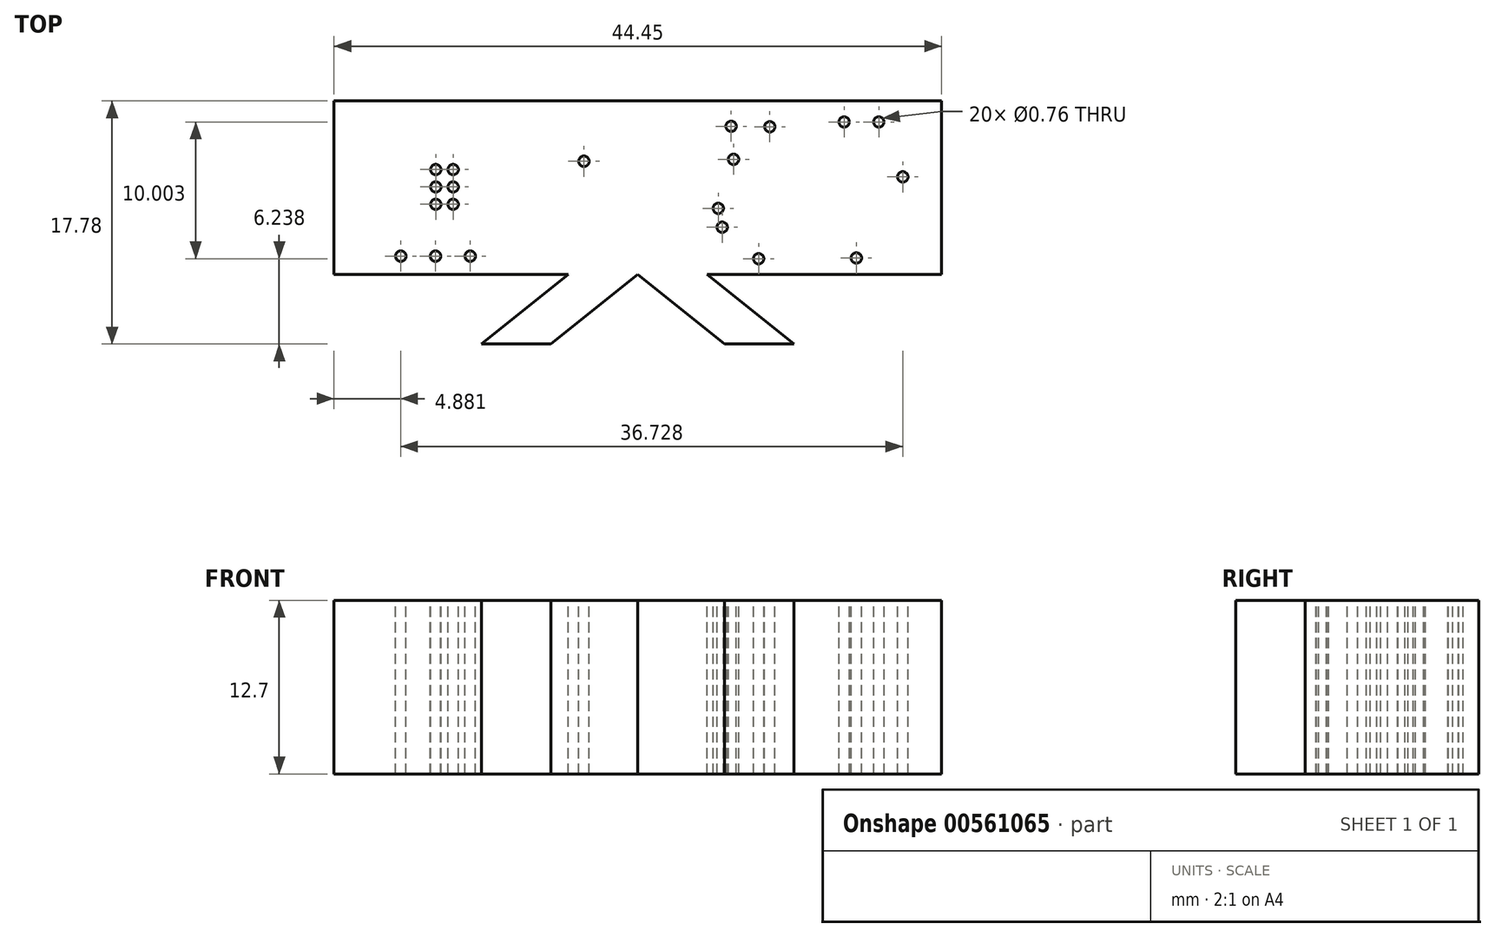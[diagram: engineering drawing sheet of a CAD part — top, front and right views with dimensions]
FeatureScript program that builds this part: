
annotation { "Feature Type Name" : "Feature", "Feature Type Description" : "" }
export const myFeature = defineFeature(function(context is Context, id is Id, definition is map)
    precondition{}
    {
        {
            var Q0;
            Q0=qCreatedBy(makeId("Top.planeOp"),FACE);
            var sketch = newSketch(context, id + "F0", { "sketchPlane" : qUnion([Q0])});
            skArc(sketch, "E0", {"start": v(-12.89, -6) * mm, "mid": v(-13.13, -5.75) * mm, "end": v(-13.37, -6) * mm});
            skArc(sketch, "E1", {"start": v(-13.37, -6) * mm, "mid": v(-13.13, -6.24) * mm, "end": v(-12.89, -6) * mm});
            skArc(sketch, "E2", {"start": v(-15.43, -6) * mm, "mid": v(-15.67, -5.75) * mm, "end": v(-15.91, -6) * mm});
            skArc(sketch, "E3", {"start": v(-15.91, -6) * mm, "mid": v(-15.67, -6.24) * mm, "end": v(-15.43, -6) * mm});
            skArc(sketch, "E4", {"start": v(-17.97, -6) * mm, "mid": v(-18.2, -5.75) * mm, "end": v(-18.45, -6) * mm});
            skArc(sketch, "E5", {"start": v(-18.45, -6) * mm, "mid": v(-18.2, -6.24) * mm, "end": v(-17.97, -6) * mm});
            skArc(sketch, "E6", {"start": v(18.76, -0.2) * mm, "mid": v(18.52, 0.05) * mm, "end": v(18.28, -0.2) * mm});
            skArc(sketch, "E7", {"start": v(18.28, -0.2) * mm, "mid": v(18.52, -0.43) * mm, "end": v(18.76, -0.2) * mm});
            skArc(sketch, "E8", {"start": v(5.26, -2.5) * mm, "mid": v(5.02, -2.26) * mm, "end": v(4.78, -2.5) * mm});
            skArc(sketch, "E9", {"start": v(4.78, -2.5) * mm, "mid": v(5.02, -2.74) * mm, "end": v(5.26, -2.5) * mm});
            skArc(sketch, "E10", {"start": v(5.54, -3.88) * mm, "mid": v(5.3, -3.63) * mm, "end": v(5.06, -3.88) * mm});
            skArc(sketch, "E11", {"start": v(5.06, -3.88) * mm, "mid": v(5.3, -4.12) * mm, "end": v(5.54, -3.88) * mm});
            skArc(sketch, "E12", {"start": v(-4.57, 0.95) * mm, "mid": v(-4.81, 1.19) * mm, "end": v(-5.05, 0.95) * mm});
            skArc(sketch, "E13", {"start": v(-5.05, 0.95) * mm, "mid": v(-4.81, 0.7) * mm, "end": v(-4.57, 0.95) * mm});
            skArc(sketch, "E14", {"start": v(6.2, 3.5) * mm, "mid": v(5.96, 3.75) * mm, "end": v(5.72, 3.5) * mm});
            skArc(sketch, "E15", {"start": v(5.72, 3.5) * mm, "mid": v(5.96, 3.27) * mm, "end": v(6.2, 3.5) * mm});
            skArc(sketch, "E16", {"start": v(9.03, 3.47) * mm, "mid": v(8.79, 3.71) * mm, "end": v(8.54, 3.47) * mm});
            skArc(sketch, "E17", {"start": v(8.54, 3.47) * mm, "mid": v(8.79, 3.23) * mm, "end": v(9.03, 3.47) * mm});
            skArc(sketch, "E18", {"start": v(6.38, 1.09) * mm, "mid": v(6.14, 1.33) * mm, "end": v(5.9, 1.09) * mm});
            skArc(sketch, "E19", {"start": v(5.9, 1.09) * mm, "mid": v(6.14, 0.85) * mm, "end": v(6.38, 1.09) * mm});
            skArc(sketch, "E20", {"start": v(28.86, -23.7) * mm, "mid": v(28.39, -23.22) * mm, "end": v(27.91, -23.7) * mm});
            skArc(sketch, "E21", {"start": v(27.91, -23.7) * mm, "mid": v(28.39, -24.17) * mm, "end": v(28.86, -23.7) * mm});
            skArc(sketch, "E22", {"start": v(26.32, -23.7) * mm, "mid": v(25.85, -23.22) * mm, "end": v(25.37, -23.7) * mm});
            skArc(sketch, "E23", {"start": v(25.37, -23.7) * mm, "mid": v(25.85, -24.17) * mm, "end": v(26.32, -23.7) * mm});
            skArc(sketch, "E24", {"start": v(23.78, -23.7) * mm, "mid": v(23.3, -23.22) * mm, "end": v(22.83, -23.7) * mm});
            skArc(sketch, "E25", {"start": v(22.83, -23.7) * mm, "mid": v(23.3, -24.17) * mm, "end": v(23.78, -23.7) * mm});
            skArc(sketch, "E26", {"start": v(21.24, -23.7) * mm, "mid": v(20.77, -23.22) * mm, "end": v(20.3, -23.7) * mm});
            skArc(sketch, "E27", {"start": v(20.3, -23.7) * mm, "mid": v(20.77, -24.17) * mm, "end": v(21.24, -23.7) * mm});
            skArc(sketch, "E28", {"start": v(18.7, -23.7) * mm, "mid": v(18.23, -23.22) * mm, "end": v(17.75, -23.7) * mm});
            skArc(sketch, "E29", {"start": v(17.75, -23.7) * mm, "mid": v(18.23, -24.17) * mm, "end": v(18.7, -23.7) * mm});
            skArc(sketch, "E30", {"start": v(16.16, -23.7) * mm, "mid": v(15.69, -23.22) * mm, "end": v(15.21, -23.7) * mm});
            skArc(sketch, "E31", {"start": v(15.21, -23.7) * mm, "mid": v(15.69, -24.17) * mm, "end": v(16.16, -23.7) * mm});
            skArc(sketch, "E32", {"start": v(13.62, -23.7) * mm, "mid": v(13.15, -23.22) * mm, "end": v(12.67, -23.7) * mm});
            skArc(sketch, "E33", {"start": v(12.67, -23.7) * mm, "mid": v(13.15, -24.17) * mm, "end": v(13.62, -23.7) * mm});
            skArc(sketch, "E34", {"start": v(11.08, -23.7) * mm, "mid": v(10.6, -23.22) * mm, "end": v(10.13, -23.7) * mm});
            skArc(sketch, "E35", {"start": v(10.13, -23.7) * mm, "mid": v(10.6, -24.17) * mm, "end": v(11.08, -23.7) * mm});
            skArc(sketch, "E36", {"start": v(8.54, -23.7) * mm, "mid": v(8.07, -23.22) * mm, "end": v(7.6, -23.7) * mm});
            skArc(sketch, "E37", {"start": v(7.6, -23.7) * mm, "mid": v(8.07, -24.17) * mm, "end": v(8.54, -23.7) * mm});
            skArc(sketch, "E38", {"start": v(6, -23.7) * mm, "mid": v(5.53, -23.22) * mm, "end": v(5.05, -23.7) * mm});
            skArc(sketch, "E39", {"start": v(5.05, -23.7) * mm, "mid": v(5.53, -24.17) * mm, "end": v(6, -23.7) * mm});
            skArc(sketch, "E40", {"start": v(3.46, -23.7) * mm, "mid": v(2.99, -23.22) * mm, "end": v(2.51, -23.7) * mm});
            skArc(sketch, "E41", {"start": v(2.51, -23.7) * mm, "mid": v(2.99, -24.17) * mm, "end": v(3.46, -23.7) * mm});
            skArc(sketch, "E42", {"start": v(0.92, -23.7) * mm, "mid": v(0.45, -23.22) * mm, "end": v(-0.03, -23.7) * mm});
            skArc(sketch, "E43", {"start": v(-0.03, -23.7) * mm, "mid": v(0.45, -24.17) * mm, "end": v(0.92, -23.7) * mm});
            skArc(sketch, "E44", {"start": v(-1.62, -23.7) * mm, "mid": v(-2.1, -23.22) * mm, "end": v(-2.57, -23.7) * mm});
            skArc(sketch, "E45", {"start": v(-2.57, -23.7) * mm, "mid": v(-2.1, -24.17) * mm, "end": v(-1.62, -23.7) * mm});
            skArc(sketch, "E46", {"start": v(-4.16, -23.7) * mm, "mid": v(-4.63, -23.22) * mm, "end": v(-5.1, -23.7) * mm});
            skArc(sketch, "E47", {"start": v(-5.1, -23.7) * mm, "mid": v(-4.63, -24.17) * mm, "end": v(-4.16, -23.7) * mm});
            skArc(sketch, "E48", {"start": v(-6.7, -23.7) * mm, "mid": v(-7.17, -23.22) * mm, "end": v(-7.65, -23.7) * mm});
            skArc(sketch, "E49", {"start": v(-7.65, -23.7) * mm, "mid": v(-7.17, -24.17) * mm, "end": v(-6.7, -23.7) * mm});
            skArc(sketch, "E50", {"start": v(-9.24, -23.7) * mm, "mid": v(-9.71, -23.22) * mm, "end": v(-10.19, -23.7) * mm});
            skArc(sketch, "E51", {"start": v(-10.19, -23.7) * mm, "mid": v(-9.71, -24.17) * mm, "end": v(-9.24, -23.7) * mm});
            skArc(sketch, "E52", {"start": v(-11.78, -23.7) * mm, "mid": v(-12.25, -23.22) * mm, "end": v(-12.73, -23.7) * mm});
            skArc(sketch, "E53", {"start": v(-12.73, -23.7) * mm, "mid": v(-12.25, -24.17) * mm, "end": v(-11.78, -23.7) * mm});
            skArc(sketch, "E54", {"start": v(-15.4, 0.34) * mm, "mid": v(-15.65, 0.58) * mm, "end": v(-15.89, 0.34) * mm});
            skArc(sketch, "E55", {"start": v(-15.89, 0.34) * mm, "mid": v(-15.65, 0.1) * mm, "end": v(-15.4, 0.34) * mm});
            skArc(sketch, "E56", {"start": v(-14.14, 0.34) * mm, "mid": v(-14.38, 0.58) * mm, "end": v(-14.62, 0.34) * mm});
            skArc(sketch, "E57", {"start": v(-14.62, 0.34) * mm, "mid": v(-14.38, 0.1) * mm, "end": v(-14.14, 0.34) * mm});
            skArc(sketch, "E58", {"start": v(-14.14, -0.93) * mm, "mid": v(-14.38, -0.69) * mm, "end": v(-14.62, -0.93) * mm});
            skArc(sketch, "E59", {"start": v(-14.62, -0.93) * mm, "mid": v(-14.38, -1.17) * mm, "end": v(-14.14, -0.93) * mm});
            skArc(sketch, "E60", {"start": v(-14.14, -2.2) * mm, "mid": v(-14.38, -1.96) * mm, "end": v(-14.62, -2.2) * mm});
            skArc(sketch, "E61", {"start": v(-14.62, -2.2) * mm, "mid": v(-14.38, -2.44) * mm, "end": v(-14.14, -2.2) * mm});
            skArc(sketch, "E62", {"start": v(-15.4, -0.93) * mm, "mid": v(-15.65, -0.69) * mm, "end": v(-15.89, -0.93) * mm});
            skArc(sketch, "E63", {"start": v(-15.89, -0.93) * mm, "mid": v(-15.65, -1.17) * mm, "end": v(-15.4, -0.93) * mm});
            skArc(sketch, "E64", {"start": v(-15.4, -2.2) * mm, "mid": v(-15.65, -1.96) * mm, "end": v(-15.89, -2.2) * mm});
            skArc(sketch, "E65", {"start": v(-15.89, -2.2) * mm, "mid": v(-15.65, -2.44) * mm, "end": v(-15.4, -2.2) * mm});
            skArc(sketch, "E66", {"start": v(37.09, 19.86) * mm, "mid": v(36.61, 20.34) * mm, "end": v(36.13, 19.86) * mm});
            skArc(sketch, "E67", {"start": v(36.13, 19.86) * mm, "mid": v(36.61, 19.38) * mm, "end": v(37.09, 19.86) * mm});
            skArc(sketch, "E68", {"start": v(37.09, 17.32) * mm, "mid": v(36.61, 17.8) * mm, "end": v(36.13, 17.32) * mm});
            skArc(sketch, "E69", {"start": v(36.13, 17.32) * mm, "mid": v(36.61, 16.84) * mm, "end": v(37.09, 17.32) * mm});
            skArc(sketch, "E70", {"start": v(37.09, 14.78) * mm, "mid": v(36.61, 15.26) * mm, "end": v(36.13, 14.78) * mm});
            skArc(sketch, "E71", {"start": v(36.13, 14.78) * mm, "mid": v(36.61, 14.3) * mm, "end": v(37.09, 14.78) * mm});
            skArc(sketch, "E72", {"start": v(37.09, 12.24) * mm, "mid": v(36.61, 12.72) * mm, "end": v(36.13, 12.24) * mm});
            skArc(sketch, "E73", {"start": v(36.13, 12.24) * mm, "mid": v(36.61, 11.76) * mm, "end": v(37.09, 12.24) * mm});
            skArc(sketch, "E74", {"start": v(37.09, 9.7) * mm, "mid": v(36.61, 10.18) * mm, "end": v(36.13, 9.7) * mm});
            skArc(sketch, "E75", {"start": v(36.13, 9.7) * mm, "mid": v(36.61, 9.22) * mm, "end": v(37.09, 9.7) * mm});
            skArc(sketch, "E76", {"start": v(37, -12.53) * mm, "mid": v(36.53, -12.06) * mm, "end": v(36.06, -12.53) * mm});
            skArc(sketch, "E77", {"start": v(36.06, -12.53) * mm, "mid": v(36.53, -13) * mm, "end": v(37, -12.53) * mm});
            skArc(sketch, "E78", {"start": v(17.24, 3.82) * mm, "mid": v(16.76, 4.3) * mm, "end": v(16.29, 3.82) * mm});
            skArc(sketch, "E79", {"start": v(16.29, 3.82) * mm, "mid": v(16.76, 3.34) * mm, "end": v(17.24, 3.82) * mm});
            skArc(sketch, "E80", {"start": v(16.8, 23.69) * mm, "mid": v(16.33, 24.16) * mm, "end": v(15.85, 23.69) * mm});
            skArc(sketch, "E81", {"start": v(15.85, 23.69) * mm, "mid": v(16.33, 23.21) * mm, "end": v(16.8, 23.69) * mm});
            skArc(sketch, "E82", {"start": v(-12.94, -6) * mm, "mid": v(-13.13, -5.8) * mm, "end": v(-13.32, -6) * mm});
            skArc(sketch, "E83", {"start": v(-13.32, -6) * mm, "mid": v(-13.13, -6.18) * mm, "end": v(-12.94, -6) * mm});
            skArc(sketch, "E84", {"start": v(-15.48, -6) * mm, "mid": v(-15.67, -5.8) * mm, "end": v(-15.86, -6) * mm});
            skArc(sketch, "E85", {"start": v(-15.86, -6) * mm, "mid": v(-15.67, -6.18) * mm, "end": v(-15.48, -6) * mm});
            skArc(sketch, "E86", {"start": v(-18.02, -6) * mm, "mid": v(-18.2, -5.8) * mm, "end": v(-18.4, -6) * mm});
            skArc(sketch, "E87", {"start": v(-18.4, -6) * mm, "mid": v(-18.2, -6.18) * mm, "end": v(-18.02, -6) * mm});
            skArc(sketch, "E88", {"start": v(18.7, -0.2) * mm, "mid": v(18.52, 0) * mm, "end": v(18.33, -0.2) * mm});
            skArc(sketch, "E89", {"start": v(18.33, -0.2) * mm, "mid": v(18.52, -0.38) * mm, "end": v(18.7, -0.2) * mm});
            skArc(sketch, "E90", {"start": v(5.2, -2.5) * mm, "mid": v(5.02, -2.3) * mm, "end": v(4.83, -2.5) * mm});
            skArc(sketch, "E91", {"start": v(4.83, -2.5) * mm, "mid": v(5.02, -2.69) * mm, "end": v(5.2, -2.5) * mm});
            skArc(sketch, "E92", {"start": v(5.5, -3.88) * mm, "mid": v(5.3, -3.69) * mm, "end": v(5.11, -3.88) * mm});
            skArc(sketch, "E93", {"start": v(5.11, -3.88) * mm, "mid": v(5.3, -4.07) * mm, "end": v(5.5, -3.88) * mm});
            skArc(sketch, "E94", {"start": v(-4.62, 0.95) * mm, "mid": v(-4.81, 1.14) * mm, "end": v(-5, 0.95) * mm});
            skArc(sketch, "E95", {"start": v(-5, 0.95) * mm, "mid": v(-4.81, 0.76) * mm, "end": v(-4.62, 0.95) * mm});
            skArc(sketch, "E96", {"start": v(6.15, 3.5) * mm, "mid": v(5.96, 3.7) * mm, "end": v(5.77, 3.5) * mm});
            skArc(sketch, "E97", {"start": v(5.77, 3.5) * mm, "mid": v(5.96, 3.32) * mm, "end": v(6.15, 3.5) * mm});
            skArc(sketch, "E98", {"start": v(8.98, 3.47) * mm, "mid": v(8.79, 3.66) * mm, "end": v(8.6, 3.47) * mm});
            skArc(sketch, "E99", {"start": v(8.6, 3.47) * mm, "mid": v(8.79, 3.28) * mm, "end": v(8.98, 3.47) * mm});
            skArc(sketch, "E100", {"start": v(6.33, 1.09) * mm, "mid": v(6.14, 1.28) * mm, "end": v(5.95, 1.09) * mm});
            skArc(sketch, "E101", {"start": v(5.95, 1.09) * mm, "mid": v(6.14, 0.9) * mm, "end": v(6.33, 1.09) * mm});
            skArc(sketch, "E102", {"start": v(28.81, -23.7) * mm, "mid": v(28.39, -23.27) * mm, "end": v(27.97, -23.7) * mm});
            skArc(sketch, "E103", {"start": v(27.97, -23.7) * mm, "mid": v(28.39, -24.11) * mm, "end": v(28.81, -23.7) * mm});
            skArc(sketch, "E104", {"start": v(26.27, -23.7) * mm, "mid": v(25.85, -23.27) * mm, "end": v(25.43, -23.7) * mm});
            skArc(sketch, "E105", {"start": v(25.43, -23.7) * mm, "mid": v(25.85, -24.11) * mm, "end": v(26.27, -23.7) * mm});
            skArc(sketch, "E106", {"start": v(23.73, -23.7) * mm, "mid": v(23.3, -23.27) * mm, "end": v(22.89, -23.7) * mm});
            skArc(sketch, "E107", {"start": v(22.89, -23.7) * mm, "mid": v(23.3, -24.11) * mm, "end": v(23.73, -23.7) * mm});
            skArc(sketch, "E108", {"start": v(21.2, -23.7) * mm, "mid": v(20.77, -23.27) * mm, "end": v(20.35, -23.7) * mm});
            skArc(sketch, "E109", {"start": v(20.35, -23.7) * mm, "mid": v(20.77, -24.11) * mm, "end": v(21.2, -23.7) * mm});
            skArc(sketch, "E110", {"start": v(18.65, -23.7) * mm, "mid": v(18.23, -23.27) * mm, "end": v(17.8, -23.7) * mm});
            skArc(sketch, "E111", {"start": v(17.8, -23.7) * mm, "mid": v(18.23, -24.11) * mm, "end": v(18.65, -23.7) * mm});
            skArc(sketch, "E112", {"start": v(16.11, -23.7) * mm, "mid": v(15.69, -23.27) * mm, "end": v(15.27, -23.7) * mm});
            skArc(sketch, "E113", {"start": v(15.27, -23.7) * mm, "mid": v(15.69, -24.11) * mm, "end": v(16.11, -23.7) * mm});
            skArc(sketch, "E114", {"start": v(13.57, -23.7) * mm, "mid": v(13.15, -23.27) * mm, "end": v(12.73, -23.7) * mm});
            skArc(sketch, "E115", {"start": v(12.73, -23.7) * mm, "mid": v(13.15, -24.11) * mm, "end": v(13.57, -23.7) * mm});
            skArc(sketch, "E116", {"start": v(11.03, -23.7) * mm, "mid": v(10.6, -23.27) * mm, "end": v(10.19, -23.7) * mm});
            skArc(sketch, "E117", {"start": v(10.19, -23.7) * mm, "mid": v(10.6, -24.11) * mm, "end": v(11.03, -23.7) * mm});
            skArc(sketch, "E118", {"start": v(8.5, -23.7) * mm, "mid": v(8.07, -23.27) * mm, "end": v(7.65, -23.7) * mm});
            skArc(sketch, "E119", {"start": v(7.65, -23.7) * mm, "mid": v(8.07, -24.11) * mm, "end": v(8.5, -23.7) * mm});
            skArc(sketch, "E120", {"start": v(5.95, -23.7) * mm, "mid": v(5.53, -23.27) * mm, "end": v(5.1, -23.7) * mm});
            skArc(sketch, "E121", {"start": v(5.1, -23.7) * mm, "mid": v(5.53, -24.11) * mm, "end": v(5.95, -23.7) * mm});
            skArc(sketch, "E122", {"start": v(3.41, -23.7) * mm, "mid": v(2.99, -23.27) * mm, "end": v(2.57, -23.7) * mm});
            skArc(sketch, "E123", {"start": v(2.57, -23.7) * mm, "mid": v(2.99, -24.11) * mm, "end": v(3.41, -23.7) * mm});
            skArc(sketch, "E124", {"start": v(0.87, -23.7) * mm, "mid": v(0.45, -23.27) * mm, "end": v(0.03, -23.7) * mm});
            skArc(sketch, "E125", {"start": v(0.03, -23.7) * mm, "mid": v(0.45, -24.11) * mm, "end": v(0.87, -23.7) * mm});
            skArc(sketch, "E126", {"start": v(-1.67, -23.7) * mm, "mid": v(-2.1, -23.27) * mm, "end": v(-2.51, -23.7) * mm});
            skArc(sketch, "E127", {"start": v(-2.51, -23.7) * mm, "mid": v(-2.1, -24.11) * mm, "end": v(-1.67, -23.7) * mm});
            skArc(sketch, "E128", {"start": v(-4.2, -23.7) * mm, "mid": v(-4.63, -23.27) * mm, "end": v(-5.05, -23.7) * mm});
            skArc(sketch, "E129", {"start": v(-5.05, -23.7) * mm, "mid": v(-4.63, -24.11) * mm, "end": v(-4.2, -23.7) * mm});
            skArc(sketch, "E130", {"start": v(-6.75, -23.7) * mm, "mid": v(-7.17, -23.27) * mm, "end": v(-7.6, -23.7) * mm});
            skArc(sketch, "E131", {"start": v(-7.6, -23.7) * mm, "mid": v(-7.17, -24.11) * mm, "end": v(-6.75, -23.7) * mm});
            skArc(sketch, "E132", {"start": v(-9.29, -23.7) * mm, "mid": v(-9.71, -23.27) * mm, "end": v(-10.13, -23.7) * mm});
            skArc(sketch, "E133", {"start": v(-10.13, -23.7) * mm, "mid": v(-9.71, -24.11) * mm, "end": v(-9.29, -23.7) * mm});
            skArc(sketch, "E134", {"start": v(-11.83, -23.7) * mm, "mid": v(-12.25, -23.27) * mm, "end": v(-12.67, -23.7) * mm});
            skArc(sketch, "E135", {"start": v(-12.67, -23.7) * mm, "mid": v(-12.25, -24.11) * mm, "end": v(-11.83, -23.7) * mm});
            skArc(sketch, "E136", {"start": v(-15.46, 0.34) * mm, "mid": v(-15.65, 0.53) * mm, "end": v(-15.84, 0.34) * mm});
            skArc(sketch, "E137", {"start": v(-15.84, 0.34) * mm, "mid": v(-15.65, 0.15) * mm, "end": v(-15.46, 0.34) * mm});
            skArc(sketch, "E138", {"start": v(-14.19, 0.34) * mm, "mid": v(-14.38, 0.53) * mm, "end": v(-14.57, 0.34) * mm});
            skArc(sketch, "E139", {"start": v(-14.57, 0.34) * mm, "mid": v(-14.38, 0.15) * mm, "end": v(-14.19, 0.34) * mm});
            skArc(sketch, "E140", {"start": v(-14.19, -0.93) * mm, "mid": v(-14.38, -0.74) * mm, "end": v(-14.57, -0.93) * mm});
            skArc(sketch, "E141", {"start": v(-14.57, -0.93) * mm, "mid": v(-14.38, -1.12) * mm, "end": v(-14.19, -0.93) * mm});
            skArc(sketch, "E142", {"start": v(-14.19, -2.2) * mm, "mid": v(-14.38, -2) * mm, "end": v(-14.57, -2.2) * mm});
            skArc(sketch, "E143", {"start": v(-14.57, -2.2) * mm, "mid": v(-14.38, -2.39) * mm, "end": v(-14.19, -2.2) * mm});
            skArc(sketch, "E144", {"start": v(-15.46, -0.93) * mm, "mid": v(-15.65, -0.74) * mm, "end": v(-15.84, -0.93) * mm});
            skArc(sketch, "E145", {"start": v(-15.84, -0.93) * mm, "mid": v(-15.65, -1.12) * mm, "end": v(-15.46, -0.93) * mm});
            skArc(sketch, "E146", {"start": v(-15.46, -2.2) * mm, "mid": v(-15.65, -2) * mm, "end": v(-15.84, -2.2) * mm});
            skArc(sketch, "E147", {"start": v(-15.84, -2.2) * mm, "mid": v(-15.65, -2.39) * mm, "end": v(-15.46, -2.2) * mm});
            skArc(sketch, "E148", {"start": v(37.04, 19.86) * mm, "mid": v(36.61, 20.29) * mm, "end": v(36.18, 19.86) * mm});
            skArc(sketch, "E149", {"start": v(36.18, 19.86) * mm, "mid": v(36.61, 19.43) * mm, "end": v(37.04, 19.86) * mm});
            skArc(sketch, "E150", {"start": v(37.04, 17.32) * mm, "mid": v(36.61, 17.75) * mm, "end": v(36.18, 17.32) * mm});
            skArc(sketch, "E151", {"start": v(36.18, 17.32) * mm, "mid": v(36.61, 16.9) * mm, "end": v(37.04, 17.32) * mm});
            skArc(sketch, "E152", {"start": v(37.04, 14.78) * mm, "mid": v(36.61, 15.2) * mm, "end": v(36.18, 14.78) * mm});
            skArc(sketch, "E153", {"start": v(36.18, 14.78) * mm, "mid": v(36.61, 14.35) * mm, "end": v(37.04, 14.78) * mm});
            skArc(sketch, "E154", {"start": v(37.04, 12.24) * mm, "mid": v(36.61, 12.67) * mm, "end": v(36.18, 12.24) * mm});
            skArc(sketch, "E155", {"start": v(36.18, 12.24) * mm, "mid": v(36.61, 11.81) * mm, "end": v(37.04, 12.24) * mm});
            skArc(sketch, "E156", {"start": v(37.04, 9.7) * mm, "mid": v(36.61, 10.13) * mm, "end": v(36.18, 9.7) * mm});
            skArc(sketch, "E157", {"start": v(36.18, 9.7) * mm, "mid": v(36.61, 9.27) * mm, "end": v(37.04, 9.7) * mm});
            skArc(sketch, "E158", {"start": v(36.95, -12.53) * mm, "mid": v(36.53, -12.1) * mm, "end": v(36.1, -12.53) * mm});
            skArc(sketch, "E159", {"start": v(36.1, -12.53) * mm, "mid": v(36.53, -12.96) * mm, "end": v(36.95, -12.53) * mm});
            skArc(sketch, "E160", {"start": v(17.19, 3.82) * mm, "mid": v(16.76, 4.25) * mm, "end": v(16.34, 3.82) * mm});
            skArc(sketch, "E161", {"start": v(16.34, 3.82) * mm, "mid": v(16.76, 3.4) * mm, "end": v(17.19, 3.82) * mm});
            skArc(sketch, "E162", {"start": v(16.75, 23.69) * mm, "mid": v(16.33, 24.1) * mm, "end": v(15.9, 23.69) * mm});
            skArc(sketch, "E163", {"start": v(15.9, 23.69) * mm, "mid": v(16.33, 23.26) * mm, "end": v(16.75, 23.69) * mm});
            skLineSegment(sketch, "E164", {"start": v(15.12, -6.13) * mm, "end": v(15.12, -7.88) * mm});
            skArc(sketch, "E165", {"start": v(15.08, -6.13) * mm, "mid": v(15.12, -6.16) * mm, "end": v(15.16, -6.13) * mm});
            skArc(sketch, "E166", {"start": v(15.16, -6.13) * mm, "mid": v(15.12, -6.09) * mm, "end": v(15.08, -6.13) * mm});
            skArc(sketch, "E167", {"start": v(15.08, -7.88) * mm, "mid": v(15.12, -7.92) * mm, "end": v(15.16, -7.88) * mm});
            skArc(sketch, "E168", {"start": v(15.16, -7.88) * mm, "mid": v(15.12, -7.84) * mm, "end": v(15.08, -7.88) * mm});
            skLineSegment(sketch, "E169", {"start": v(15.12, -7.88) * mm, "end": v(30.93, -23.7) * mm});
            skArc(sketch, "E170", {"start": v(30.9, -23.7) * mm, "mid": v(30.93, -23.73) * mm, "end": v(30.97, -23.7) * mm});
            skArc(sketch, "E171", {"start": v(30.97, -23.7) * mm, "mid": v(30.93, -23.65) * mm, "end": v(30.9, -23.7) * mm});
            skLineSegment(sketch, "E172", {"start": v(15.12, -6.13) * mm, "end": v(30.12, -6.13) * mm});
            skArc(sketch, "E173", {"start": v(30.09, -6.13) * mm, "mid": v(30.12, -6.16) * mm, "end": v(30.16, -6.13) * mm});
            skArc(sketch, "E174", {"start": v(30.16, -6.13) * mm, "mid": v(30.12, -6.09) * mm, "end": v(30.09, -6.13) * mm});
            skLineSegment(sketch, "E175", {"start": v(30.12, -6.13) * mm, "end": v(36.53, -12.53) * mm});
            skArc(sketch, "E176", {"start": v(36.5, -12.53) * mm, "mid": v(36.53, -12.57) * mm, "end": v(36.57, -12.53) * mm});
            skArc(sketch, "E177", {"start": v(36.57, -12.53) * mm, "mid": v(36.53, -12.5) * mm, "end": v(36.5, -12.53) * mm});
            skLineSegment(sketch, "E178", {"start": v(-14.38, -0.93) * mm, "end": v(-14.24, -0.93) * mm});
            skArc(sketch, "E179", {"start": v(-14.41, -0.93) * mm, "mid": v(-14.38, -0.97) * mm, "end": v(-14.34, -0.93) * mm});
            skArc(sketch, "E180", {"start": v(-14.34, -0.93) * mm, "mid": v(-14.38, -0.89) * mm, "end": v(-14.41, -0.93) * mm});
            skArc(sketch, "E181", {"start": v(-14.28, -0.93) * mm, "mid": v(-14.24, -0.97) * mm, "end": v(-14.2, -0.93) * mm});
            skArc(sketch, "E182", {"start": v(-14.2, -0.93) * mm, "mid": v(-14.24, -0.89) * mm, "end": v(-14.28, -0.93) * mm});
            skLineSegment(sketch, "E183", {"start": v(-14.24, -0.93) * mm, "end": v(-14.01, -0.7) * mm});
            skArc(sketch, "E184", {"start": v(-14.05, -0.7) * mm, "mid": v(-14.01, -0.73) * mm, "end": v(-13.97, -0.7) * mm});
            skArc(sketch, "E185", {"start": v(-13.97, -0.7) * mm, "mid": v(-14.01, -0.66) * mm, "end": v(-14.05, -0.7) * mm});
            skLineSegment(sketch, "E186", {"start": v(-14.01, -0.7) * mm, "end": v(-12.24, -0.7) * mm});
            skArc(sketch, "E187", {"start": v(-12.28, -0.7) * mm, "mid": v(-12.24, -0.73) * mm, "end": v(-12.2, -0.7) * mm});
            skArc(sketch, "E188", {"start": v(-12.2, -0.7) * mm, "mid": v(-12.24, -0.66) * mm, "end": v(-12.28, -0.7) * mm});
            skLineSegment(sketch, "E189", {"start": v(-12.24, -0.7) * mm, "end": v(-8.8, -4.14) * mm});
            skArc(sketch, "E190", {"start": v(-8.83, -4.14) * mm, "mid": v(-8.8, -4.18) * mm, "end": v(-8.76, -4.14) * mm});
            skArc(sketch, "E191", {"start": v(-8.76, -4.14) * mm, "mid": v(-8.8, -4.1) * mm, "end": v(-8.83, -4.14) * mm});
            skLineSegment(sketch, "E192", {"start": v(-8.8, -4.14) * mm, "end": v(-8.8, -9.37) * mm});
            skArc(sketch, "E193", {"start": v(-8.83, -9.37) * mm, "mid": v(-8.8, -9.4) * mm, "end": v(-8.76, -9.37) * mm});
            skArc(sketch, "E194", {"start": v(-8.76, -9.37) * mm, "mid": v(-8.8, -9.33) * mm, "end": v(-8.83, -9.37) * mm});
            skLineSegment(sketch, "E195", {"start": v(-8.8, -9.37) * mm, "end": v(5.53, -23.7) * mm});
            skArc(sketch, "E196", {"start": v(5.5, -23.7) * mm, "mid": v(5.53, -23.73) * mm, "end": v(5.57, -23.7) * mm});
            skArc(sketch, "E197", {"start": v(5.57, -23.7) * mm, "mid": v(5.53, -23.65) * mm, "end": v(5.5, -23.7) * mm});
            skLineSegment(sketch, "E198", {"start": v(7.97, -6.18) * mm, "end": v(10.72, -6.18) * mm});
            skArc(sketch, "E199", {"start": v(7.93, -6.18) * mm, "mid": v(7.97, -6.22) * mm, "end": v(8.01, -6.18) * mm});
            skArc(sketch, "E200", {"start": v(8.01, -6.18) * mm, "mid": v(7.97, -6.14) * mm, "end": v(7.93, -6.18) * mm});
            skArc(sketch, "E201", {"start": v(10.68, -6.18) * mm, "mid": v(10.72, -6.22) * mm, "end": v(10.75, -6.18) * mm});
            skArc(sketch, "E202", {"start": v(10.75, -6.18) * mm, "mid": v(10.72, -6.14) * mm, "end": v(10.68, -6.18) * mm});
            skLineSegment(sketch, "E203", {"start": v(10.72, -6.18) * mm, "end": v(13.39, -8.85) * mm});
            skArc(sketch, "E204", {"start": v(13.35, -8.85) * mm, "mid": v(13.39, -8.9) * mm, "end": v(13.42, -8.85) * mm});
            skArc(sketch, "E205", {"start": v(13.42, -8.85) * mm, "mid": v(13.39, -8.82) * mm, "end": v(13.35, -8.85) * mm});
            skLineSegment(sketch, "E206", {"start": v(13.39, -8.85) * mm, "end": v(13.55, -8.85) * mm});
            skArc(sketch, "E207", {"start": v(13.52, -8.85) * mm, "mid": v(13.55, -8.9) * mm, "end": v(13.6, -8.85) * mm});
            skArc(sketch, "E208", {"start": v(13.6, -8.85) * mm, "mid": v(13.55, -8.82) * mm, "end": v(13.52, -8.85) * mm});
            skLineSegment(sketch, "E209", {"start": v(13.55, -8.85) * mm, "end": v(28.39, -23.7) * mm});
            skArc(sketch, "E210", {"start": v(28.35, -23.7) * mm, "mid": v(28.39, -23.73) * mm, "end": v(28.43, -23.7) * mm});
            skArc(sketch, "E211", {"start": v(28.43, -23.7) * mm, "mid": v(28.39, -23.65) * mm, "end": v(28.35, -23.7) * mm});
            skLineSegment(sketch, "E212", {"start": v(7.97, -6.18) * mm, "end": v(12.31, -6.18) * mm});
            skArc(sketch, "E213", {"start": v(12.28, -6.18) * mm, "mid": v(12.31, -6.22) * mm, "end": v(12.35, -6.18) * mm});
            skArc(sketch, "E214", {"start": v(12.35, -6.18) * mm, "mid": v(12.31, -6.14) * mm, "end": v(12.28, -6.18) * mm});
            skLineSegment(sketch, "E215", {"start": v(12.31, -6.18) * mm, "end": v(14.23, -4.26) * mm});
            skArc(sketch, "E216", {"start": v(14.2, -4.26) * mm, "mid": v(14.23, -4.3) * mm, "end": v(14.27, -4.26) * mm});
            skArc(sketch, "E217", {"start": v(14.27, -4.26) * mm, "mid": v(14.23, -4.22) * mm, "end": v(14.2, -4.26) * mm});
            skLineSegment(sketch, "E218", {"start": v(14.23, -4.26) * mm, "end": v(30.8, -4.26) * mm});
            skArc(sketch, "E219", {"start": v(30.76, -4.26) * mm, "mid": v(30.8, -4.3) * mm, "end": v(30.84, -4.26) * mm});
            skArc(sketch, "E220", {"start": v(30.84, -4.26) * mm, "mid": v(30.8, -4.22) * mm, "end": v(30.76, -4.26) * mm});
            skLineSegment(sketch, "E221", {"start": v(30.8, -4.26) * mm, "end": v(36.53, -10) * mm});
            skArc(sketch, "E222", {"start": v(36.5, -10) * mm, "mid": v(36.53, -10.03) * mm, "end": v(36.57, -10) * mm});
            skArc(sketch, "E223", {"start": v(36.57, -10) * mm, "mid": v(36.53, -9.95) * mm, "end": v(36.5, -10) * mm});
            skLineSegment(sketch, "E224", {"start": v(18.52, -0.2) * mm, "end": v(12, -0.2) * mm});
            skArc(sketch, "E225", {"start": v(18.48, -0.2) * mm, "mid": v(18.52, -0.23) * mm, "end": v(18.56, -0.2) * mm});
            skArc(sketch, "E226", {"start": v(18.56, -0.2) * mm, "mid": v(18.52, -0.15) * mm, "end": v(18.48, -0.2) * mm});
            skArc(sketch, "E227", {"start": v(11.97, -0.2) * mm, "mid": v(12, -0.23) * mm, "end": v(12.04, -0.2) * mm});
            skArc(sketch, "E228", {"start": v(12.04, -0.2) * mm, "mid": v(12, -0.15) * mm, "end": v(11.97, -0.2) * mm});
            skLineSegment(sketch, "E229", {"start": v(12, -0.2) * mm, "end": v(6.55, -5.65) * mm});
            skArc(sketch, "E230", {"start": v(6.5, -5.65) * mm, "mid": v(6.55, -5.69) * mm, "end": v(6.58, -5.65) * mm});
            skArc(sketch, "E231", {"start": v(6.58, -5.65) * mm, "mid": v(6.55, -5.61) * mm, "end": v(6.5, -5.65) * mm});
            skLineSegment(sketch, "E232", {"start": v(6.55, -5.65) * mm, "end": v(6.55, -6.96) * mm});
            skArc(sketch, "E233", {"start": v(6.5, -6.96) * mm, "mid": v(6.55, -7) * mm, "end": v(6.58, -6.96) * mm});
            skArc(sketch, "E234", {"start": v(6.58, -6.96) * mm, "mid": v(6.55, -6.92) * mm, "end": v(6.5, -6.96) * mm});
            skLineSegment(sketch, "E235", {"start": v(6.55, -6.96) * mm, "end": v(7.84, -8.25) * mm});
            skArc(sketch, "E236", {"start": v(7.8, -8.25) * mm, "mid": v(7.84, -8.3) * mm, "end": v(7.87, -8.25) * mm});
            skArc(sketch, "E237", {"start": v(7.87, -8.25) * mm, "mid": v(7.84, -8.21) * mm, "end": v(7.8, -8.25) * mm});
            skLineSegment(sketch, "E238", {"start": v(7.84, -8.25) * mm, "end": v(10.34, -8.25) * mm});
            skArc(sketch, "E239", {"start": v(10.3, -8.25) * mm, "mid": v(10.34, -8.3) * mm, "end": v(10.38, -8.25) * mm});
            skArc(sketch, "E240", {"start": v(10.38, -8.25) * mm, "mid": v(10.34, -8.21) * mm, "end": v(10.3, -8.25) * mm});
            skLineSegment(sketch, "E241", {"start": v(10.34, -8.25) * mm, "end": v(23.07, -20.98) * mm});
            skArc(sketch, "E242", {"start": v(23.04, -20.98) * mm, "mid": v(23.07, -21.02) * mm, "end": v(23.11, -20.98) * mm});
            skArc(sketch, "E243", {"start": v(23.11, -20.98) * mm, "mid": v(23.07, -20.94) * mm, "end": v(23.04, -20.98) * mm});
            skLineSegment(sketch, "E244", {"start": v(23.07, -20.98) * mm, "end": v(23.14, -20.98) * mm});
            skArc(sketch, "E245", {"start": v(23.1, -20.98) * mm, "mid": v(23.14, -21.02) * mm, "end": v(23.18, -20.98) * mm});
            skArc(sketch, "E246", {"start": v(23.18, -20.98) * mm, "mid": v(23.14, -20.94) * mm, "end": v(23.1, -20.98) * mm});
            skLineSegment(sketch, "E247", {"start": v(23.14, -20.98) * mm, "end": v(25.85, -23.7) * mm});
            skArc(sketch, "E248", {"start": v(25.81, -23.7) * mm, "mid": v(25.85, -23.73) * mm, "end": v(25.89, -23.7) * mm});
            skArc(sketch, "E249", {"start": v(25.89, -23.7) * mm, "mid": v(25.85, -23.65) * mm, "end": v(25.81, -23.7) * mm});
            skLineSegment(sketch, "E250", {"start": v(8.79, 3.47) * mm, "end": v(8.79, -2.32) * mm});
            skArc(sketch, "E251", {"start": v(8.75, 3.47) * mm, "mid": v(8.79, 3.43) * mm, "end": v(8.82, 3.47) * mm});
            skArc(sketch, "E252", {"start": v(8.82, 3.47) * mm, "mid": v(8.79, 3.5) * mm, "end": v(8.75, 3.47) * mm});
            skArc(sketch, "E253", {"start": v(8.75, -2.32) * mm, "mid": v(8.79, -2.36) * mm, "end": v(8.82, -2.32) * mm});
            skArc(sketch, "E254", {"start": v(8.82, -2.32) * mm, "mid": v(8.79, -2.28) * mm, "end": v(8.75, -2.32) * mm});
            skLineSegment(sketch, "E255", {"start": v(8.79, -2.32) * mm, "end": v(4.84, -6.27) * mm});
            skArc(sketch, "E256", {"start": v(4.8, -6.27) * mm, "mid": v(4.84, -6.3) * mm, "end": v(4.88, -6.27) * mm});
            skArc(sketch, "E257", {"start": v(4.88, -6.27) * mm, "mid": v(4.84, -6.23) * mm, "end": v(4.8, -6.27) * mm});
            skLineSegment(sketch, "E258", {"start": v(4.84, -6.27) * mm, "end": v(4.84, -6.38) * mm});
            skArc(sketch, "E259", {"start": v(4.8, -6.38) * mm, "mid": v(4.84, -6.41) * mm, "end": v(4.88, -6.38) * mm});
            skArc(sketch, "E260", {"start": v(4.88, -6.38) * mm, "mid": v(4.84, -6.34) * mm, "end": v(4.8, -6.38) * mm});
            skLineSegment(sketch, "E261", {"start": v(4.84, -6.38) * mm, "end": v(7.43, -8.97) * mm});
            skArc(sketch, "E262", {"start": v(7.4, -8.97) * mm, "mid": v(7.43, -9) * mm, "end": v(7.47, -8.97) * mm});
            skArc(sketch, "E263", {"start": v(7.47, -8.97) * mm, "mid": v(7.43, -8.93) * mm, "end": v(7.4, -8.97) * mm});
            skLineSegment(sketch, "E264", {"start": v(7.43, -8.97) * mm, "end": v(8.57, -8.97) * mm});
            skArc(sketch, "E265", {"start": v(8.53, -8.97) * mm, "mid": v(8.57, -9) * mm, "end": v(8.61, -8.97) * mm});
            skArc(sketch, "E266", {"start": v(8.61, -8.97) * mm, "mid": v(8.57, -8.93) * mm, "end": v(8.53, -8.97) * mm});
            skLineSegment(sketch, "E267", {"start": v(8.57, -8.97) * mm, "end": v(9.38, -9.77) * mm});
            skArc(sketch, "E268", {"start": v(9.34, -9.77) * mm, "mid": v(9.38, -9.81) * mm, "end": v(9.42, -9.77) * mm});
            skArc(sketch, "E269", {"start": v(9.42, -9.77) * mm, "mid": v(9.38, -9.74) * mm, "end": v(9.34, -9.77) * mm});
            skLineSegment(sketch, "E270", {"start": v(9.38, -9.77) * mm, "end": v(9.4, -9.77) * mm});
            skArc(sketch, "E271", {"start": v(9.35, -9.77) * mm, "mid": v(9.4, -9.81) * mm, "end": v(9.43, -9.77) * mm});
            skArc(sketch, "E272", {"start": v(9.43, -9.77) * mm, "mid": v(9.4, -9.74) * mm, "end": v(9.35, -9.77) * mm});
            skLineSegment(sketch, "E273", {"start": v(9.4, -9.77) * mm, "end": v(23.3, -23.7) * mm});
            skArc(sketch, "E274", {"start": v(23.27, -23.7) * mm, "mid": v(23.3, -23.73) * mm, "end": v(23.35, -23.7) * mm});
            skArc(sketch, "E275", {"start": v(23.35, -23.7) * mm, "mid": v(23.3, -23.65) * mm, "end": v(23.27, -23.7) * mm});
            skLineSegment(sketch, "E276", {"start": v(5.3, -3.88) * mm, "end": v(5.08, -3.88) * mm});
            skArc(sketch, "E277", {"start": v(5.27, -3.88) * mm, "mid": v(5.3, -3.91) * mm, "end": v(5.34, -3.88) * mm});
            skArc(sketch, "E278", {"start": v(5.34, -3.88) * mm, "mid": v(5.3, -3.84) * mm, "end": v(5.27, -3.88) * mm});
            skArc(sketch, "E279", {"start": v(5.04, -3.88) * mm, "mid": v(5.08, -3.91) * mm, "end": v(5.12, -3.88) * mm});
            skArc(sketch, "E280", {"start": v(5.12, -3.88) * mm, "mid": v(5.08, -3.84) * mm, "end": v(5.04, -3.88) * mm});
            skLineSegment(sketch, "E281", {"start": v(5.08, -3.88) * mm, "end": v(3.66, -5.3) * mm});
            skArc(sketch, "E282", {"start": v(3.62, -5.3) * mm, "mid": v(3.66, -5.34) * mm, "end": v(3.7, -5.3) * mm});
            skArc(sketch, "E283", {"start": v(3.7, -5.3) * mm, "mid": v(3.66, -5.26) * mm, "end": v(3.62, -5.3) * mm});
            skLineSegment(sketch, "E284", {"start": v(3.66, -5.3) * mm, "end": v(3.66, -6.6) * mm});
            skArc(sketch, "E285", {"start": v(3.62, -6.6) * mm, "mid": v(3.66, -6.63) * mm, "end": v(3.7, -6.6) * mm});
            skArc(sketch, "E286", {"start": v(3.7, -6.6) * mm, "mid": v(3.66, -6.56) * mm, "end": v(3.62, -6.6) * mm});
            skLineSegment(sketch, "E287", {"start": v(3.66, -6.6) * mm, "end": v(16.5, -19.44) * mm});
            skArc(sketch, "E288", {"start": v(16.47, -19.44) * mm, "mid": v(16.5, -19.48) * mm, "end": v(16.55, -19.44) * mm});
            skArc(sketch, "E289", {"start": v(16.55, -19.44) * mm, "mid": v(16.5, -19.4) * mm, "end": v(16.47, -19.44) * mm});
            skLineSegment(sketch, "E290", {"start": v(16.5, -19.44) * mm, "end": v(16.52, -19.44) * mm});
            skArc(sketch, "E291", {"start": v(16.48, -19.44) * mm, "mid": v(16.52, -19.48) * mm, "end": v(16.56, -19.44) * mm});
            skArc(sketch, "E292", {"start": v(16.56, -19.44) * mm, "mid": v(16.52, -19.4) * mm, "end": v(16.48, -19.44) * mm});
            skLineSegment(sketch, "E293", {"start": v(16.52, -19.44) * mm, "end": v(20.77, -23.7) * mm});
            skArc(sketch, "E294", {"start": v(20.73, -23.7) * mm, "mid": v(20.77, -23.73) * mm, "end": v(20.8, -23.7) * mm});
            skArc(sketch, "E295", {"start": v(20.8, -23.7) * mm, "mid": v(20.77, -23.65) * mm, "end": v(20.73, -23.7) * mm});
            skLineSegment(sketch, "E296", {"start": v(5.02, -2.5) * mm, "end": v(5.02, -2.76) * mm});
            skArc(sketch, "E297", {"start": v(4.98, -2.5) * mm, "mid": v(5.02, -2.54) * mm, "end": v(5.06, -2.5) * mm});
            skArc(sketch, "E298", {"start": v(5.06, -2.5) * mm, "mid": v(5.02, -2.46) * mm, "end": v(4.98, -2.5) * mm});
            skArc(sketch, "E299", {"start": v(4.98, -2.76) * mm, "mid": v(5.02, -2.8) * mm, "end": v(5.06, -2.76) * mm});
            skArc(sketch, "E300", {"start": v(5.06, -2.76) * mm, "mid": v(5.02, -2.73) * mm, "end": v(4.98, -2.76) * mm});
            skLineSegment(sketch, "E301", {"start": v(5.02, -2.76) * mm, "end": v(1.15, -6.63) * mm});
            skArc(sketch, "E302", {"start": v(1.11, -6.63) * mm, "mid": v(1.15, -6.67) * mm, "end": v(1.19, -6.63) * mm});
            skArc(sketch, "E303", {"start": v(1.19, -6.63) * mm, "mid": v(1.15, -6.6) * mm, "end": v(1.11, -6.63) * mm});
            skLineSegment(sketch, "E304", {"start": v(1.15, -6.63) * mm, "end": v(6.99, -12.47) * mm});
            skArc(sketch, "E305", {"start": v(6.95, -12.47) * mm, "mid": v(6.99, -12.5) * mm, "end": v(7.03, -12.47) * mm});
            skArc(sketch, "E306", {"start": v(7.03, -12.47) * mm, "mid": v(6.99, -12.43) * mm, "end": v(6.95, -12.47) * mm});
            skLineSegment(sketch, "E307", {"start": v(6.99, -12.47) * mm, "end": v(7.01, -12.47) * mm});
            skArc(sketch, "E308", {"start": v(6.97, -12.47) * mm, "mid": v(7.01, -12.5) * mm, "end": v(7.05, -12.47) * mm});
            skArc(sketch, "E309", {"start": v(7.05, -12.47) * mm, "mid": v(7.01, -12.43) * mm, "end": v(6.97, -12.47) * mm});
            skLineSegment(sketch, "E310", {"start": v(7.01, -12.47) * mm, "end": v(18.23, -23.7) * mm});
            skArc(sketch, "E311", {"start": v(18.2, -23.7) * mm, "mid": v(18.23, -23.73) * mm, "end": v(18.27, -23.7) * mm});
            skArc(sketch, "E312", {"start": v(18.27, -23.7) * mm, "mid": v(18.23, -23.65) * mm, "end": v(18.2, -23.7) * mm});
            skLineSegment(sketch, "E313", {"start": v(6.14, 1.09) * mm, "end": v(5.96, 1.09) * mm});
            skArc(sketch, "E314", {"start": v(6.1, 1.09) * mm, "mid": v(6.14, 1.05) * mm, "end": v(6.18, 1.09) * mm});
            skArc(sketch, "E315", {"start": v(6.18, 1.09) * mm, "mid": v(6.14, 1.13) * mm, "end": v(6.1, 1.09) * mm});
            skArc(sketch, "E316", {"start": v(5.92, 1.09) * mm, "mid": v(5.96, 1.05) * mm, "end": v(6, 1.09) * mm});
            skArc(sketch, "E317", {"start": v(6, 1.09) * mm, "mid": v(5.96, 1.13) * mm, "end": v(5.92, 1.09) * mm});
            skLineSegment(sketch, "E318", {"start": v(5.96, 1.09) * mm, "end": v(-1.29, -6.16) * mm});
            skArc(sketch, "E319", {"start": v(-1.33, -6.16) * mm, "mid": v(-1.29, -6.2) * mm, "end": v(-1.25, -6.16) * mm});
            skArc(sketch, "E320", {"start": v(-1.25, -6.16) * mm, "mid": v(-1.29, -6.12) * mm, "end": v(-1.33, -6.16) * mm});
            skLineSegment(sketch, "E321", {"start": v(-1.29, -6.16) * mm, "end": v(-1.29, -6.7) * mm});
            skArc(sketch, "E322", {"start": v(-1.33, -6.7) * mm, "mid": v(-1.29, -6.73) * mm, "end": v(-1.25, -6.7) * mm});
            skArc(sketch, "E323", {"start": v(-1.25, -6.7) * mm, "mid": v(-1.29, -6.65) * mm, "end": v(-1.33, -6.7) * mm});
            skLineSegment(sketch, "E324", {"start": v(-1.29, -6.7) * mm, "end": v(6.29, -14.27) * mm});
            skArc(sketch, "E325", {"start": v(6.25, -14.27) * mm, "mid": v(6.29, -14.3) * mm, "end": v(6.33, -14.27) * mm});
            skArc(sketch, "E326", {"start": v(6.33, -14.27) * mm, "mid": v(6.29, -14.23) * mm, "end": v(6.25, -14.27) * mm});
            skLineSegment(sketch, "E327", {"start": v(6.29, -14.27) * mm, "end": v(6.29, -14.3) * mm});
            skArc(sketch, "E328", {"start": v(6.25, -14.3) * mm, "mid": v(6.29, -14.33) * mm, "end": v(6.33, -14.3) * mm});
            skArc(sketch, "E329", {"start": v(6.33, -14.3) * mm, "mid": v(6.29, -14.25) * mm, "end": v(6.25, -14.3) * mm});
            skLineSegment(sketch, "E330", {"start": v(6.29, -14.3) * mm, "end": v(15.69, -23.7) * mm});
            skArc(sketch, "E331", {"start": v(15.65, -23.7) * mm, "mid": v(15.69, -23.73) * mm, "end": v(15.73, -23.7) * mm});
            skArc(sketch, "E332", {"start": v(15.73, -23.7) * mm, "mid": v(15.69, -23.65) * mm, "end": v(15.65, -23.7) * mm});
            skLineSegment(sketch, "E333", {"start": v(5.96, 3.5) * mm, "end": v(5.96, 3.27) * mm});
            skArc(sketch, "E334", {"start": v(5.92, 3.5) * mm, "mid": v(5.96, 3.47) * mm, "end": v(6, 3.5) * mm});
            skArc(sketch, "E335", {"start": v(6, 3.5) * mm, "mid": v(5.96, 3.55) * mm, "end": v(5.92, 3.5) * mm});
            skArc(sketch, "E336", {"start": v(5.92, 3.27) * mm, "mid": v(5.96, 3.23) * mm, "end": v(6, 3.27) * mm});
            skArc(sketch, "E337", {"start": v(6, 3.27) * mm, "mid": v(5.96, 3.3) * mm, "end": v(5.92, 3.27) * mm});
            skLineSegment(sketch, "E338", {"start": v(5.96, 3.27) * mm, "end": v(-4.03, -6.72) * mm});
            skArc(sketch, "E339", {"start": v(-4.07, -6.72) * mm, "mid": v(-4.03, -6.76) * mm, "end": v(-4, -6.72) * mm});
            skArc(sketch, "E340", {"start": v(-4, -6.72) * mm, "mid": v(-4.03, -6.69) * mm, "end": v(-4.07, -6.72) * mm});
            skLineSegment(sketch, "E341", {"start": v(-4.03, -6.72) * mm, "end": v(4.64, -15.4) * mm});
            skArc(sketch, "E342", {"start": v(4.6, -15.4) * mm, "mid": v(4.64, -15.43) * mm, "end": v(4.67, -15.4) * mm});
            skArc(sketch, "E343", {"start": v(4.67, -15.4) * mm, "mid": v(4.64, -15.35) * mm, "end": v(4.6, -15.4) * mm});
            skLineSegment(sketch, "E344", {"start": v(4.64, -15.4) * mm, "end": v(4.66, -15.4) * mm});
            skArc(sketch, "E345", {"start": v(4.62, -15.4) * mm, "mid": v(4.66, -15.43) * mm, "end": v(4.7, -15.4) * mm});
            skArc(sketch, "E346", {"start": v(4.7, -15.4) * mm, "mid": v(4.66, -15.35) * mm, "end": v(4.62, -15.4) * mm});
            skLineSegment(sketch, "E347", {"start": v(4.66, -15.4) * mm, "end": v(8.5, -19.24) * mm});
            skArc(sketch, "E348", {"start": v(8.47, -19.24) * mm, "mid": v(8.5, -19.28) * mm, "end": v(8.55, -19.24) * mm});
            skArc(sketch, "E349", {"start": v(8.55, -19.24) * mm, "mid": v(8.5, -19.2) * mm, "end": v(8.47, -19.24) * mm});
            skLineSegment(sketch, "E350", {"start": v(8.5, -19.24) * mm, "end": v(8.5, -19.2) * mm});
            skArc(sketch, "E351", {"start": v(8.47, -19.2) * mm, "mid": v(8.5, -19.24) * mm, "end": v(8.55, -19.2) * mm});
            skArc(sketch, "E352", {"start": v(8.55, -19.2) * mm, "mid": v(8.5, -19.16) * mm, "end": v(8.47, -19.2) * mm});
            skLineSegment(sketch, "E353", {"start": v(8.5, -19.2) * mm, "end": v(13, -23.7) * mm});
            skArc(sketch, "E354", {"start": v(12.96, -23.7) * mm, "mid": v(13, -23.73) * mm, "end": v(13.04, -23.7) * mm});
            skArc(sketch, "E355", {"start": v(13.04, -23.7) * mm, "mid": v(13, -23.65) * mm, "end": v(12.96, -23.7) * mm});
            skLineSegment(sketch, "E356", {"start": v(13, -23.7) * mm, "end": v(13.15, -23.7) * mm});
            skArc(sketch, "E357", {"start": v(13.11, -23.7) * mm, "mid": v(13.15, -23.73) * mm, "end": v(13.19, -23.7) * mm});
            skArc(sketch, "E358", {"start": v(13.19, -23.7) * mm, "mid": v(13.15, -23.65) * mm, "end": v(13.11, -23.7) * mm});
            skLineSegment(sketch, "E359", {"start": v(10.6, -23.7) * mm, "end": v(-5.75, -7.33) * mm});
            skArc(sketch, "E360", {"start": v(10.57, -23.7) * mm, "mid": v(10.6, -23.73) * mm, "end": v(10.65, -23.7) * mm});
            skArc(sketch, "E361", {"start": v(10.65, -23.7) * mm, "mid": v(10.6, -23.65) * mm, "end": v(10.57, -23.7) * mm});
            skArc(sketch, "E362", {"start": v(-5.78, -7.33) * mm, "mid": v(-5.75, -7.37) * mm, "end": v(-5.7, -7.33) * mm});
            skArc(sketch, "E363", {"start": v(-5.7, -7.33) * mm, "mid": v(-5.75, -7.3) * mm, "end": v(-5.78, -7.33) * mm});
            skLineSegment(sketch, "E364", {"start": v(-5.75, -7.33) * mm, "end": v(-5.75, -6.68) * mm});
            skArc(sketch, "E365", {"start": v(-5.78, -6.68) * mm, "mid": v(-5.75, -6.72) * mm, "end": v(-5.7, -6.68) * mm});
            skArc(sketch, "E366", {"start": v(-5.7, -6.68) * mm, "mid": v(-5.75, -6.64) * mm, "end": v(-5.78, -6.68) * mm});
            skLineSegment(sketch, "E367", {"start": v(-5.75, -6.68) * mm, "end": v(-4.4, -5.33) * mm});
            skArc(sketch, "E368", {"start": v(-4.43, -5.33) * mm, "mid": v(-4.4, -5.37) * mm, "end": v(-4.36, -5.33) * mm});
            skArc(sketch, "E369", {"start": v(-4.36, -5.33) * mm, "mid": v(-4.4, -5.3) * mm, "end": v(-4.43, -5.33) * mm});
            skLineSegment(sketch, "E370", {"start": v(-4.4, -5.33) * mm, "end": v(-4.4, 0.79) * mm});
            skArc(sketch, "E371", {"start": v(-4.43, 0.79) * mm, "mid": v(-4.4, 0.75) * mm, "end": v(-4.36, 0.79) * mm});
            skArc(sketch, "E372", {"start": v(-4.36, 0.79) * mm, "mid": v(-4.4, 0.83) * mm, "end": v(-4.43, 0.79) * mm});
            skLineSegment(sketch, "E373", {"start": v(-4.4, 0.79) * mm, "end": v(-4.65, 0.79) * mm});
            skArc(sketch, "E374", {"start": v(-4.69, 0.79) * mm, "mid": v(-4.65, 0.75) * mm, "end": v(-4.61, 0.79) * mm});
            skArc(sketch, "E375", {"start": v(-4.61, 0.79) * mm, "mid": v(-4.65, 0.83) * mm, "end": v(-4.69, 0.79) * mm});
            skLineSegment(sketch, "E376", {"start": v(-4.65, 0.79) * mm, "end": v(-4.81, 0.95) * mm});
            skArc(sketch, "E377", {"start": v(-4.85, 0.95) * mm, "mid": v(-4.81, 0.9) * mm, "end": v(-4.77, 0.95) * mm});
            skArc(sketch, "E378", {"start": v(-4.77, 0.95) * mm, "mid": v(-4.81, 0.99) * mm, "end": v(-4.85, 0.95) * mm});
            skLineSegment(sketch, "E379", {"start": v(-14.38, 0.34) * mm, "end": v(-11.81, 0.34) * mm});
            skArc(sketch, "E380", {"start": v(-14.41, 0.34) * mm, "mid": v(-14.38, 0.3) * mm, "end": v(-14.34, 0.34) * mm});
            skArc(sketch, "E381", {"start": v(-14.34, 0.34) * mm, "mid": v(-14.38, 0.38) * mm, "end": v(-14.41, 0.34) * mm});
            skArc(sketch, "E382", {"start": v(-11.85, 0.34) * mm, "mid": v(-11.81, 0.3) * mm, "end": v(-11.78, 0.34) * mm});
            skArc(sketch, "E383", {"start": v(-11.78, 0.34) * mm, "mid": v(-11.81, 0.38) * mm, "end": v(-11.85, 0.34) * mm});
            skLineSegment(sketch, "E384", {"start": v(-11.81, 0.34) * mm, "end": v(-7.74, -3.73) * mm});
            skArc(sketch, "E385", {"start": v(-7.78, -3.73) * mm, "mid": v(-7.74, -3.76) * mm, "end": v(-7.7, -3.73) * mm});
            skArc(sketch, "E386", {"start": v(-7.7, -3.73) * mm, "mid": v(-7.74, -3.69) * mm, "end": v(-7.78, -3.73) * mm});
            skLineSegment(sketch, "E387", {"start": v(-7.74, -3.73) * mm, "end": v(-7.74, -7.88) * mm});
            skArc(sketch, "E388", {"start": v(-7.78, -7.88) * mm, "mid": v(-7.74, -7.91) * mm, "end": v(-7.7, -7.88) * mm});
            skArc(sketch, "E389", {"start": v(-7.7, -7.88) * mm, "mid": v(-7.74, -7.84) * mm, "end": v(-7.78, -7.88) * mm});
            skLineSegment(sketch, "E390", {"start": v(-7.74, -7.88) * mm, "end": v(8.07, -23.7) * mm});
            skArc(sketch, "E391", {"start": v(8.03, -23.7) * mm, "mid": v(8.07, -23.73) * mm, "end": v(8.1, -23.7) * mm});
            skArc(sketch, "E392", {"start": v(8.1, -23.7) * mm, "mid": v(8.07, -23.65) * mm, "end": v(8.03, -23.7) * mm});
            skLineSegment(sketch, "E393", {"start": v(-14.38, -2.2) * mm, "end": v(-12.18, -2.2) * mm});
            skArc(sketch, "E394", {"start": v(-14.41, -2.2) * mm, "mid": v(-14.38, -2.24) * mm, "end": v(-14.34, -2.2) * mm});
            skArc(sketch, "E395", {"start": v(-14.34, -2.2) * mm, "mid": v(-14.38, -2.16) * mm, "end": v(-14.41, -2.2) * mm});
            skArc(sketch, "E396", {"start": v(-12.22, -2.2) * mm, "mid": v(-12.18, -2.24) * mm, "end": v(-12.14, -2.2) * mm});
            skArc(sketch, "E397", {"start": v(-12.14, -2.2) * mm, "mid": v(-12.18, -2.16) * mm, "end": v(-12.22, -2.2) * mm});
            skLineSegment(sketch, "E398", {"start": v(-12.18, -2.2) * mm, "end": v(-10.41, -3.96) * mm});
            skArc(sketch, "E399", {"start": v(-10.45, -3.96) * mm, "mid": v(-10.41, -4) * mm, "end": v(-10.38, -3.96) * mm});
            skArc(sketch, "E400", {"start": v(-10.38, -3.96) * mm, "mid": v(-10.41, -3.92) * mm, "end": v(-10.45, -3.96) * mm});
            skLineSegment(sketch, "E401", {"start": v(-10.41, -3.96) * mm, "end": v(-10.41, -10.29) * mm});
            skArc(sketch, "E402", {"start": v(-10.45, -10.29) * mm, "mid": v(-10.41, -10.33) * mm, "end": v(-10.38, -10.29) * mm});
            skArc(sketch, "E403", {"start": v(-10.38, -10.29) * mm, "mid": v(-10.41, -10.25) * mm, "end": v(-10.45, -10.29) * mm});
            skLineSegment(sketch, "E404", {"start": v(-10.41, -10.29) * mm, "end": v(2.99, -23.7) * mm});
            skArc(sketch, "E405", {"start": v(2.95, -23.7) * mm, "mid": v(2.99, -23.73) * mm, "end": v(3.03, -23.7) * mm});
            skArc(sketch, "E406", {"start": v(3.03, -23.7) * mm, "mid": v(2.99, -23.65) * mm, "end": v(2.95, -23.7) * mm});
            skLineSegment(sketch, "E407", {"start": v(-13.13, -6) * mm, "end": v(-13.13, -10.1) * mm});
            skArc(sketch, "E408", {"start": v(-13.17, -6) * mm, "mid": v(-13.13, -6.03) * mm, "end": v(-13.1, -6) * mm});
            skArc(sketch, "E409", {"start": v(-13.1, -6) * mm, "mid": v(-13.13, -5.96) * mm, "end": v(-13.17, -6) * mm});
            skArc(sketch, "E410", {"start": v(-13.17, -10.1) * mm, "mid": v(-13.13, -10.15) * mm, "end": v(-13.1, -10.1) * mm});
            skArc(sketch, "E411", {"start": v(-13.1, -10.1) * mm, "mid": v(-13.13, -10.07) * mm, "end": v(-13.17, -10.1) * mm});
            skLineSegment(sketch, "E412", {"start": v(-13.13, -10.1) * mm, "end": v(0.45, -23.7) * mm});
            skArc(sketch, "E413", {"start": v(0.41, -23.7) * mm, "mid": v(0.45, -23.73) * mm, "end": v(0.49, -23.7) * mm});
            skArc(sketch, "E414", {"start": v(0.49, -23.7) * mm, "mid": v(0.45, -23.65) * mm, "end": v(0.41, -23.7) * mm});
            skLineSegment(sketch, "E415", {"start": v(-15.67, -6) * mm, "end": v(-15.67, -10.1) * mm});
            skArc(sketch, "E416", {"start": v(-15.7, -6) * mm, "mid": v(-15.67, -6.03) * mm, "end": v(-15.63, -6) * mm});
            skArc(sketch, "E417", {"start": v(-15.63, -6) * mm, "mid": v(-15.67, -5.96) * mm, "end": v(-15.7, -6) * mm});
            skArc(sketch, "E418", {"start": v(-15.7, -10.1) * mm, "mid": v(-15.67, -10.15) * mm, "end": v(-15.63, -10.1) * mm});
            skArc(sketch, "E419", {"start": v(-15.63, -10.1) * mm, "mid": v(-15.67, -10.07) * mm, "end": v(-15.7, -10.1) * mm});
            skLineSegment(sketch, "E420", {"start": v(-15.67, -10.1) * mm, "end": v(-2.1, -23.7) * mm});
            skArc(sketch, "E421", {"start": v(-2.13, -23.7) * mm, "mid": v(-2.1, -23.73) * mm, "end": v(-2.05, -23.7) * mm});
            skArc(sketch, "E422", {"start": v(-2.05, -23.7) * mm, "mid": v(-2.1, -23.65) * mm, "end": v(-2.13, -23.7) * mm});
            skLineSegment(sketch, "E423", {"start": v(-15.65, -0.93) * mm, "end": v(-17.84, -0.93) * mm});
            skArc(sketch, "E424", {"start": v(-15.68, -0.93) * mm, "mid": v(-15.65, -0.97) * mm, "end": v(-15.6, -0.93) * mm});
            skArc(sketch, "E425", {"start": v(-15.6, -0.93) * mm, "mid": v(-15.65, -0.89) * mm, "end": v(-15.68, -0.93) * mm});
            skArc(sketch, "E426", {"start": v(-17.88, -0.93) * mm, "mid": v(-17.84, -0.97) * mm, "end": v(-17.8, -0.93) * mm});
            skArc(sketch, "E427", {"start": v(-17.8, -0.93) * mm, "mid": v(-17.84, -0.89) * mm, "end": v(-17.88, -0.93) * mm});
            skLineSegment(sketch, "E428", {"start": v(-17.84, -0.93) * mm, "end": v(-20.72, -3.8) * mm});
            skArc(sketch, "E429", {"start": v(-20.75, -3.8) * mm, "mid": v(-20.72, -3.84) * mm, "end": v(-20.68, -3.8) * mm});
            skArc(sketch, "E430", {"start": v(-20.68, -3.8) * mm, "mid": v(-20.72, -3.76) * mm, "end": v(-20.75, -3.8) * mm});
            skLineSegment(sketch, "E431", {"start": v(-20.72, -3.8) * mm, "end": v(-20.72, -12.68) * mm});
            skArc(sketch, "E432", {"start": v(-20.75, -12.68) * mm, "mid": v(-20.72, -12.72) * mm, "end": v(-20.68, -12.68) * mm});
            skArc(sketch, "E433", {"start": v(-20.68, -12.68) * mm, "mid": v(-20.72, -12.64) * mm, "end": v(-20.75, -12.68) * mm});
            skLineSegment(sketch, "E434", {"start": v(-20.72, -12.68) * mm, "end": v(-9.71, -23.7) * mm});
            skArc(sketch, "E435", {"start": v(-9.75, -23.7) * mm, "mid": v(-9.71, -23.73) * mm, "end": v(-9.67, -23.7) * mm});
            skArc(sketch, "E436", {"start": v(-9.67, -23.7) * mm, "mid": v(-9.71, -23.65) * mm, "end": v(-9.75, -23.7) * mm});
            skLineSegment(sketch, "E437", {"start": v(-15.65, 0.34) * mm, "end": v(-20.12, 0.34) * mm});
            skArc(sketch, "E438", {"start": v(-15.68, 0.34) * mm, "mid": v(-15.65, 0.3) * mm, "end": v(-15.6, 0.34) * mm});
            skArc(sketch, "E439", {"start": v(-15.6, 0.34) * mm, "mid": v(-15.65, 0.38) * mm, "end": v(-15.68, 0.34) * mm});
            skArc(sketch, "E440", {"start": v(-20.15, 0.34) * mm, "mid": v(-20.12, 0.3) * mm, "end": v(-20.08, 0.34) * mm});
            skArc(sketch, "E441", {"start": v(-20.08, 0.34) * mm, "mid": v(-20.12, 0.38) * mm, "end": v(-20.15, 0.34) * mm});
            skLineSegment(sketch, "E442", {"start": v(-20.12, 0.34) * mm, "end": v(-22.16, -1.7) * mm});
            skArc(sketch, "E443", {"start": v(-22.2, -1.7) * mm, "mid": v(-22.16, -1.74) * mm, "end": v(-22.13, -1.7) * mm});
            skArc(sketch, "E444", {"start": v(-22.13, -1.7) * mm, "mid": v(-22.16, -1.67) * mm, "end": v(-22.2, -1.7) * mm});
            skLineSegment(sketch, "E445", {"start": v(-22.16, -1.7) * mm, "end": v(-22.16, -13.78) * mm});
            skArc(sketch, "E446", {"start": v(-22.2, -13.78) * mm, "mid": v(-22.16, -13.82) * mm, "end": v(-22.13, -13.78) * mm});
            skArc(sketch, "E447", {"start": v(-22.13, -13.78) * mm, "mid": v(-22.16, -13.74) * mm, "end": v(-22.2, -13.78) * mm});
            skLineSegment(sketch, "E448", {"start": v(-22.16, -13.78) * mm, "end": v(-12.25, -23.7) * mm});
            skArc(sketch, "E449", {"start": v(-12.29, -23.7) * mm, "mid": v(-12.25, -23.73) * mm, "end": v(-12.21, -23.7) * mm});
            skArc(sketch, "E450", {"start": v(-12.21, -23.7) * mm, "mid": v(-12.25, -23.65) * mm, "end": v(-12.29, -23.7) * mm});
            skLineSegment(sketch, "E451", {"start": v(16.76, 3.82) * mm, "end": v(16.76, 23.25) * mm});
            skArc(sketch, "E452", {"start": v(16.45, 3.82) * mm, "mid": v(16.76, 3.5) * mm, "end": v(17.08, 3.82) * mm});
            skArc(sketch, "E453", {"start": v(17.08, 3.82) * mm, "mid": v(16.76, 4.14) * mm, "end": v(16.45, 3.82) * mm});
            skArc(sketch, "E454", {"start": v(16.45, 23.25) * mm, "mid": v(16.76, 22.94) * mm, "end": v(17.08, 23.25) * mm});
            skArc(sketch, "E455", {"start": v(17.08, 23.25) * mm, "mid": v(16.76, 23.57) * mm, "end": v(16.45, 23.25) * mm});
            skLineSegment(sketch, "E456", {"start": v(16.76, 23.25) * mm, "end": v(16.33, 23.69) * mm});
            skArc(sketch, "E457", {"start": v(16.73, 23.25) * mm, "mid": v(16.76, 23.22) * mm, "end": v(16.8, 23.25) * mm});
            skArc(sketch, "E458", {"start": v(16.8, 23.25) * mm, "mid": v(16.76, 23.3) * mm, "end": v(16.73, 23.25) * mm});
            skArc(sketch, "E459", {"start": v(16.3, 23.69) * mm, "mid": v(16.33, 23.65) * mm, "end": v(16.37, 23.69) * mm});
            skArc(sketch, "E460", {"start": v(16.37, 23.69) * mm, "mid": v(16.33, 23.72) * mm, "end": v(16.3, 23.69) * mm});
            skLineSegment(sketch, "E461", {"start": v(14.22, 3.82) * mm, "end": v(14.22, 23.25) * mm});
            skArc(sketch, "E462", {"start": v(13.9, 3.82) * mm, "mid": v(14.22, 3.5) * mm, "end": v(14.54, 3.82) * mm});
            skArc(sketch, "E463", {"start": v(14.54, 3.82) * mm, "mid": v(14.22, 4.14) * mm, "end": v(13.9, 3.82) * mm});
            skArc(sketch, "E464", {"start": v(13.9, 23.25) * mm, "mid": v(14.22, 22.94) * mm, "end": v(14.54, 23.25) * mm});
            skArc(sketch, "E465", {"start": v(14.54, 23.25) * mm, "mid": v(14.22, 23.57) * mm, "end": v(13.9, 23.25) * mm});
            skLineSegment(sketch, "E466", {"start": v(14.22, 23.25) * mm, "end": v(13.79, 23.69) * mm});
            skArc(sketch, "E467", {"start": v(14.19, 23.25) * mm, "mid": v(14.22, 23.22) * mm, "end": v(14.26, 23.25) * mm});
            skArc(sketch, "E468", {"start": v(14.26, 23.25) * mm, "mid": v(14.22, 23.3) * mm, "end": v(14.19, 23.25) * mm});
            skArc(sketch, "E469", {"start": v(13.75, 23.69) * mm, "mid": v(13.79, 23.65) * mm, "end": v(13.83, 23.69) * mm});
            skArc(sketch, "E470", {"start": v(13.83, 23.69) * mm, "mid": v(13.79, 23.72) * mm, "end": v(13.75, 23.69) * mm});
            skLineSegment(sketch, "E471", {"start": v(36.6, 14.78) * mm, "end": v(-20.06, 14.78) * mm});
            skArc(sketch, "E472", {"start": v(36.57, 14.78) * mm, "mid": v(36.6, 14.74) * mm, "end": v(36.65, 14.78) * mm});
            skArc(sketch, "E473", {"start": v(36.65, 14.78) * mm, "mid": v(36.6, 14.82) * mm, "end": v(36.57, 14.78) * mm});
            skArc(sketch, "E474", {"start": v(-20.1, 14.78) * mm, "mid": v(-20.06, 14.74) * mm, "end": v(-20.02, 14.78) * mm});
            skArc(sketch, "E475", {"start": v(-20.02, 14.78) * mm, "mid": v(-20.06, 14.82) * mm, "end": v(-20.1, 14.78) * mm});
            skLineSegment(sketch, "E476", {"start": v(-20.06, 14.78) * mm, "end": v(-24.33, 10.5) * mm});
            skArc(sketch, "E477", {"start": v(-24.37, 10.5) * mm, "mid": v(-24.33, 10.46) * mm, "end": v(-24.3, 10.5) * mm});
            skArc(sketch, "E478", {"start": v(-24.3, 10.5) * mm, "mid": v(-24.33, 10.54) * mm, "end": v(-24.37, 10.5) * mm});
            skLineSegment(sketch, "E479", {"start": v(-24.33, 10.5) * mm, "end": v(-24.33, 3.76) * mm});
            skArc(sketch, "E480", {"start": v(-24.37, 3.76) * mm, "mid": v(-24.33, 3.73) * mm, "end": v(-24.3, 3.76) * mm});
            skArc(sketch, "E481", {"start": v(-24.3, 3.76) * mm, "mid": v(-24.33, 3.8) * mm, "end": v(-24.37, 3.76) * mm});
            skLineSegment(sketch, "E482", {"start": v(-24.33, 3.76) * mm, "end": v(-20.28, -0.29) * mm});
            skArc(sketch, "E483", {"start": v(-20.32, -0.29) * mm, "mid": v(-20.28, -0.33) * mm, "end": v(-20.24, -0.29) * mm});
            skArc(sketch, "E484", {"start": v(-20.24, -0.29) * mm, "mid": v(-20.28, -0.25) * mm, "end": v(-20.32, -0.29) * mm});
            skLineSegment(sketch, "E485", {"start": v(-20.28, -0.29) * mm, "end": v(-15.01, -0.29) * mm});
            skArc(sketch, "E486", {"start": v(-15.05, -0.29) * mm, "mid": v(-15.01, -0.33) * mm, "end": v(-14.98, -0.29) * mm});
            skArc(sketch, "E487", {"start": v(-14.98, -0.29) * mm, "mid": v(-15.01, -0.25) * mm, "end": v(-15.05, -0.29) * mm});
            skLineSegment(sketch, "E488", {"start": v(-15.01, -0.29) * mm, "end": v(-14.38, -0.93) * mm});
            skLineSegment(sketch, "E489", {"start": v(36.6, 9.7) * mm, "end": v(-19.47, 9.7) * mm});
            skArc(sketch, "E490", {"start": v(36.57, 9.7) * mm, "mid": v(36.6, 9.66) * mm, "end": v(36.65, 9.7) * mm});
            skArc(sketch, "E491", {"start": v(36.65, 9.7) * mm, "mid": v(36.6, 9.74) * mm, "end": v(36.57, 9.7) * mm});
            skArc(sketch, "E492", {"start": v(-19.51, 9.7) * mm, "mid": v(-19.47, 9.66) * mm, "end": v(-19.44, 9.7) * mm});
            skArc(sketch, "E493", {"start": v(-19.44, 9.7) * mm, "mid": v(-19.47, 9.74) * mm, "end": v(-19.51, 9.7) * mm});
            skLineSegment(sketch, "E494", {"start": v(-19.47, 9.7) * mm, "end": v(-21.1, 8.06) * mm});
            skArc(sketch, "E495", {"start": v(-21.15, 8.06) * mm, "mid": v(-21.1, 8.03) * mm, "end": v(-21.07, 8.06) * mm});
            skArc(sketch, "E496", {"start": v(-21.07, 8.06) * mm, "mid": v(-21.1, 8.1) * mm, "end": v(-21.15, 8.06) * mm});
            skLineSegment(sketch, "E497", {"start": v(-21.1, 8.06) * mm, "end": v(-21.1, 3.76) * mm});
            skArc(sketch, "E498", {"start": v(-21.15, 3.76) * mm, "mid": v(-21.1, 3.72) * mm, "end": v(-21.07, 3.76) * mm});
            skArc(sketch, "E499", {"start": v(-21.07, 3.76) * mm, "mid": v(-21.1, 3.8) * mm, "end": v(-21.15, 3.76) * mm});
            skLineSegment(sketch, "E500", {"start": v(-21.1, 3.76) * mm, "end": v(-18.99, 1.64) * mm});
            skArc(sketch, "E501", {"start": v(-19.03, 1.64) * mm, "mid": v(-18.99, 1.6) * mm, "end": v(-18.95, 1.64) * mm});
            skArc(sketch, "E502", {"start": v(-18.95, 1.64) * mm, "mid": v(-18.99, 1.67) * mm, "end": v(-19.03, 1.64) * mm});
            skLineSegment(sketch, "E503", {"start": v(-18.99, 1.64) * mm, "end": v(-15.67, 1.64) * mm});
            skArc(sketch, "E504", {"start": v(-15.7, 1.64) * mm, "mid": v(-15.67, 1.6) * mm, "end": v(-15.63, 1.64) * mm});
            skArc(sketch, "E505", {"start": v(-15.63, 1.64) * mm, "mid": v(-15.67, 1.67) * mm, "end": v(-15.7, 1.64) * mm});
            skLineSegment(sketch, "E506", {"start": v(-15.67, 1.64) * mm, "end": v(-14.38, 0.34) * mm});
            skLineSegment(sketch, "E507", {"start": v(36.6, 19.86) * mm, "end": v(-17.28, 19.86) * mm});
            skArc(sketch, "E508", {"start": v(36.57, 19.86) * mm, "mid": v(36.6, 19.82) * mm, "end": v(36.65, 19.86) * mm});
            skArc(sketch, "E509", {"start": v(36.65, 19.86) * mm, "mid": v(36.6, 19.9) * mm, "end": v(36.57, 19.86) * mm});
            skArc(sketch, "E510", {"start": v(-17.32, 19.86) * mm, "mid": v(-17.28, 19.82) * mm, "end": v(-17.24, 19.86) * mm});
            skArc(sketch, "E511", {"start": v(-17.24, 19.86) * mm, "mid": v(-17.28, 19.9) * mm, "end": v(-17.32, 19.86) * mm});
            skLineSegment(sketch, "E512", {"start": v(-17.28, 19.86) * mm, "end": v(-26.38, 10.76) * mm});
            skArc(sketch, "E513", {"start": v(-26.42, 10.76) * mm, "mid": v(-26.38, 10.73) * mm, "end": v(-26.34, 10.76) * mm});
            skArc(sketch, "E514", {"start": v(-26.34, 10.76) * mm, "mid": v(-26.38, 10.8) * mm, "end": v(-26.42, 10.76) * mm});
            skLineSegment(sketch, "E515", {"start": v(-26.38, 10.76) * mm, "end": v(-26.38, 2.47) * mm});
            skArc(sketch, "E516", {"start": v(-26.42, 2.47) * mm, "mid": v(-26.38, 2.43) * mm, "end": v(-26.34, 2.47) * mm});
            skArc(sketch, "E517", {"start": v(-26.34, 2.47) * mm, "mid": v(-26.38, 2.5) * mm, "end": v(-26.42, 2.47) * mm});
            skLineSegment(sketch, "E518", {"start": v(-26.38, 2.47) * mm, "end": v(-18.7, -5.21) * mm});
            skArc(sketch, "E519", {"start": v(-18.74, -5.21) * mm, "mid": v(-18.7, -5.25) * mm, "end": v(-18.66, -5.21) * mm});
            skArc(sketch, "E520", {"start": v(-18.66, -5.21) * mm, "mid": v(-18.7, -5.17) * mm, "end": v(-18.74, -5.21) * mm});
            skLineSegment(sketch, "E521", {"start": v(-18.7, -5.21) * mm, "end": v(-17.4, -5.21) * mm});
            skArc(sketch, "E522", {"start": v(-17.43, -5.21) * mm, "mid": v(-17.4, -5.25) * mm, "end": v(-17.36, -5.21) * mm});
            skArc(sketch, "E523", {"start": v(-17.36, -5.21) * mm, "mid": v(-17.4, -5.17) * mm, "end": v(-17.43, -5.21) * mm});
            skLineSegment(sketch, "E524", {"start": v(-17.4, -5.21) * mm, "end": v(-14.38, -2.2) * mm});
            skLineSegment(sketch, "E525", {"start": v(36.6, 17.32) * mm, "end": v(-18.74, 17.32) * mm});
            skArc(sketch, "E526", {"start": v(36.57, 17.32) * mm, "mid": v(36.6, 17.28) * mm, "end": v(36.65, 17.32) * mm});
            skArc(sketch, "E527", {"start": v(36.65, 17.32) * mm, "mid": v(36.6, 17.36) * mm, "end": v(36.57, 17.32) * mm});
            skArc(sketch, "E528", {"start": v(-18.78, 17.32) * mm, "mid": v(-18.74, 17.28) * mm, "end": v(-18.7, 17.32) * mm});
            skArc(sketch, "E529", {"start": v(-18.7, 17.32) * mm, "mid": v(-18.74, 17.36) * mm, "end": v(-18.78, 17.32) * mm});
            skLineSegment(sketch, "E530", {"start": v(-18.74, 17.32) * mm, "end": v(-25.12, 10.94) * mm});
            skArc(sketch, "E531", {"start": v(-25.16, 10.94) * mm, "mid": v(-25.12, 10.9) * mm, "end": v(-25.08, 10.94) * mm});
            skArc(sketch, "E532", {"start": v(-25.08, 10.94) * mm, "mid": v(-25.12, 10.98) * mm, "end": v(-25.16, 10.94) * mm});
            skLineSegment(sketch, "E533", {"start": v(-25.12, 10.94) * mm, "end": v(-25.12, 3.35) * mm});
            skArc(sketch, "E534", {"start": v(-25.16, 3.35) * mm, "mid": v(-25.12, 3.31) * mm, "end": v(-25.08, 3.35) * mm});
            skArc(sketch, "E535", {"start": v(-25.08, 3.35) * mm, "mid": v(-25.12, 3.39) * mm, "end": v(-25.16, 3.35) * mm});
            skLineSegment(sketch, "E536", {"start": v(-25.12, 3.35) * mm, "end": v(-20.9, -0.87) * mm});
            skArc(sketch, "E537", {"start": v(-20.94, -0.87) * mm, "mid": v(-20.9, -0.9) * mm, "end": v(-20.86, -0.87) * mm});
            skArc(sketch, "E538", {"start": v(-20.86, -0.87) * mm, "mid": v(-20.9, -0.83) * mm, "end": v(-20.94, -0.87) * mm});
            skLineSegment(sketch, "E539", {"start": v(-20.9, -0.87) * mm, "end": v(-15.7, -0.87) * mm});
            skArc(sketch, "E540", {"start": v(-15.74, -0.87) * mm, "mid": v(-15.7, -0.9) * mm, "end": v(-15.66, -0.87) * mm});
            skArc(sketch, "E541", {"start": v(-15.66, -0.87) * mm, "mid": v(-15.7, -0.83) * mm, "end": v(-15.74, -0.87) * mm});
            skLineSegment(sketch, "E542", {"start": v(-15.7, -0.87) * mm, "end": v(-15.65, -0.93) * mm});
            skLineSegment(sketch, "E543", {"start": v(36.6, 12.24) * mm, "end": v(-20.34, 12.24) * mm});
            skArc(sketch, "E544", {"start": v(36.57, 12.24) * mm, "mid": v(36.6, 12.2) * mm, "end": v(36.65, 12.24) * mm});
            skArc(sketch, "E545", {"start": v(36.65, 12.24) * mm, "mid": v(36.6, 12.28) * mm, "end": v(36.57, 12.24) * mm});
            skArc(sketch, "E546", {"start": v(-20.38, 12.24) * mm, "mid": v(-20.34, 12.2) * mm, "end": v(-20.3, 12.24) * mm});
            skArc(sketch, "E547", {"start": v(-20.3, 12.24) * mm, "mid": v(-20.34, 12.28) * mm, "end": v(-20.38, 12.24) * mm});
            skLineSegment(sketch, "E548", {"start": v(-20.34, 12.24) * mm, "end": v(-22.97, 9.6) * mm});
            skArc(sketch, "E549", {"start": v(-23.01, 9.6) * mm, "mid": v(-22.97, 9.57) * mm, "end": v(-22.94, 9.6) * mm});
            skArc(sketch, "E550", {"start": v(-22.94, 9.6) * mm, "mid": v(-22.97, 9.64) * mm, "end": v(-23.01, 9.6) * mm});
            skLineSegment(sketch, "E551", {"start": v(-22.97, 9.6) * mm, "end": v(-22.97, 3.7) * mm});
            skArc(sketch, "E552", {"start": v(-23.01, 3.7) * mm, "mid": v(-22.97, 3.66) * mm, "end": v(-22.94, 3.7) * mm});
            skArc(sketch, "E553", {"start": v(-22.94, 3.7) * mm, "mid": v(-22.97, 3.73) * mm, "end": v(-23.01, 3.7) * mm});
            skLineSegment(sketch, "E554", {"start": v(-22.97, 3.7) * mm, "end": v(-19.82, 0.54) * mm});
            skArc(sketch, "E555", {"start": v(-19.86, 0.54) * mm, "mid": v(-19.82, 0.5) * mm, "end": v(-19.78, 0.54) * mm});
            skArc(sketch, "E556", {"start": v(-19.78, 0.54) * mm, "mid": v(-19.82, 0.58) * mm, "end": v(-19.86, 0.54) * mm});
            skLineSegment(sketch, "E557", {"start": v(-19.82, 0.54) * mm, "end": v(-15.85, 0.54) * mm});
            skArc(sketch, "E558", {"start": v(-15.89, 0.54) * mm, "mid": v(-15.85, 0.5) * mm, "end": v(-15.8, 0.54) * mm});
            skArc(sketch, "E559", {"start": v(-15.8, 0.54) * mm, "mid": v(-15.85, 0.58) * mm, "end": v(-15.89, 0.54) * mm});
            skLineSegment(sketch, "E560", {"start": v(-15.85, 0.54) * mm, "end": v(-15.65, 0.34) * mm});
            skCircle(sketch, "E561", {"center": v(-13.13, -6) * mm, "radius": 0.32 * mm});
            skCircle(sketch, "E562", {"center": v(-15.67, -6) * mm, "radius": 0.32 * mm});
            skCircle(sketch, "E563", {"center": v(-18.2, -6) * mm, "radius": 0.32 * mm});
            skCircle(sketch, "E564", {"center": v(18.52, -0.2) * mm, "radius": 0.32 * mm});
            skCircle(sketch, "E565", {"center": v(5.02, -2.5) * mm, "radius": 0.32 * mm});
            skCircle(sketch, "E566", {"center": v(5.3, -3.88) * mm, "radius": 0.32 * mm});
            skCircle(sketch, "E567", {"center": v(-4.81, 0.95) * mm, "radius": 0.32 * mm});
            skCircle(sketch, "E568", {"center": v(5.96, 3.5) * mm, "radius": 0.32 * mm});
            skCircle(sketch, "E569", {"center": v(8.79, 3.47) * mm, "radius": 0.32 * mm});
            skCircle(sketch, "E570", {"center": v(6.14, 1.09) * mm, "radius": 0.32 * mm});
            skCircle(sketch, "E571", {"center": v(15.12, -6.13) * mm, "radius": 0.32 * mm});
            skCircle(sketch, "E572", {"center": v(7.97, -6.18) * mm, "radius": 0.32 * mm});
            skCircle(sketch, "E573", {"center": v(30.93, -23.7) * mm, "radius": 0.55 * mm});
            skCircle(sketch, "E574", {"center": v(28.39, -23.7) * mm, "radius": 0.55 * mm});
            skCircle(sketch, "E575", {"center": v(25.85, -23.7) * mm, "radius": 0.55 * mm});
            skCircle(sketch, "E576", {"center": v(23.3, -23.7) * mm, "radius": 0.55 * mm});
            skCircle(sketch, "E577", {"center": v(20.77, -23.7) * mm, "radius": 0.55 * mm});
            skCircle(sketch, "E578", {"center": v(18.23, -23.7) * mm, "radius": 0.55 * mm});
            skCircle(sketch, "E579", {"center": v(15.69, -23.7) * mm, "radius": 0.55 * mm});
            skCircle(sketch, "E580", {"center": v(13.15, -23.7) * mm, "radius": 0.55 * mm});
            skCircle(sketch, "E581", {"center": v(10.6, -23.7) * mm, "radius": 0.55 * mm});
            skCircle(sketch, "E582", {"center": v(8.07, -23.7) * mm, "radius": 0.55 * mm});
            skCircle(sketch, "E583", {"center": v(5.53, -23.7) * mm, "radius": 0.55 * mm});
            skCircle(sketch, "E584", {"center": v(2.99, -23.7) * mm, "radius": 0.55 * mm});
            skCircle(sketch, "E585", {"center": v(0.45, -23.7) * mm, "radius": 0.55 * mm});
            skCircle(sketch, "E586", {"center": v(-2.1, -23.7) * mm, "radius": 0.55 * mm});
            skCircle(sketch, "E587", {"center": v(-4.63, -23.7) * mm, "radius": 0.55 * mm});
            skCircle(sketch, "E588", {"center": v(-7.17, -23.7) * mm, "radius": 0.55 * mm});
            skCircle(sketch, "E589", {"center": v(-9.71, -23.7) * mm, "radius": 0.55 * mm});
            skCircle(sketch, "E590", {"center": v(-12.25, -23.7) * mm, "radius": 0.55 * mm});
            skCircle(sketch, "E591", {"center": v(-15.65, 0.34) * mm, "radius": 0.32 * mm});
            skCircle(sketch, "E592", {"center": v(-14.38, 0.34) * mm, "radius": 0.32 * mm});
            skCircle(sketch, "E593", {"center": v(-14.38, -0.93) * mm, "radius": 0.32 * mm});
            skCircle(sketch, "E594", {"center": v(-14.38, -2.2) * mm, "radius": 0.32 * mm});
            skCircle(sketch, "E595", {"center": v(-15.65, -0.93) * mm, "radius": 0.32 * mm});
            skCircle(sketch, "E596", {"center": v(-15.65, -2.2) * mm, "radius": 0.32 * mm});
            skCircle(sketch, "E597", {"center": v(36.6, 22.4) * mm, "radius": 0.55 * mm});
            skCircle(sketch, "E598", {"center": v(36.6, 19.86) * mm, "radius": 0.55 * mm});
            skCircle(sketch, "E599", {"center": v(36.6, 17.32) * mm, "radius": 0.55 * mm});
            skCircle(sketch, "E600", {"center": v(36.6, 14.78) * mm, "radius": 0.55 * mm});
            skCircle(sketch, "E601", {"center": v(36.6, 12.24) * mm, "radius": 0.55 * mm});
            skCircle(sketch, "E602", {"center": v(36.6, 9.7) * mm, "radius": 0.55 * mm});
            skCircle(sketch, "E603", {"center": v(36.53, -10) * mm, "radius": 0.55 * mm});
            skCircle(sketch, "E604", {"center": v(36.53, -12.53) * mm, "radius": 0.55 * mm});
            skCircle(sketch, "E605", {"center": v(14.22, 3.82) * mm, "radius": 0.55 * mm});
            skCircle(sketch, "E606", {"center": v(16.76, 3.82) * mm, "radius": 0.55 * mm});
            skCircle(sketch, "E607", {"center": v(13.79, 23.69) * mm, "radius": 0.55 * mm});
            skCircle(sketch, "E608", {"center": v(16.33, 23.69) * mm, "radius": 0.55 * mm});
            skCircle(sketch, "E609", {"center": v(-25.5, -12.84) * mm, "radius": 2.54 * mm});
            skCircle(sketch, "E610", {"center": v(25.48, -12.74) * mm, "radius": 2.54 * mm});
            skCircle(sketch, "E611", {"center": v(25.5, -12.74) * mm, "radius": 0.5 * mm});
            skLineSegment(sketch, "E612", {"start": v(-38.1, -25.4) * mm, "end": v(38.1, -25.4) * mm});
            skLineSegment(sketch, "E613", {"start": v(38.1, -25.4) * mm, "end": v(38.1, 25.4) * mm});
            skLineSegment(sketch, "E614", {"start": v(38.1, 25.4) * mm, "end": v(-38.1, 25.4) * mm});
            skLineSegment(sketch, "E615", {"start": v(-38.1, 25.4) * mm, "end": v(-38.1, -25.4) * mm});
            skLineSegment(sketch, "E616", {"start": v(-12.65, -6.03) * mm, "end": v(-12.67, -6.14) * mm});
            skLineSegment(sketch, "E617", {"start": v(-12.67, -6.14) * mm, "end": v(-12.72, -6.25) * mm});
            skLineSegment(sketch, "E618", {"start": v(-12.72, -6.25) * mm, "end": v(-12.79, -6.33) * mm});
            skLineSegment(sketch, "E619", {"start": v(-12.79, -6.33) * mm, "end": v(-12.88, -6.4) * mm});
            skLineSegment(sketch, "E620", {"start": v(-12.88, -6.4) * mm, "end": v(-12.95, -6.44) * mm});
            skLineSegment(sketch, "E621", {"start": v(-12.95, -6.44) * mm, "end": v(-12.95, -10.04) * mm});
            skLineSegment(sketch, "E622", {"start": v(-12.95, -10.04) * mm, "end": v(-0.09, -22.9) * mm});
            skLineSegment(sketch, "E623", {"start": v(-0.09, -22.9) * mm, "end": v(0.09, -22.81) * mm});
            skLineSegment(sketch, "E624", {"start": v(0.09, -22.81) * mm, "end": v(0.23, -22.76) * mm});
            skLineSegment(sketch, "E625", {"start": v(0.23, -22.76) * mm, "end": v(0.38, -22.74) * mm});
            skLineSegment(sketch, "E626", {"start": v(0.38, -22.74) * mm, "end": v(0.53, -22.74) * mm});
            skLineSegment(sketch, "E627", {"start": v(0.53, -22.74) * mm, "end": v(0.67, -22.76) * mm});
            skLineSegment(sketch, "E628", {"start": v(0.67, -22.76) * mm, "end": v(0.82, -22.81) * mm});
            skLineSegment(sketch, "E629", {"start": v(0.82, -22.81) * mm, "end": v(0.95, -22.88) * mm});
            skLineSegment(sketch, "E630", {"start": v(0.95, -22.88) * mm, "end": v(1.07, -22.97) * mm});
            skLineSegment(sketch, "E631", {"start": v(1.07, -22.97) * mm, "end": v(1.17, -23.07) * mm});
            skLineSegment(sketch, "E632", {"start": v(1.17, -23.07) * mm, "end": v(1.26, -23.2) * mm});
            skLineSegment(sketch, "E633", {"start": v(1.26, -23.2) * mm, "end": v(1.33, -23.32) * mm});
            skLineSegment(sketch, "E634", {"start": v(1.33, -23.32) * mm, "end": v(1.37, -23.47) * mm});
            skLineSegment(sketch, "E635", {"start": v(1.37, -23.47) * mm, "end": v(1.4, -23.61) * mm});
            skLineSegment(sketch, "E636", {"start": v(1.4, -23.61) * mm, "end": v(1.4, -23.76) * mm});
            skLineSegment(sketch, "E637", {"start": v(1.4, -23.76) * mm, "end": v(1.37, -23.91) * mm});
            skLineSegment(sketch, "E638", {"start": v(1.37, -23.91) * mm, "end": v(1.33, -24.05) * mm});
            skLineSegment(sketch, "E639", {"start": v(1.33, -24.05) * mm, "end": v(1.26, -24.19) * mm});
            skLineSegment(sketch, "E640", {"start": v(1.26, -24.19) * mm, "end": v(1.17, -24.3) * mm});
            skLineSegment(sketch, "E641", {"start": v(1.17, -24.3) * mm, "end": v(1.07, -24.41) * mm});
            skLineSegment(sketch, "E642", {"start": v(1.07, -24.41) * mm, "end": v(0.95, -24.5) * mm});
            skLineSegment(sketch, "E643", {"start": v(0.95, -24.5) * mm, "end": v(0.82, -24.57) * mm});
            skLineSegment(sketch, "E644", {"start": v(0.82, -24.57) * mm, "end": v(0.67, -24.62) * mm});
            skLineSegment(sketch, "E645", {"start": v(0.67, -24.62) * mm, "end": v(0.53, -24.64) * mm});
            skLineSegment(sketch, "E646", {"start": v(0.53, -24.64) * mm, "end": v(0.38, -24.64) * mm});
            skLineSegment(sketch, "E647", {"start": v(0.38, -24.64) * mm, "end": v(0.23, -24.62) * mm});
            skLineSegment(sketch, "E648", {"start": v(0.23, -24.62) * mm, "end": v(0.09, -24.57) * mm});
            skLineSegment(sketch, "E649", {"start": v(0.09, -24.57) * mm, "end": v(-0.05, -24.5) * mm});
            skLineSegment(sketch, "E650", {"start": v(-0.05, -24.5) * mm, "end": v(-0.17, -24.41) * mm});
            skLineSegment(sketch, "E651", {"start": v(-0.17, -24.41) * mm, "end": v(-0.27, -24.3) * mm});
            skLineSegment(sketch, "E652", {"start": v(-0.27, -24.3) * mm, "end": v(-0.36, -24.19) * mm});
            skLineSegment(sketch, "E653", {"start": v(-0.36, -24.19) * mm, "end": v(-0.43, -24.05) * mm});
            skLineSegment(sketch, "E654", {"start": v(-0.43, -24.05) * mm, "end": v(-0.47, -23.91) * mm});
            skLineSegment(sketch, "E655", {"start": v(-0.47, -23.91) * mm, "end": v(-0.5, -23.76) * mm});
            skLineSegment(sketch, "E656", {"start": v(-0.5, -23.76) * mm, "end": v(-0.5, -23.61) * mm});
            skLineSegment(sketch, "E657", {"start": v(-0.5, -23.61) * mm, "end": v(-0.47, -23.47) * mm});
            skLineSegment(sketch, "E658", {"start": v(-0.47, -23.47) * mm, "end": v(-0.43, -23.32) * mm});
            skLineSegment(sketch, "E659", {"start": v(-0.43, -23.32) * mm, "end": v(-0.36, -23.2) * mm});
            skLineSegment(sketch, "E660", {"start": v(-0.36, -23.2) * mm, "end": v(-0.34, -23.15) * mm});
            skLineSegment(sketch, "E661", {"start": v(-0.34, -23.15) * mm, "end": v(-13.27, -10.21) * mm});
            skLineSegment(sketch, "E662", {"start": v(-13.27, -10.21) * mm, "end": v(-13.3, -10.15) * mm});
            skLineSegment(sketch, "E663", {"start": v(-13.3, -10.15) * mm, "end": v(-13.3, -10.1) * mm});
            skLineSegment(sketch, "E664", {"start": v(-13.3, -10.1) * mm, "end": v(-13.3, -6.44) * mm});
            skLineSegment(sketch, "E665", {"start": v(-13.3, -6.44) * mm, "end": v(-13.38, -6.4) * mm});
            skLineSegment(sketch, "E666", {"start": v(-13.38, -6.4) * mm, "end": v(-13.47, -6.33) * mm});
            skLineSegment(sketch, "E667", {"start": v(-13.47, -6.33) * mm, "end": v(-13.54, -6.25) * mm});
            skLineSegment(sketch, "E668", {"start": v(-13.54, -6.25) * mm, "end": v(-13.59, -6.14) * mm});
            skLineSegment(sketch, "E669", {"start": v(-13.59, -6.14) * mm, "end": v(-13.61, -6.03) * mm});
            skLineSegment(sketch, "E670", {"start": v(-13.61, -6.03) * mm, "end": v(-13.6, -5.92) * mm});
            skLineSegment(sketch, "E671", {"start": v(-13.6, -5.92) * mm, "end": v(-13.58, -5.8) * mm});
            skLineSegment(sketch, "E672", {"start": v(-13.58, -5.8) * mm, "end": v(-13.52, -5.7) * mm});
            skLineSegment(sketch, "E673", {"start": v(-13.52, -5.7) * mm, "end": v(-13.44, -5.63) * mm});
            skLineSegment(sketch, "E674", {"start": v(-13.44, -5.63) * mm, "end": v(-13.35, -5.56) * mm});
            skLineSegment(sketch, "E675", {"start": v(-13.35, -5.56) * mm, "end": v(-13.24, -5.52) * mm});
            skLineSegment(sketch, "E676", {"start": v(-13.24, -5.52) * mm, "end": v(-13.13, -5.51) * mm});
            skLineSegment(sketch, "E677", {"start": v(-13.13, -5.51) * mm, "end": v(-13.02, -5.52) * mm});
            skLineSegment(sketch, "E678", {"start": v(-13.02, -5.52) * mm, "end": v(-12.91, -5.56) * mm});
            skLineSegment(sketch, "E679", {"start": v(-12.91, -5.56) * mm, "end": v(-12.82, -5.63) * mm});
            skLineSegment(sketch, "E680", {"start": v(-12.82, -5.63) * mm, "end": v(-12.74, -5.7) * mm});
            skLineSegment(sketch, "E681", {"start": v(-12.74, -5.7) * mm, "end": v(-12.68, -5.8) * mm});
            skLineSegment(sketch, "E682", {"start": v(-12.68, -5.8) * mm, "end": v(-12.65, -5.92) * mm});
            skLineSegment(sketch, "E683", {"start": v(-12.65, -5.92) * mm, "end": v(-12.65, -6.03) * mm});
            skLineSegment(sketch, "E684", {"start": v(-15.19, -6.03) * mm, "end": v(-15.21, -6.14) * mm});
            skLineSegment(sketch, "E685", {"start": v(-15.21, -6.14) * mm, "end": v(-15.26, -6.25) * mm});
            skLineSegment(sketch, "E686", {"start": v(-15.26, -6.25) * mm, "end": v(-15.33, -6.33) * mm});
            skLineSegment(sketch, "E687", {"start": v(-15.33, -6.33) * mm, "end": v(-15.42, -6.4) * mm});
            skLineSegment(sketch, "E688", {"start": v(-15.42, -6.4) * mm, "end": v(-15.5, -6.44) * mm});
            skLineSegment(sketch, "E689", {"start": v(-15.5, -6.44) * mm, "end": v(-15.5, -10.04) * mm});
            skLineSegment(sketch, "E690", {"start": v(-15.5, -10.04) * mm, "end": v(-2.63, -22.9) * mm});
            skLineSegment(sketch, "E691", {"start": v(-2.63, -22.9) * mm, "end": v(-2.45, -22.81) * mm});
            skLineSegment(sketch, "E692", {"start": v(-2.45, -22.81) * mm, "end": v(-2.31, -22.76) * mm});
            skLineSegment(sketch, "E693", {"start": v(-2.31, -22.76) * mm, "end": v(-2.16, -22.74) * mm});
            skLineSegment(sketch, "E694", {"start": v(-2.16, -22.74) * mm, "end": v(-2.01, -22.74) * mm});
            skLineSegment(sketch, "E695", {"start": v(-2.01, -22.74) * mm, "end": v(-1.87, -22.76) * mm});
            skLineSegment(sketch, "E696", {"start": v(-1.87, -22.76) * mm, "end": v(-1.72, -22.81) * mm});
            skLineSegment(sketch, "E697", {"start": v(-1.72, -22.81) * mm, "end": v(-1.6, -22.88) * mm});
            skLineSegment(sketch, "E698", {"start": v(-1.6, -22.88) * mm, "end": v(-1.47, -22.97) * mm});
            skLineSegment(sketch, "E699", {"start": v(-1.47, -22.97) * mm, "end": v(-1.37, -23.07) * mm});
            skLineSegment(sketch, "E700", {"start": v(-1.37, -23.07) * mm, "end": v(-1.28, -23.2) * mm});
            skLineSegment(sketch, "E701", {"start": v(-1.28, -23.2) * mm, "end": v(-1.21, -23.32) * mm});
            skLineSegment(sketch, "E702", {"start": v(-1.21, -23.32) * mm, "end": v(-1.17, -23.47) * mm});
            skLineSegment(sketch, "E703", {"start": v(-1.17, -23.47) * mm, "end": v(-1.14, -23.61) * mm});
            skLineSegment(sketch, "E704", {"start": v(-1.14, -23.61) * mm, "end": v(-1.14, -23.76) * mm});
            skLineSegment(sketch, "E705", {"start": v(-1.14, -23.76) * mm, "end": v(-1.17, -23.91) * mm});
            skLineSegment(sketch, "E706", {"start": v(-1.17, -23.91) * mm, "end": v(-1.21, -24.05) * mm});
            skLineSegment(sketch, "E707", {"start": v(-1.21, -24.05) * mm, "end": v(-1.28, -24.19) * mm});
            skLineSegment(sketch, "E708", {"start": v(-1.28, -24.19) * mm, "end": v(-1.37, -24.3) * mm});
            skLineSegment(sketch, "E709", {"start": v(-1.37, -24.3) * mm, "end": v(-1.47, -24.41) * mm});
            skLineSegment(sketch, "E710", {"start": v(-1.47, -24.41) * mm, "end": v(-1.6, -24.5) * mm});
            skLineSegment(sketch, "E711", {"start": v(-1.6, -24.5) * mm, "end": v(-1.72, -24.57) * mm});
            skLineSegment(sketch, "E712", {"start": v(-1.72, -24.57) * mm, "end": v(-1.87, -24.62) * mm});
            skLineSegment(sketch, "E713", {"start": v(-1.87, -24.62) * mm, "end": v(-2.01, -24.64) * mm});
            skLineSegment(sketch, "E714", {"start": v(-2.01, -24.64) * mm, "end": v(-2.16, -24.64) * mm});
            skLineSegment(sketch, "E715", {"start": v(-2.16, -24.64) * mm, "end": v(-2.31, -24.62) * mm});
            skLineSegment(sketch, "E716", {"start": v(-2.31, -24.62) * mm, "end": v(-2.45, -24.57) * mm});
            skLineSegment(sketch, "E717", {"start": v(-2.45, -24.57) * mm, "end": v(-2.59, -24.5) * mm});
            skLineSegment(sketch, "E718", {"start": v(-2.59, -24.5) * mm, "end": v(-2.7, -24.41) * mm});
            skLineSegment(sketch, "E719", {"start": v(-2.7, -24.41) * mm, "end": v(-2.81, -24.3) * mm});
            skLineSegment(sketch, "E720", {"start": v(-2.81, -24.3) * mm, "end": v(-2.9, -24.19) * mm});
            skLineSegment(sketch, "E721", {"start": v(-2.9, -24.19) * mm, "end": v(-2.97, -24.05) * mm});
            skLineSegment(sketch, "E722", {"start": v(-2.97, -24.05) * mm, "end": v(-3.01, -23.91) * mm});
            skLineSegment(sketch, "E723", {"start": v(-3.01, -23.91) * mm, "end": v(-3.04, -23.76) * mm});
            skLineSegment(sketch, "E724", {"start": v(-3.04, -23.76) * mm, "end": v(-3.04, -23.61) * mm});
            skLineSegment(sketch, "E725", {"start": v(-3.04, -23.61) * mm, "end": v(-3.01, -23.47) * mm});
            skLineSegment(sketch, "E726", {"start": v(-3.01, -23.47) * mm, "end": v(-2.97, -23.32) * mm});
            skLineSegment(sketch, "E727", {"start": v(-2.97, -23.32) * mm, "end": v(-2.9, -23.2) * mm});
            skLineSegment(sketch, "E728", {"start": v(-2.9, -23.2) * mm, "end": v(-2.88, -23.15) * mm});
            skLineSegment(sketch, "E729", {"start": v(-2.88, -23.15) * mm, "end": v(-15.81, -10.21) * mm});
            skLineSegment(sketch, "E730", {"start": v(-15.81, -10.21) * mm, "end": v(-15.84, -10.15) * mm});
            skLineSegment(sketch, "E731", {"start": v(-15.84, -10.15) * mm, "end": v(-15.85, -10.1) * mm});
            skLineSegment(sketch, "E732", {"start": v(-15.85, -10.1) * mm, "end": v(-15.85, -6.44) * mm});
            skLineSegment(sketch, "E733", {"start": v(-15.85, -6.44) * mm, "end": v(-15.92, -6.4) * mm});
            skLineSegment(sketch, "E734", {"start": v(-15.92, -6.4) * mm, "end": v(-16.01, -6.33) * mm});
            skLineSegment(sketch, "E735", {"start": v(-16.01, -6.33) * mm, "end": v(-16.08, -6.25) * mm});
            skLineSegment(sketch, "E736", {"start": v(-16.08, -6.25) * mm, "end": v(-16.13, -6.14) * mm});
            skLineSegment(sketch, "E737", {"start": v(-16.13, -6.14) * mm, "end": v(-16.15, -6.03) * mm});
            skLineSegment(sketch, "E738", {"start": v(-16.15, -6.03) * mm, "end": v(-16.15, -5.92) * mm});
            skLineSegment(sketch, "E739", {"start": v(-16.15, -5.92) * mm, "end": v(-16.12, -5.8) * mm});
            skLineSegment(sketch, "E740", {"start": v(-16.12, -5.8) * mm, "end": v(-16.06, -5.7) * mm});
            skLineSegment(sketch, "E741", {"start": v(-16.06, -5.7) * mm, "end": v(-15.98, -5.63) * mm});
            skLineSegment(sketch, "E742", {"start": v(-15.98, -5.63) * mm, "end": v(-15.9, -5.56) * mm});
            skLineSegment(sketch, "E743", {"start": v(-15.9, -5.56) * mm, "end": v(-15.78, -5.52) * mm});
            skLineSegment(sketch, "E744", {"start": v(-15.78, -5.52) * mm, "end": v(-15.67, -5.51) * mm});
            skLineSegment(sketch, "E745", {"start": v(-15.67, -5.51) * mm, "end": v(-15.56, -5.52) * mm});
            skLineSegment(sketch, "E746", {"start": v(-15.56, -5.52) * mm, "end": v(-15.45, -5.56) * mm});
            skLineSegment(sketch, "E747", {"start": v(-15.45, -5.56) * mm, "end": v(-15.36, -5.63) * mm});
            skLineSegment(sketch, "E748", {"start": v(-15.36, -5.63) * mm, "end": v(-15.28, -5.7) * mm});
            skLineSegment(sketch, "E749", {"start": v(-15.28, -5.7) * mm, "end": v(-15.22, -5.8) * mm});
            skLineSegment(sketch, "E750", {"start": v(-15.22, -5.8) * mm, "end": v(-15.2, -5.92) * mm});
            skLineSegment(sketch, "E751", {"start": v(-15.2, -5.92) * mm, "end": v(-15.19, -6.03) * mm});
            skLineSegment(sketch, "E752", {"start": v(-17.73, -6.03) * mm, "end": v(-17.75, -6.14) * mm});
            skLineSegment(sketch, "E753", {"start": v(-17.75, -6.14) * mm, "end": v(-17.8, -6.25) * mm});
            skLineSegment(sketch, "E754", {"start": v(-17.8, -6.25) * mm, "end": v(-17.87, -6.33) * mm});
            skLineSegment(sketch, "E755", {"start": v(-17.87, -6.33) * mm, "end": v(-17.96, -6.4) * mm});
            skLineSegment(sketch, "E756", {"start": v(-17.96, -6.4) * mm, "end": v(-18.06, -6.45) * mm});
            skLineSegment(sketch, "E757", {"start": v(-18.06, -6.45) * mm, "end": v(-18.17, -6.47) * mm});
            skLineSegment(sketch, "E758", {"start": v(-18.17, -6.47) * mm, "end": v(-18.29, -6.47) * mm});
            skLineSegment(sketch, "E759", {"start": v(-18.29, -6.47) * mm, "end": v(-18.4, -6.44) * mm});
            skLineSegment(sketch, "E760", {"start": v(-18.4, -6.44) * mm, "end": v(-18.5, -6.38) * mm});
            skLineSegment(sketch, "E761", {"start": v(-18.5, -6.38) * mm, "end": v(-18.58, -6.3) * mm});
            skLineSegment(sketch, "E762", {"start": v(-18.58, -6.3) * mm, "end": v(-18.64, -6.21) * mm});
            skLineSegment(sketch, "E763", {"start": v(-18.64, -6.21) * mm, "end": v(-18.68, -6.1) * mm});
            skLineSegment(sketch, "E764", {"start": v(-18.68, -6.1) * mm, "end": v(-18.7, -6) * mm});
            skLineSegment(sketch, "E765", {"start": v(-18.7, -6) * mm, "end": v(-18.68, -5.88) * mm});
            skLineSegment(sketch, "E766", {"start": v(-18.68, -5.88) * mm, "end": v(-18.64, -5.77) * mm});
            skLineSegment(sketch, "E767", {"start": v(-18.64, -5.77) * mm, "end": v(-18.58, -5.68) * mm});
            skLineSegment(sketch, "E768", {"start": v(-18.58, -5.68) * mm, "end": v(-18.5, -5.6) * mm});
            skLineSegment(sketch, "E769", {"start": v(-18.5, -5.6) * mm, "end": v(-18.4, -5.55) * mm});
            skLineSegment(sketch, "E770", {"start": v(-18.4, -5.55) * mm, "end": v(-18.29, -5.52) * mm});
            skLineSegment(sketch, "E771", {"start": v(-18.29, -5.52) * mm, "end": v(-18.17, -5.51) * mm});
            skLineSegment(sketch, "E772", {"start": v(-18.17, -5.51) * mm, "end": v(-18.06, -5.53) * mm});
            skLineSegment(sketch, "E773", {"start": v(-18.06, -5.53) * mm, "end": v(-17.96, -5.58) * mm});
            skLineSegment(sketch, "E774", {"start": v(-17.96, -5.58) * mm, "end": v(-17.87, -5.65) * mm});
            skLineSegment(sketch, "E775", {"start": v(-17.87, -5.65) * mm, "end": v(-17.8, -5.74) * mm});
            skLineSegment(sketch, "E776", {"start": v(-17.8, -5.74) * mm, "end": v(-17.75, -5.84) * mm});
            skLineSegment(sketch, "E777", {"start": v(-17.75, -5.84) * mm, "end": v(-17.73, -5.96) * mm});
            skLineSegment(sketch, "E778", {"start": v(-17.73, -5.96) * mm, "end": v(-17.73, -6.03) * mm});
            skLineSegment(sketch, "E779", {"start": v(19, -0.23) * mm, "end": v(18.98, -0.34) * mm});
            skLineSegment(sketch, "E780", {"start": v(18.98, -0.34) * mm, "end": v(18.93, -0.44) * mm});
            skLineSegment(sketch, "E781", {"start": v(18.93, -0.44) * mm, "end": v(18.86, -0.53) * mm});
            skLineSegment(sketch, "E782", {"start": v(18.86, -0.53) * mm, "end": v(18.77, -0.6) * mm});
            skLineSegment(sketch, "E783", {"start": v(18.77, -0.6) * mm, "end": v(18.67, -0.65) * mm});
            skLineSegment(sketch, "E784", {"start": v(18.67, -0.65) * mm, "end": v(18.56, -0.68) * mm});
            skLineSegment(sketch, "E785", {"start": v(18.56, -0.68) * mm, "end": v(18.45, -0.67) * mm});
            skLineSegment(sketch, "E786", {"start": v(18.45, -0.67) * mm, "end": v(18.34, -0.64) * mm});
            skLineSegment(sketch, "E787", {"start": v(18.34, -0.64) * mm, "end": v(18.24, -0.58) * mm});
            skLineSegment(sketch, "E788", {"start": v(18.24, -0.58) * mm, "end": v(18.15, -0.5) * mm});
            skLineSegment(sketch, "E789", {"start": v(18.15, -0.5) * mm, "end": v(18.09, -0.41) * mm});
            skLineSegment(sketch, "E790", {"start": v(18.09, -0.41) * mm, "end": v(18.07, -0.37) * mm});
            skLineSegment(sketch, "E791", {"start": v(18.07, -0.37) * mm, "end": v(12.07, -0.37) * mm});
            skLineSegment(sketch, "E792", {"start": v(12.07, -0.37) * mm, "end": v(11.36, -1.08) * mm});
            skLineSegment(sketch, "E793", {"start": v(11.36, -1.08) * mm, "end": v(6.72, -5.73) * mm});
            skLineSegment(sketch, "E794", {"start": v(6.72, -5.73) * mm, "end": v(6.72, -6.9) * mm});
            skLineSegment(sketch, "E795", {"start": v(6.72, -6.9) * mm, "end": v(7.9, -8.07) * mm});
            skLineSegment(sketch, "E796", {"start": v(7.9, -8.07) * mm, "end": v(10.36, -8.08) * mm});
            skLineSegment(sketch, "E797", {"start": v(10.36, -8.08) * mm, "end": v(10.42, -8.1) * mm});
            skLineSegment(sketch, "E798", {"start": v(10.42, -8.1) * mm, "end": v(10.47, -8.13) * mm});
            skLineSegment(sketch, "E799", {"start": v(10.47, -8.13) * mm, "end": v(23.15, -20.8) * mm});
            skLineSegment(sketch, "E800", {"start": v(23.15, -20.8) * mm, "end": v(23.21, -20.82) * mm});
            skLineSegment(sketch, "E801", {"start": v(23.21, -20.82) * mm, "end": v(23.27, -20.86) * mm});
            skLineSegment(sketch, "E802", {"start": v(23.27, -20.86) * mm, "end": v(25.31, -22.9) * mm});
            skLineSegment(sketch, "E803", {"start": v(25.31, -22.9) * mm, "end": v(25.49, -22.81) * mm});
            skLineSegment(sketch, "E804", {"start": v(25.49, -22.81) * mm, "end": v(25.63, -22.76) * mm});
            skLineSegment(sketch, "E805", {"start": v(25.63, -22.76) * mm, "end": v(25.78, -22.74) * mm});
            skLineSegment(sketch, "E806", {"start": v(25.78, -22.74) * mm, "end": v(25.93, -22.74) * mm});
            skLineSegment(sketch, "E807", {"start": v(25.93, -22.74) * mm, "end": v(26.07, -22.76) * mm});
            skLineSegment(sketch, "E808", {"start": v(26.07, -22.76) * mm, "end": v(26.22, -22.81) * mm});
            skLineSegment(sketch, "E809", {"start": v(26.22, -22.81) * mm, "end": v(26.35, -22.88) * mm});
            skLineSegment(sketch, "E810", {"start": v(26.35, -22.88) * mm, "end": v(26.47, -22.97) * mm});
            skLineSegment(sketch, "E811", {"start": v(26.47, -22.97) * mm, "end": v(26.57, -23.07) * mm});
            skLineSegment(sketch, "E812", {"start": v(26.57, -23.07) * mm, "end": v(26.66, -23.2) * mm});
            skLineSegment(sketch, "E813", {"start": v(26.66, -23.2) * mm, "end": v(26.73, -23.32) * mm});
            skLineSegment(sketch, "E814", {"start": v(26.73, -23.32) * mm, "end": v(26.77, -23.47) * mm});
            skLineSegment(sketch, "E815", {"start": v(26.77, -23.47) * mm, "end": v(26.8, -23.61) * mm});
            skLineSegment(sketch, "E816", {"start": v(26.8, -23.61) * mm, "end": v(26.8, -23.76) * mm});
            skLineSegment(sketch, "E817", {"start": v(26.8, -23.76) * mm, "end": v(26.77, -23.91) * mm});
            skLineSegment(sketch, "E818", {"start": v(26.77, -23.91) * mm, "end": v(26.73, -24.05) * mm});
            skLineSegment(sketch, "E819", {"start": v(26.73, -24.05) * mm, "end": v(26.66, -24.19) * mm});
            skLineSegment(sketch, "E820", {"start": v(26.66, -24.19) * mm, "end": v(26.57, -24.3) * mm});
            skLineSegment(sketch, "E821", {"start": v(26.57, -24.3) * mm, "end": v(26.47, -24.41) * mm});
            skLineSegment(sketch, "E822", {"start": v(26.47, -24.41) * mm, "end": v(26.35, -24.5) * mm});
            skLineSegment(sketch, "E823", {"start": v(26.35, -24.5) * mm, "end": v(26.22, -24.57) * mm});
            skLineSegment(sketch, "E824", {"start": v(26.22, -24.57) * mm, "end": v(26.07, -24.62) * mm});
            skLineSegment(sketch, "E825", {"start": v(26.07, -24.62) * mm, "end": v(25.93, -24.64) * mm});
            skLineSegment(sketch, "E826", {"start": v(25.93, -24.64) * mm, "end": v(25.78, -24.64) * mm});
            skLineSegment(sketch, "E827", {"start": v(25.78, -24.64) * mm, "end": v(25.63, -24.62) * mm});
            skLineSegment(sketch, "E828", {"start": v(25.63, -24.62) * mm, "end": v(25.49, -24.57) * mm});
            skLineSegment(sketch, "E829", {"start": v(25.49, -24.57) * mm, "end": v(25.35, -24.5) * mm});
            skLineSegment(sketch, "E830", {"start": v(25.35, -24.5) * mm, "end": v(25.23, -24.41) * mm});
            skLineSegment(sketch, "E831", {"start": v(25.23, -24.41) * mm, "end": v(25.13, -24.3) * mm});
            skLineSegment(sketch, "E832", {"start": v(25.13, -24.3) * mm, "end": v(25.04, -24.19) * mm});
            skLineSegment(sketch, "E833", {"start": v(25.04, -24.19) * mm, "end": v(24.97, -24.05) * mm});
            skLineSegment(sketch, "E834", {"start": v(24.97, -24.05) * mm, "end": v(24.93, -23.91) * mm});
            skLineSegment(sketch, "E835", {"start": v(24.93, -23.91) * mm, "end": v(24.9, -23.76) * mm});
            skLineSegment(sketch, "E836", {"start": v(24.9, -23.76) * mm, "end": v(24.9, -23.61) * mm});
            skLineSegment(sketch, "E837", {"start": v(24.9, -23.61) * mm, "end": v(24.93, -23.47) * mm});
            skLineSegment(sketch, "E838", {"start": v(24.93, -23.47) * mm, "end": v(24.97, -23.32) * mm});
            skLineSegment(sketch, "E839", {"start": v(24.97, -23.32) * mm, "end": v(25.04, -23.2) * mm});
            skLineSegment(sketch, "E840", {"start": v(25.04, -23.2) * mm, "end": v(25.06, -23.15) * mm});
            skLineSegment(sketch, "E841", {"start": v(25.06, -23.15) * mm, "end": v(23.07, -21.16) * mm});
            skLineSegment(sketch, "E842", {"start": v(23.07, -21.16) * mm, "end": v(23, -21.15) * mm});
            skLineSegment(sketch, "E843", {"start": v(23, -21.15) * mm, "end": v(22.95, -21.1) * mm});
            skLineSegment(sketch, "E844", {"start": v(22.95, -21.1) * mm, "end": v(10.27, -8.43) * mm});
            skLineSegment(sketch, "E845", {"start": v(10.27, -8.43) * mm, "end": v(7.8, -8.43) * mm});
            skLineSegment(sketch, "E846", {"start": v(7.8, -8.43) * mm, "end": v(7.74, -8.4) * mm});
            skLineSegment(sketch, "E847", {"start": v(7.74, -8.4) * mm, "end": v(7.71, -8.38) * mm});
            skLineSegment(sketch, "E848", {"start": v(7.71, -8.38) * mm, "end": v(6.4, -7.06) * mm});
            skLineSegment(sketch, "E849", {"start": v(6.4, -7.06) * mm, "end": v(6.37, -7) * mm});
            skLineSegment(sketch, "E850", {"start": v(6.37, -7) * mm, "end": v(6.37, -6.29) * mm});
            skLineSegment(sketch, "E851", {"start": v(6.37, -6.29) * mm, "end": v(6.37, -5.6) * mm});
            skLineSegment(sketch, "E852", {"start": v(6.37, -5.6) * mm, "end": v(6.4, -5.54) * mm});
            skLineSegment(sketch, "E853", {"start": v(6.4, -5.54) * mm, "end": v(6.9, -5.04) * mm});
            skLineSegment(sketch, "E854", {"start": v(6.9, -5.04) * mm, "end": v(11.91, -0.04) * mm});
            skLineSegment(sketch, "E855", {"start": v(11.91, -0.04) * mm, "end": v(11.98, -0.02) * mm});
            skLineSegment(sketch, "E856", {"start": v(11.98, -0.02) * mm, "end": v(12.68, -0.02) * mm});
            skLineSegment(sketch, "E857", {"start": v(12.68, -0.02) * mm, "end": v(18.07, -0.02) * mm});
            skLineSegment(sketch, "E858", {"start": v(18.07, -0.02) * mm, "end": v(18.13, 0.1) * mm});
            skLineSegment(sketch, "E859", {"start": v(18.13, 0.1) * mm, "end": v(18.2, 0.17) * mm});
            skLineSegment(sketch, "E860", {"start": v(18.2, 0.17) * mm, "end": v(18.3, 0.24) * mm});
            skLineSegment(sketch, "E861", {"start": v(18.3, 0.24) * mm, "end": v(18.4, 0.28) * mm});
            skLineSegment(sketch, "E862", {"start": v(18.4, 0.28) * mm, "end": v(18.52, 0.29) * mm});
            skLineSegment(sketch, "E863", {"start": v(18.52, 0.29) * mm, "end": v(18.63, 0.28) * mm});
            skLineSegment(sketch, "E864", {"start": v(18.63, 0.28) * mm, "end": v(18.74, 0.24) * mm});
            skLineSegment(sketch, "E865", {"start": v(18.74, 0.24) * mm, "end": v(18.83, 0.17) * mm});
            skLineSegment(sketch, "E866", {"start": v(18.83, 0.17) * mm, "end": v(18.91, 0.1) * mm});
            skLineSegment(sketch, "E867", {"start": v(18.91, 0.1) * mm, "end": v(18.97, 0) * mm});
            skLineSegment(sketch, "E868", {"start": v(18.97, 0) * mm, "end": v(19, -0.12) * mm});
            skLineSegment(sketch, "E869", {"start": v(19, -0.12) * mm, "end": v(19, -0.23) * mm});
            skLineSegment(sketch, "E870", {"start": v(5.5, -2.54) * mm, "end": v(5.48, -2.65) * mm});
            skLineSegment(sketch, "E871", {"start": v(5.48, -2.65) * mm, "end": v(5.43, -2.75) * mm});
            skLineSegment(sketch, "E872", {"start": v(5.43, -2.75) * mm, "end": v(5.36, -2.84) * mm});
            skLineSegment(sketch, "E873", {"start": v(5.36, -2.84) * mm, "end": v(5.27, -2.91) * mm});
            skLineSegment(sketch, "E874", {"start": v(5.27, -2.91) * mm, "end": v(5.17, -2.96) * mm});
            skLineSegment(sketch, "E875", {"start": v(5.17, -2.96) * mm, "end": v(5.05, -2.98) * mm});
            skLineSegment(sketch, "E876", {"start": v(5.05, -2.98) * mm, "end": v(1.4, -6.63) * mm});
            skLineSegment(sketch, "E877", {"start": v(1.4, -6.63) * mm, "end": v(7.08, -12.3) * mm});
            skLineSegment(sketch, "E878", {"start": v(7.08, -12.3) * mm, "end": v(7.13, -12.34) * mm});
            skLineSegment(sketch, "E879", {"start": v(7.13, -12.34) * mm, "end": v(17.7, -22.9) * mm});
            skLineSegment(sketch, "E880", {"start": v(17.7, -22.9) * mm, "end": v(17.87, -22.81) * mm});
            skLineSegment(sketch, "E881", {"start": v(17.87, -22.81) * mm, "end": v(18, -22.76) * mm});
            skLineSegment(sketch, "E882", {"start": v(18, -22.76) * mm, "end": v(18.16, -22.74) * mm});
            skLineSegment(sketch, "E883", {"start": v(18.16, -22.74) * mm, "end": v(18.3, -22.74) * mm});
            skLineSegment(sketch, "E884", {"start": v(18.3, -22.74) * mm, "end": v(18.45, -22.76) * mm});
            skLineSegment(sketch, "E885", {"start": v(18.45, -22.76) * mm, "end": v(18.6, -22.81) * mm});
            skLineSegment(sketch, "E886", {"start": v(18.6, -22.81) * mm, "end": v(18.73, -22.88) * mm});
            skLineSegment(sketch, "E887", {"start": v(18.73, -22.88) * mm, "end": v(18.85, -22.97) * mm});
            skLineSegment(sketch, "E888", {"start": v(18.85, -22.97) * mm, "end": v(18.95, -23.07) * mm});
            skLineSegment(sketch, "E889", {"start": v(18.95, -23.07) * mm, "end": v(19.04, -23.2) * mm});
            skLineSegment(sketch, "E890", {"start": v(19.04, -23.2) * mm, "end": v(19.1, -23.32) * mm});
            skLineSegment(sketch, "E891", {"start": v(19.1, -23.32) * mm, "end": v(19.15, -23.47) * mm});
            skLineSegment(sketch, "E892", {"start": v(19.15, -23.47) * mm, "end": v(19.18, -23.61) * mm});
            skLineSegment(sketch, "E893", {"start": v(19.18, -23.61) * mm, "end": v(19.18, -23.76) * mm});
            skLineSegment(sketch, "E894", {"start": v(19.18, -23.76) * mm, "end": v(19.15, -23.91) * mm});
            skLineSegment(sketch, "E895", {"start": v(19.15, -23.91) * mm, "end": v(19.1, -24.05) * mm});
            skLineSegment(sketch, "E896", {"start": v(19.1, -24.05) * mm, "end": v(19.04, -24.19) * mm});
            skLineSegment(sketch, "E897", {"start": v(19.04, -24.19) * mm, "end": v(18.95, -24.3) * mm});
            skLineSegment(sketch, "E898", {"start": v(18.95, -24.3) * mm, "end": v(18.85, -24.41) * mm});
            skLineSegment(sketch, "E899", {"start": v(18.85, -24.41) * mm, "end": v(18.73, -24.5) * mm});
            skLineSegment(sketch, "E900", {"start": v(18.73, -24.5) * mm, "end": v(18.6, -24.57) * mm});
            skLineSegment(sketch, "E901", {"start": v(18.6, -24.57) * mm, "end": v(18.45, -24.62) * mm});
            skLineSegment(sketch, "E902", {"start": v(18.45, -24.62) * mm, "end": v(18.3, -24.64) * mm});
            skLineSegment(sketch, "E903", {"start": v(18.3, -24.64) * mm, "end": v(18.16, -24.64) * mm});
            skLineSegment(sketch, "E904", {"start": v(18.16, -24.64) * mm, "end": v(18, -24.62) * mm});
            skLineSegment(sketch, "E905", {"start": v(18, -24.62) * mm, "end": v(17.87, -24.57) * mm});
            skLineSegment(sketch, "E906", {"start": v(17.87, -24.57) * mm, "end": v(17.73, -24.5) * mm});
            skLineSegment(sketch, "E907", {"start": v(17.73, -24.5) * mm, "end": v(17.61, -24.41) * mm});
            skLineSegment(sketch, "E908", {"start": v(17.61, -24.41) * mm, "end": v(17.5, -24.3) * mm});
            skLineSegment(sketch, "E909", {"start": v(17.5, -24.3) * mm, "end": v(17.42, -24.19) * mm});
            skLineSegment(sketch, "E910", {"start": v(17.42, -24.19) * mm, "end": v(17.35, -24.05) * mm});
            skLineSegment(sketch, "E911", {"start": v(17.35, -24.05) * mm, "end": v(17.3, -23.91) * mm});
            skLineSegment(sketch, "E912", {"start": v(17.3, -23.91) * mm, "end": v(17.28, -23.76) * mm});
            skLineSegment(sketch, "E913", {"start": v(17.28, -23.76) * mm, "end": v(17.28, -23.61) * mm});
            skLineSegment(sketch, "E914", {"start": v(17.28, -23.61) * mm, "end": v(17.3, -23.47) * mm});
            skLineSegment(sketch, "E915", {"start": v(17.3, -23.47) * mm, "end": v(17.35, -23.32) * mm});
            skLineSegment(sketch, "E916", {"start": v(17.35, -23.32) * mm, "end": v(17.42, -23.2) * mm});
            skLineSegment(sketch, "E917", {"start": v(17.42, -23.2) * mm, "end": v(17.44, -23.15) * mm});
            skLineSegment(sketch, "E918", {"start": v(17.44, -23.15) * mm, "end": v(6.92, -12.64) * mm});
            skLineSegment(sketch, "E919", {"start": v(6.92, -12.64) * mm, "end": v(6.87, -12.6) * mm});
            skLineSegment(sketch, "E920", {"start": v(6.87, -12.6) * mm, "end": v(1, -6.74) * mm});
            skLineSegment(sketch, "E921", {"start": v(1, -6.74) * mm, "end": v(0.98, -6.68) * mm});
            skLineSegment(sketch, "E922", {"start": v(0.98, -6.68) * mm, "end": v(0.98, -6.6) * mm});
            skLineSegment(sketch, "E923", {"start": v(0.98, -6.6) * mm, "end": v(1, -6.54) * mm});
            skLineSegment(sketch, "E924", {"start": v(1, -6.54) * mm, "end": v(1.02, -6.5) * mm});
            skLineSegment(sketch, "E925", {"start": v(1.02, -6.5) * mm, "end": v(4.69, -2.85) * mm});
            skLineSegment(sketch, "E926", {"start": v(4.69, -2.85) * mm, "end": v(4.6, -2.75) * mm});
            skLineSegment(sketch, "E927", {"start": v(4.6, -2.75) * mm, "end": v(4.56, -2.65) * mm});
            skLineSegment(sketch, "E928", {"start": v(4.56, -2.65) * mm, "end": v(4.54, -2.54) * mm});
            skLineSegment(sketch, "E929", {"start": v(4.54, -2.54) * mm, "end": v(4.54, -2.43) * mm});
            skLineSegment(sketch, "E930", {"start": v(4.54, -2.43) * mm, "end": v(4.57, -2.32) * mm});
            skLineSegment(sketch, "E931", {"start": v(4.57, -2.32) * mm, "end": v(4.63, -2.22) * mm});
            skLineSegment(sketch, "E932", {"start": v(4.63, -2.22) * mm, "end": v(4.7, -2.13) * mm});
            skLineSegment(sketch, "E933", {"start": v(4.7, -2.13) * mm, "end": v(4.8, -2.07) * mm});
            skLineSegment(sketch, "E934", {"start": v(4.8, -2.07) * mm, "end": v(4.9, -2.03) * mm});
            skLineSegment(sketch, "E935", {"start": v(4.9, -2.03) * mm, "end": v(5.02, -2.02) * mm});
            skLineSegment(sketch, "E936", {"start": v(5.02, -2.02) * mm, "end": v(5.13, -2.03) * mm});
            skLineSegment(sketch, "E937", {"start": v(5.13, -2.03) * mm, "end": v(5.24, -2.07) * mm});
            skLineSegment(sketch, "E938", {"start": v(5.24, -2.07) * mm, "end": v(5.33, -2.13) * mm});
            skLineSegment(sketch, "E939", {"start": v(5.33, -2.13) * mm, "end": v(5.41, -2.22) * mm});
            skLineSegment(sketch, "E940", {"start": v(5.41, -2.22) * mm, "end": v(5.47, -2.32) * mm});
            skLineSegment(sketch, "E941", {"start": v(5.47, -2.32) * mm, "end": v(5.5, -2.43) * mm});
            skLineSegment(sketch, "E942", {"start": v(5.5, -2.43) * mm, "end": v(5.5, -2.54) * mm});
            skLineSegment(sketch, "E943", {"start": v(5.78, -3.91) * mm, "end": v(5.76, -4.03) * mm});
            skLineSegment(sketch, "E944", {"start": v(5.76, -4.03) * mm, "end": v(5.72, -4.13) * mm});
            skLineSegment(sketch, "E945", {"start": v(5.72, -4.13) * mm, "end": v(5.64, -4.22) * mm});
            skLineSegment(sketch, "E946", {"start": v(5.64, -4.22) * mm, "end": v(5.55, -4.29) * mm});
            skLineSegment(sketch, "E947", {"start": v(5.55, -4.29) * mm, "end": v(5.45, -4.34) * mm});
            skLineSegment(sketch, "E948", {"start": v(5.45, -4.34) * mm, "end": v(5.34, -4.36) * mm});
            skLineSegment(sketch, "E949", {"start": v(5.34, -4.36) * mm, "end": v(5.23, -4.35) * mm});
            skLineSegment(sketch, "E950", {"start": v(5.23, -4.35) * mm, "end": v(5.12, -4.32) * mm});
            skLineSegment(sketch, "E951", {"start": v(5.12, -4.32) * mm, "end": v(5.02, -4.27) * mm});
            skLineSegment(sketch, "E952", {"start": v(5.02, -4.27) * mm, "end": v(4.98, -4.23) * mm});
            skLineSegment(sketch, "E953", {"start": v(4.98, -4.23) * mm, "end": v(3.84, -5.37) * mm});
            skLineSegment(sketch, "E954", {"start": v(3.84, -5.37) * mm, "end": v(3.84, -6.52) * mm});
            skLineSegment(sketch, "E955", {"start": v(3.84, -6.52) * mm, "end": v(16.6, -19.28) * mm});
            skLineSegment(sketch, "E956", {"start": v(16.6, -19.28) * mm, "end": v(16.65, -19.32) * mm});
            skLineSegment(sketch, "E957", {"start": v(16.65, -19.32) * mm, "end": v(20.23, -22.9) * mm});
            skLineSegment(sketch, "E958", {"start": v(20.23, -22.9) * mm, "end": v(20.4, -22.81) * mm});
            skLineSegment(sketch, "E959", {"start": v(20.4, -22.81) * mm, "end": v(20.55, -22.76) * mm});
            skLineSegment(sketch, "E960", {"start": v(20.55, -22.76) * mm, "end": v(20.7, -22.74) * mm});
            skLineSegment(sketch, "E961", {"start": v(20.7, -22.74) * mm, "end": v(20.85, -22.74) * mm});
            skLineSegment(sketch, "E962", {"start": v(20.85, -22.74) * mm, "end": v(21, -22.76) * mm});
            skLineSegment(sketch, "E963", {"start": v(21, -22.76) * mm, "end": v(21.14, -22.81) * mm});
            skLineSegment(sketch, "E964", {"start": v(21.14, -22.81) * mm, "end": v(21.27, -22.88) * mm});
            skLineSegment(sketch, "E965", {"start": v(21.27, -22.88) * mm, "end": v(21.39, -22.97) * mm});
            skLineSegment(sketch, "E966", {"start": v(21.39, -22.97) * mm, "end": v(21.5, -23.07) * mm});
            skLineSegment(sketch, "E967", {"start": v(21.5, -23.07) * mm, "end": v(21.58, -23.2) * mm});
            skLineSegment(sketch, "E968", {"start": v(21.58, -23.2) * mm, "end": v(21.65, -23.32) * mm});
            skLineSegment(sketch, "E969", {"start": v(21.65, -23.32) * mm, "end": v(21.7, -23.47) * mm});
            skLineSegment(sketch, "E970", {"start": v(21.7, -23.47) * mm, "end": v(21.72, -23.61) * mm});
            skLineSegment(sketch, "E971", {"start": v(21.72, -23.61) * mm, "end": v(21.72, -23.76) * mm});
            skLineSegment(sketch, "E972", {"start": v(21.72, -23.76) * mm, "end": v(21.7, -23.91) * mm});
            skLineSegment(sketch, "E973", {"start": v(21.7, -23.91) * mm, "end": v(21.65, -24.05) * mm});
            skLineSegment(sketch, "E974", {"start": v(21.65, -24.05) * mm, "end": v(21.58, -24.19) * mm});
            skLineSegment(sketch, "E975", {"start": v(21.58, -24.19) * mm, "end": v(21.5, -24.3) * mm});
            skLineSegment(sketch, "E976", {"start": v(21.5, -24.3) * mm, "end": v(21.39, -24.41) * mm});
            skLineSegment(sketch, "E977", {"start": v(21.39, -24.41) * mm, "end": v(21.27, -24.5) * mm});
            skLineSegment(sketch, "E978", {"start": v(21.27, -24.5) * mm, "end": v(21.14, -24.57) * mm});
            skLineSegment(sketch, "E979", {"start": v(21.14, -24.57) * mm, "end": v(21, -24.62) * mm});
            skLineSegment(sketch, "E980", {"start": v(21, -24.62) * mm, "end": v(20.85, -24.64) * mm});
            skLineSegment(sketch, "E981", {"start": v(20.85, -24.64) * mm, "end": v(20.7, -24.64) * mm});
            skLineSegment(sketch, "E982", {"start": v(20.7, -24.64) * mm, "end": v(20.55, -24.62) * mm});
            skLineSegment(sketch, "E983", {"start": v(20.55, -24.62) * mm, "end": v(20.4, -24.57) * mm});
            skLineSegment(sketch, "E984", {"start": v(20.4, -24.57) * mm, "end": v(20.27, -24.5) * mm});
            skLineSegment(sketch, "E985", {"start": v(20.27, -24.5) * mm, "end": v(20.15, -24.41) * mm});
            skLineSegment(sketch, "E986", {"start": v(20.15, -24.41) * mm, "end": v(20.05, -24.3) * mm});
            skLineSegment(sketch, "E987", {"start": v(20.05, -24.3) * mm, "end": v(19.96, -24.19) * mm});
            skLineSegment(sketch, "E988", {"start": v(19.96, -24.19) * mm, "end": v(19.9, -24.05) * mm});
            skLineSegment(sketch, "E989", {"start": v(19.9, -24.05) * mm, "end": v(19.85, -23.91) * mm});
            skLineSegment(sketch, "E990", {"start": v(19.85, -23.91) * mm, "end": v(19.82, -23.76) * mm});
            skLineSegment(sketch, "E991", {"start": v(19.82, -23.76) * mm, "end": v(19.82, -23.61) * mm});
            skLineSegment(sketch, "E992", {"start": v(19.82, -23.61) * mm, "end": v(19.85, -23.47) * mm});
            skLineSegment(sketch, "E993", {"start": v(19.85, -23.47) * mm, "end": v(19.9, -23.32) * mm});
            skLineSegment(sketch, "E994", {"start": v(19.9, -23.32) * mm, "end": v(19.96, -23.2) * mm});
            skLineSegment(sketch, "E995", {"start": v(19.96, -23.2) * mm, "end": v(19.98, -23.15) * mm});
            skLineSegment(sketch, "E996", {"start": v(19.98, -23.15) * mm, "end": v(16.43, -19.6) * mm});
            skLineSegment(sketch, "E997", {"start": v(16.43, -19.6) * mm, "end": v(16.38, -19.57) * mm});
            skLineSegment(sketch, "E998", {"start": v(16.38, -19.57) * mm, "end": v(3.5, -6.69) * mm});
            skLineSegment(sketch, "E999", {"start": v(3.5, -6.69) * mm, "end": v(3.48, -6.62) * mm});
            skLineSegment(sketch, "E1000", {"start": v(3.48, -6.62) * mm, "end": v(3.48, -5.92) * mm});
            skLineSegment(sketch, "E1001", {"start": v(3.48, -5.92) * mm, "end": v(3.48, -5.26) * mm});
            skLineSegment(sketch, "E1002", {"start": v(3.48, -5.26) * mm, "end": v(3.51, -5.2) * mm});
            skLineSegment(sketch, "E1003", {"start": v(3.51, -5.2) * mm, "end": v(4.01, -4.7) * mm});
            skLineSegment(sketch, "E1004", {"start": v(4.01, -4.7) * mm, "end": v(4.82, -3.88) * mm});
            skLineSegment(sketch, "E1005", {"start": v(4.82, -3.88) * mm, "end": v(4.83, -3.76) * mm});
            skLineSegment(sketch, "E1006", {"start": v(4.83, -3.76) * mm, "end": v(4.87, -3.66) * mm});
            skLineSegment(sketch, "E1007", {"start": v(4.87, -3.66) * mm, "end": v(4.94, -3.56) * mm});
            skLineSegment(sketch, "E1008", {"start": v(4.94, -3.56) * mm, "end": v(5.02, -3.49) * mm});
            skLineSegment(sketch, "E1009", {"start": v(5.02, -3.49) * mm, "end": v(5.12, -3.43) * mm});
            skLineSegment(sketch, "E1010", {"start": v(5.12, -3.43) * mm, "end": v(5.23, -3.4) * mm});
            skLineSegment(sketch, "E1011", {"start": v(5.23, -3.4) * mm, "end": v(5.34, -3.4) * mm});
            skLineSegment(sketch, "E1012", {"start": v(5.34, -3.4) * mm, "end": v(5.45, -3.42) * mm});
            skLineSegment(sketch, "E1013", {"start": v(5.45, -3.42) * mm, "end": v(5.55, -3.46) * mm});
            skLineSegment(sketch, "E1014", {"start": v(5.55, -3.46) * mm, "end": v(5.64, -3.54) * mm});
            skLineSegment(sketch, "E1015", {"start": v(5.64, -3.54) * mm, "end": v(5.72, -3.62) * mm});
            skLineSegment(sketch, "E1016", {"start": v(5.72, -3.62) * mm, "end": v(5.76, -3.73) * mm});
            skLineSegment(sketch, "E1017", {"start": v(5.76, -3.73) * mm, "end": v(5.78, -3.84) * mm});
            skLineSegment(sketch, "E1018", {"start": v(5.78, -3.84) * mm, "end": v(5.78, -3.91) * mm});
            skLineSegment(sketch, "E1019", {"start": v(-4.57, 0.53) * mm, "end": v(-4.66, 0.49) * mm});
            skLineSegment(sketch, "E1020", {"start": v(-4.66, 0.49) * mm, "end": v(-4.77, 0.46) * mm});
            skLineSegment(sketch, "E1021", {"start": v(-4.77, 0.46) * mm, "end": v(-4.88, 0.47) * mm});
            skLineSegment(sketch, "E1022", {"start": v(-4.88, 0.47) * mm, "end": v(-5, 0.5) * mm});
            skLineSegment(sketch, "E1023", {"start": v(-5, 0.5) * mm, "end": v(-5.1, 0.56) * mm});
            skLineSegment(sketch, "E1024", {"start": v(-5.1, 0.56) * mm, "end": v(-5.18, 0.63) * mm});
            skLineSegment(sketch, "E1025", {"start": v(-5.18, 0.63) * mm, "end": v(-5.24, 0.73) * mm});
            skLineSegment(sketch, "E1026", {"start": v(-5.24, 0.73) * mm, "end": v(-5.28, 0.83) * mm});
            skLineSegment(sketch, "E1027", {"start": v(-5.28, 0.83) * mm, "end": v(-5.3, 0.95) * mm});
            skLineSegment(sketch, "E1028", {"start": v(-5.3, 0.95) * mm, "end": v(-5.28, 1.06) * mm});
            skLineSegment(sketch, "E1029", {"start": v(-5.28, 1.06) * mm, "end": v(-5.24, 1.17) * mm});
            skLineSegment(sketch, "E1030", {"start": v(-5.24, 1.17) * mm, "end": v(-5.18, 1.26) * mm});
            skLineSegment(sketch, "E1031", {"start": v(-5.18, 1.26) * mm, "end": v(-5.1, 1.34) * mm});
            skLineSegment(sketch, "E1032", {"start": v(-5.1, 1.34) * mm, "end": v(-5, 1.4) * mm});
            skLineSegment(sketch, "E1033", {"start": v(-5, 1.4) * mm, "end": v(-4.88, 1.42) * mm});
            skLineSegment(sketch, "E1034", {"start": v(-4.88, 1.42) * mm, "end": v(-4.77, 1.43) * mm});
            skLineSegment(sketch, "E1035", {"start": v(-4.77, 1.43) * mm, "end": v(-4.66, 1.4) * mm});
            skLineSegment(sketch, "E1036", {"start": v(-4.66, 1.4) * mm, "end": v(-4.56, 1.36) * mm});
            skLineSegment(sketch, "E1037", {"start": v(-4.56, 1.36) * mm, "end": v(-4.47, 1.29) * mm});
            skLineSegment(sketch, "E1038", {"start": v(-4.47, 1.29) * mm, "end": v(-4.4, 1.2) * mm});
            skLineSegment(sketch, "E1039", {"start": v(-4.4, 1.2) * mm, "end": v(-4.35, 1.1) * mm});
            skLineSegment(sketch, "E1040", {"start": v(-4.35, 1.1) * mm, "end": v(-4.33, 0.99) * mm});
            skLineSegment(sketch, "E1041", {"start": v(-4.33, 0.99) * mm, "end": v(-4.33, 0.95) * mm});
            skLineSegment(sketch, "E1042", {"start": v(-4.33, 0.95) * mm, "end": v(-4.27, 0.91) * mm});
            skLineSegment(sketch, "E1043", {"start": v(-4.27, 0.91) * mm, "end": v(-4.23, 0.86) * mm});
            skLineSegment(sketch, "E1044", {"start": v(-4.23, 0.86) * mm, "end": v(-4.22, 0.79) * mm});
            skLineSegment(sketch, "E1045", {"start": v(-4.22, 0.79) * mm, "end": v(-4.22, 0.78) * mm});
            skLineSegment(sketch, "E1046", {"start": v(-4.22, 0.78) * mm, "end": v(-4.22, -5.37) * mm});
            skLineSegment(sketch, "E1047", {"start": v(-4.22, -5.37) * mm, "end": v(-4.25, -5.44) * mm});
            skLineSegment(sketch, "E1048", {"start": v(-4.25, -5.44) * mm, "end": v(-4.75, -5.93) * mm});
            skLineSegment(sketch, "E1049", {"start": v(-4.75, -5.93) * mm, "end": v(-5.57, -6.75) * mm});
            skLineSegment(sketch, "E1050", {"start": v(-5.57, -6.75) * mm, "end": v(-5.57, -7.26) * mm});
            skLineSegment(sketch, "E1051", {"start": v(-5.57, -7.26) * mm, "end": v(10.07, -22.9) * mm});
            skLineSegment(sketch, "E1052", {"start": v(10.07, -22.9) * mm, "end": v(10.25, -22.81) * mm});
            skLineSegment(sketch, "E1053", {"start": v(10.25, -22.81) * mm, "end": v(10.39, -22.76) * mm});
            skLineSegment(sketch, "E1054", {"start": v(10.39, -22.76) * mm, "end": v(10.54, -22.74) * mm});
            skLineSegment(sketch, "E1055", {"start": v(10.54, -22.74) * mm, "end": v(10.69, -22.74) * mm});
            skLineSegment(sketch, "E1056", {"start": v(10.69, -22.74) * mm, "end": v(10.83, -22.76) * mm});
            skLineSegment(sketch, "E1057", {"start": v(10.83, -22.76) * mm, "end": v(10.98, -22.81) * mm});
            skLineSegment(sketch, "E1058", {"start": v(10.98, -22.81) * mm, "end": v(11.1, -22.88) * mm});
            skLineSegment(sketch, "E1059", {"start": v(11.1, -22.88) * mm, "end": v(11.23, -22.97) * mm});
            skLineSegment(sketch, "E1060", {"start": v(11.23, -22.97) * mm, "end": v(11.33, -23.07) * mm});
            skLineSegment(sketch, "E1061", {"start": v(11.33, -23.07) * mm, "end": v(11.42, -23.2) * mm});
            skLineSegment(sketch, "E1062", {"start": v(11.42, -23.2) * mm, "end": v(11.49, -23.32) * mm});
            skLineSegment(sketch, "E1063", {"start": v(11.49, -23.32) * mm, "end": v(11.53, -23.47) * mm});
            skLineSegment(sketch, "E1064", {"start": v(11.53, -23.47) * mm, "end": v(11.56, -23.61) * mm});
            skLineSegment(sketch, "E1065", {"start": v(11.56, -23.61) * mm, "end": v(11.56, -23.76) * mm});
            skLineSegment(sketch, "E1066", {"start": v(11.56, -23.76) * mm, "end": v(11.53, -23.91) * mm});
            skLineSegment(sketch, "E1067", {"start": v(11.53, -23.91) * mm, "end": v(11.49, -24.05) * mm});
            skLineSegment(sketch, "E1068", {"start": v(11.49, -24.05) * mm, "end": v(11.42, -24.19) * mm});
            skLineSegment(sketch, "E1069", {"start": v(11.42, -24.19) * mm, "end": v(11.33, -24.3) * mm});
            skLineSegment(sketch, "E1070", {"start": v(11.33, -24.3) * mm, "end": v(11.23, -24.41) * mm});
            skLineSegment(sketch, "E1071", {"start": v(11.23, -24.41) * mm, "end": v(11.1, -24.5) * mm});
            skLineSegment(sketch, "E1072", {"start": v(11.1, -24.5) * mm, "end": v(10.98, -24.57) * mm});
            skLineSegment(sketch, "E1073", {"start": v(10.98, -24.57) * mm, "end": v(10.83, -24.62) * mm});
            skLineSegment(sketch, "E1074", {"start": v(10.83, -24.62) * mm, "end": v(10.69, -24.64) * mm});
            skLineSegment(sketch, "E1075", {"start": v(10.69, -24.64) * mm, "end": v(10.54, -24.64) * mm});
            skLineSegment(sketch, "E1076", {"start": v(10.54, -24.64) * mm, "end": v(10.39, -24.62) * mm});
            skLineSegment(sketch, "E1077", {"start": v(10.39, -24.62) * mm, "end": v(10.25, -24.57) * mm});
            skLineSegment(sketch, "E1078", {"start": v(10.25, -24.57) * mm, "end": v(10.11, -24.5) * mm});
            skLineSegment(sketch, "E1079", {"start": v(10.11, -24.5) * mm, "end": v(10, -24.41) * mm});
            skLineSegment(sketch, "E1080", {"start": v(10, -24.41) * mm, "end": v(9.89, -24.3) * mm});
            skLineSegment(sketch, "E1081", {"start": v(9.89, -24.3) * mm, "end": v(9.8, -24.19) * mm});
            skLineSegment(sketch, "E1082", {"start": v(9.8, -24.19) * mm, "end": v(9.73, -24.05) * mm});
            skLineSegment(sketch, "E1083", {"start": v(9.73, -24.05) * mm, "end": v(9.69, -23.91) * mm});
            skLineSegment(sketch, "E1084", {"start": v(9.69, -23.91) * mm, "end": v(9.66, -23.76) * mm});
            skLineSegment(sketch, "E1085", {"start": v(9.66, -23.76) * mm, "end": v(9.66, -23.61) * mm});
            skLineSegment(sketch, "E1086", {"start": v(9.66, -23.61) * mm, "end": v(9.69, -23.47) * mm});
            skLineSegment(sketch, "E1087", {"start": v(9.69, -23.47) * mm, "end": v(9.73, -23.32) * mm});
            skLineSegment(sketch, "E1088", {"start": v(9.73, -23.32) * mm, "end": v(9.8, -23.2) * mm});
            skLineSegment(sketch, "E1089", {"start": v(9.8, -23.2) * mm, "end": v(9.82, -23.15) * mm});
            skLineSegment(sketch, "E1090", {"start": v(9.82, -23.15) * mm, "end": v(-5.88, -7.45) * mm});
            skLineSegment(sketch, "E1091", {"start": v(-5.88, -7.45) * mm, "end": v(-5.92, -7.39) * mm});
            skLineSegment(sketch, "E1092", {"start": v(-5.92, -7.39) * mm, "end": v(-5.92, -7.33) * mm});
            skLineSegment(sketch, "E1093", {"start": v(-5.92, -7.33) * mm, "end": v(-5.92, -6.64) * mm});
            skLineSegment(sketch, "E1094", {"start": v(-5.92, -6.64) * mm, "end": v(-5.9, -6.58) * mm});
            skLineSegment(sketch, "E1095", {"start": v(-5.9, -6.58) * mm, "end": v(-5.4, -6.08) * mm});
            skLineSegment(sketch, "E1096", {"start": v(-5.4, -6.08) * mm, "end": v(-4.58, -5.26) * mm});
            skLineSegment(sketch, "E1097", {"start": v(-4.58, -5.26) * mm, "end": v(-4.57, 0.53) * mm});
            skLineSegment(sketch, "E1098", {"start": v(6.44, 3.47) * mm, "end": v(6.42, 3.36) * mm});
            skLineSegment(sketch, "E1099", {"start": v(6.42, 3.36) * mm, "end": v(6.37, 3.25) * mm});
            skLineSegment(sketch, "E1100", {"start": v(6.37, 3.25) * mm, "end": v(6.3, 3.16) * mm});
            skLineSegment(sketch, "E1101", {"start": v(6.3, 3.16) * mm, "end": v(6.21, 3.1) * mm});
            skLineSegment(sketch, "E1102", {"start": v(6.21, 3.1) * mm, "end": v(6.1, 3.05) * mm});
            skLineSegment(sketch, "E1103", {"start": v(6.1, 3.05) * mm, "end": v(6, 3.03) * mm});
            skLineSegment(sketch, "E1104", {"start": v(6, 3.03) * mm, "end": v(5.97, 3.03) * mm});
            skLineSegment(sketch, "E1105", {"start": v(5.97, 3.03) * mm, "end": v(-3.78, -6.73) * mm});
            skLineSegment(sketch, "E1106", {"start": v(-3.78, -6.73) * mm, "end": v(-1.9, -8.6) * mm});
            skLineSegment(sketch, "E1107", {"start": v(-1.9, -8.6) * mm, "end": v(4.73, -15.23) * mm});
            skLineSegment(sketch, "E1108", {"start": v(4.73, -15.23) * mm, "end": v(4.79, -15.27) * mm});
            skLineSegment(sketch, "E1109", {"start": v(4.79, -15.27) * mm, "end": v(8.55, -19.03) * mm});
            skLineSegment(sketch, "E1110", {"start": v(8.55, -19.03) * mm, "end": v(8.62, -19.06) * mm});
            skLineSegment(sketch, "E1111", {"start": v(8.62, -19.06) * mm, "end": v(9.78, -20.23) * mm});
            skLineSegment(sketch, "E1112", {"start": v(9.78, -20.23) * mm, "end": v(12.53, -22.97) * mm});
            skLineSegment(sketch, "E1113", {"start": v(12.53, -22.97) * mm, "end": v(12.65, -22.88) * mm});
            skLineSegment(sketch, "E1114", {"start": v(12.65, -22.88) * mm, "end": v(12.79, -22.81) * mm});
            skLineSegment(sketch, "E1115", {"start": v(12.79, -22.81) * mm, "end": v(12.93, -22.76) * mm});
            skLineSegment(sketch, "E1116", {"start": v(12.93, -22.76) * mm, "end": v(13.08, -22.74) * mm});
            skLineSegment(sketch, "E1117", {"start": v(13.08, -22.74) * mm, "end": v(13.23, -22.74) * mm});
            skLineSegment(sketch, "E1118", {"start": v(13.23, -22.74) * mm, "end": v(13.37, -22.76) * mm});
            skLineSegment(sketch, "E1119", {"start": v(13.37, -22.76) * mm, "end": v(13.52, -22.81) * mm});
            skLineSegment(sketch, "E1120", {"start": v(13.52, -22.81) * mm, "end": v(13.65, -22.88) * mm});
            skLineSegment(sketch, "E1121", {"start": v(13.65, -22.88) * mm, "end": v(13.77, -22.97) * mm});
            skLineSegment(sketch, "E1122", {"start": v(13.77, -22.97) * mm, "end": v(13.87, -23.07) * mm});
            skLineSegment(sketch, "E1123", {"start": v(13.87, -23.07) * mm, "end": v(13.96, -23.2) * mm});
            skLineSegment(sketch, "E1124", {"start": v(13.96, -23.2) * mm, "end": v(14.03, -23.32) * mm});
            skLineSegment(sketch, "E1125", {"start": v(14.03, -23.32) * mm, "end": v(14.07, -23.47) * mm});
            skLineSegment(sketch, "E1126", {"start": v(14.07, -23.47) * mm, "end": v(14.1, -23.61) * mm});
            skLineSegment(sketch, "E1127", {"start": v(14.1, -23.61) * mm, "end": v(14.1, -23.76) * mm});
            skLineSegment(sketch, "E1128", {"start": v(14.1, -23.76) * mm, "end": v(14.07, -23.91) * mm});
            skLineSegment(sketch, "E1129", {"start": v(14.07, -23.91) * mm, "end": v(14.03, -24.05) * mm});
            skLineSegment(sketch, "E1130", {"start": v(14.03, -24.05) * mm, "end": v(13.96, -24.19) * mm});
            skLineSegment(sketch, "E1131", {"start": v(13.96, -24.19) * mm, "end": v(13.87, -24.3) * mm});
            skLineSegment(sketch, "E1132", {"start": v(13.87, -24.3) * mm, "end": v(13.77, -24.41) * mm});
            skLineSegment(sketch, "E1133", {"start": v(13.77, -24.41) * mm, "end": v(13.65, -24.5) * mm});
            skLineSegment(sketch, "E1134", {"start": v(13.65, -24.5) * mm, "end": v(13.52, -24.57) * mm});
            skLineSegment(sketch, "E1135", {"start": v(13.52, -24.57) * mm, "end": v(13.37, -24.62) * mm});
            skLineSegment(sketch, "E1136", {"start": v(13.37, -24.62) * mm, "end": v(13.23, -24.64) * mm});
            skLineSegment(sketch, "E1137", {"start": v(13.23, -24.64) * mm, "end": v(13.08, -24.64) * mm});
            skLineSegment(sketch, "E1138", {"start": v(13.08, -24.64) * mm, "end": v(12.93, -24.62) * mm});
            skLineSegment(sketch, "E1139", {"start": v(12.93, -24.62) * mm, "end": v(12.79, -24.57) * mm});
            skLineSegment(sketch, "E1140", {"start": v(12.79, -24.57) * mm, "end": v(12.65, -24.5) * mm});
            skLineSegment(sketch, "E1141", {"start": v(12.65, -24.5) * mm, "end": v(12.53, -24.41) * mm});
            skLineSegment(sketch, "E1142", {"start": v(12.53, -24.41) * mm, "end": v(12.43, -24.3) * mm});
            skLineSegment(sketch, "E1143", {"start": v(12.43, -24.3) * mm, "end": v(12.34, -24.19) * mm});
            skLineSegment(sketch, "E1144", {"start": v(12.34, -24.19) * mm, "end": v(12.27, -24.05) * mm});
            skLineSegment(sketch, "E1145", {"start": v(12.27, -24.05) * mm, "end": v(12.23, -23.91) * mm});
            skLineSegment(sketch, "E1146", {"start": v(12.23, -23.91) * mm, "end": v(12.2, -23.76) * mm});
            skLineSegment(sketch, "E1147", {"start": v(12.2, -23.76) * mm, "end": v(12.2, -23.61) * mm});
            skLineSegment(sketch, "E1148", {"start": v(12.2, -23.61) * mm, "end": v(12.23, -23.47) * mm});
            skLineSegment(sketch, "E1149", {"start": v(12.23, -23.47) * mm, "end": v(12.27, -23.32) * mm});
            skLineSegment(sketch, "E1150", {"start": v(12.27, -23.32) * mm, "end": v(12.3, -23.25) * mm});
            skLineSegment(sketch, "E1151", {"start": v(12.3, -23.25) * mm, "end": v(8.47, -19.42) * mm});
            skLineSegment(sketch, "E1152", {"start": v(8.47, -19.42) * mm, "end": v(8.4, -19.39) * mm});
            skLineSegment(sketch, "E1153", {"start": v(8.4, -19.39) * mm, "end": v(7.23, -18.22) * mm});
            skLineSegment(sketch, "E1154", {"start": v(7.23, -18.22) * mm, "end": v(4.57, -15.56) * mm});
            skLineSegment(sketch, "E1155", {"start": v(4.57, -15.56) * mm, "end": v(4.51, -15.52) * mm});
            skLineSegment(sketch, "E1156", {"start": v(4.51, -15.52) * mm, "end": v(-4.18, -6.83) * mm});
            skLineSegment(sketch, "E1157", {"start": v(-4.18, -6.83) * mm, "end": v(-4.2, -6.76) * mm});
            skLineSegment(sketch, "E1158", {"start": v(-4.2, -6.76) * mm, "end": v(-4.2, -6.7) * mm});
            skLineSegment(sketch, "E1159", {"start": v(-4.2, -6.7) * mm, "end": v(-4.19, -6.63) * mm});
            skLineSegment(sketch, "E1160", {"start": v(-4.19, -6.63) * mm, "end": v(-4.16, -6.6) * mm});
            skLineSegment(sketch, "E1161", {"start": v(-4.16, -6.6) * mm, "end": v(5.6, 3.17) * mm});
            skLineSegment(sketch, "E1162", {"start": v(5.6, 3.17) * mm, "end": v(5.53, 3.29) * mm});
            skLineSegment(sketch, "E1163", {"start": v(5.53, 3.29) * mm, "end": v(5.5, 3.4) * mm});
            skLineSegment(sketch, "E1164", {"start": v(5.5, 3.4) * mm, "end": v(5.48, 3.5) * mm});
            skLineSegment(sketch, "E1165", {"start": v(5.48, 3.5) * mm, "end": v(5.5, 3.62) * mm});
            skLineSegment(sketch, "E1166", {"start": v(5.5, 3.62) * mm, "end": v(5.53, 3.73) * mm});
            skLineSegment(sketch, "E1167", {"start": v(5.53, 3.73) * mm, "end": v(5.6, 3.82) * mm});
            skLineSegment(sketch, "E1168", {"start": v(5.6, 3.82) * mm, "end": v(5.68, 3.9) * mm});
            skLineSegment(sketch, "E1169", {"start": v(5.68, 3.9) * mm, "end": v(5.78, 3.95) * mm});
            skLineSegment(sketch, "E1170", {"start": v(5.78, 3.95) * mm, "end": v(5.89, 3.98) * mm});
            skLineSegment(sketch, "E1171", {"start": v(5.89, 3.98) * mm, "end": v(6, 3.99) * mm});
            skLineSegment(sketch, "E1172", {"start": v(6, 3.99) * mm, "end": v(6.1, 3.96) * mm});
            skLineSegment(sketch, "E1173", {"start": v(6.1, 3.96) * mm, "end": v(6.21, 3.92) * mm});
            skLineSegment(sketch, "E1174", {"start": v(6.21, 3.92) * mm, "end": v(6.3, 3.85) * mm});
            skLineSegment(sketch, "E1175", {"start": v(6.3, 3.85) * mm, "end": v(6.37, 3.76) * mm});
            skLineSegment(sketch, "E1176", {"start": v(6.37, 3.76) * mm, "end": v(6.42, 3.66) * mm});
            skLineSegment(sketch, "E1177", {"start": v(6.42, 3.66) * mm, "end": v(6.44, 3.54) * mm});
            skLineSegment(sketch, "E1178", {"start": v(6.44, 3.54) * mm, "end": v(6.44, 3.47) * mm});
            skLineSegment(sketch, "E1179", {"start": v(9.27, 3.43) * mm, "end": v(9.25, 3.32) * mm});
            skLineSegment(sketch, "E1180", {"start": v(9.25, 3.32) * mm, "end": v(9.2, 3.22) * mm});
            skLineSegment(sketch, "E1181", {"start": v(9.2, 3.22) * mm, "end": v(9.13, 3.13) * mm});
            skLineSegment(sketch, "E1182", {"start": v(9.13, 3.13) * mm, "end": v(9.04, 3.06) * mm});
            skLineSegment(sketch, "E1183", {"start": v(9.04, 3.06) * mm, "end": v(8.96, 3.02) * mm});
            skLineSegment(sketch, "E1184", {"start": v(8.96, 3.02) * mm, "end": v(8.96, -2.35) * mm});
            skLineSegment(sketch, "E1185", {"start": v(8.96, -2.35) * mm, "end": v(8.94, -2.41) * mm});
            skLineSegment(sketch, "E1186", {"start": v(8.94, -2.41) * mm, "end": v(8.91, -2.45) * mm});
            skLineSegment(sketch, "E1187", {"start": v(8.91, -2.45) * mm, "end": v(5.04, -6.32) * mm});
            skLineSegment(sketch, "E1188", {"start": v(5.04, -6.32) * mm, "end": v(7.5, -8.8) * mm});
            skLineSegment(sketch, "E1189", {"start": v(7.5, -8.8) * mm, "end": v(8.62, -8.8) * mm});
            skLineSegment(sketch, "E1190", {"start": v(8.62, -8.8) * mm, "end": v(8.68, -8.83) * mm});
            skLineSegment(sketch, "E1191", {"start": v(8.68, -8.83) * mm, "end": v(9.18, -9.32) * mm});
            skLineSegment(sketch, "E1192", {"start": v(9.18, -9.32) * mm, "end": v(9.49, -9.62) * mm});
            skLineSegment(sketch, "E1193", {"start": v(9.49, -9.62) * mm, "end": v(9.61, -9.74) * mm});
            skLineSegment(sketch, "E1194", {"start": v(9.61, -9.74) * mm, "end": v(22.78, -22.9) * mm});
            skLineSegment(sketch, "E1195", {"start": v(22.78, -22.9) * mm, "end": v(22.88, -22.84) * mm});
            skLineSegment(sketch, "E1196", {"start": v(22.88, -22.84) * mm, "end": v(23.01, -22.78) * mm});
            skLineSegment(sketch, "E1197", {"start": v(23.01, -22.78) * mm, "end": v(23.16, -22.75) * mm});
            skLineSegment(sketch, "E1198", {"start": v(23.16, -22.75) * mm, "end": v(23.3, -22.74) * mm});
            skLineSegment(sketch, "E1199", {"start": v(23.3, -22.74) * mm, "end": v(23.46, -22.75) * mm});
            skLineSegment(sketch, "E1200", {"start": v(23.46, -22.75) * mm, "end": v(23.6, -22.78) * mm});
            skLineSegment(sketch, "E1201", {"start": v(23.6, -22.78) * mm, "end": v(23.74, -22.84) * mm});
            skLineSegment(sketch, "E1202", {"start": v(23.74, -22.84) * mm, "end": v(23.87, -22.92) * mm});
            skLineSegment(sketch, "E1203", {"start": v(23.87, -22.92) * mm, "end": v(23.98, -23.02) * mm});
            skLineSegment(sketch, "E1204", {"start": v(23.98, -23.02) * mm, "end": v(24.08, -23.13) * mm});
            skLineSegment(sketch, "E1205", {"start": v(24.08, -23.13) * mm, "end": v(24.16, -23.26) * mm});
            skLineSegment(sketch, "E1206", {"start": v(24.16, -23.26) * mm, "end": v(24.21, -23.4) * mm});
            skLineSegment(sketch, "E1207", {"start": v(24.21, -23.4) * mm, "end": v(24.25, -23.54) * mm});
            skLineSegment(sketch, "E1208", {"start": v(24.25, -23.54) * mm, "end": v(24.26, -23.7) * mm});
            skLineSegment(sketch, "E1209", {"start": v(24.26, -23.7) * mm, "end": v(24.25, -23.84) * mm});
            skLineSegment(sketch, "E1210", {"start": v(24.25, -23.84) * mm, "end": v(24.21, -23.99) * mm});
            skLineSegment(sketch, "E1211", {"start": v(24.21, -23.99) * mm, "end": v(24.16, -24.12) * mm});
            skLineSegment(sketch, "E1212", {"start": v(24.16, -24.12) * mm, "end": v(24.08, -24.25) * mm});
            skLineSegment(sketch, "E1213", {"start": v(24.08, -24.25) * mm, "end": v(23.98, -24.36) * mm});
            skLineSegment(sketch, "E1214", {"start": v(23.98, -24.36) * mm, "end": v(23.87, -24.46) * mm});
            skLineSegment(sketch, "E1215", {"start": v(23.87, -24.46) * mm, "end": v(23.74, -24.54) * mm});
            skLineSegment(sketch, "E1216", {"start": v(23.74, -24.54) * mm, "end": v(23.6, -24.6) * mm});
            skLineSegment(sketch, "E1217", {"start": v(23.6, -24.6) * mm, "end": v(23.46, -24.63) * mm});
            skLineSegment(sketch, "E1218", {"start": v(23.46, -24.63) * mm, "end": v(23.3, -24.64) * mm});
            skLineSegment(sketch, "E1219", {"start": v(23.3, -24.64) * mm, "end": v(23.16, -24.63) * mm});
            skLineSegment(sketch, "E1220", {"start": v(23.16, -24.63) * mm, "end": v(23.01, -24.6) * mm});
            skLineSegment(sketch, "E1221", {"start": v(23.01, -24.6) * mm, "end": v(22.88, -24.54) * mm});
            skLineSegment(sketch, "E1222", {"start": v(22.88, -24.54) * mm, "end": v(22.75, -24.46) * mm});
            skLineSegment(sketch, "E1223", {"start": v(22.75, -24.46) * mm, "end": v(22.64, -24.36) * mm});
            skLineSegment(sketch, "E1224", {"start": v(22.64, -24.36) * mm, "end": v(22.54, -24.25) * mm});
            skLineSegment(sketch, "E1225", {"start": v(22.54, -24.25) * mm, "end": v(22.46, -24.12) * mm});
            skLineSegment(sketch, "E1226", {"start": v(22.46, -24.12) * mm, "end": v(22.4, -23.99) * mm});
            skLineSegment(sketch, "E1227", {"start": v(22.4, -23.99) * mm, "end": v(22.37, -23.84) * mm});
            skLineSegment(sketch, "E1228", {"start": v(22.37, -23.84) * mm, "end": v(22.36, -23.7) * mm});
            skLineSegment(sketch, "E1229", {"start": v(22.36, -23.7) * mm, "end": v(22.37, -23.54) * mm});
            skLineSegment(sketch, "E1230", {"start": v(22.37, -23.54) * mm, "end": v(22.4, -23.4) * mm});
            skLineSegment(sketch, "E1231", {"start": v(22.4, -23.4) * mm, "end": v(22.46, -23.26) * mm});
            skLineSegment(sketch, "E1232", {"start": v(22.46, -23.26) * mm, "end": v(22.52, -23.15) * mm});
            skLineSegment(sketch, "E1233", {"start": v(22.52, -23.15) * mm, "end": v(9.3, -9.94) * mm});
            skLineSegment(sketch, "E1234", {"start": v(9.3, -9.94) * mm, "end": v(9.25, -9.9) * mm});
            skLineSegment(sketch, "E1235", {"start": v(9.25, -9.9) * mm, "end": v(8.5, -9.15) * mm});
            skLineSegment(sketch, "E1236", {"start": v(8.5, -9.15) * mm, "end": v(7.4, -9.14) * mm});
            skLineSegment(sketch, "E1237", {"start": v(7.4, -9.14) * mm, "end": v(7.33, -9.11) * mm});
            skLineSegment(sketch, "E1238", {"start": v(7.33, -9.11) * mm, "end": v(6.83, -8.62) * mm});
            skLineSegment(sketch, "E1239", {"start": v(6.83, -8.62) * mm, "end": v(4.69, -6.47) * mm});
            skLineSegment(sketch, "E1240", {"start": v(4.69, -6.47) * mm, "end": v(4.66, -6.4) * mm});
            skLineSegment(sketch, "E1241", {"start": v(4.66, -6.4) * mm, "end": v(4.66, -6.24) * mm});
            skLineSegment(sketch, "E1242", {"start": v(4.66, -6.24) * mm, "end": v(4.69, -6.17) * mm});
            skLineSegment(sketch, "E1243", {"start": v(4.69, -6.17) * mm, "end": v(4.71, -6.14) * mm});
            skLineSegment(sketch, "E1244", {"start": v(4.71, -6.14) * mm, "end": v(8.6, -2.25) * mm});
            skLineSegment(sketch, "E1245", {"start": v(8.6, -2.25) * mm, "end": v(8.6, 3.02) * mm});
            skLineSegment(sketch, "E1246", {"start": v(8.6, 3.02) * mm, "end": v(8.5, 3.08) * mm});
            skLineSegment(sketch, "E1247", {"start": v(8.5, 3.08) * mm, "end": v(8.42, 3.16) * mm});
            skLineSegment(sketch, "E1248", {"start": v(8.42, 3.16) * mm, "end": v(8.36, 3.25) * mm});
            skLineSegment(sketch, "E1249", {"start": v(8.36, 3.25) * mm, "end": v(8.32, 3.36) * mm});
            skLineSegment(sketch, "E1250", {"start": v(8.32, 3.36) * mm, "end": v(8.3, 3.47) * mm});
            skLineSegment(sketch, "E1251", {"start": v(8.3, 3.47) * mm, "end": v(8.32, 3.58) * mm});
            skLineSegment(sketch, "E1252", {"start": v(8.32, 3.58) * mm, "end": v(8.36, 3.69) * mm});
            skLineSegment(sketch, "E1253", {"start": v(8.36, 3.69) * mm, "end": v(8.42, 3.78) * mm});
            skLineSegment(sketch, "E1254", {"start": v(8.42, 3.78) * mm, "end": v(8.5, 3.86) * mm});
            skLineSegment(sketch, "E1255", {"start": v(8.5, 3.86) * mm, "end": v(8.6, 3.92) * mm});
            skLineSegment(sketch, "E1256", {"start": v(8.6, 3.92) * mm, "end": v(8.71, 3.95) * mm});
            skLineSegment(sketch, "E1257", {"start": v(8.71, 3.95) * mm, "end": v(8.82, 3.95) * mm});
            skLineSegment(sketch, "E1258", {"start": v(8.82, 3.95) * mm, "end": v(8.94, 3.93) * mm});
            skLineSegment(sketch, "E1259", {"start": v(8.94, 3.93) * mm, "end": v(9.04, 3.88) * mm});
            skLineSegment(sketch, "E1260", {"start": v(9.04, 3.88) * mm, "end": v(9.13, 3.8) * mm});
            skLineSegment(sketch, "E1261", {"start": v(9.13, 3.8) * mm, "end": v(9.2, 3.72) * mm});
            skLineSegment(sketch, "E1262", {"start": v(9.2, 3.72) * mm, "end": v(9.25, 3.62) * mm});
            skLineSegment(sketch, "E1263", {"start": v(9.25, 3.62) * mm, "end": v(9.27, 3.5) * mm});
            skLineSegment(sketch, "E1264", {"start": v(9.27, 3.5) * mm, "end": v(9.27, 3.43) * mm});
            skLineSegment(sketch, "E1265", {"start": v(6.62, 1.05) * mm, "end": v(6.6, 0.94) * mm});
            skLineSegment(sketch, "E1266", {"start": v(6.6, 0.94) * mm, "end": v(6.55, 0.84) * mm});
            skLineSegment(sketch, "E1267", {"start": v(6.55, 0.84) * mm, "end": v(6.48, 0.74) * mm});
            skLineSegment(sketch, "E1268", {"start": v(6.48, 0.74) * mm, "end": v(6.4, 0.68) * mm});
            skLineSegment(sketch, "E1269", {"start": v(6.4, 0.68) * mm, "end": v(6.29, 0.63) * mm});
            skLineSegment(sketch, "E1270", {"start": v(6.29, 0.63) * mm, "end": v(6.18, 0.6) * mm});
            skLineSegment(sketch, "E1271", {"start": v(6.18, 0.6) * mm, "end": v(6.07, 0.6) * mm});
            skLineSegment(sketch, "E1272", {"start": v(6.07, 0.6) * mm, "end": v(5.96, 0.64) * mm});
            skLineSegment(sketch, "E1273", {"start": v(5.96, 0.64) * mm, "end": v(5.86, 0.7) * mm});
            skLineSegment(sketch, "E1274", {"start": v(5.86, 0.7) * mm, "end": v(5.84, 0.71) * mm});
            skLineSegment(sketch, "E1275", {"start": v(5.84, 0.71) * mm, "end": v(-1.1, -6.23) * mm});
            skLineSegment(sketch, "E1276", {"start": v(-1.1, -6.23) * mm, "end": v(-1.1, -6.62) * mm});
            skLineSegment(sketch, "E1277", {"start": v(-1.1, -6.62) * mm, "end": v(6.44, -14.17) * mm});
            skLineSegment(sketch, "E1278", {"start": v(6.44, -14.17) * mm, "end": v(6.46, -14.2) * mm});
            skLineSegment(sketch, "E1279", {"start": v(6.46, -14.2) * mm, "end": v(15.15, -22.9) * mm});
            skLineSegment(sketch, "E1280", {"start": v(15.15, -22.9) * mm, "end": v(15.33, -22.81) * mm});
            skLineSegment(sketch, "E1281", {"start": v(15.33, -22.81) * mm, "end": v(15.47, -22.76) * mm});
            skLineSegment(sketch, "E1282", {"start": v(15.47, -22.76) * mm, "end": v(15.62, -22.74) * mm});
            skLineSegment(sketch, "E1283", {"start": v(15.62, -22.74) * mm, "end": v(15.77, -22.74) * mm});
            skLineSegment(sketch, "E1284", {"start": v(15.77, -22.74) * mm, "end": v(15.91, -22.76) * mm});
            skLineSegment(sketch, "E1285", {"start": v(15.91, -22.76) * mm, "end": v(16.06, -22.81) * mm});
            skLineSegment(sketch, "E1286", {"start": v(16.06, -22.81) * mm, "end": v(16.19, -22.88) * mm});
            skLineSegment(sketch, "E1287", {"start": v(16.19, -22.88) * mm, "end": v(16.3, -22.97) * mm});
            skLineSegment(sketch, "E1288", {"start": v(16.3, -22.97) * mm, "end": v(16.41, -23.07) * mm});
            skLineSegment(sketch, "E1289", {"start": v(16.41, -23.07) * mm, "end": v(16.5, -23.2) * mm});
            skLineSegment(sketch, "E1290", {"start": v(16.5, -23.2) * mm, "end": v(16.57, -23.32) * mm});
            skLineSegment(sketch, "E1291", {"start": v(16.57, -23.32) * mm, "end": v(16.61, -23.47) * mm});
            skLineSegment(sketch, "E1292", {"start": v(16.61, -23.47) * mm, "end": v(16.64, -23.61) * mm});
            skLineSegment(sketch, "E1293", {"start": v(16.64, -23.61) * mm, "end": v(16.64, -23.76) * mm});
            skLineSegment(sketch, "E1294", {"start": v(16.64, -23.76) * mm, "end": v(16.61, -23.91) * mm});
            skLineSegment(sketch, "E1295", {"start": v(16.61, -23.91) * mm, "end": v(16.57, -24.05) * mm});
            skLineSegment(sketch, "E1296", {"start": v(16.57, -24.05) * mm, "end": v(16.5, -24.19) * mm});
            skLineSegment(sketch, "E1297", {"start": v(16.5, -24.19) * mm, "end": v(16.41, -24.3) * mm});
            skLineSegment(sketch, "E1298", {"start": v(16.41, -24.3) * mm, "end": v(16.3, -24.41) * mm});
            skLineSegment(sketch, "E1299", {"start": v(16.3, -24.41) * mm, "end": v(16.19, -24.5) * mm});
            skLineSegment(sketch, "E1300", {"start": v(16.19, -24.5) * mm, "end": v(16.06, -24.57) * mm});
            skLineSegment(sketch, "E1301", {"start": v(16.06, -24.57) * mm, "end": v(15.91, -24.62) * mm});
            skLineSegment(sketch, "E1302", {"start": v(15.91, -24.62) * mm, "end": v(15.77, -24.64) * mm});
            skLineSegment(sketch, "E1303", {"start": v(15.77, -24.64) * mm, "end": v(15.62, -24.64) * mm});
            skLineSegment(sketch, "E1304", {"start": v(15.62, -24.64) * mm, "end": v(15.47, -24.62) * mm});
            skLineSegment(sketch, "E1305", {"start": v(15.47, -24.62) * mm, "end": v(15.33, -24.57) * mm});
            skLineSegment(sketch, "E1306", {"start": v(15.33, -24.57) * mm, "end": v(15.2, -24.5) * mm});
            skLineSegment(sketch, "E1307", {"start": v(15.2, -24.5) * mm, "end": v(15.07, -24.41) * mm});
            skLineSegment(sketch, "E1308", {"start": v(15.07, -24.41) * mm, "end": v(14.97, -24.3) * mm});
            skLineSegment(sketch, "E1309", {"start": v(14.97, -24.3) * mm, "end": v(14.88, -24.19) * mm});
            skLineSegment(sketch, "E1310", {"start": v(14.88, -24.19) * mm, "end": v(14.81, -24.05) * mm});
            skLineSegment(sketch, "E1311", {"start": v(14.81, -24.05) * mm, "end": v(14.77, -23.91) * mm});
            skLineSegment(sketch, "E1312", {"start": v(14.77, -23.91) * mm, "end": v(14.74, -23.76) * mm});
            skLineSegment(sketch, "E1313", {"start": v(14.74, -23.76) * mm, "end": v(14.74, -23.61) * mm});
            skLineSegment(sketch, "E1314", {"start": v(14.74, -23.61) * mm, "end": v(14.77, -23.47) * mm});
            skLineSegment(sketch, "E1315", {"start": v(14.77, -23.47) * mm, "end": v(14.81, -23.32) * mm});
            skLineSegment(sketch, "E1316", {"start": v(14.81, -23.32) * mm, "end": v(14.88, -23.2) * mm});
            skLineSegment(sketch, "E1317", {"start": v(14.88, -23.2) * mm, "end": v(14.9, -23.15) * mm});
            skLineSegment(sketch, "E1318", {"start": v(14.9, -23.15) * mm, "end": v(6.15, -14.4) * mm});
            skLineSegment(sketch, "E1319", {"start": v(6.15, -14.4) * mm, "end": v(6.12, -14.35) * mm});
            skLineSegment(sketch, "E1320", {"start": v(6.12, -14.35) * mm, "end": v(-1.43, -6.8) * mm});
            skLineSegment(sketch, "E1321", {"start": v(-1.43, -6.8) * mm, "end": v(-1.46, -6.73) * mm});
            skLineSegment(sketch, "E1322", {"start": v(-1.46, -6.73) * mm, "end": v(-1.47, -6.7) * mm});
            skLineSegment(sketch, "E1323", {"start": v(-1.47, -6.7) * mm, "end": v(-1.46, -6.12) * mm});
            skLineSegment(sketch, "E1324", {"start": v(-1.46, -6.12) * mm, "end": v(-1.43, -6.06) * mm});
            skLineSegment(sketch, "E1325", {"start": v(-1.43, -6.06) * mm, "end": v(-0.93, -5.55) * mm});
            skLineSegment(sketch, "E1326", {"start": v(-0.93, -5.55) * mm, "end": v(5.66, 1.04) * mm});
            skLineSegment(sketch, "E1327", {"start": v(5.66, 1.04) * mm, "end": v(5.66, 1.13) * mm});
            skLineSegment(sketch, "E1328", {"start": v(5.66, 1.13) * mm, "end": v(5.68, 1.24) * mm});
            skLineSegment(sketch, "E1329", {"start": v(5.68, 1.24) * mm, "end": v(5.73, 1.34) * mm});
            skLineSegment(sketch, "E1330", {"start": v(5.73, 1.34) * mm, "end": v(5.8, 1.43) * mm});
            skLineSegment(sketch, "E1331", {"start": v(5.8, 1.43) * mm, "end": v(5.89, 1.5) * mm});
            skLineSegment(sketch, "E1332", {"start": v(5.89, 1.5) * mm, "end": v(6, 1.55) * mm});
            skLineSegment(sketch, "E1333", {"start": v(6, 1.55) * mm, "end": v(6.1, 1.57) * mm});
            skLineSegment(sketch, "E1334", {"start": v(6.1, 1.57) * mm, "end": v(6.22, 1.56) * mm});
            skLineSegment(sketch, "E1335", {"start": v(6.22, 1.56) * mm, "end": v(6.32, 1.53) * mm});
            skLineSegment(sketch, "E1336", {"start": v(6.32, 1.53) * mm, "end": v(6.42, 1.48) * mm});
            skLineSegment(sketch, "E1337", {"start": v(6.42, 1.48) * mm, "end": v(6.5, 1.4) * mm});
            skLineSegment(sketch, "E1338", {"start": v(6.5, 1.4) * mm, "end": v(6.57, 1.3) * mm});
            skLineSegment(sketch, "E1339", {"start": v(6.57, 1.3) * mm, "end": v(6.6, 1.2) * mm});
            skLineSegment(sketch, "E1340", {"start": v(6.6, 1.2) * mm, "end": v(6.62, 1.09) * mm});
            skLineSegment(sketch, "E1341", {"start": v(6.62, 1.09) * mm, "end": v(6.62, 1.05) * mm});
            skLineSegment(sketch, "E1342", {"start": v(14.77, -5.64) * mm, "end": v(15.6, -5.64) * mm});
            skLineSegment(sketch, "E1343", {"start": v(15.6, -5.64) * mm, "end": v(15.6, -5.95) * mm});
            skLineSegment(sketch, "E1344", {"start": v(15.6, -5.95) * mm, "end": v(16.07, -5.95) * mm});
            skLineSegment(sketch, "E1345", {"start": v(16.07, -5.95) * mm, "end": v(30.17, -5.95) * mm});
            skLineSegment(sketch, "E1346", {"start": v(30.17, -5.95) * mm, "end": v(30.23, -5.98) * mm});
            skLineSegment(sketch, "E1347", {"start": v(30.23, -5.98) * mm, "end": v(30.73, -6.48) * mm});
            skLineSegment(sketch, "E1348", {"start": v(30.73, -6.48) * mm, "end": v(36, -11.74) * mm});
            skLineSegment(sketch, "E1349", {"start": v(36, -11.74) * mm, "end": v(36.17, -11.65) * mm});
            skLineSegment(sketch, "E1350", {"start": v(36.17, -11.65) * mm, "end": v(36.3, -11.6) * mm});
            skLineSegment(sketch, "E1351", {"start": v(36.3, -11.6) * mm, "end": v(36.45, -11.58) * mm});
            skLineSegment(sketch, "E1352", {"start": v(36.45, -11.58) * mm, "end": v(36.6, -11.58) * mm});
            skLineSegment(sketch, "E1353", {"start": v(36.6, -11.58) * mm, "end": v(36.75, -11.6) * mm});
            skLineSegment(sketch, "E1354", {"start": v(36.75, -11.6) * mm, "end": v(36.9, -11.65) * mm});
            skLineSegment(sketch, "E1355", {"start": v(36.9, -11.65) * mm, "end": v(37.03, -11.72) * mm});
            skLineSegment(sketch, "E1356", {"start": v(37.03, -11.72) * mm, "end": v(37.15, -11.81) * mm});
            skLineSegment(sketch, "E1357", {"start": v(37.15, -11.81) * mm, "end": v(37.25, -11.92) * mm});
            skLineSegment(sketch, "E1358", {"start": v(37.25, -11.92) * mm, "end": v(37.34, -12.04) * mm});
            skLineSegment(sketch, "E1359", {"start": v(37.34, -12.04) * mm, "end": v(37.4, -12.17) * mm});
            skLineSegment(sketch, "E1360", {"start": v(37.4, -12.17) * mm, "end": v(37.45, -12.31) * mm});
            skLineSegment(sketch, "E1361", {"start": v(37.45, -12.31) * mm, "end": v(37.48, -12.46) * mm});
            skLineSegment(sketch, "E1362", {"start": v(37.48, -12.46) * mm, "end": v(37.48, -12.6) * mm});
            skLineSegment(sketch, "E1363", {"start": v(37.48, -12.6) * mm, "end": v(37.45, -12.76) * mm});
            skLineSegment(sketch, "E1364", {"start": v(37.45, -12.76) * mm, "end": v(37.4, -12.9) * mm});
            skLineSegment(sketch, "E1365", {"start": v(37.4, -12.9) * mm, "end": v(37.34, -13.03) * mm});
            skLineSegment(sketch, "E1366", {"start": v(37.34, -13.03) * mm, "end": v(37.25, -13.15) * mm});
            skLineSegment(sketch, "E1367", {"start": v(37.25, -13.15) * mm, "end": v(37.15, -13.26) * mm});
            skLineSegment(sketch, "E1368", {"start": v(37.15, -13.26) * mm, "end": v(37.03, -13.35) * mm});
            skLineSegment(sketch, "E1369", {"start": v(37.03, -13.35) * mm, "end": v(36.9, -13.41) * mm});
            skLineSegment(sketch, "E1370", {"start": v(36.9, -13.41) * mm, "end": v(36.75, -13.46) * mm});
            skLineSegment(sketch, "E1371", {"start": v(36.75, -13.46) * mm, "end": v(36.6, -13.48) * mm});
            skLineSegment(sketch, "E1372", {"start": v(36.6, -13.48) * mm, "end": v(36.45, -13.48) * mm});
            skLineSegment(sketch, "E1373", {"start": v(36.45, -13.48) * mm, "end": v(36.3, -13.46) * mm});
            skLineSegment(sketch, "E1374", {"start": v(36.3, -13.46) * mm, "end": v(36.17, -13.41) * mm});
            skLineSegment(sketch, "E1375", {"start": v(36.17, -13.41) * mm, "end": v(36.03, -13.35) * mm});
            skLineSegment(sketch, "E1376", {"start": v(36.03, -13.35) * mm, "end": v(35.91, -13.26) * mm});
            skLineSegment(sketch, "E1377", {"start": v(35.91, -13.26) * mm, "end": v(35.8, -13.15) * mm});
            skLineSegment(sketch, "E1378", {"start": v(35.8, -13.15) * mm, "end": v(35.72, -13.03) * mm});
            skLineSegment(sketch, "E1379", {"start": v(35.72, -13.03) * mm, "end": v(35.65, -12.9) * mm});
            skLineSegment(sketch, "E1380", {"start": v(35.65, -12.9) * mm, "end": v(35.6, -12.76) * mm});
            skLineSegment(sketch, "E1381", {"start": v(35.6, -12.76) * mm, "end": v(35.58, -12.6) * mm});
            skLineSegment(sketch, "E1382", {"start": v(35.58, -12.6) * mm, "end": v(35.58, -12.46) * mm});
            skLineSegment(sketch, "E1383", {"start": v(35.58, -12.46) * mm, "end": v(35.6, -12.31) * mm});
            skLineSegment(sketch, "E1384", {"start": v(35.6, -12.31) * mm, "end": v(35.65, -12.17) * mm});
            skLineSegment(sketch, "E1385", {"start": v(35.65, -12.17) * mm, "end": v(35.72, -12.04) * mm});
            skLineSegment(sketch, "E1386", {"start": v(35.72, -12.04) * mm, "end": v(35.74, -12) * mm});
            skLineSegment(sketch, "E1387", {"start": v(35.74, -12) * mm, "end": v(30.05, -6.3) * mm});
            skLineSegment(sketch, "E1388", {"start": v(30.05, -6.3) * mm, "end": v(25.11, -6.3) * mm});
            skLineSegment(sketch, "E1389", {"start": v(25.11, -6.3) * mm, "end": v(15.6, -6.3) * mm});
            skLineSegment(sketch, "E1390", {"start": v(15.6, -6.3) * mm, "end": v(15.6, -6.6) * mm});
            skLineSegment(sketch, "E1391", {"start": v(15.6, -6.6) * mm, "end": v(15.3, -6.6) * mm});
            skLineSegment(sketch, "E1392", {"start": v(15.3, -6.6) * mm, "end": v(15.3, -7.07) * mm});
            skLineSegment(sketch, "E1393", {"start": v(15.3, -7.07) * mm, "end": v(15.3, -7.8) * mm});
            skLineSegment(sketch, "E1394", {"start": v(15.3, -7.8) * mm, "end": v(22.81, -15.32) * mm});
            skLineSegment(sketch, "E1395", {"start": v(22.81, -15.32) * mm, "end": v(30.23, -22.74) * mm});
            skLineSegment(sketch, "E1396", {"start": v(30.23, -22.74) * mm, "end": v(31.88, -22.74) * mm});
            skLineSegment(sketch, "E1397", {"start": v(31.88, -22.74) * mm, "end": v(31.88, -24.64) * mm});
            skLineSegment(sketch, "E1398", {"start": v(31.88, -24.64) * mm, "end": v(29.98, -24.64) * mm});
            skLineSegment(sketch, "E1399", {"start": v(29.98, -24.64) * mm, "end": v(29.98, -22.99) * mm});
            skLineSegment(sketch, "E1400", {"start": v(29.98, -22.99) * mm, "end": v(28.7, -21.7) * mm});
            skLineSegment(sketch, "E1401", {"start": v(28.7, -21.7) * mm, "end": v(14.97, -7.97) * mm});
            skLineSegment(sketch, "E1402", {"start": v(14.97, -7.97) * mm, "end": v(14.95, -7.9) * mm});
            skLineSegment(sketch, "E1403", {"start": v(14.95, -7.9) * mm, "end": v(14.94, -7.2) * mm});
            skLineSegment(sketch, "E1404", {"start": v(14.94, -7.2) * mm, "end": v(14.94, -6.6) * mm});
            skLineSegment(sketch, "E1405", {"start": v(14.94, -6.6) * mm, "end": v(14.64, -6.6) * mm});
            skLineSegment(sketch, "E1406", {"start": v(14.64, -6.6) * mm, "end": v(14.64, -5.64) * mm});
            skLineSegment(sketch, "E1407", {"start": v(14.64, -5.64) * mm, "end": v(14.77, -5.64) * mm});
            skLineSegment(sketch, "E1408", {"start": v(7.63, -5.7) * mm, "end": v(8.46, -5.7) * mm});
            skLineSegment(sketch, "E1409", {"start": v(8.46, -5.7) * mm, "end": v(8.46, -6) * mm});
            skLineSegment(sketch, "E1410", {"start": v(8.46, -6) * mm, "end": v(8.92, -6) * mm});
            skLineSegment(sketch, "E1411", {"start": v(8.92, -6) * mm, "end": v(12.24, -6) * mm});
            skLineSegment(sketch, "E1412", {"start": v(12.24, -6) * mm, "end": v(13.82, -4.43) * mm});
            skLineSegment(sketch, "E1413", {"start": v(13.82, -4.43) * mm, "end": v(14.14, -4.11) * mm});
            skLineSegment(sketch, "E1414", {"start": v(14.14, -4.11) * mm, "end": v(14.2, -4.09) * mm});
            skLineSegment(sketch, "E1415", {"start": v(14.2, -4.09) * mm, "end": v(14.9, -4.08) * mm});
            skLineSegment(sketch, "E1416", {"start": v(14.9, -4.08) * mm, "end": v(30.84, -4.09) * mm});
            skLineSegment(sketch, "E1417", {"start": v(30.84, -4.09) * mm, "end": v(30.9, -4.12) * mm});
            skLineSegment(sketch, "E1418", {"start": v(30.9, -4.12) * mm, "end": v(31.4, -4.62) * mm});
            skLineSegment(sketch, "E1419", {"start": v(31.4, -4.62) * mm, "end": v(35.83, -9.04) * mm});
            skLineSegment(sketch, "E1420", {"start": v(35.83, -9.04) * mm, "end": v(37.48, -9.04) * mm});
            skLineSegment(sketch, "E1421", {"start": v(37.48, -9.04) * mm, "end": v(37.48, -10.94) * mm});
            skLineSegment(sketch, "E1422", {"start": v(37.48, -10.94) * mm, "end": v(35.58, -10.94) * mm});
            skLineSegment(sketch, "E1423", {"start": v(35.58, -10.94) * mm, "end": v(35.58, -9.29) * mm});
            skLineSegment(sketch, "E1424", {"start": v(35.58, -9.29) * mm, "end": v(34.3, -8.01) * mm});
            skLineSegment(sketch, "E1425", {"start": v(34.3, -8.01) * mm, "end": v(30.73, -4.44) * mm});
            skLineSegment(sketch, "E1426", {"start": v(30.73, -4.44) * mm, "end": v(14.3, -4.44) * mm});
            skLineSegment(sketch, "E1427", {"start": v(14.3, -4.44) * mm, "end": v(13.5, -5.25) * mm});
            skLineSegment(sketch, "E1428", {"start": v(13.5, -5.25) * mm, "end": v(12.4, -6.33) * mm});
            skLineSegment(sketch, "E1429", {"start": v(12.4, -6.33) * mm, "end": v(12.34, -6.36) * mm});
            skLineSegment(sketch, "E1430", {"start": v(12.34, -6.36) * mm, "end": v(11.64, -6.36) * mm});
            skLineSegment(sketch, "E1431", {"start": v(11.64, -6.36) * mm, "end": v(11.15, -6.36) * mm});
            skLineSegment(sketch, "E1432", {"start": v(11.15, -6.36) * mm, "end": v(13.46, -8.68) * mm});
            skLineSegment(sketch, "E1433", {"start": v(13.46, -8.68) * mm, "end": v(13.6, -8.68) * mm});
            skLineSegment(sketch, "E1434", {"start": v(13.6, -8.68) * mm, "end": v(13.66, -8.7) * mm});
            skLineSegment(sketch, "E1435", {"start": v(13.66, -8.7) * mm, "end": v(14.16, -9.2) * mm});
            skLineSegment(sketch, "E1436", {"start": v(14.16, -9.2) * mm, "end": v(27.85, -22.9) * mm});
            skLineSegment(sketch, "E1437", {"start": v(27.85, -22.9) * mm, "end": v(28.03, -22.81) * mm});
            skLineSegment(sketch, "E1438", {"start": v(28.03, -22.81) * mm, "end": v(28.17, -22.76) * mm});
            skLineSegment(sketch, "E1439", {"start": v(28.17, -22.76) * mm, "end": v(28.32, -22.74) * mm});
            skLineSegment(sketch, "E1440", {"start": v(28.32, -22.74) * mm, "end": v(28.47, -22.74) * mm});
            skLineSegment(sketch, "E1441", {"start": v(28.47, -22.74) * mm, "end": v(28.61, -22.76) * mm});
            skLineSegment(sketch, "E1442", {"start": v(28.61, -22.76) * mm, "end": v(28.76, -22.81) * mm});
            skLineSegment(sketch, "E1443", {"start": v(28.76, -22.81) * mm, "end": v(28.89, -22.88) * mm});
            skLineSegment(sketch, "E1444", {"start": v(28.89, -22.88) * mm, "end": v(29, -22.97) * mm});
            skLineSegment(sketch, "E1445", {"start": v(29, -22.97) * mm, "end": v(29.11, -23.07) * mm});
            skLineSegment(sketch, "E1446", {"start": v(29.11, -23.07) * mm, "end": v(29.2, -23.2) * mm});
            skLineSegment(sketch, "E1447", {"start": v(29.2, -23.2) * mm, "end": v(29.27, -23.32) * mm});
            skLineSegment(sketch, "E1448", {"start": v(29.27, -23.32) * mm, "end": v(29.31, -23.47) * mm});
            skLineSegment(sketch, "E1449", {"start": v(29.31, -23.47) * mm, "end": v(29.34, -23.61) * mm});
            skLineSegment(sketch, "E1450", {"start": v(29.34, -23.61) * mm, "end": v(29.34, -23.76) * mm});
            skLineSegment(sketch, "E1451", {"start": v(29.34, -23.76) * mm, "end": v(29.31, -23.91) * mm});
            skLineSegment(sketch, "E1452", {"start": v(29.31, -23.91) * mm, "end": v(29.27, -24.05) * mm});
            skLineSegment(sketch, "E1453", {"start": v(29.27, -24.05) * mm, "end": v(29.2, -24.19) * mm});
            skLineSegment(sketch, "E1454", {"start": v(29.2, -24.19) * mm, "end": v(29.11, -24.3) * mm});
            skLineSegment(sketch, "E1455", {"start": v(29.11, -24.3) * mm, "end": v(29, -24.41) * mm});
            skLineSegment(sketch, "E1456", {"start": v(29, -24.41) * mm, "end": v(28.89, -24.5) * mm});
            skLineSegment(sketch, "E1457", {"start": v(28.89, -24.5) * mm, "end": v(28.76, -24.57) * mm});
            skLineSegment(sketch, "E1458", {"start": v(28.76, -24.57) * mm, "end": v(28.61, -24.62) * mm});
            skLineSegment(sketch, "E1459", {"start": v(28.61, -24.62) * mm, "end": v(28.47, -24.64) * mm});
            skLineSegment(sketch, "E1460", {"start": v(28.47, -24.64) * mm, "end": v(28.32, -24.64) * mm});
            skLineSegment(sketch, "E1461", {"start": v(28.32, -24.64) * mm, "end": v(28.17, -24.62) * mm});
            skLineSegment(sketch, "E1462", {"start": v(28.17, -24.62) * mm, "end": v(28.03, -24.57) * mm});
            skLineSegment(sketch, "E1463", {"start": v(28.03, -24.57) * mm, "end": v(27.9, -24.5) * mm});
            skLineSegment(sketch, "E1464", {"start": v(27.9, -24.5) * mm, "end": v(27.77, -24.41) * mm});
            skLineSegment(sketch, "E1465", {"start": v(27.77, -24.41) * mm, "end": v(27.67, -24.3) * mm});
            skLineSegment(sketch, "E1466", {"start": v(27.67, -24.3) * mm, "end": v(27.58, -24.19) * mm});
            skLineSegment(sketch, "E1467", {"start": v(27.58, -24.19) * mm, "end": v(27.51, -24.05) * mm});
            skLineSegment(sketch, "E1468", {"start": v(27.51, -24.05) * mm, "end": v(27.47, -23.91) * mm});
            skLineSegment(sketch, "E1469", {"start": v(27.47, -23.91) * mm, "end": v(27.44, -23.76) * mm});
            skLineSegment(sketch, "E1470", {"start": v(27.44, -23.76) * mm, "end": v(27.44, -23.61) * mm});
            skLineSegment(sketch, "E1471", {"start": v(27.44, -23.61) * mm, "end": v(27.47, -23.47) * mm});
            skLineSegment(sketch, "E1472", {"start": v(27.47, -23.47) * mm, "end": v(27.51, -23.32) * mm});
            skLineSegment(sketch, "E1473", {"start": v(27.51, -23.32) * mm, "end": v(27.58, -23.2) * mm});
            skLineSegment(sketch, "E1474", {"start": v(27.58, -23.2) * mm, "end": v(27.6, -23.15) * mm});
            skLineSegment(sketch, "E1475", {"start": v(27.6, -23.15) * mm, "end": v(13.48, -9.03) * mm});
            skLineSegment(sketch, "E1476", {"start": v(13.48, -9.03) * mm, "end": v(13.35, -9.03) * mm});
            skLineSegment(sketch, "E1477", {"start": v(13.35, -9.03) * mm, "end": v(13.28, -9) * mm});
            skLineSegment(sketch, "E1478", {"start": v(13.28, -9) * mm, "end": v(12.78, -8.5) * mm});
            skLineSegment(sketch, "E1479", {"start": v(12.78, -8.5) * mm, "end": v(10.64, -6.36) * mm});
            skLineSegment(sketch, "E1480", {"start": v(10.64, -6.36) * mm, "end": v(8.45, -6.36) * mm});
            skLineSegment(sketch, "E1481", {"start": v(8.45, -6.36) * mm, "end": v(8.46, -6.66) * mm});
            skLineSegment(sketch, "E1482", {"start": v(8.46, -6.66) * mm, "end": v(7.5, -6.66) * mm});
            skLineSegment(sketch, "E1483", {"start": v(7.5, -6.66) * mm, "end": v(7.5, -5.7) * mm});
            skLineSegment(sketch, "E1484", {"start": v(7.5, -5.7) * mm, "end": v(7.63, -5.7) * mm});
            skLineSegment(sketch, "E1485", {"start": v(9.02, -23.76) * mm, "end": v(9, -23.91) * mm});
            skLineSegment(sketch, "E1486", {"start": v(9, -23.91) * mm, "end": v(8.95, -24.05) * mm});
            skLineSegment(sketch, "E1487", {"start": v(8.95, -24.05) * mm, "end": v(8.88, -24.19) * mm});
            skLineSegment(sketch, "E1488", {"start": v(8.88, -24.19) * mm, "end": v(8.8, -24.3) * mm});
            skLineSegment(sketch, "E1489", {"start": v(8.8, -24.3) * mm, "end": v(8.69, -24.41) * mm});
            skLineSegment(sketch, "E1490", {"start": v(8.69, -24.41) * mm, "end": v(8.57, -24.5) * mm});
            skLineSegment(sketch, "E1491", {"start": v(8.57, -24.5) * mm, "end": v(8.44, -24.57) * mm});
            skLineSegment(sketch, "E1492", {"start": v(8.44, -24.57) * mm, "end": v(8.3, -24.62) * mm});
            skLineSegment(sketch, "E1493", {"start": v(8.3, -24.62) * mm, "end": v(8.15, -24.64) * mm});
            skLineSegment(sketch, "E1494", {"start": v(8.15, -24.64) * mm, "end": v(8, -24.64) * mm});
            skLineSegment(sketch, "E1495", {"start": v(8, -24.64) * mm, "end": v(7.85, -24.62) * mm});
            skLineSegment(sketch, "E1496", {"start": v(7.85, -24.62) * mm, "end": v(7.7, -24.57) * mm});
            skLineSegment(sketch, "E1497", {"start": v(7.7, -24.57) * mm, "end": v(7.57, -24.5) * mm});
            skLineSegment(sketch, "E1498", {"start": v(7.57, -24.5) * mm, "end": v(7.45, -24.41) * mm});
            skLineSegment(sketch, "E1499", {"start": v(7.45, -24.41) * mm, "end": v(7.35, -24.3) * mm});
            skLineSegment(sketch, "E1500", {"start": v(7.35, -24.3) * mm, "end": v(7.26, -24.19) * mm});
            skLineSegment(sketch, "E1501", {"start": v(7.26, -24.19) * mm, "end": v(7.2, -24.05) * mm});
            skLineSegment(sketch, "E1502", {"start": v(7.2, -24.05) * mm, "end": v(7.15, -23.91) * mm});
            skLineSegment(sketch, "E1503", {"start": v(7.15, -23.91) * mm, "end": v(7.12, -23.76) * mm});
            skLineSegment(sketch, "E1504", {"start": v(7.12, -23.76) * mm, "end": v(7.12, -23.61) * mm});
            skLineSegment(sketch, "E1505", {"start": v(7.12, -23.61) * mm, "end": v(7.15, -23.47) * mm});
            skLineSegment(sketch, "E1506", {"start": v(7.15, -23.47) * mm, "end": v(7.2, -23.32) * mm});
            skLineSegment(sketch, "E1507", {"start": v(7.2, -23.32) * mm, "end": v(7.26, -23.2) * mm});
            skLineSegment(sketch, "E1508", {"start": v(7.26, -23.2) * mm, "end": v(7.28, -23.15) * mm});
            skLineSegment(sketch, "E1509", {"start": v(7.28, -23.15) * mm, "end": v(-7.89, -7.98) * mm});
            skLineSegment(sketch, "E1510", {"start": v(-7.89, -7.98) * mm, "end": v(-7.92, -7.92) * mm});
            skLineSegment(sketch, "E1511", {"start": v(-7.92, -7.92) * mm, "end": v(-7.92, -7.88) * mm});
            skLineSegment(sketch, "E1512", {"start": v(-7.92, -7.88) * mm, "end": v(-7.92, -3.8) * mm});
            skLineSegment(sketch, "E1513", {"start": v(-7.92, -3.8) * mm, "end": v(-11.89, 0.17) * mm});
            skLineSegment(sketch, "E1514", {"start": v(-11.89, 0.17) * mm, "end": v(-13.93, 0.17) * mm});
            skLineSegment(sketch, "E1515", {"start": v(-13.93, 0.17) * mm, "end": v(-13.99, 0.06) * mm});
            skLineSegment(sketch, "E1516", {"start": v(-13.99, 0.06) * mm, "end": v(-14.06, -0.02) * mm});
            skLineSegment(sketch, "E1517", {"start": v(-14.06, -0.02) * mm, "end": v(-14.16, -0.09) * mm});
            skLineSegment(sketch, "E1518", {"start": v(-14.16, -0.09) * mm, "end": v(-14.26, -0.13) * mm});
            skLineSegment(sketch, "E1519", {"start": v(-14.26, -0.13) * mm, "end": v(-14.38, -0.14) * mm});
            skLineSegment(sketch, "E1520", {"start": v(-14.38, -0.14) * mm, "end": v(-14.49, -0.13) * mm});
            skLineSegment(sketch, "E1521", {"start": v(-14.49, -0.13) * mm, "end": v(-14.6, -0.09) * mm});
            skLineSegment(sketch, "E1522", {"start": v(-14.6, -0.09) * mm, "end": v(-14.7, -0.02) * mm});
            skLineSegment(sketch, "E1523", {"start": v(-14.7, -0.02) * mm, "end": v(-14.77, 0.06) * mm});
            skLineSegment(sketch, "E1524", {"start": v(-14.77, 0.06) * mm, "end": v(-14.82, 0.16) * mm});
            skLineSegment(sketch, "E1525", {"start": v(-14.82, 0.16) * mm, "end": v(-14.85, 0.27) * mm});
            skLineSegment(sketch, "E1526", {"start": v(-14.85, 0.27) * mm, "end": v(-14.86, 0.38) * mm});
            skLineSegment(sketch, "E1527", {"start": v(-14.86, 0.38) * mm, "end": v(-14.84, 0.5) * mm});
            skLineSegment(sketch, "E1528", {"start": v(-14.84, 0.5) * mm, "end": v(-14.79, 0.6) * mm});
            skLineSegment(sketch, "E1529", {"start": v(-14.79, 0.6) * mm, "end": v(-14.72, 0.69) * mm});
            skLineSegment(sketch, "E1530", {"start": v(-14.72, 0.69) * mm, "end": v(-14.63, 0.75) * mm});
            skLineSegment(sketch, "E1531", {"start": v(-14.63, 0.75) * mm, "end": v(-14.53, 0.8) * mm});
            skLineSegment(sketch, "E1532", {"start": v(-14.53, 0.8) * mm, "end": v(-14.41, 0.83) * mm});
            skLineSegment(sketch, "E1533", {"start": v(-14.41, 0.83) * mm, "end": v(-14.3, 0.82) * mm});
            skLineSegment(sketch, "E1534", {"start": v(-14.3, 0.82) * mm, "end": v(-14.2, 0.79) * mm});
            skLineSegment(sketch, "E1535", {"start": v(-14.2, 0.79) * mm, "end": v(-14.1, 0.73) * mm});
            skLineSegment(sketch, "E1536", {"start": v(-14.1, 0.73) * mm, "end": v(-14.01, 0.66) * mm});
            skLineSegment(sketch, "E1537", {"start": v(-14.01, 0.66) * mm, "end": v(-13.95, 0.56) * mm});
            skLineSegment(sketch, "E1538", {"start": v(-13.95, 0.56) * mm, "end": v(-13.93, 0.52) * mm});
            skLineSegment(sketch, "E1539", {"start": v(-13.93, 0.52) * mm, "end": v(-11.79, 0.52) * mm});
            skLineSegment(sketch, "E1540", {"start": v(-11.79, 0.52) * mm, "end": v(-11.72, 0.5) * mm});
            skLineSegment(sketch, "E1541", {"start": v(-11.72, 0.5) * mm, "end": v(-11.69, 0.47) * mm});
            skLineSegment(sketch, "E1542", {"start": v(-11.69, 0.47) * mm, "end": v(-7.6, -3.63) * mm});
            skLineSegment(sketch, "E1543", {"start": v(-7.6, -3.63) * mm, "end": v(-7.57, -3.7) * mm});
            skLineSegment(sketch, "E1544", {"start": v(-7.57, -3.7) * mm, "end": v(-7.57, -4.4) * mm});
            skLineSegment(sketch, "E1545", {"start": v(-7.57, -4.4) * mm, "end": v(-7.57, -7.8) * mm});
            skLineSegment(sketch, "E1546", {"start": v(-7.57, -7.8) * mm, "end": v(7.53, -22.9) * mm});
            skLineSegment(sketch, "E1547", {"start": v(7.53, -22.9) * mm, "end": v(7.7, -22.81) * mm});
            skLineSegment(sketch, "E1548", {"start": v(7.7, -22.81) * mm, "end": v(7.85, -22.76) * mm});
            skLineSegment(sketch, "E1549", {"start": v(7.85, -22.76) * mm, "end": v(8, -22.74) * mm});
            skLineSegment(sketch, "E1550", {"start": v(8, -22.74) * mm, "end": v(8.15, -22.74) * mm});
            skLineSegment(sketch, "E1551", {"start": v(8.15, -22.74) * mm, "end": v(8.3, -22.76) * mm});
            skLineSegment(sketch, "E1552", {"start": v(8.3, -22.76) * mm, "end": v(8.44, -22.81) * mm});
            skLineSegment(sketch, "E1553", {"start": v(8.44, -22.81) * mm, "end": v(8.57, -22.88) * mm});
            skLineSegment(sketch, "E1554", {"start": v(8.57, -22.88) * mm, "end": v(8.69, -22.97) * mm});
            skLineSegment(sketch, "E1555", {"start": v(8.69, -22.97) * mm, "end": v(8.8, -23.07) * mm});
            skLineSegment(sketch, "E1556", {"start": v(8.8, -23.07) * mm, "end": v(8.88, -23.2) * mm});
            skLineSegment(sketch, "E1557", {"start": v(8.88, -23.2) * mm, "end": v(8.95, -23.32) * mm});
            skLineSegment(sketch, "E1558", {"start": v(8.95, -23.32) * mm, "end": v(9, -23.47) * mm});
            skLineSegment(sketch, "E1559", {"start": v(9, -23.47) * mm, "end": v(9.02, -23.61) * mm});
            skLineSegment(sketch, "E1560", {"start": v(9.02, -23.61) * mm, "end": v(9.02, -23.76) * mm});
            skLineSegment(sketch, "E1561", {"start": v(6.48, -23.76) * mm, "end": v(6.45, -23.91) * mm});
            skLineSegment(sketch, "E1562", {"start": v(6.45, -23.91) * mm, "end": v(6.4, -24.05) * mm});
            skLineSegment(sketch, "E1563", {"start": v(6.4, -24.05) * mm, "end": v(6.34, -24.19) * mm});
            skLineSegment(sketch, "E1564", {"start": v(6.34, -24.19) * mm, "end": v(6.25, -24.3) * mm});
            skLineSegment(sketch, "E1565", {"start": v(6.25, -24.3) * mm, "end": v(6.15, -24.41) * mm});
            skLineSegment(sketch, "E1566", {"start": v(6.15, -24.41) * mm, "end": v(6.03, -24.5) * mm});
            skLineSegment(sketch, "E1567", {"start": v(6.03, -24.5) * mm, "end": v(5.9, -24.57) * mm});
            skLineSegment(sketch, "E1568", {"start": v(5.9, -24.57) * mm, "end": v(5.75, -24.62) * mm});
            skLineSegment(sketch, "E1569", {"start": v(5.75, -24.62) * mm, "end": v(5.6, -24.64) * mm});
            skLineSegment(sketch, "E1570", {"start": v(5.6, -24.64) * mm, "end": v(5.46, -24.64) * mm});
            skLineSegment(sketch, "E1571", {"start": v(5.46, -24.64) * mm, "end": v(5.3, -24.62) * mm});
            skLineSegment(sketch, "E1572", {"start": v(5.3, -24.62) * mm, "end": v(5.17, -24.57) * mm});
            skLineSegment(sketch, "E1573", {"start": v(5.17, -24.57) * mm, "end": v(5.03, -24.5) * mm});
            skLineSegment(sketch, "E1574", {"start": v(5.03, -24.5) * mm, "end": v(4.91, -24.41) * mm});
            skLineSegment(sketch, "E1575", {"start": v(4.91, -24.41) * mm, "end": v(4.8, -24.3) * mm});
            skLineSegment(sketch, "E1576", {"start": v(4.8, -24.3) * mm, "end": v(4.72, -24.19) * mm});
            skLineSegment(sketch, "E1577", {"start": v(4.72, -24.19) * mm, "end": v(4.65, -24.05) * mm});
            skLineSegment(sketch, "E1578", {"start": v(4.65, -24.05) * mm, "end": v(4.6, -23.91) * mm});
            skLineSegment(sketch, "E1579", {"start": v(4.6, -23.91) * mm, "end": v(4.58, -23.76) * mm});
            skLineSegment(sketch, "E1580", {"start": v(4.58, -23.76) * mm, "end": v(4.58, -23.61) * mm});
            skLineSegment(sketch, "E1581", {"start": v(4.58, -23.61) * mm, "end": v(4.6, -23.47) * mm});
            skLineSegment(sketch, "E1582", {"start": v(4.6, -23.47) * mm, "end": v(4.65, -23.32) * mm});
            skLineSegment(sketch, "E1583", {"start": v(4.65, -23.32) * mm, "end": v(4.72, -23.2) * mm});
            skLineSegment(sketch, "E1584", {"start": v(4.72, -23.2) * mm, "end": v(4.74, -23.15) * mm});
            skLineSegment(sketch, "E1585", {"start": v(4.74, -23.15) * mm, "end": v(-8.94, -9.47) * mm});
            skLineSegment(sketch, "E1586", {"start": v(-8.94, -9.47) * mm, "end": v(-8.97, -9.4) * mm});
            skLineSegment(sketch, "E1587", {"start": v(-8.97, -9.4) * mm, "end": v(-8.97, -9.37) * mm});
            skLineSegment(sketch, "E1588", {"start": v(-8.97, -9.37) * mm, "end": v(-8.97, -4.22) * mm});
            skLineSegment(sketch, "E1589", {"start": v(-8.97, -4.22) * mm, "end": v(-12.32, -0.87) * mm});
            skLineSegment(sketch, "E1590", {"start": v(-12.32, -0.87) * mm, "end": v(-13.9, -0.87) * mm});
            skLineSegment(sketch, "E1591", {"start": v(-13.9, -0.87) * mm, "end": v(-13.9, -1) * mm});
            skLineSegment(sketch, "E1592", {"start": v(-13.9, -1) * mm, "end": v(-13.93, -1.11) * mm});
            skLineSegment(sketch, "E1593", {"start": v(-13.93, -1.11) * mm, "end": v(-13.99, -1.21) * mm});
            skLineSegment(sketch, "E1594", {"start": v(-13.99, -1.21) * mm, "end": v(-14.06, -1.3) * mm});
            skLineSegment(sketch, "E1595", {"start": v(-14.06, -1.3) * mm, "end": v(-14.16, -1.36) * mm});
            skLineSegment(sketch, "E1596", {"start": v(-14.16, -1.36) * mm, "end": v(-14.26, -1.4) * mm});
            skLineSegment(sketch, "E1597", {"start": v(-14.26, -1.4) * mm, "end": v(-14.38, -1.4) * mm});
            skLineSegment(sketch, "E1598", {"start": v(-14.38, -1.4) * mm, "end": v(-14.49, -1.4) * mm});
            skLineSegment(sketch, "E1599", {"start": v(-14.49, -1.4) * mm, "end": v(-14.6, -1.36) * mm});
            skLineSegment(sketch, "E1600", {"start": v(-14.6, -1.36) * mm, "end": v(-14.7, -1.3) * mm});
            skLineSegment(sketch, "E1601", {"start": v(-14.7, -1.3) * mm, "end": v(-14.77, -1.21) * mm});
            skLineSegment(sketch, "E1602", {"start": v(-14.77, -1.21) * mm, "end": v(-14.82, -1.11) * mm});
            skLineSegment(sketch, "E1603", {"start": v(-14.82, -1.11) * mm, "end": v(-14.85, -1) * mm});
            skLineSegment(sketch, "E1604", {"start": v(-14.85, -1) * mm, "end": v(-14.86, -0.89) * mm});
            skLineSegment(sketch, "E1605", {"start": v(-14.86, -0.89) * mm, "end": v(-14.84, -0.78) * mm});
            skLineSegment(sketch, "E1606", {"start": v(-14.84, -0.78) * mm, "end": v(-14.79, -0.68) * mm});
            skLineSegment(sketch, "E1607", {"start": v(-14.79, -0.68) * mm, "end": v(-14.72, -0.58) * mm});
            skLineSegment(sketch, "E1608", {"start": v(-14.72, -0.58) * mm, "end": v(-14.63, -0.52) * mm});
            skLineSegment(sketch, "E1609", {"start": v(-14.63, -0.52) * mm, "end": v(-14.53, -0.47) * mm});
            skLineSegment(sketch, "E1610", {"start": v(-14.53, -0.47) * mm, "end": v(-14.41, -0.44) * mm});
            skLineSegment(sketch, "E1611", {"start": v(-14.41, -0.44) * mm, "end": v(-14.3, -0.45) * mm});
            skLineSegment(sketch, "E1612", {"start": v(-14.3, -0.45) * mm, "end": v(-14.2, -0.48) * mm});
            skLineSegment(sketch, "E1613", {"start": v(-14.2, -0.48) * mm, "end": v(-14.09, -0.54) * mm});
            skLineSegment(sketch, "E1614", {"start": v(-14.09, -0.54) * mm, "end": v(-14.02, -0.52) * mm});
            skLineSegment(sketch, "E1615", {"start": v(-14.02, -0.52) * mm, "end": v(-12.21, -0.52) * mm});
            skLineSegment(sketch, "E1616", {"start": v(-12.21, -0.52) * mm, "end": v(-12.15, -0.55) * mm});
            skLineSegment(sketch, "E1617", {"start": v(-12.15, -0.55) * mm, "end": v(-12.11, -0.57) * mm});
            skLineSegment(sketch, "E1618", {"start": v(-12.11, -0.57) * mm, "end": v(-8.64, -4.05) * mm});
            skLineSegment(sketch, "E1619", {"start": v(-8.64, -4.05) * mm, "end": v(-8.62, -4.11) * mm});
            skLineSegment(sketch, "E1620", {"start": v(-8.62, -4.11) * mm, "end": v(-8.62, -4.82) * mm});
            skLineSegment(sketch, "E1621", {"start": v(-8.62, -4.82) * mm, "end": v(-8.62, -9.3) * mm});
            skLineSegment(sketch, "E1622", {"start": v(-8.62, -9.3) * mm, "end": v(5, -22.9) * mm});
            skLineSegment(sketch, "E1623", {"start": v(5, -22.9) * mm, "end": v(5.1, -22.84) * mm});
            skLineSegment(sketch, "E1624", {"start": v(5.1, -22.84) * mm, "end": v(5.23, -22.78) * mm});
            skLineSegment(sketch, "E1625", {"start": v(5.23, -22.78) * mm, "end": v(5.38, -22.75) * mm});
            skLineSegment(sketch, "E1626", {"start": v(5.38, -22.75) * mm, "end": v(5.53, -22.74) * mm});
            skLineSegment(sketch, "E1627", {"start": v(5.53, -22.74) * mm, "end": v(5.68, -22.75) * mm});
            skLineSegment(sketch, "E1628", {"start": v(5.68, -22.75) * mm, "end": v(5.82, -22.78) * mm});
            skLineSegment(sketch, "E1629", {"start": v(5.82, -22.78) * mm, "end": v(5.96, -22.84) * mm});
            skLineSegment(sketch, "E1630", {"start": v(5.96, -22.84) * mm, "end": v(6.09, -22.92) * mm});
            skLineSegment(sketch, "E1631", {"start": v(6.09, -22.92) * mm, "end": v(6.2, -23.02) * mm});
            skLineSegment(sketch, "E1632", {"start": v(6.2, -23.02) * mm, "end": v(6.3, -23.13) * mm});
            skLineSegment(sketch, "E1633", {"start": v(6.3, -23.13) * mm, "end": v(6.38, -23.26) * mm});
            skLineSegment(sketch, "E1634", {"start": v(6.38, -23.26) * mm, "end": v(6.43, -23.4) * mm});
            skLineSegment(sketch, "E1635", {"start": v(6.43, -23.4) * mm, "end": v(6.47, -23.54) * mm});
            skLineSegment(sketch, "E1636", {"start": v(6.47, -23.54) * mm, "end": v(6.48, -23.7) * mm});
            skLineSegment(sketch, "E1637", {"start": v(6.48, -23.7) * mm, "end": v(6.48, -23.76) * mm});
            skLineSegment(sketch, "E1638", {"start": v(3.94, -23.76) * mm, "end": v(3.91, -23.91) * mm});
            skLineSegment(sketch, "E1639", {"start": v(3.91, -23.91) * mm, "end": v(3.87, -24.05) * mm});
            skLineSegment(sketch, "E1640", {"start": v(3.87, -24.05) * mm, "end": v(3.8, -24.19) * mm});
            skLineSegment(sketch, "E1641", {"start": v(3.8, -24.19) * mm, "end": v(3.71, -24.3) * mm});
            skLineSegment(sketch, "E1642", {"start": v(3.71, -24.3) * mm, "end": v(3.6, -24.41) * mm});
            skLineSegment(sketch, "E1643", {"start": v(3.6, -24.41) * mm, "end": v(3.49, -24.5) * mm});
            skLineSegment(sketch, "E1644", {"start": v(3.49, -24.5) * mm, "end": v(3.36, -24.57) * mm});
            skLineSegment(sketch, "E1645", {"start": v(3.36, -24.57) * mm, "end": v(3.21, -24.62) * mm});
            skLineSegment(sketch, "E1646", {"start": v(3.21, -24.62) * mm, "end": v(3.07, -24.64) * mm});
            skLineSegment(sketch, "E1647", {"start": v(3.07, -24.64) * mm, "end": v(2.92, -24.64) * mm});
            skLineSegment(sketch, "E1648", {"start": v(2.92, -24.64) * mm, "end": v(2.77, -24.62) * mm});
            skLineSegment(sketch, "E1649", {"start": v(2.77, -24.62) * mm, "end": v(2.63, -24.57) * mm});
            skLineSegment(sketch, "E1650", {"start": v(2.63, -24.57) * mm, "end": v(2.5, -24.5) * mm});
            skLineSegment(sketch, "E1651", {"start": v(2.5, -24.5) * mm, "end": v(2.37, -24.41) * mm});
            skLineSegment(sketch, "E1652", {"start": v(2.37, -24.41) * mm, "end": v(2.27, -24.3) * mm});
            skLineSegment(sketch, "E1653", {"start": v(2.27, -24.3) * mm, "end": v(2.18, -24.19) * mm});
            skLineSegment(sketch, "E1654", {"start": v(2.18, -24.19) * mm, "end": v(2.11, -24.05) * mm});
            skLineSegment(sketch, "E1655", {"start": v(2.11, -24.05) * mm, "end": v(2.07, -23.91) * mm});
            skLineSegment(sketch, "E1656", {"start": v(2.07, -23.91) * mm, "end": v(2.04, -23.76) * mm});
            skLineSegment(sketch, "E1657", {"start": v(2.04, -23.76) * mm, "end": v(2.04, -23.61) * mm});
            skLineSegment(sketch, "E1658", {"start": v(2.04, -23.61) * mm, "end": v(2.07, -23.47) * mm});
            skLineSegment(sketch, "E1659", {"start": v(2.07, -23.47) * mm, "end": v(2.11, -23.32) * mm});
            skLineSegment(sketch, "E1660", {"start": v(2.11, -23.32) * mm, "end": v(2.18, -23.2) * mm});
            skLineSegment(sketch, "E1661", {"start": v(2.18, -23.2) * mm, "end": v(2.2, -23.15) * mm});
            skLineSegment(sketch, "E1662", {"start": v(2.2, -23.15) * mm, "end": v(-10.56, -10.4) * mm});
            skLineSegment(sketch, "E1663", {"start": v(-10.56, -10.4) * mm, "end": v(-10.59, -10.33) * mm});
            skLineSegment(sketch, "E1664", {"start": v(-10.59, -10.33) * mm, "end": v(-10.6, -10.29) * mm});
            skLineSegment(sketch, "E1665", {"start": v(-10.6, -10.29) * mm, "end": v(-10.6, -4.04) * mm});
            skLineSegment(sketch, "E1666", {"start": v(-10.6, -4.04) * mm, "end": v(-12.26, -2.37) * mm});
            skLineSegment(sketch, "E1667", {"start": v(-12.26, -2.37) * mm, "end": v(-13.93, -2.37) * mm});
            skLineSegment(sketch, "E1668", {"start": v(-13.93, -2.37) * mm, "end": v(-13.99, -2.48) * mm});
            skLineSegment(sketch, "E1669", {"start": v(-13.99, -2.48) * mm, "end": v(-14.06, -2.56) * mm});
            skLineSegment(sketch, "E1670", {"start": v(-14.06, -2.56) * mm, "end": v(-14.16, -2.63) * mm});
            skLineSegment(sketch, "E1671", {"start": v(-14.16, -2.63) * mm, "end": v(-14.26, -2.67) * mm});
            skLineSegment(sketch, "E1672", {"start": v(-14.26, -2.67) * mm, "end": v(-14.38, -2.68) * mm});
            skLineSegment(sketch, "E1673", {"start": v(-14.38, -2.68) * mm, "end": v(-14.49, -2.67) * mm});
            skLineSegment(sketch, "E1674", {"start": v(-14.49, -2.67) * mm, "end": v(-14.6, -2.63) * mm});
            skLineSegment(sketch, "E1675", {"start": v(-14.6, -2.63) * mm, "end": v(-14.7, -2.56) * mm});
            skLineSegment(sketch, "E1676", {"start": v(-14.7, -2.56) * mm, "end": v(-14.77, -2.48) * mm});
            skLineSegment(sketch, "E1677", {"start": v(-14.77, -2.48) * mm, "end": v(-14.82, -2.38) * mm});
            skLineSegment(sketch, "E1678", {"start": v(-14.82, -2.38) * mm, "end": v(-14.85, -2.27) * mm});
            skLineSegment(sketch, "E1679", {"start": v(-14.85, -2.27) * mm, "end": v(-14.86, -2.16) * mm});
            skLineSegment(sketch, "E1680", {"start": v(-14.86, -2.16) * mm, "end": v(-14.84, -2.05) * mm});
            skLineSegment(sketch, "E1681", {"start": v(-14.84, -2.05) * mm, "end": v(-14.79, -1.95) * mm});
            skLineSegment(sketch, "E1682", {"start": v(-14.79, -1.95) * mm, "end": v(-14.72, -1.85) * mm});
            skLineSegment(sketch, "E1683", {"start": v(-14.72, -1.85) * mm, "end": v(-14.63, -1.79) * mm});
            skLineSegment(sketch, "E1684", {"start": v(-14.63, -1.79) * mm, "end": v(-14.53, -1.74) * mm});
            skLineSegment(sketch, "E1685", {"start": v(-14.53, -1.74) * mm, "end": v(-14.41, -1.71) * mm});
            skLineSegment(sketch, "E1686", {"start": v(-14.41, -1.71) * mm, "end": v(-14.3, -1.72) * mm});
            skLineSegment(sketch, "E1687", {"start": v(-14.3, -1.72) * mm, "end": v(-14.2, -1.75) * mm});
            skLineSegment(sketch, "E1688", {"start": v(-14.2, -1.75) * mm, "end": v(-14.1, -1.8) * mm});
            skLineSegment(sketch, "E1689", {"start": v(-14.1, -1.8) * mm, "end": v(-14.01, -1.88) * mm});
            skLineSegment(sketch, "E1690", {"start": v(-14.01, -1.88) * mm, "end": v(-13.95, -1.98) * mm});
            skLineSegment(sketch, "E1691", {"start": v(-13.95, -1.98) * mm, "end": v(-13.93, -2.02) * mm});
            skLineSegment(sketch, "E1692", {"start": v(-13.93, -2.02) * mm, "end": v(-12.15, -2.02) * mm});
            skLineSegment(sketch, "E1693", {"start": v(-12.15, -2.02) * mm, "end": v(-12.09, -2.04) * mm});
            skLineSegment(sketch, "E1694", {"start": v(-12.09, -2.04) * mm, "end": v(-12.05, -2.07) * mm});
            skLineSegment(sketch, "E1695", {"start": v(-12.05, -2.07) * mm, "end": v(-10.26, -3.87) * mm});
            skLineSegment(sketch, "E1696", {"start": v(-10.26, -3.87) * mm, "end": v(-10.24, -3.93) * mm});
            skLineSegment(sketch, "E1697", {"start": v(-10.24, -3.93) * mm, "end": v(-10.24, -4.64) * mm});
            skLineSegment(sketch, "E1698", {"start": v(-10.24, -4.64) * mm, "end": v(-10.24, -10.22) * mm});
            skLineSegment(sketch, "E1699", {"start": v(-10.24, -10.22) * mm, "end": v(2.46, -22.9) * mm});
            skLineSegment(sketch, "E1700", {"start": v(2.46, -22.9) * mm, "end": v(2.56, -22.84) * mm});
            skLineSegment(sketch, "E1701", {"start": v(2.56, -22.84) * mm, "end": v(2.7, -22.78) * mm});
            skLineSegment(sketch, "E1702", {"start": v(2.7, -22.78) * mm, "end": v(2.84, -22.75) * mm});
            skLineSegment(sketch, "E1703", {"start": v(2.84, -22.75) * mm, "end": v(2.99, -22.74) * mm});
            skLineSegment(sketch, "E1704", {"start": v(2.99, -22.74) * mm, "end": v(3.14, -22.75) * mm});
            skLineSegment(sketch, "E1705", {"start": v(3.14, -22.75) * mm, "end": v(3.28, -22.78) * mm});
            skLineSegment(sketch, "E1706", {"start": v(3.28, -22.78) * mm, "end": v(3.42, -22.84) * mm});
            skLineSegment(sketch, "E1707", {"start": v(3.42, -22.84) * mm, "end": v(3.55, -22.92) * mm});
            skLineSegment(sketch, "E1708", {"start": v(3.55, -22.92) * mm, "end": v(3.66, -23.02) * mm});
            skLineSegment(sketch, "E1709", {"start": v(3.66, -23.02) * mm, "end": v(3.76, -23.13) * mm});
            skLineSegment(sketch, "E1710", {"start": v(3.76, -23.13) * mm, "end": v(3.84, -23.26) * mm});
            skLineSegment(sketch, "E1711", {"start": v(3.84, -23.26) * mm, "end": v(3.9, -23.4) * mm});
            skLineSegment(sketch, "E1712", {"start": v(3.9, -23.4) * mm, "end": v(3.93, -23.54) * mm});
            skLineSegment(sketch, "E1713", {"start": v(3.93, -23.54) * mm, "end": v(3.94, -23.7) * mm});
            skLineSegment(sketch, "E1714", {"start": v(3.94, -23.7) * mm, "end": v(3.94, -23.76) * mm});
            skLineSegment(sketch, "E1715", {"start": v(-3.68, -23.76) * mm, "end": v(-3.7, -23.91) * mm});
            skLineSegment(sketch, "E1716", {"start": v(-3.7, -23.91) * mm, "end": v(-3.75, -24.05) * mm});
            skLineSegment(sketch, "E1717", {"start": v(-3.75, -24.05) * mm, "end": v(-3.82, -24.19) * mm});
            skLineSegment(sketch, "E1718", {"start": v(-3.82, -24.19) * mm, "end": v(-3.9, -24.3) * mm});
            skLineSegment(sketch, "E1719", {"start": v(-3.9, -24.3) * mm, "end": v(-4.01, -24.41) * mm});
            skLineSegment(sketch, "E1720", {"start": v(-4.01, -24.41) * mm, "end": v(-4.13, -24.5) * mm});
            skLineSegment(sketch, "E1721", {"start": v(-4.13, -24.5) * mm, "end": v(-4.26, -24.57) * mm});
            skLineSegment(sketch, "E1722", {"start": v(-4.26, -24.57) * mm, "end": v(-4.4, -24.62) * mm});
            skLineSegment(sketch, "E1723", {"start": v(-4.4, -24.62) * mm, "end": v(-4.55, -24.64) * mm});
            skLineSegment(sketch, "E1724", {"start": v(-4.55, -24.64) * mm, "end": v(-4.7, -24.64) * mm});
            skLineSegment(sketch, "E1725", {"start": v(-4.7, -24.64) * mm, "end": v(-4.85, -24.62) * mm});
            skLineSegment(sketch, "E1726", {"start": v(-4.85, -24.62) * mm, "end": v(-5, -24.57) * mm});
            skLineSegment(sketch, "E1727", {"start": v(-5, -24.57) * mm, "end": v(-5.13, -24.5) * mm});
            skLineSegment(sketch, "E1728", {"start": v(-5.13, -24.5) * mm, "end": v(-5.25, -24.41) * mm});
            skLineSegment(sketch, "E1729", {"start": v(-5.25, -24.41) * mm, "end": v(-5.35, -24.3) * mm});
            skLineSegment(sketch, "E1730", {"start": v(-5.35, -24.3) * mm, "end": v(-5.44, -24.19) * mm});
            skLineSegment(sketch, "E1731", {"start": v(-5.44, -24.19) * mm, "end": v(-5.5, -24.05) * mm});
            skLineSegment(sketch, "E1732", {"start": v(-5.5, -24.05) * mm, "end": v(-5.55, -23.91) * mm});
            skLineSegment(sketch, "E1733", {"start": v(-5.55, -23.91) * mm, "end": v(-5.58, -23.76) * mm});
            skLineSegment(sketch, "E1734", {"start": v(-5.58, -23.76) * mm, "end": v(-5.58, -23.61) * mm});
            skLineSegment(sketch, "E1735", {"start": v(-5.58, -23.61) * mm, "end": v(-5.55, -23.47) * mm});
            skLineSegment(sketch, "E1736", {"start": v(-5.55, -23.47) * mm, "end": v(-5.5, -23.32) * mm});
            skLineSegment(sketch, "E1737", {"start": v(-5.5, -23.32) * mm, "end": v(-5.44, -23.2) * mm});
            skLineSegment(sketch, "E1738", {"start": v(-5.44, -23.2) * mm, "end": v(-5.35, -23.07) * mm});
            skLineSegment(sketch, "E1739", {"start": v(-5.35, -23.07) * mm, "end": v(-5.25, -22.97) * mm});
            skLineSegment(sketch, "E1740", {"start": v(-5.25, -22.97) * mm, "end": v(-5.13, -22.88) * mm});
            skLineSegment(sketch, "E1741", {"start": v(-5.13, -22.88) * mm, "end": v(-5, -22.81) * mm});
            skLineSegment(sketch, "E1742", {"start": v(-5, -22.81) * mm, "end": v(-4.85, -22.76) * mm});
            skLineSegment(sketch, "E1743", {"start": v(-4.85, -22.76) * mm, "end": v(-4.7, -22.74) * mm});
            skLineSegment(sketch, "E1744", {"start": v(-4.7, -22.74) * mm, "end": v(-4.55, -22.74) * mm});
            skLineSegment(sketch, "E1745", {"start": v(-4.55, -22.74) * mm, "end": v(-4.4, -22.76) * mm});
            skLineSegment(sketch, "E1746", {"start": v(-4.4, -22.76) * mm, "end": v(-4.26, -22.81) * mm});
            skLineSegment(sketch, "E1747", {"start": v(-4.26, -22.81) * mm, "end": v(-4.13, -22.88) * mm});
            skLineSegment(sketch, "E1748", {"start": v(-4.13, -22.88) * mm, "end": v(-4.01, -22.97) * mm});
            skLineSegment(sketch, "E1749", {"start": v(-4.01, -22.97) * mm, "end": v(-3.9, -23.07) * mm});
            skLineSegment(sketch, "E1750", {"start": v(-3.9, -23.07) * mm, "end": v(-3.82, -23.2) * mm});
            skLineSegment(sketch, "E1751", {"start": v(-3.82, -23.2) * mm, "end": v(-3.75, -23.32) * mm});
            skLineSegment(sketch, "E1752", {"start": v(-3.75, -23.32) * mm, "end": v(-3.7, -23.47) * mm});
            skLineSegment(sketch, "E1753", {"start": v(-3.7, -23.47) * mm, "end": v(-3.68, -23.61) * mm});
            skLineSegment(sketch, "E1754", {"start": v(-3.68, -23.61) * mm, "end": v(-3.68, -23.76) * mm});
            skLineSegment(sketch, "E1755", {"start": v(-6.22, -23.76) * mm, "end": v(-6.25, -23.91) * mm});
            skLineSegment(sketch, "E1756", {"start": v(-6.25, -23.91) * mm, "end": v(-6.3, -24.05) * mm});
            skLineSegment(sketch, "E1757", {"start": v(-6.3, -24.05) * mm, "end": v(-6.36, -24.19) * mm});
            skLineSegment(sketch, "E1758", {"start": v(-6.36, -24.19) * mm, "end": v(-6.45, -24.3) * mm});
            skLineSegment(sketch, "E1759", {"start": v(-6.45, -24.3) * mm, "end": v(-6.55, -24.41) * mm});
            skLineSegment(sketch, "E1760", {"start": v(-6.55, -24.41) * mm, "end": v(-6.67, -24.5) * mm});
            skLineSegment(sketch, "E1761", {"start": v(-6.67, -24.5) * mm, "end": v(-6.8, -24.57) * mm});
            skLineSegment(sketch, "E1762", {"start": v(-6.8, -24.57) * mm, "end": v(-6.95, -24.62) * mm});
            skLineSegment(sketch, "E1763", {"start": v(-6.95, -24.62) * mm, "end": v(-7.1, -24.64) * mm});
            skLineSegment(sketch, "E1764", {"start": v(-7.1, -24.64) * mm, "end": v(-7.24, -24.64) * mm});
            skLineSegment(sketch, "E1765", {"start": v(-7.24, -24.64) * mm, "end": v(-7.4, -24.62) * mm});
            skLineSegment(sketch, "E1766", {"start": v(-7.4, -24.62) * mm, "end": v(-7.53, -24.57) * mm});
            skLineSegment(sketch, "E1767", {"start": v(-7.53, -24.57) * mm, "end": v(-7.67, -24.5) * mm});
            skLineSegment(sketch, "E1768", {"start": v(-7.67, -24.5) * mm, "end": v(-7.79, -24.41) * mm});
            skLineSegment(sketch, "E1769", {"start": v(-7.79, -24.41) * mm, "end": v(-7.9, -24.3) * mm});
            skLineSegment(sketch, "E1770", {"start": v(-7.9, -24.3) * mm, "end": v(-7.98, -24.19) * mm});
            skLineSegment(sketch, "E1771", {"start": v(-7.98, -24.19) * mm, "end": v(-8.05, -24.05) * mm});
            skLineSegment(sketch, "E1772", {"start": v(-8.05, -24.05) * mm, "end": v(-8.1, -23.91) * mm});
            skLineSegment(sketch, "E1773", {"start": v(-8.1, -23.91) * mm, "end": v(-8.12, -23.76) * mm});
            skLineSegment(sketch, "E1774", {"start": v(-8.12, -23.76) * mm, "end": v(-8.12, -23.61) * mm});
            skLineSegment(sketch, "E1775", {"start": v(-8.12, -23.61) * mm, "end": v(-8.1, -23.47) * mm});
            skLineSegment(sketch, "E1776", {"start": v(-8.1, -23.47) * mm, "end": v(-8.05, -23.32) * mm});
            skLineSegment(sketch, "E1777", {"start": v(-8.05, -23.32) * mm, "end": v(-7.98, -23.2) * mm});
            skLineSegment(sketch, "E1778", {"start": v(-7.98, -23.2) * mm, "end": v(-7.9, -23.07) * mm});
            skLineSegment(sketch, "E1779", {"start": v(-7.9, -23.07) * mm, "end": v(-7.79, -22.97) * mm});
            skLineSegment(sketch, "E1780", {"start": v(-7.79, -22.97) * mm, "end": v(-7.67, -22.88) * mm});
            skLineSegment(sketch, "E1781", {"start": v(-7.67, -22.88) * mm, "end": v(-7.53, -22.81) * mm});
            skLineSegment(sketch, "E1782", {"start": v(-7.53, -22.81) * mm, "end": v(-7.4, -22.76) * mm});
            skLineSegment(sketch, "E1783", {"start": v(-7.4, -22.76) * mm, "end": v(-7.24, -22.74) * mm});
            skLineSegment(sketch, "E1784", {"start": v(-7.24, -22.74) * mm, "end": v(-7.1, -22.74) * mm});
            skLineSegment(sketch, "E1785", {"start": v(-7.1, -22.74) * mm, "end": v(-6.95, -22.76) * mm});
            skLineSegment(sketch, "E1786", {"start": v(-6.95, -22.76) * mm, "end": v(-6.8, -22.81) * mm});
            skLineSegment(sketch, "E1787", {"start": v(-6.8, -22.81) * mm, "end": v(-6.67, -22.88) * mm});
            skLineSegment(sketch, "E1788", {"start": v(-6.67, -22.88) * mm, "end": v(-6.55, -22.97) * mm});
            skLineSegment(sketch, "E1789", {"start": v(-6.55, -22.97) * mm, "end": v(-6.45, -23.07) * mm});
            skLineSegment(sketch, "E1790", {"start": v(-6.45, -23.07) * mm, "end": v(-6.36, -23.2) * mm});
            skLineSegment(sketch, "E1791", {"start": v(-6.36, -23.2) * mm, "end": v(-6.3, -23.32) * mm});
            skLineSegment(sketch, "E1792", {"start": v(-6.3, -23.32) * mm, "end": v(-6.25, -23.47) * mm});
            skLineSegment(sketch, "E1793", {"start": v(-6.25, -23.47) * mm, "end": v(-6.22, -23.61) * mm});
            skLineSegment(sketch, "E1794", {"start": v(-6.22, -23.61) * mm, "end": v(-6.22, -23.76) * mm});
            skLineSegment(sketch, "E1795", {"start": v(-8.76, -23.76) * mm, "end": v(-8.79, -23.91) * mm});
            skLineSegment(sketch, "E1796", {"start": v(-8.79, -23.91) * mm, "end": v(-8.83, -24.05) * mm});
            skLineSegment(sketch, "E1797", {"start": v(-8.83, -24.05) * mm, "end": v(-8.9, -24.19) * mm});
            skLineSegment(sketch, "E1798", {"start": v(-8.9, -24.19) * mm, "end": v(-8.99, -24.3) * mm});
            skLineSegment(sketch, "E1799", {"start": v(-8.99, -24.3) * mm, "end": v(-9.1, -24.41) * mm});
            skLineSegment(sketch, "E1800", {"start": v(-9.1, -24.41) * mm, "end": v(-9.21, -24.5) * mm});
            skLineSegment(sketch, "E1801", {"start": v(-9.21, -24.5) * mm, "end": v(-9.34, -24.57) * mm});
            skLineSegment(sketch, "E1802", {"start": v(-9.34, -24.57) * mm, "end": v(-9.49, -24.62) * mm});
            skLineSegment(sketch, "E1803", {"start": v(-9.49, -24.62) * mm, "end": v(-9.63, -24.64) * mm});
            skLineSegment(sketch, "E1804", {"start": v(-9.63, -24.64) * mm, "end": v(-9.78, -24.64) * mm});
            skLineSegment(sketch, "E1805", {"start": v(-9.78, -24.64) * mm, "end": v(-9.93, -24.62) * mm});
            skLineSegment(sketch, "E1806", {"start": v(-9.93, -24.62) * mm, "end": v(-10.07, -24.57) * mm});
            skLineSegment(sketch, "E1807", {"start": v(-10.07, -24.57) * mm, "end": v(-10.2, -24.5) * mm});
            skLineSegment(sketch, "E1808", {"start": v(-10.2, -24.5) * mm, "end": v(-10.33, -24.41) * mm});
            skLineSegment(sketch, "E1809", {"start": v(-10.33, -24.41) * mm, "end": v(-10.43, -24.3) * mm});
            skLineSegment(sketch, "E1810", {"start": v(-10.43, -24.3) * mm, "end": v(-10.52, -24.19) * mm});
            skLineSegment(sketch, "E1811", {"start": v(-10.52, -24.19) * mm, "end": v(-10.59, -24.05) * mm});
            skLineSegment(sketch, "E1812", {"start": v(-10.59, -24.05) * mm, "end": v(-10.63, -23.91) * mm});
            skLineSegment(sketch, "E1813", {"start": v(-10.63, -23.91) * mm, "end": v(-10.66, -23.76) * mm});
            skLineSegment(sketch, "E1814", {"start": v(-10.66, -23.76) * mm, "end": v(-10.66, -23.61) * mm});
            skLineSegment(sketch, "E1815", {"start": v(-10.66, -23.61) * mm, "end": v(-10.63, -23.47) * mm});
            skLineSegment(sketch, "E1816", {"start": v(-10.63, -23.47) * mm, "end": v(-10.59, -23.32) * mm});
            skLineSegment(sketch, "E1817", {"start": v(-10.59, -23.32) * mm, "end": v(-10.52, -23.2) * mm});
            skLineSegment(sketch, "E1818", {"start": v(-10.52, -23.2) * mm, "end": v(-10.5, -23.15) * mm});
            skLineSegment(sketch, "E1819", {"start": v(-10.5, -23.15) * mm, "end": v(-20.86, -12.79) * mm});
            skLineSegment(sketch, "E1820", {"start": v(-20.86, -12.79) * mm, "end": v(-20.89, -12.73) * mm});
            skLineSegment(sketch, "E1821", {"start": v(-20.89, -12.73) * mm, "end": v(-20.9, -12.68) * mm});
            skLineSegment(sketch, "E1822", {"start": v(-20.9, -12.68) * mm, "end": v(-20.89, -3.76) * mm});
            skLineSegment(sketch, "E1823", {"start": v(-20.89, -3.76) * mm, "end": v(-20.86, -3.7) * mm});
            skLineSegment(sketch, "E1824", {"start": v(-20.86, -3.7) * mm, "end": v(-20.36, -3.2) * mm});
            skLineSegment(sketch, "E1825", {"start": v(-20.36, -3.2) * mm, "end": v(-17.93, -0.77) * mm});
            skLineSegment(sketch, "E1826", {"start": v(-17.93, -0.77) * mm, "end": v(-17.87, -0.75) * mm});
            skLineSegment(sketch, "E1827", {"start": v(-17.87, -0.75) * mm, "end": v(-17.16, -0.75) * mm});
            skLineSegment(sketch, "E1828", {"start": v(-17.16, -0.75) * mm, "end": v(-16.1, -0.75) * mm});
            skLineSegment(sketch, "E1829", {"start": v(-16.1, -0.75) * mm, "end": v(-16.06, -0.68) * mm});
            skLineSegment(sketch, "E1830", {"start": v(-16.06, -0.68) * mm, "end": v(-15.99, -0.58) * mm});
            skLineSegment(sketch, "E1831", {"start": v(-15.99, -0.58) * mm, "end": v(-15.9, -0.52) * mm});
            skLineSegment(sketch, "E1832", {"start": v(-15.9, -0.52) * mm, "end": v(-15.8, -0.47) * mm});
            skLineSegment(sketch, "E1833", {"start": v(-15.8, -0.47) * mm, "end": v(-15.68, -0.44) * mm});
            skLineSegment(sketch, "E1834", {"start": v(-15.68, -0.44) * mm, "end": v(-15.57, -0.45) * mm});
            skLineSegment(sketch, "E1835", {"start": v(-15.57, -0.45) * mm, "end": v(-15.46, -0.48) * mm});
            skLineSegment(sketch, "E1836", {"start": v(-15.46, -0.48) * mm, "end": v(-15.36, -0.54) * mm});
            skLineSegment(sketch, "E1837", {"start": v(-15.36, -0.54) * mm, "end": v(-15.28, -0.61) * mm});
            skLineSegment(sketch, "E1838", {"start": v(-15.28, -0.61) * mm, "end": v(-15.22, -0.7) * mm});
            skLineSegment(sketch, "E1839", {"start": v(-15.22, -0.7) * mm, "end": v(-15.18, -0.81) * mm});
            skLineSegment(sketch, "E1840", {"start": v(-15.18, -0.81) * mm, "end": v(-15.16, -0.93) * mm});
            skLineSegment(sketch, "E1841", {"start": v(-15.16, -0.93) * mm, "end": v(-15.18, -1.04) * mm});
            skLineSegment(sketch, "E1842", {"start": v(-15.18, -1.04) * mm, "end": v(-15.22, -1.15) * mm});
            skLineSegment(sketch, "E1843", {"start": v(-15.22, -1.15) * mm, "end": v(-15.28, -1.24) * mm});
            skLineSegment(sketch, "E1844", {"start": v(-15.28, -1.24) * mm, "end": v(-15.36, -1.32) * mm});
            skLineSegment(sketch, "E1845", {"start": v(-15.36, -1.32) * mm, "end": v(-15.46, -1.37) * mm});
            skLineSegment(sketch, "E1846", {"start": v(-15.46, -1.37) * mm, "end": v(-15.57, -1.4) * mm});
            skLineSegment(sketch, "E1847", {"start": v(-15.57, -1.4) * mm, "end": v(-15.68, -1.4) * mm});
            skLineSegment(sketch, "E1848", {"start": v(-15.68, -1.4) * mm, "end": v(-15.8, -1.39) * mm});
            skLineSegment(sketch, "E1849", {"start": v(-15.8, -1.39) * mm, "end": v(-15.9, -1.34) * mm});
            skLineSegment(sketch, "E1850", {"start": v(-15.9, -1.34) * mm, "end": v(-15.99, -1.27) * mm});
            skLineSegment(sketch, "E1851", {"start": v(-15.99, -1.27) * mm, "end": v(-16.06, -1.18) * mm});
            skLineSegment(sketch, "E1852", {"start": v(-16.06, -1.18) * mm, "end": v(-16.1, -1.1) * mm});
            skLineSegment(sketch, "E1853", {"start": v(-16.1, -1.1) * mm, "end": v(-17.77, -1.1) * mm});
            skLineSegment(sketch, "E1854", {"start": v(-17.77, -1.1) * mm, "end": v(-20.54, -3.88) * mm});
            skLineSegment(sketch, "E1855", {"start": v(-20.54, -3.88) * mm, "end": v(-20.54, -9.63) * mm});
            skLineSegment(sketch, "E1856", {"start": v(-20.54, -9.63) * mm, "end": v(-20.54, -12.61) * mm});
            skLineSegment(sketch, "E1857", {"start": v(-20.54, -12.61) * mm, "end": v(-10.24, -22.9) * mm});
            skLineSegment(sketch, "E1858", {"start": v(-10.24, -22.9) * mm, "end": v(-10.14, -22.84) * mm});
            skLineSegment(sketch, "E1859", {"start": v(-10.14, -22.84) * mm, "end": v(-10, -22.78) * mm});
            skLineSegment(sketch, "E1860", {"start": v(-10, -22.78) * mm, "end": v(-9.86, -22.75) * mm});
            skLineSegment(sketch, "E1861", {"start": v(-9.86, -22.75) * mm, "end": v(-9.71, -22.74) * mm});
            skLineSegment(sketch, "E1862", {"start": v(-9.71, -22.74) * mm, "end": v(-9.56, -22.75) * mm});
            skLineSegment(sketch, "E1863", {"start": v(-9.56, -22.75) * mm, "end": v(-9.42, -22.78) * mm});
            skLineSegment(sketch, "E1864", {"start": v(-9.42, -22.78) * mm, "end": v(-9.28, -22.84) * mm});
            skLineSegment(sketch, "E1865", {"start": v(-9.28, -22.84) * mm, "end": v(-9.15, -22.92) * mm});
            skLineSegment(sketch, "E1866", {"start": v(-9.15, -22.92) * mm, "end": v(-9.04, -23.02) * mm});
            skLineSegment(sketch, "E1867", {"start": v(-9.04, -23.02) * mm, "end": v(-8.94, -23.13) * mm});
            skLineSegment(sketch, "E1868", {"start": v(-8.94, -23.13) * mm, "end": v(-8.86, -23.26) * mm});
            skLineSegment(sketch, "E1869", {"start": v(-8.86, -23.26) * mm, "end": v(-8.8, -23.4) * mm});
            skLineSegment(sketch, "E1870", {"start": v(-8.8, -23.4) * mm, "end": v(-8.77, -23.54) * mm});
            skLineSegment(sketch, "E1871", {"start": v(-8.77, -23.54) * mm, "end": v(-8.76, -23.7) * mm});
            skLineSegment(sketch, "E1872", {"start": v(-8.76, -23.7) * mm, "end": v(-8.76, -23.76) * mm});
            skLineSegment(sketch, "E1873", {"start": v(-11.3, -23.76) * mm, "end": v(-11.33, -23.91) * mm});
            skLineSegment(sketch, "E1874", {"start": v(-11.33, -23.91) * mm, "end": v(-11.37, -24.05) * mm});
            skLineSegment(sketch, "E1875", {"start": v(-11.37, -24.05) * mm, "end": v(-11.44, -24.19) * mm});
            skLineSegment(sketch, "E1876", {"start": v(-11.44, -24.19) * mm, "end": v(-11.53, -24.3) * mm});
            skLineSegment(sketch, "E1877", {"start": v(-11.53, -24.3) * mm, "end": v(-11.63, -24.41) * mm});
            skLineSegment(sketch, "E1878", {"start": v(-11.63, -24.41) * mm, "end": v(-11.75, -24.5) * mm});
            skLineSegment(sketch, "E1879", {"start": v(-11.75, -24.5) * mm, "end": v(-11.88, -24.57) * mm});
            skLineSegment(sketch, "E1880", {"start": v(-11.88, -24.57) * mm, "end": v(-12.03, -24.62) * mm});
            skLineSegment(sketch, "E1881", {"start": v(-12.03, -24.62) * mm, "end": v(-12.17, -24.64) * mm});
            skLineSegment(sketch, "E1882", {"start": v(-12.17, -24.64) * mm, "end": v(-12.32, -24.64) * mm});
            skLineSegment(sketch, "E1883", {"start": v(-12.32, -24.64) * mm, "end": v(-12.47, -24.62) * mm});
            skLineSegment(sketch, "E1884", {"start": v(-12.47, -24.62) * mm, "end": v(-12.61, -24.57) * mm});
            skLineSegment(sketch, "E1885", {"start": v(-12.61, -24.57) * mm, "end": v(-12.75, -24.5) * mm});
            skLineSegment(sketch, "E1886", {"start": v(-12.75, -24.5) * mm, "end": v(-12.87, -24.41) * mm});
            skLineSegment(sketch, "E1887", {"start": v(-12.87, -24.41) * mm, "end": v(-12.97, -24.3) * mm});
            skLineSegment(sketch, "E1888", {"start": v(-12.97, -24.3) * mm, "end": v(-13.06, -24.19) * mm});
            skLineSegment(sketch, "E1889", {"start": v(-13.06, -24.19) * mm, "end": v(-13.13, -24.05) * mm});
            skLineSegment(sketch, "E1890", {"start": v(-13.13, -24.05) * mm, "end": v(-13.17, -23.91) * mm});
            skLineSegment(sketch, "E1891", {"start": v(-13.17, -23.91) * mm, "end": v(-13.2, -23.76) * mm});
            skLineSegment(sketch, "E1892", {"start": v(-13.2, -23.76) * mm, "end": v(-13.2, -23.61) * mm});
            skLineSegment(sketch, "E1893", {"start": v(-13.2, -23.61) * mm, "end": v(-13.17, -23.47) * mm});
            skLineSegment(sketch, "E1894", {"start": v(-13.17, -23.47) * mm, "end": v(-13.13, -23.32) * mm});
            skLineSegment(sketch, "E1895", {"start": v(-13.13, -23.32) * mm, "end": v(-13.06, -23.2) * mm});
            skLineSegment(sketch, "E1896", {"start": v(-13.06, -23.2) * mm, "end": v(-13.04, -23.15) * mm});
            skLineSegment(sketch, "E1897", {"start": v(-13.04, -23.15) * mm, "end": v(-22.3, -13.88) * mm});
            skLineSegment(sketch, "E1898", {"start": v(-22.3, -13.88) * mm, "end": v(-22.34, -13.82) * mm});
            skLineSegment(sketch, "E1899", {"start": v(-22.34, -13.82) * mm, "end": v(-22.34, -13.78) * mm});
            skLineSegment(sketch, "E1900", {"start": v(-22.34, -13.78) * mm, "end": v(-22.34, -1.66) * mm});
            skLineSegment(sketch, "E1901", {"start": v(-22.34, -1.66) * mm, "end": v(-22.3, -1.6) * mm});
            skLineSegment(sketch, "E1902", {"start": v(-22.3, -1.6) * mm, "end": v(-21.81, -1.1) * mm});
            skLineSegment(sketch, "E1903", {"start": v(-21.81, -1.1) * mm, "end": v(-20.21, 0.5) * mm});
            skLineSegment(sketch, "E1904", {"start": v(-20.21, 0.5) * mm, "end": v(-20.14, 0.52) * mm});
            skLineSegment(sketch, "E1905", {"start": v(-20.14, 0.52) * mm, "end": v(-19.44, 0.52) * mm});
            skLineSegment(sketch, "E1906", {"start": v(-19.44, 0.52) * mm, "end": v(-16.1, 0.52) * mm});
            skLineSegment(sketch, "E1907", {"start": v(-16.1, 0.52) * mm, "end": v(-16.04, 0.63) * mm});
            skLineSegment(sketch, "E1908", {"start": v(-16.04, 0.63) * mm, "end": v(-15.96, 0.71) * mm});
            skLineSegment(sketch, "E1909", {"start": v(-15.96, 0.71) * mm, "end": v(-15.86, 0.77) * mm});
            skLineSegment(sketch, "E1910", {"start": v(-15.86, 0.77) * mm, "end": v(-15.76, 0.81) * mm});
            skLineSegment(sketch, "E1911", {"start": v(-15.76, 0.81) * mm, "end": v(-15.65, 0.83) * mm});
            skLineSegment(sketch, "E1912", {"start": v(-15.65, 0.83) * mm, "end": v(-15.53, 0.81) * mm});
            skLineSegment(sketch, "E1913", {"start": v(-15.53, 0.81) * mm, "end": v(-15.43, 0.77) * mm});
            skLineSegment(sketch, "E1914", {"start": v(-15.43, 0.77) * mm, "end": v(-15.33, 0.71) * mm});
            skLineSegment(sketch, "E1915", {"start": v(-15.33, 0.71) * mm, "end": v(-15.26, 0.63) * mm});
            skLineSegment(sketch, "E1916", {"start": v(-15.26, 0.63) * mm, "end": v(-15.2, 0.53) * mm});
            skLineSegment(sketch, "E1917", {"start": v(-15.2, 0.53) * mm, "end": v(-15.17, 0.42) * mm});
            skLineSegment(sketch, "E1918", {"start": v(-15.17, 0.42) * mm, "end": v(-15.17, 0.3) * mm});
            skLineSegment(sketch, "E1919", {"start": v(-15.17, 0.3) * mm, "end": v(-15.19, 0.2) * mm});
            skLineSegment(sketch, "E1920", {"start": v(-15.19, 0.2) * mm, "end": v(-15.23, 0.1) * mm});
            skLineSegment(sketch, "E1921", {"start": v(-15.23, 0.1) * mm, "end": v(-15.3, 0) * mm});
            skLineSegment(sketch, "E1922", {"start": v(-15.3, 0) * mm, "end": v(-15.4, -0.07) * mm});
            skLineSegment(sketch, "E1923", {"start": v(-15.4, -0.07) * mm, "end": v(-15.5, -0.12) * mm});
            skLineSegment(sketch, "E1924", {"start": v(-15.5, -0.12) * mm, "end": v(-15.6, -0.14) * mm});
            skLineSegment(sketch, "E1925", {"start": v(-15.6, -0.14) * mm, "end": v(-15.72, -0.13) * mm});
            skLineSegment(sketch, "E1926", {"start": v(-15.72, -0.13) * mm, "end": v(-15.83, -0.1) * mm});
            skLineSegment(sketch, "E1927", {"start": v(-15.83, -0.1) * mm, "end": v(-15.93, -0.05) * mm});
            skLineSegment(sketch, "E1928", {"start": v(-15.93, -0.05) * mm, "end": v(-16.01, 0.03) * mm});
            skLineSegment(sketch, "E1929", {"start": v(-16.01, 0.03) * mm, "end": v(-16.08, 0.12) * mm});
            skLineSegment(sketch, "E1930", {"start": v(-16.08, 0.12) * mm, "end": v(-16.1, 0.17) * mm});
            skLineSegment(sketch, "E1931", {"start": v(-16.1, 0.17) * mm, "end": v(-20.05, 0.17) * mm});
            skLineSegment(sketch, "E1932", {"start": v(-20.05, 0.17) * mm, "end": v(-21.99, -1.78) * mm});
            skLineSegment(sketch, "E1933", {"start": v(-21.99, -1.78) * mm, "end": v(-21.99, -5.5) * mm});
            skLineSegment(sketch, "E1934", {"start": v(-21.99, -5.5) * mm, "end": v(-21.99, -13.7) * mm});
            skLineSegment(sketch, "E1935", {"start": v(-21.99, -13.7) * mm, "end": v(-12.78, -22.9) * mm});
            skLineSegment(sketch, "E1936", {"start": v(-12.78, -22.9) * mm, "end": v(-12.68, -22.84) * mm});
            skLineSegment(sketch, "E1937", {"start": v(-12.68, -22.84) * mm, "end": v(-12.55, -22.78) * mm});
            skLineSegment(sketch, "E1938", {"start": v(-12.55, -22.78) * mm, "end": v(-12.4, -22.75) * mm});
            skLineSegment(sketch, "E1939", {"start": v(-12.4, -22.75) * mm, "end": v(-12.25, -22.74) * mm});
            skLineSegment(sketch, "E1940", {"start": v(-12.25, -22.74) * mm, "end": v(-12.1, -22.75) * mm});
            skLineSegment(sketch, "E1941", {"start": v(-12.1, -22.75) * mm, "end": v(-11.96, -22.78) * mm});
            skLineSegment(sketch, "E1942", {"start": v(-11.96, -22.78) * mm, "end": v(-11.82, -22.84) * mm});
            skLineSegment(sketch, "E1943", {"start": v(-11.82, -22.84) * mm, "end": v(-11.7, -22.92) * mm});
            skLineSegment(sketch, "E1944", {"start": v(-11.7, -22.92) * mm, "end": v(-11.58, -23.02) * mm});
            skLineSegment(sketch, "E1945", {"start": v(-11.58, -23.02) * mm, "end": v(-11.48, -23.13) * mm});
            skLineSegment(sketch, "E1946", {"start": v(-11.48, -23.13) * mm, "end": v(-11.4, -23.26) * mm});
            skLineSegment(sketch, "E1947", {"start": v(-11.4, -23.26) * mm, "end": v(-11.35, -23.4) * mm});
            skLineSegment(sketch, "E1948", {"start": v(-11.35, -23.4) * mm, "end": v(-11.31, -23.54) * mm});
            skLineSegment(sketch, "E1949", {"start": v(-11.31, -23.54) * mm, "end": v(-11.3, -23.7) * mm});
            skLineSegment(sketch, "E1950", {"start": v(-11.3, -23.7) * mm, "end": v(-11.3, -23.76) * mm});
            skLineSegment(sketch, "E1951", {"start": v(-15.17, -2.24) * mm, "end": v(-15.19, -2.35) * mm});
            skLineSegment(sketch, "E1952", {"start": v(-15.19, -2.35) * mm, "end": v(-15.23, -2.45) * mm});
            skLineSegment(sketch, "E1953", {"start": v(-15.23, -2.45) * mm, "end": v(-15.3, -2.54) * mm});
            skLineSegment(sketch, "E1954", {"start": v(-15.3, -2.54) * mm, "end": v(-15.4, -2.6) * mm});
            skLineSegment(sketch, "E1955", {"start": v(-15.4, -2.6) * mm, "end": v(-15.5, -2.66) * mm});
            skLineSegment(sketch, "E1956", {"start": v(-15.5, -2.66) * mm, "end": v(-15.6, -2.68) * mm});
            skLineSegment(sketch, "E1957", {"start": v(-15.6, -2.68) * mm, "end": v(-15.72, -2.67) * mm});
            skLineSegment(sketch, "E1958", {"start": v(-15.72, -2.67) * mm, "end": v(-15.83, -2.64) * mm});
            skLineSegment(sketch, "E1959", {"start": v(-15.83, -2.64) * mm, "end": v(-15.93, -2.59) * mm});
            skLineSegment(sketch, "E1960", {"start": v(-15.93, -2.59) * mm, "end": v(-16.01, -2.5) * mm});
            skLineSegment(sketch, "E1961", {"start": v(-16.01, -2.5) * mm, "end": v(-16.08, -2.42) * mm});
            skLineSegment(sketch, "E1962", {"start": v(-16.08, -2.42) * mm, "end": v(-16.12, -2.3) * mm});
            skLineSegment(sketch, "E1963", {"start": v(-16.12, -2.3) * mm, "end": v(-16.13, -2.2) * mm});
            skLineSegment(sketch, "E1964", {"start": v(-16.13, -2.2) * mm, "end": v(-16.12, -2.08) * mm});
            skLineSegment(sketch, "E1965", {"start": v(-16.12, -2.08) * mm, "end": v(-16.08, -1.98) * mm});
            skLineSegment(sketch, "E1966", {"start": v(-16.08, -1.98) * mm, "end": v(-16.01, -1.88) * mm});
            skLineSegment(sketch, "E1967", {"start": v(-16.01, -1.88) * mm, "end": v(-15.93, -1.8) * mm});
            skLineSegment(sketch, "E1968", {"start": v(-15.93, -1.8) * mm, "end": v(-15.83, -1.75) * mm});
            skLineSegment(sketch, "E1969", {"start": v(-15.83, -1.75) * mm, "end": v(-15.72, -1.72) * mm});
            skLineSegment(sketch, "E1970", {"start": v(-15.72, -1.72) * mm, "end": v(-15.6, -1.71) * mm});
            skLineSegment(sketch, "E1971", {"start": v(-15.6, -1.71) * mm, "end": v(-15.5, -1.74) * mm});
            skLineSegment(sketch, "E1972", {"start": v(-15.5, -1.74) * mm, "end": v(-15.4, -1.79) * mm});
            skLineSegment(sketch, "E1973", {"start": v(-15.4, -1.79) * mm, "end": v(-15.3, -1.85) * mm});
            skLineSegment(sketch, "E1974", {"start": v(-15.3, -1.85) * mm, "end": v(-15.23, -1.95) * mm});
            skLineSegment(sketch, "E1975", {"start": v(-15.23, -1.95) * mm, "end": v(-15.19, -2.05) * mm});
            skLineSegment(sketch, "E1976", {"start": v(-15.19, -2.05) * mm, "end": v(-15.17, -2.16) * mm});
            skLineSegment(sketch, "E1977", {"start": v(-15.17, -2.16) * mm, "end": v(-15.17, -2.24) * mm});
            skLineSegment(sketch, "E1978", {"start": v(35.8, 23.35) * mm, "end": v(37.56, 23.35) * mm});
            skLineSegment(sketch, "E1979", {"start": v(37.56, 23.35) * mm, "end": v(37.56, 21.45) * mm});
            skLineSegment(sketch, "E1980", {"start": v(37.56, 21.45) * mm, "end": v(35.66, 21.45) * mm});
            skLineSegment(sketch, "E1981", {"start": v(35.66, 21.45) * mm, "end": v(35.66, 23.35) * mm});
            skLineSegment(sketch, "E1982", {"start": v(35.66, 23.35) * mm, "end": v(35.8, 23.35) * mm});
            skLineSegment(sketch, "E1983", {"start": v(37.56, 19.79) * mm, "end": v(37.54, 19.64) * mm});
            skLineSegment(sketch, "E1984", {"start": v(37.54, 19.64) * mm, "end": v(37.5, 19.5) * mm});
            skLineSegment(sketch, "E1985", {"start": v(37.5, 19.5) * mm, "end": v(37.42, 19.36) * mm});
            skLineSegment(sketch, "E1986", {"start": v(37.42, 19.36) * mm, "end": v(37.33, 19.24) * mm});
            skLineSegment(sketch, "E1987", {"start": v(37.33, 19.24) * mm, "end": v(37.23, 19.14) * mm});
            skLineSegment(sketch, "E1988", {"start": v(37.23, 19.14) * mm, "end": v(37.1, 19.05) * mm});
            skLineSegment(sketch, "E1989", {"start": v(37.1, 19.05) * mm, "end": v(36.97, 18.98) * mm});
            skLineSegment(sketch, "E1990", {"start": v(36.97, 18.98) * mm, "end": v(36.83, 18.94) * mm});
            skLineSegment(sketch, "E1991", {"start": v(36.83, 18.94) * mm, "end": v(36.69, 18.91) * mm});
            skLineSegment(sketch, "E1992", {"start": v(36.69, 18.91) * mm, "end": v(36.54, 18.91) * mm});
            skLineSegment(sketch, "E1993", {"start": v(36.54, 18.91) * mm, "end": v(36.39, 18.94) * mm});
            skLineSegment(sketch, "E1994", {"start": v(36.39, 18.94) * mm, "end": v(36.25, 18.98) * mm});
            skLineSegment(sketch, "E1995", {"start": v(36.25, 18.98) * mm, "end": v(36.11, 19.05) * mm});
            skLineSegment(sketch, "E1996", {"start": v(36.11, 19.05) * mm, "end": v(36, 19.14) * mm});
            skLineSegment(sketch, "E1997", {"start": v(36, 19.14) * mm, "end": v(35.89, 19.24) * mm});
            skLineSegment(sketch, "E1998", {"start": v(35.89, 19.24) * mm, "end": v(35.8, 19.36) * mm});
            skLineSegment(sketch, "E1999", {"start": v(35.8, 19.36) * mm, "end": v(35.73, 19.5) * mm});
            skLineSegment(sketch, "E2000", {"start": v(35.73, 19.5) * mm, "end": v(35.68, 19.64) * mm});
            skLineSegment(sketch, "E2001", {"start": v(35.68, 19.64) * mm, "end": v(35.66, 19.79) * mm});
            skLineSegment(sketch, "E2002", {"start": v(35.66, 19.79) * mm, "end": v(35.66, 19.93) * mm});
            skLineSegment(sketch, "E2003", {"start": v(35.66, 19.93) * mm, "end": v(35.68, 20.08) * mm});
            skLineSegment(sketch, "E2004", {"start": v(35.68, 20.08) * mm, "end": v(35.73, 20.22) * mm});
            skLineSegment(sketch, "E2005", {"start": v(35.73, 20.22) * mm, "end": v(35.8, 20.36) * mm});
            skLineSegment(sketch, "E2006", {"start": v(35.8, 20.36) * mm, "end": v(35.89, 20.48) * mm});
            skLineSegment(sketch, "E2007", {"start": v(35.89, 20.48) * mm, "end": v(36, 20.58) * mm});
            skLineSegment(sketch, "E2008", {"start": v(36, 20.58) * mm, "end": v(36.11, 20.67) * mm});
            skLineSegment(sketch, "E2009", {"start": v(36.11, 20.67) * mm, "end": v(36.25, 20.74) * mm});
            skLineSegment(sketch, "E2010", {"start": v(36.25, 20.74) * mm, "end": v(36.39, 20.78) * mm});
            skLineSegment(sketch, "E2011", {"start": v(36.39, 20.78) * mm, "end": v(36.54, 20.8) * mm});
            skLineSegment(sketch, "E2012", {"start": v(36.54, 20.8) * mm, "end": v(36.69, 20.8) * mm});
            skLineSegment(sketch, "E2013", {"start": v(36.69, 20.8) * mm, "end": v(36.83, 20.78) * mm});
            skLineSegment(sketch, "E2014", {"start": v(36.83, 20.78) * mm, "end": v(36.97, 20.74) * mm});
            skLineSegment(sketch, "E2015", {"start": v(36.97, 20.74) * mm, "end": v(37.1, 20.67) * mm});
            skLineSegment(sketch, "E2016", {"start": v(37.1, 20.67) * mm, "end": v(37.23, 20.58) * mm});
            skLineSegment(sketch, "E2017", {"start": v(37.23, 20.58) * mm, "end": v(37.33, 20.48) * mm});
            skLineSegment(sketch, "E2018", {"start": v(37.33, 20.48) * mm, "end": v(37.42, 20.36) * mm});
            skLineSegment(sketch, "E2019", {"start": v(37.42, 20.36) * mm, "end": v(37.5, 20.22) * mm});
            skLineSegment(sketch, "E2020", {"start": v(37.5, 20.22) * mm, "end": v(37.54, 20.08) * mm});
            skLineSegment(sketch, "E2021", {"start": v(37.54, 20.08) * mm, "end": v(37.56, 19.93) * mm});
            skLineSegment(sketch, "E2022", {"start": v(37.56, 19.93) * mm, "end": v(37.56, 19.79) * mm});
            skLineSegment(sketch, "E2023", {"start": v(37.56, 17.25) * mm, "end": v(37.54, 17.1) * mm});
            skLineSegment(sketch, "E2024", {"start": v(37.54, 17.1) * mm, "end": v(37.5, 16.96) * mm});
            skLineSegment(sketch, "E2025", {"start": v(37.5, 16.96) * mm, "end": v(37.42, 16.82) * mm});
            skLineSegment(sketch, "E2026", {"start": v(37.42, 16.82) * mm, "end": v(37.33, 16.7) * mm});
            skLineSegment(sketch, "E2027", {"start": v(37.33, 16.7) * mm, "end": v(37.23, 16.6) * mm});
            skLineSegment(sketch, "E2028", {"start": v(37.23, 16.6) * mm, "end": v(37.1, 16.5) * mm});
            skLineSegment(sketch, "E2029", {"start": v(37.1, 16.5) * mm, "end": v(36.97, 16.44) * mm});
            skLineSegment(sketch, "E2030", {"start": v(36.97, 16.44) * mm, "end": v(36.83, 16.4) * mm});
            skLineSegment(sketch, "E2031", {"start": v(36.83, 16.4) * mm, "end": v(36.69, 16.37) * mm});
            skLineSegment(sketch, "E2032", {"start": v(36.69, 16.37) * mm, "end": v(36.54, 16.37) * mm});
            skLineSegment(sketch, "E2033", {"start": v(36.54, 16.37) * mm, "end": v(36.39, 16.4) * mm});
            skLineSegment(sketch, "E2034", {"start": v(36.39, 16.4) * mm, "end": v(36.25, 16.44) * mm});
            skLineSegment(sketch, "E2035", {"start": v(36.25, 16.44) * mm, "end": v(36.11, 16.5) * mm});
            skLineSegment(sketch, "E2036", {"start": v(36.11, 16.5) * mm, "end": v(36, 16.6) * mm});
            skLineSegment(sketch, "E2037", {"start": v(36, 16.6) * mm, "end": v(35.89, 16.7) * mm});
            skLineSegment(sketch, "E2038", {"start": v(35.89, 16.7) * mm, "end": v(35.8, 16.82) * mm});
            skLineSegment(sketch, "E2039", {"start": v(35.8, 16.82) * mm, "end": v(35.73, 16.96) * mm});
            skLineSegment(sketch, "E2040", {"start": v(35.73, 16.96) * mm, "end": v(35.68, 17.1) * mm});
            skLineSegment(sketch, "E2041", {"start": v(35.68, 17.1) * mm, "end": v(35.66, 17.25) * mm});
            skLineSegment(sketch, "E2042", {"start": v(35.66, 17.25) * mm, "end": v(35.66, 17.4) * mm});
            skLineSegment(sketch, "E2043", {"start": v(35.66, 17.4) * mm, "end": v(35.68, 17.54) * mm});
            skLineSegment(sketch, "E2044", {"start": v(35.68, 17.54) * mm, "end": v(35.73, 17.68) * mm});
            skLineSegment(sketch, "E2045", {"start": v(35.73, 17.68) * mm, "end": v(35.8, 17.82) * mm});
            skLineSegment(sketch, "E2046", {"start": v(35.8, 17.82) * mm, "end": v(35.89, 17.94) * mm});
            skLineSegment(sketch, "E2047", {"start": v(35.89, 17.94) * mm, "end": v(36, 18.04) * mm});
            skLineSegment(sketch, "E2048", {"start": v(36, 18.04) * mm, "end": v(36.11, 18.13) * mm});
            skLineSegment(sketch, "E2049", {"start": v(36.11, 18.13) * mm, "end": v(36.25, 18.2) * mm});
            skLineSegment(sketch, "E2050", {"start": v(36.25, 18.2) * mm, "end": v(36.39, 18.24) * mm});
            skLineSegment(sketch, "E2051", {"start": v(36.39, 18.24) * mm, "end": v(36.54, 18.27) * mm});
            skLineSegment(sketch, "E2052", {"start": v(36.54, 18.27) * mm, "end": v(36.69, 18.27) * mm});
            skLineSegment(sketch, "E2053", {"start": v(36.69, 18.27) * mm, "end": v(36.83, 18.24) * mm});
            skLineSegment(sketch, "E2054", {"start": v(36.83, 18.24) * mm, "end": v(36.97, 18.2) * mm});
            skLineSegment(sketch, "E2055", {"start": v(36.97, 18.2) * mm, "end": v(37.1, 18.13) * mm});
            skLineSegment(sketch, "E2056", {"start": v(37.1, 18.13) * mm, "end": v(37.23, 18.04) * mm});
            skLineSegment(sketch, "E2057", {"start": v(37.23, 18.04) * mm, "end": v(37.33, 17.94) * mm});
            skLineSegment(sketch, "E2058", {"start": v(37.33, 17.94) * mm, "end": v(37.42, 17.82) * mm});
            skLineSegment(sketch, "E2059", {"start": v(37.42, 17.82) * mm, "end": v(37.5, 17.68) * mm});
            skLineSegment(sketch, "E2060", {"start": v(37.5, 17.68) * mm, "end": v(37.54, 17.54) * mm});
            skLineSegment(sketch, "E2061", {"start": v(37.54, 17.54) * mm, "end": v(37.56, 17.4) * mm});
            skLineSegment(sketch, "E2062", {"start": v(37.56, 17.4) * mm, "end": v(37.56, 17.25) * mm});
            skLineSegment(sketch, "E2063", {"start": v(37.56, 14.7) * mm, "end": v(37.54, 14.56) * mm});
            skLineSegment(sketch, "E2064", {"start": v(37.54, 14.56) * mm, "end": v(37.5, 14.42) * mm});
            skLineSegment(sketch, "E2065", {"start": v(37.5, 14.42) * mm, "end": v(37.42, 14.28) * mm});
            skLineSegment(sketch, "E2066", {"start": v(37.42, 14.28) * mm, "end": v(37.33, 14.16) * mm});
            skLineSegment(sketch, "E2067", {"start": v(37.33, 14.16) * mm, "end": v(37.23, 14.06) * mm});
            skLineSegment(sketch, "E2068", {"start": v(37.23, 14.06) * mm, "end": v(37.1, 13.97) * mm});
            skLineSegment(sketch, "E2069", {"start": v(37.1, 13.97) * mm, "end": v(36.97, 13.9) * mm});
            skLineSegment(sketch, "E2070", {"start": v(36.97, 13.9) * mm, "end": v(36.83, 13.86) * mm});
            skLineSegment(sketch, "E2071", {"start": v(36.83, 13.86) * mm, "end": v(36.69, 13.83) * mm});
            skLineSegment(sketch, "E2072", {"start": v(36.69, 13.83) * mm, "end": v(36.54, 13.83) * mm});
            skLineSegment(sketch, "E2073", {"start": v(36.54, 13.83) * mm, "end": v(36.39, 13.86) * mm});
            skLineSegment(sketch, "E2074", {"start": v(36.39, 13.86) * mm, "end": v(36.25, 13.9) * mm});
            skLineSegment(sketch, "E2075", {"start": v(36.25, 13.9) * mm, "end": v(36.11, 13.97) * mm});
            skLineSegment(sketch, "E2076", {"start": v(36.11, 13.97) * mm, "end": v(36, 14.06) * mm});
            skLineSegment(sketch, "E2077", {"start": v(36, 14.06) * mm, "end": v(35.89, 14.16) * mm});
            skLineSegment(sketch, "E2078", {"start": v(35.89, 14.16) * mm, "end": v(35.8, 14.28) * mm});
            skLineSegment(sketch, "E2079", {"start": v(35.8, 14.28) * mm, "end": v(35.73, 14.42) * mm});
            skLineSegment(sketch, "E2080", {"start": v(35.73, 14.42) * mm, "end": v(35.68, 14.56) * mm});
            skLineSegment(sketch, "E2081", {"start": v(35.68, 14.56) * mm, "end": v(35.66, 14.7) * mm});
            skLineSegment(sketch, "E2082", {"start": v(35.66, 14.7) * mm, "end": v(35.66, 14.85) * mm});
            skLineSegment(sketch, "E2083", {"start": v(35.66, 14.85) * mm, "end": v(35.68, 15) * mm});
            skLineSegment(sketch, "E2084", {"start": v(35.68, 15) * mm, "end": v(35.73, 15.14) * mm});
            skLineSegment(sketch, "E2085", {"start": v(35.73, 15.14) * mm, "end": v(35.8, 15.28) * mm});
            skLineSegment(sketch, "E2086", {"start": v(35.8, 15.28) * mm, "end": v(35.89, 15.4) * mm});
            skLineSegment(sketch, "E2087", {"start": v(35.89, 15.4) * mm, "end": v(36, 15.5) * mm});
            skLineSegment(sketch, "E2088", {"start": v(36, 15.5) * mm, "end": v(36.11, 15.6) * mm});
            skLineSegment(sketch, "E2089", {"start": v(36.11, 15.6) * mm, "end": v(36.25, 15.66) * mm});
            skLineSegment(sketch, "E2090", {"start": v(36.25, 15.66) * mm, "end": v(36.39, 15.7) * mm});
            skLineSegment(sketch, "E2091", {"start": v(36.39, 15.7) * mm, "end": v(36.54, 15.73) * mm});
            skLineSegment(sketch, "E2092", {"start": v(36.54, 15.73) * mm, "end": v(36.69, 15.73) * mm});
            skLineSegment(sketch, "E2093", {"start": v(36.69, 15.73) * mm, "end": v(36.83, 15.7) * mm});
            skLineSegment(sketch, "E2094", {"start": v(36.83, 15.7) * mm, "end": v(36.97, 15.66) * mm});
            skLineSegment(sketch, "E2095", {"start": v(36.97, 15.66) * mm, "end": v(37.1, 15.6) * mm});
            skLineSegment(sketch, "E2096", {"start": v(37.1, 15.6) * mm, "end": v(37.23, 15.5) * mm});
            skLineSegment(sketch, "E2097", {"start": v(37.23, 15.5) * mm, "end": v(37.33, 15.4) * mm});
            skLineSegment(sketch, "E2098", {"start": v(37.33, 15.4) * mm, "end": v(37.42, 15.28) * mm});
            skLineSegment(sketch, "E2099", {"start": v(37.42, 15.28) * mm, "end": v(37.5, 15.14) * mm});
            skLineSegment(sketch, "E2100", {"start": v(37.5, 15.14) * mm, "end": v(37.54, 15) * mm});
            skLineSegment(sketch, "E2101", {"start": v(37.54, 15) * mm, "end": v(37.56, 14.85) * mm});
            skLineSegment(sketch, "E2102", {"start": v(37.56, 14.85) * mm, "end": v(37.56, 14.7) * mm});
            skLineSegment(sketch, "E2103", {"start": v(37.56, 12.17) * mm, "end": v(37.54, 12.02) * mm});
            skLineSegment(sketch, "E2104", {"start": v(37.54, 12.02) * mm, "end": v(37.5, 11.88) * mm});
            skLineSegment(sketch, "E2105", {"start": v(37.5, 11.88) * mm, "end": v(37.42, 11.74) * mm});
            skLineSegment(sketch, "E2106", {"start": v(37.42, 11.74) * mm, "end": v(37.33, 11.62) * mm});
            skLineSegment(sketch, "E2107", {"start": v(37.33, 11.62) * mm, "end": v(37.23, 11.52) * mm});
            skLineSegment(sketch, "E2108", {"start": v(37.23, 11.52) * mm, "end": v(37.1, 11.43) * mm});
            skLineSegment(sketch, "E2109", {"start": v(37.1, 11.43) * mm, "end": v(36.97, 11.36) * mm});
            skLineSegment(sketch, "E2110", {"start": v(36.97, 11.36) * mm, "end": v(36.83, 11.32) * mm});
            skLineSegment(sketch, "E2111", {"start": v(36.83, 11.32) * mm, "end": v(36.69, 11.3) * mm});
            skLineSegment(sketch, "E2112", {"start": v(36.69, 11.3) * mm, "end": v(36.54, 11.3) * mm});
            skLineSegment(sketch, "E2113", {"start": v(36.54, 11.3) * mm, "end": v(36.39, 11.32) * mm});
            skLineSegment(sketch, "E2114", {"start": v(36.39, 11.32) * mm, "end": v(36.25, 11.36) * mm});
            skLineSegment(sketch, "E2115", {"start": v(36.25, 11.36) * mm, "end": v(36.11, 11.43) * mm});
            skLineSegment(sketch, "E2116", {"start": v(36.11, 11.43) * mm, "end": v(36, 11.52) * mm});
            skLineSegment(sketch, "E2117", {"start": v(36, 11.52) * mm, "end": v(35.89, 11.62) * mm});
            skLineSegment(sketch, "E2118", {"start": v(35.89, 11.62) * mm, "end": v(35.8, 11.74) * mm});
            skLineSegment(sketch, "E2119", {"start": v(35.8, 11.74) * mm, "end": v(35.73, 11.88) * mm});
            skLineSegment(sketch, "E2120", {"start": v(35.73, 11.88) * mm, "end": v(35.68, 12.02) * mm});
            skLineSegment(sketch, "E2121", {"start": v(35.68, 12.02) * mm, "end": v(35.66, 12.17) * mm});
            skLineSegment(sketch, "E2122", {"start": v(35.66, 12.17) * mm, "end": v(35.66, 12.31) * mm});
            skLineSegment(sketch, "E2123", {"start": v(35.66, 12.31) * mm, "end": v(35.68, 12.46) * mm});
            skLineSegment(sketch, "E2124", {"start": v(35.68, 12.46) * mm, "end": v(35.73, 12.6) * mm});
            skLineSegment(sketch, "E2125", {"start": v(35.73, 12.6) * mm, "end": v(35.8, 12.74) * mm});
            skLineSegment(sketch, "E2126", {"start": v(35.8, 12.74) * mm, "end": v(35.89, 12.86) * mm});
            skLineSegment(sketch, "E2127", {"start": v(35.89, 12.86) * mm, "end": v(36, 12.96) * mm});
            skLineSegment(sketch, "E2128", {"start": v(36, 12.96) * mm, "end": v(36.11, 13.05) * mm});
            skLineSegment(sketch, "E2129", {"start": v(36.11, 13.05) * mm, "end": v(36.25, 13.12) * mm});
            skLineSegment(sketch, "E2130", {"start": v(36.25, 13.12) * mm, "end": v(36.39, 13.16) * mm});
            skLineSegment(sketch, "E2131", {"start": v(36.39, 13.16) * mm, "end": v(36.54, 13.19) * mm});
            skLineSegment(sketch, "E2132", {"start": v(36.54, 13.19) * mm, "end": v(36.69, 13.19) * mm});
            skLineSegment(sketch, "E2133", {"start": v(36.69, 13.19) * mm, "end": v(36.83, 13.16) * mm});
            skLineSegment(sketch, "E2134", {"start": v(36.83, 13.16) * mm, "end": v(36.97, 13.12) * mm});
            skLineSegment(sketch, "E2135", {"start": v(36.97, 13.12) * mm, "end": v(37.1, 13.05) * mm});
            skLineSegment(sketch, "E2136", {"start": v(37.1, 13.05) * mm, "end": v(37.23, 12.96) * mm});
            skLineSegment(sketch, "E2137", {"start": v(37.23, 12.96) * mm, "end": v(37.33, 12.86) * mm});
            skLineSegment(sketch, "E2138", {"start": v(37.33, 12.86) * mm, "end": v(37.42, 12.74) * mm});
            skLineSegment(sketch, "E2139", {"start": v(37.42, 12.74) * mm, "end": v(37.5, 12.6) * mm});
            skLineSegment(sketch, "E2140", {"start": v(37.5, 12.6) * mm, "end": v(37.54, 12.46) * mm});
            skLineSegment(sketch, "E2141", {"start": v(37.54, 12.46) * mm, "end": v(37.56, 12.31) * mm});
            skLineSegment(sketch, "E2142", {"start": v(37.56, 12.31) * mm, "end": v(37.56, 12.17) * mm});
            skLineSegment(sketch, "E2143", {"start": v(37.56, 9.63) * mm, "end": v(37.54, 9.48) * mm});
            skLineSegment(sketch, "E2144", {"start": v(37.54, 9.48) * mm, "end": v(37.5, 9.34) * mm});
            skLineSegment(sketch, "E2145", {"start": v(37.5, 9.34) * mm, "end": v(37.42, 9.2) * mm});
            skLineSegment(sketch, "E2146", {"start": v(37.42, 9.2) * mm, "end": v(37.33, 9.08) * mm});
            skLineSegment(sketch, "E2147", {"start": v(37.33, 9.08) * mm, "end": v(37.23, 8.98) * mm});
            skLineSegment(sketch, "E2148", {"start": v(37.23, 8.98) * mm, "end": v(37.1, 8.89) * mm});
            skLineSegment(sketch, "E2149", {"start": v(37.1, 8.89) * mm, "end": v(36.97, 8.82) * mm});
            skLineSegment(sketch, "E2150", {"start": v(36.97, 8.82) * mm, "end": v(36.83, 8.78) * mm});
            skLineSegment(sketch, "E2151", {"start": v(36.83, 8.78) * mm, "end": v(36.69, 8.75) * mm});
            skLineSegment(sketch, "E2152", {"start": v(36.69, 8.75) * mm, "end": v(36.54, 8.75) * mm});
            skLineSegment(sketch, "E2153", {"start": v(36.54, 8.75) * mm, "end": v(36.39, 8.78) * mm});
            skLineSegment(sketch, "E2154", {"start": v(36.39, 8.78) * mm, "end": v(36.25, 8.82) * mm});
            skLineSegment(sketch, "E2155", {"start": v(36.25, 8.82) * mm, "end": v(36.11, 8.89) * mm});
            skLineSegment(sketch, "E2156", {"start": v(36.11, 8.89) * mm, "end": v(36, 8.98) * mm});
            skLineSegment(sketch, "E2157", {"start": v(36, 8.98) * mm, "end": v(35.89, 9.08) * mm});
            skLineSegment(sketch, "E2158", {"start": v(35.89, 9.08) * mm, "end": v(35.8, 9.2) * mm});
            skLineSegment(sketch, "E2159", {"start": v(35.8, 9.2) * mm, "end": v(35.73, 9.34) * mm});
            skLineSegment(sketch, "E2160", {"start": v(35.73, 9.34) * mm, "end": v(35.68, 9.48) * mm});
            skLineSegment(sketch, "E2161", {"start": v(35.68, 9.48) * mm, "end": v(35.66, 9.63) * mm});
            skLineSegment(sketch, "E2162", {"start": v(35.66, 9.63) * mm, "end": v(35.66, 9.77) * mm});
            skLineSegment(sketch, "E2163", {"start": v(35.66, 9.77) * mm, "end": v(35.68, 9.92) * mm});
            skLineSegment(sketch, "E2164", {"start": v(35.68, 9.92) * mm, "end": v(35.73, 10.06) * mm});
            skLineSegment(sketch, "E2165", {"start": v(35.73, 10.06) * mm, "end": v(35.8, 10.2) * mm});
            skLineSegment(sketch, "E2166", {"start": v(35.8, 10.2) * mm, "end": v(35.89, 10.32) * mm});
            skLineSegment(sketch, "E2167", {"start": v(35.89, 10.32) * mm, "end": v(36, 10.42) * mm});
            skLineSegment(sketch, "E2168", {"start": v(36, 10.42) * mm, "end": v(36.11, 10.51) * mm});
            skLineSegment(sketch, "E2169", {"start": v(36.11, 10.51) * mm, "end": v(36.25, 10.58) * mm});
            skLineSegment(sketch, "E2170", {"start": v(36.25, 10.58) * mm, "end": v(36.39, 10.62) * mm});
            skLineSegment(sketch, "E2171", {"start": v(36.39, 10.62) * mm, "end": v(36.54, 10.65) * mm});
            skLineSegment(sketch, "E2172", {"start": v(36.54, 10.65) * mm, "end": v(36.69, 10.65) * mm});
            skLineSegment(sketch, "E2173", {"start": v(36.69, 10.65) * mm, "end": v(36.83, 10.62) * mm});
            skLineSegment(sketch, "E2174", {"start": v(36.83, 10.62) * mm, "end": v(36.97, 10.58) * mm});
            skLineSegment(sketch, "E2175", {"start": v(36.97, 10.58) * mm, "end": v(37.1, 10.51) * mm});
            skLineSegment(sketch, "E2176", {"start": v(37.1, 10.51) * mm, "end": v(37.23, 10.42) * mm});
            skLineSegment(sketch, "E2177", {"start": v(37.23, 10.42) * mm, "end": v(37.33, 10.32) * mm});
            skLineSegment(sketch, "E2178", {"start": v(37.33, 10.32) * mm, "end": v(37.42, 10.2) * mm});
            skLineSegment(sketch, "E2179", {"start": v(37.42, 10.2) * mm, "end": v(37.5, 10.06) * mm});
            skLineSegment(sketch, "E2180", {"start": v(37.5, 10.06) * mm, "end": v(37.54, 9.92) * mm});
            skLineSegment(sketch, "E2181", {"start": v(37.54, 9.92) * mm, "end": v(37.56, 9.77) * mm});
            skLineSegment(sketch, "E2182", {"start": v(37.56, 9.77) * mm, "end": v(37.56, 9.63) * mm});
            skLineSegment(sketch, "E2183", {"start": v(13.4, 4.77) * mm, "end": v(13.49, 4.77) * mm});
            skLineSegment(sketch, "E2184", {"start": v(13.49, 4.77) * mm, "end": v(13.49, 22.74) * mm});
            skLineSegment(sketch, "E2185", {"start": v(13.49, 22.74) * mm, "end": v(12.84, 22.74) * mm});
            skLineSegment(sketch, "E2186", {"start": v(12.84, 22.74) * mm, "end": v(12.84, 24.64) * mm});
            skLineSegment(sketch, "E2187", {"start": v(12.84, 24.64) * mm, "end": v(14.74, 24.64) * mm});
            skLineSegment(sketch, "E2188", {"start": v(14.74, 24.64) * mm, "end": v(14.74, 23.77) * mm});
            skLineSegment(sketch, "E2189", {"start": v(14.74, 23.77) * mm, "end": v(14.82, 23.69) * mm});
            skLineSegment(sketch, "E2190", {"start": v(14.82, 23.69) * mm, "end": v(14.88, 23.59) * mm});
            skLineSegment(sketch, "E2191", {"start": v(14.88, 23.59) * mm, "end": v(14.93, 23.48) * mm});
            skLineSegment(sketch, "E2192", {"start": v(14.93, 23.48) * mm, "end": v(14.95, 23.37) * mm});
            skLineSegment(sketch, "E2193", {"start": v(14.95, 23.37) * mm, "end": v(14.96, 23.25) * mm});
            skLineSegment(sketch, "E2194", {"start": v(14.96, 23.25) * mm, "end": v(14.96, 4.78) * mm});
            skLineSegment(sketch, "E2195", {"start": v(14.96, 4.78) * mm, "end": v(15.17, 4.77) * mm});
            skLineSegment(sketch, "E2196", {"start": v(15.17, 4.77) * mm, "end": v(15.17, 2.87) * mm});
            skLineSegment(sketch, "E2197", {"start": v(15.17, 2.87) * mm, "end": v(13.27, 2.87) * mm});
            skLineSegment(sketch, "E2198", {"start": v(13.27, 2.87) * mm, "end": v(13.27, 4.77) * mm});
            skLineSegment(sketch, "E2199", {"start": v(13.27, 4.77) * mm, "end": v(13.4, 4.77) * mm});
            skLineSegment(sketch, "E2200", {"start": v(17.71, 3.75) * mm, "end": v(17.69, 3.6) * mm});
            skLineSegment(sketch, "E2201", {"start": v(17.69, 3.6) * mm, "end": v(17.64, 3.46) * mm});
            skLineSegment(sketch, "E2202", {"start": v(17.64, 3.46) * mm, "end": v(17.57, 3.32) * mm});
            skLineSegment(sketch, "E2203", {"start": v(17.57, 3.32) * mm, "end": v(17.49, 3.2) * mm});
            skLineSegment(sketch, "E2204", {"start": v(17.49, 3.2) * mm, "end": v(17.38, 3.1) * mm});
            skLineSegment(sketch, "E2205", {"start": v(17.38, 3.1) * mm, "end": v(17.26, 3) * mm});
            skLineSegment(sketch, "E2206", {"start": v(17.26, 3) * mm, "end": v(17.13, 2.94) * mm});
            skLineSegment(sketch, "E2207", {"start": v(17.13, 2.94) * mm, "end": v(16.98, 2.9) * mm});
            skLineSegment(sketch, "E2208", {"start": v(16.98, 2.9) * mm, "end": v(16.84, 2.87) * mm});
            skLineSegment(sketch, "E2209", {"start": v(16.84, 2.87) * mm, "end": v(16.69, 2.87) * mm});
            skLineSegment(sketch, "E2210", {"start": v(16.69, 2.87) * mm, "end": v(16.54, 2.9) * mm});
            skLineSegment(sketch, "E2211", {"start": v(16.54, 2.9) * mm, "end": v(16.4, 2.94) * mm});
            skLineSegment(sketch, "E2212", {"start": v(16.4, 2.94) * mm, "end": v(16.27, 3) * mm});
            skLineSegment(sketch, "E2213", {"start": v(16.27, 3) * mm, "end": v(16.14, 3.1) * mm});
            skLineSegment(sketch, "E2214", {"start": v(16.14, 3.1) * mm, "end": v(16.04, 3.2) * mm});
            skLineSegment(sketch, "E2215", {"start": v(16.04, 3.2) * mm, "end": v(15.95, 3.32) * mm});
            skLineSegment(sketch, "E2216", {"start": v(15.95, 3.32) * mm, "end": v(15.89, 3.46) * mm});
            skLineSegment(sketch, "E2217", {"start": v(15.89, 3.46) * mm, "end": v(15.84, 3.6) * mm});
            skLineSegment(sketch, "E2218", {"start": v(15.84, 3.6) * mm, "end": v(15.81, 3.75) * mm});
            skLineSegment(sketch, "E2219", {"start": v(15.81, 3.75) * mm, "end": v(15.81, 3.9) * mm});
            skLineSegment(sketch, "E2220", {"start": v(15.81, 3.9) * mm, "end": v(15.84, 4.04) * mm});
            skLineSegment(sketch, "E2221", {"start": v(15.84, 4.04) * mm, "end": v(15.89, 4.18) * mm});
            skLineSegment(sketch, "E2222", {"start": v(15.89, 4.18) * mm, "end": v(15.95, 4.32) * mm});
            skLineSegment(sketch, "E2223", {"start": v(15.95, 4.32) * mm, "end": v(16.03, 4.42) * mm});
            skLineSegment(sketch, "E2224", {"start": v(16.03, 4.42) * mm, "end": v(16.03, 22.78) * mm});
            skLineSegment(sketch, "E2225", {"start": v(16.03, 22.78) * mm, "end": v(15.83, 22.88) * mm});
            skLineSegment(sketch, "E2226", {"start": v(15.83, 22.88) * mm, "end": v(15.71, 22.96) * mm});
            skLineSegment(sketch, "E2227", {"start": v(15.71, 22.96) * mm, "end": v(15.6, 23.07) * mm});
            skLineSegment(sketch, "E2228", {"start": v(15.6, 23.07) * mm, "end": v(15.52, 23.2) * mm});
            skLineSegment(sketch, "E2229", {"start": v(15.52, 23.2) * mm, "end": v(15.45, 23.32) * mm});
            skLineSegment(sketch, "E2230", {"start": v(15.45, 23.32) * mm, "end": v(15.4, 23.46) * mm});
            skLineSegment(sketch, "E2231", {"start": v(15.4, 23.46) * mm, "end": v(15.38, 23.61) * mm});
            skLineSegment(sketch, "E2232", {"start": v(15.38, 23.61) * mm, "end": v(15.38, 23.76) * mm});
            skLineSegment(sketch, "E2233", {"start": v(15.38, 23.76) * mm, "end": v(15.4, 23.9) * mm});
            skLineSegment(sketch, "E2234", {"start": v(15.4, 23.9) * mm, "end": v(15.45, 24.05) * mm});
            skLineSegment(sketch, "E2235", {"start": v(15.45, 24.05) * mm, "end": v(15.52, 24.18) * mm});
            skLineSegment(sketch, "E2236", {"start": v(15.52, 24.18) * mm, "end": v(15.6, 24.3) * mm});
            skLineSegment(sketch, "E2237", {"start": v(15.6, 24.3) * mm, "end": v(15.71, 24.4) * mm});
            skLineSegment(sketch, "E2238", {"start": v(15.71, 24.4) * mm, "end": v(15.83, 24.5) * mm});
            skLineSegment(sketch, "E2239", {"start": v(15.83, 24.5) * mm, "end": v(15.97, 24.57) * mm});
            skLineSegment(sketch, "E2240", {"start": v(15.97, 24.57) * mm, "end": v(16.1, 24.61) * mm});
            skLineSegment(sketch, "E2241", {"start": v(16.1, 24.61) * mm, "end": v(16.26, 24.64) * mm});
            skLineSegment(sketch, "E2242", {"start": v(16.26, 24.64) * mm, "end": v(16.4, 24.64) * mm});
            skLineSegment(sketch, "E2243", {"start": v(16.4, 24.64) * mm, "end": v(16.55, 24.61) * mm});
            skLineSegment(sketch, "E2244", {"start": v(16.55, 24.61) * mm, "end": v(16.7, 24.57) * mm});
            skLineSegment(sketch, "E2245", {"start": v(16.7, 24.57) * mm, "end": v(16.83, 24.5) * mm});
            skLineSegment(sketch, "E2246", {"start": v(16.83, 24.5) * mm, "end": v(16.95, 24.4) * mm});
            skLineSegment(sketch, "E2247", {"start": v(16.95, 24.4) * mm, "end": v(17.05, 24.3) * mm});
            skLineSegment(sketch, "E2248", {"start": v(17.05, 24.3) * mm, "end": v(17.14, 24.18) * mm});
            skLineSegment(sketch, "E2249", {"start": v(17.14, 24.18) * mm, "end": v(17.2, 24.05) * mm});
            skLineSegment(sketch, "E2250", {"start": v(17.2, 24.05) * mm, "end": v(17.25, 23.9) * mm});
            skLineSegment(sketch, "E2251", {"start": v(17.25, 23.9) * mm, "end": v(17.28, 23.78) * mm});
            skLineSegment(sketch, "E2252", {"start": v(17.28, 23.78) * mm, "end": v(17.36, 23.69) * mm});
            skLineSegment(sketch, "E2253", {"start": v(17.36, 23.69) * mm, "end": v(17.42, 23.59) * mm});
            skLineSegment(sketch, "E2254", {"start": v(17.42, 23.59) * mm, "end": v(17.47, 23.48) * mm});
            skLineSegment(sketch, "E2255", {"start": v(17.47, 23.48) * mm, "end": v(17.5, 23.37) * mm});
            skLineSegment(sketch, "E2256", {"start": v(17.5, 23.37) * mm, "end": v(17.5, 23.25) * mm});
            skLineSegment(sketch, "E2257", {"start": v(17.5, 23.25) * mm, "end": v(17.5, 4.42) * mm});
            skLineSegment(sketch, "E2258", {"start": v(17.5, 4.42) * mm, "end": v(17.57, 4.32) * mm});
            skLineSegment(sketch, "E2259", {"start": v(17.57, 4.32) * mm, "end": v(17.64, 4.18) * mm});
            skLineSegment(sketch, "E2260", {"start": v(17.64, 4.18) * mm, "end": v(17.69, 4.04) * mm});
            skLineSegment(sketch, "E2261", {"start": v(17.69, 4.04) * mm, "end": v(17.71, 3.9) * mm});
            skLineSegment(sketch, "E2262", {"start": v(17.71, 3.9) * mm, "end": v(17.71, 3.75) * mm});
            skLineSegment(sketch, "E2263", {"start": v(-22.86, -12.97) * mm, "end": v(-22.9, -13.24) * mm});
            skLineSegment(sketch, "E2264", {"start": v(-22.9, -13.24) * mm, "end": v(-22.95, -13.5) * mm});
            skLineSegment(sketch, "E2265", {"start": v(-22.95, -13.5) * mm, "end": v(-23.03, -13.77) * mm});
            skLineSegment(sketch, "E2266", {"start": v(-23.03, -13.77) * mm, "end": v(-23.14, -14.02) * mm});
            skLineSegment(sketch, "E2267", {"start": v(-23.14, -14.02) * mm, "end": v(-23.27, -14.25) * mm});
            skLineSegment(sketch, "E2268", {"start": v(-23.27, -14.25) * mm, "end": v(-23.43, -14.47) * mm});
            skLineSegment(sketch, "E2269", {"start": v(-23.43, -14.47) * mm, "end": v(-23.6, -14.68) * mm});
            skLineSegment(sketch, "E2270", {"start": v(-23.6, -14.68) * mm, "end": v(-23.8, -14.86) * mm});
            skLineSegment(sketch, "E2271", {"start": v(-23.8, -14.86) * mm, "end": v(-24.02, -15.02) * mm});
            skLineSegment(sketch, "E2272", {"start": v(-24.02, -15.02) * mm, "end": v(-24.25, -15.16) * mm});
            skLineSegment(sketch, "E2273", {"start": v(-24.25, -15.16) * mm, "end": v(-24.5, -15.28) * mm});
            skLineSegment(sketch, "E2274", {"start": v(-24.5, -15.28) * mm, "end": v(-24.75, -15.37) * mm});
            skLineSegment(sketch, "E2275", {"start": v(-24.75, -15.37) * mm, "end": v(-25.01, -15.44) * mm});
            skLineSegment(sketch, "E2276", {"start": v(-25.01, -15.44) * mm, "end": v(-25.28, -15.47) * mm});
            skLineSegment(sketch, "E2277", {"start": v(-25.28, -15.47) * mm, "end": v(-25.55, -15.48) * mm});
            skLineSegment(sketch, "E2278", {"start": v(-25.55, -15.48) * mm, "end": v(-25.82, -15.46) * mm});
            skLineSegment(sketch, "E2279", {"start": v(-25.82, -15.46) * mm, "end": v(-26.09, -15.42) * mm});
            skLineSegment(sketch, "E2280", {"start": v(-26.09, -15.42) * mm, "end": v(-26.35, -15.34) * mm});
            skLineSegment(sketch, "E2281", {"start": v(-26.35, -15.34) * mm, "end": v(-26.6, -15.24) * mm});
            skLineSegment(sketch, "E2282", {"start": v(-26.6, -15.24) * mm, "end": v(-26.84, -15.12) * mm});
            skLineSegment(sketch, "E2283", {"start": v(-26.84, -15.12) * mm, "end": v(-27.07, -14.97) * mm});
            skLineSegment(sketch, "E2284", {"start": v(-27.07, -14.97) * mm, "end": v(-27.28, -14.8) * mm});
            skLineSegment(sketch, "E2285", {"start": v(-27.28, -14.8) * mm, "end": v(-27.47, -14.6) * mm});
            skLineSegment(sketch, "E2286", {"start": v(-27.47, -14.6) * mm, "end": v(-27.64, -14.4) * mm});
            skLineSegment(sketch, "E2287", {"start": v(-27.64, -14.4) * mm, "end": v(-27.79, -14.17) * mm});
            skLineSegment(sketch, "E2288", {"start": v(-27.79, -14.17) * mm, "end": v(-27.9, -13.92) * mm});
            skLineSegment(sketch, "E2289", {"start": v(-27.9, -13.92) * mm, "end": v(-28, -13.67) * mm});
            skLineSegment(sketch, "E2290", {"start": v(-28, -13.67) * mm, "end": v(-28.08, -13.41) * mm});
            skLineSegment(sketch, "E2291", {"start": v(-28.08, -13.41) * mm, "end": v(-28.13, -13.14) * mm});
            skLineSegment(sketch, "E2292", {"start": v(-28.13, -13.14) * mm, "end": v(-28.14, -12.88) * mm});
            skLineSegment(sketch, "E2293", {"start": v(-28.14, -12.88) * mm, "end": v(-28.13, -12.6) * mm});
            skLineSegment(sketch, "E2294", {"start": v(-28.13, -12.6) * mm, "end": v(-28.1, -12.34) * mm});
            skLineSegment(sketch, "E2295", {"start": v(-28.1, -12.34) * mm, "end": v(-28.03, -12.07) * mm});
            skLineSegment(sketch, "E2296", {"start": v(-28.03, -12.07) * mm, "end": v(-27.94, -11.82) * mm});
            skLineSegment(sketch, "E2297", {"start": v(-27.94, -11.82) * mm, "end": v(-27.82, -11.57) * mm});
            skLineSegment(sketch, "E2298", {"start": v(-27.82, -11.57) * mm, "end": v(-27.68, -11.34) * mm});
            skLineSegment(sketch, "E2299", {"start": v(-27.68, -11.34) * mm, "end": v(-27.51, -11.13) * mm});
            skLineSegment(sketch, "E2300", {"start": v(-27.51, -11.13) * mm, "end": v(-27.33, -10.93) * mm});
            skLineSegment(sketch, "E2301", {"start": v(-27.33, -10.93) * mm, "end": v(-27.12, -10.75) * mm});
            skLineSegment(sketch, "E2302", {"start": v(-27.12, -10.75) * mm, "end": v(-26.9, -10.6) * mm});
            skLineSegment(sketch, "E2303", {"start": v(-26.9, -10.6) * mm, "end": v(-26.66, -10.47) * mm});
            skLineSegment(sketch, "E2304", {"start": v(-26.66, -10.47) * mm, "end": v(-26.42, -10.36) * mm});
            skLineSegment(sketch, "E2305", {"start": v(-26.42, -10.36) * mm, "end": v(-26.16, -10.28) * mm});
            skLineSegment(sketch, "E2306", {"start": v(-26.16, -10.28) * mm, "end": v(-25.9, -10.23) * mm});
            skLineSegment(sketch, "E2307", {"start": v(-25.9, -10.23) * mm, "end": v(-25.62, -10.2) * mm});
            skLineSegment(sketch, "E2308", {"start": v(-25.62, -10.2) * mm, "end": v(-25.35, -10.2) * mm});
            skLineSegment(sketch, "E2309", {"start": v(-25.35, -10.2) * mm, "end": v(-25.08, -10.23) * mm});
            skLineSegment(sketch, "E2310", {"start": v(-25.08, -10.23) * mm, "end": v(-24.82, -10.29) * mm});
            skLineSegment(sketch, "E2311", {"start": v(-24.82, -10.29) * mm, "end": v(-24.56, -10.37) * mm});
            skLineSegment(sketch, "E2312", {"start": v(-24.56, -10.37) * mm, "end": v(-24.31, -10.48) * mm});
            skLineSegment(sketch, "E2313", {"start": v(-24.31, -10.48) * mm, "end": v(-24.08, -10.61) * mm});
            skLineSegment(sketch, "E2314", {"start": v(-24.08, -10.61) * mm, "end": v(-23.86, -10.77) * mm});
            skLineSegment(sketch, "E2315", {"start": v(-23.86, -10.77) * mm, "end": v(-23.65, -10.95) * mm});
            skLineSegment(sketch, "E2316", {"start": v(-23.65, -10.95) * mm, "end": v(-23.47, -11.15) * mm});
            skLineSegment(sketch, "E2317", {"start": v(-23.47, -11.15) * mm, "end": v(-23.3, -11.37) * mm});
            skLineSegment(sketch, "E2318", {"start": v(-23.3, -11.37) * mm, "end": v(-23.17, -11.6) * mm});
            skLineSegment(sketch, "E2319", {"start": v(-23.17, -11.6) * mm, "end": v(-23.05, -11.84) * mm});
            skLineSegment(sketch, "E2320", {"start": v(-23.05, -11.84) * mm, "end": v(-22.96, -12.1) * mm});
            skLineSegment(sketch, "E2321", {"start": v(-22.96, -12.1) * mm, "end": v(-22.9, -12.36) * mm});
            skLineSegment(sketch, "E2322", {"start": v(-22.9, -12.36) * mm, "end": v(-22.87, -12.63) * mm});
            skLineSegment(sketch, "E2323", {"start": v(-22.87, -12.63) * mm, "end": v(-22.86, -12.84) * mm});
            skLineSegment(sketch, "E2324", {"start": v(-22.86, -12.84) * mm, "end": v(-22.86, -12.97) * mm});
            skLineSegment(sketch, "E2325", {"start": v(28.12, -12.87) * mm, "end": v(28.09, -13.14) * mm});
            skLineSegment(sketch, "E2326", {"start": v(28.09, -13.14) * mm, "end": v(28.03, -13.4) * mm});
            skLineSegment(sketch, "E2327", {"start": v(28.03, -13.4) * mm, "end": v(27.95, -13.67) * mm});
            skLineSegment(sketch, "E2328", {"start": v(27.95, -13.67) * mm, "end": v(27.84, -13.91) * mm});
            skLineSegment(sketch, "E2329", {"start": v(27.84, -13.91) * mm, "end": v(27.7, -14.15) * mm});
            skLineSegment(sketch, "E2330", {"start": v(27.7, -14.15) * mm, "end": v(27.55, -14.37) * mm});
            skLineSegment(sketch, "E2331", {"start": v(27.55, -14.37) * mm, "end": v(27.37, -14.57) * mm});
            skLineSegment(sketch, "E2332", {"start": v(27.37, -14.57) * mm, "end": v(27.18, -14.76) * mm});
            skLineSegment(sketch, "E2333", {"start": v(27.18, -14.76) * mm, "end": v(26.96, -14.92) * mm});
            skLineSegment(sketch, "E2334", {"start": v(26.96, -14.92) * mm, "end": v(26.73, -15.06) * mm});
            skLineSegment(sketch, "E2335", {"start": v(26.73, -15.06) * mm, "end": v(26.48, -15.18) * mm});
            skLineSegment(sketch, "E2336", {"start": v(26.48, -15.18) * mm, "end": v(26.23, -15.27) * mm});
            skLineSegment(sketch, "E2337", {"start": v(26.23, -15.27) * mm, "end": v(25.97, -15.33) * mm});
            skLineSegment(sketch, "E2338", {"start": v(25.97, -15.33) * mm, "end": v(25.7, -15.37) * mm});
            skLineSegment(sketch, "E2339", {"start": v(25.7, -15.37) * mm, "end": v(25.43, -15.38) * mm});
            skLineSegment(sketch, "E2340", {"start": v(25.43, -15.38) * mm, "end": v(25.16, -15.36) * mm});
            skLineSegment(sketch, "E2341", {"start": v(25.16, -15.36) * mm, "end": v(24.89, -15.31) * mm});
            skLineSegment(sketch, "E2342", {"start": v(24.89, -15.31) * mm, "end": v(24.63, -15.24) * mm});
            skLineSegment(sketch, "E2343", {"start": v(24.63, -15.24) * mm, "end": v(24.38, -15.14) * mm});
            skLineSegment(sketch, "E2344", {"start": v(24.38, -15.14) * mm, "end": v(24.14, -15.01) * mm});
            skLineSegment(sketch, "E2345", {"start": v(24.14, -15.01) * mm, "end": v(23.91, -14.86) * mm});
            skLineSegment(sketch, "E2346", {"start": v(23.91, -14.86) * mm, "end": v(23.7, -14.7) * mm});
            skLineSegment(sketch, "E2347", {"start": v(23.7, -14.7) * mm, "end": v(23.51, -14.5) * mm});
            skLineSegment(sketch, "E2348", {"start": v(23.51, -14.5) * mm, "end": v(23.34, -14.3) * mm});
            skLineSegment(sketch, "E2349", {"start": v(23.34, -14.3) * mm, "end": v(23.2, -14.06) * mm});
            skLineSegment(sketch, "E2350", {"start": v(23.2, -14.06) * mm, "end": v(23.07, -13.82) * mm});
            skLineSegment(sketch, "E2351", {"start": v(23.07, -13.82) * mm, "end": v(22.97, -13.57) * mm});
            skLineSegment(sketch, "E2352", {"start": v(22.97, -13.57) * mm, "end": v(22.9, -13.3) * mm});
            skLineSegment(sketch, "E2353", {"start": v(22.9, -13.3) * mm, "end": v(22.85, -13.04) * mm});
            skLineSegment(sketch, "E2354", {"start": v(22.85, -13.04) * mm, "end": v(22.83, -12.77) * mm});
            skLineSegment(sketch, "E2355", {"start": v(22.83, -12.77) * mm, "end": v(22.84, -12.5) * mm});
            skLineSegment(sketch, "E2356", {"start": v(22.84, -12.5) * mm, "end": v(22.88, -12.24) * mm});
            skLineSegment(sketch, "E2357", {"start": v(22.88, -12.24) * mm, "end": v(22.95, -11.97) * mm});
            skLineSegment(sketch, "E2358", {"start": v(22.95, -11.97) * mm, "end": v(23.04, -11.72) * mm});
            skLineSegment(sketch, "E2359", {"start": v(23.04, -11.72) * mm, "end": v(23.16, -11.47) * mm});
            skLineSegment(sketch, "E2360", {"start": v(23.16, -11.47) * mm, "end": v(23.3, -11.24) * mm});
            skLineSegment(sketch, "E2361", {"start": v(23.3, -11.24) * mm, "end": v(23.46, -11.03) * mm});
            skLineSegment(sketch, "E2362", {"start": v(23.46, -11.03) * mm, "end": v(23.65, -10.83) * mm});
            skLineSegment(sketch, "E2363", {"start": v(23.65, -10.83) * mm, "end": v(23.86, -10.65) * mm});
            skLineSegment(sketch, "E2364", {"start": v(23.86, -10.65) * mm, "end": v(24.08, -10.5) * mm});
            skLineSegment(sketch, "E2365", {"start": v(24.08, -10.5) * mm, "end": v(24.31, -10.37) * mm});
            skLineSegment(sketch, "E2366", {"start": v(24.31, -10.37) * mm, "end": v(24.56, -10.26) * mm});
            skLineSegment(sketch, "E2367", {"start": v(24.56, -10.26) * mm, "end": v(24.82, -10.18) * mm});
            skLineSegment(sketch, "E2368", {"start": v(24.82, -10.18) * mm, "end": v(25.09, -10.12) * mm});
            skLineSegment(sketch, "E2369", {"start": v(25.09, -10.12) * mm, "end": v(25.36, -10.1) * mm});
            skLineSegment(sketch, "E2370", {"start": v(25.36, -10.1) * mm, "end": v(25.63, -10.1) * mm});
            skLineSegment(sketch, "E2371", {"start": v(25.63, -10.1) * mm, "end": v(25.9, -10.13) * mm});
            skLineSegment(sketch, "E2372", {"start": v(25.9, -10.13) * mm, "end": v(26.16, -10.19) * mm});
            skLineSegment(sketch, "E2373", {"start": v(26.16, -10.19) * mm, "end": v(26.42, -10.27) * mm});
            skLineSegment(sketch, "E2374", {"start": v(26.42, -10.27) * mm, "end": v(26.66, -10.38) * mm});
            skLineSegment(sketch, "E2375", {"start": v(26.66, -10.38) * mm, "end": v(26.9, -10.51) * mm});
            skLineSegment(sketch, "E2376", {"start": v(26.9, -10.51) * mm, "end": v(27.12, -10.67) * mm});
            skLineSegment(sketch, "E2377", {"start": v(27.12, -10.67) * mm, "end": v(27.33, -10.85) * mm});
            skLineSegment(sketch, "E2378", {"start": v(27.33, -10.85) * mm, "end": v(27.5, -11.05) * mm});
            skLineSegment(sketch, "E2379", {"start": v(27.5, -11.05) * mm, "end": v(27.67, -11.26) * mm});
            skLineSegment(sketch, "E2380", {"start": v(27.67, -11.26) * mm, "end": v(27.81, -11.5) * mm});
            skLineSegment(sketch, "E2381", {"start": v(27.81, -11.5) * mm, "end": v(27.92, -11.74) * mm});
            skLineSegment(sketch, "E2382", {"start": v(27.92, -11.74) * mm, "end": v(28.01, -12) * mm});
            skLineSegment(sketch, "E2383", {"start": v(28.01, -12) * mm, "end": v(28.07, -12.26) * mm});
            skLineSegment(sketch, "E2384", {"start": v(28.07, -12.26) * mm, "end": v(28.11, -12.53) * mm});
            skLineSegment(sketch, "E2385", {"start": v(28.11, -12.53) * mm, "end": v(28.12, -12.74) * mm});
            skLineSegment(sketch, "E2386", {"start": v(28.12, -12.74) * mm, "end": v(28.12, -12.87) * mm});
            skLineSegment(sketch, "E2387", {"start": v(-12.88, -6.4) * mm, "end": v(-12.98, -6.45) * mm});
            skLineSegment(sketch, "E2388", {"start": v(-12.98, -6.45) * mm, "end": v(-13.1, -6.47) * mm});
            skLineSegment(sketch, "E2389", {"start": v(-13.1, -6.47) * mm, "end": v(-13.2, -6.47) * mm});
            skLineSegment(sketch, "E2390", {"start": v(-13.2, -6.47) * mm, "end": v(-13.31, -6.44) * mm});
            skLineSegment(sketch, "E2391", {"start": v(-13.31, -6.44) * mm, "end": v(-13.41, -6.38) * mm});
            skLineSegment(sketch, "E2392", {"start": v(-13.41, -6.38) * mm, "end": v(-13.5, -6.3) * mm});
            skLineSegment(sketch, "E2393", {"start": v(-13.5, -6.3) * mm, "end": v(-13.56, -6.21) * mm});
            skLineSegment(sketch, "E2394", {"start": v(-13.56, -6.21) * mm, "end": v(-13.6, -6.1) * mm});
            skLineSegment(sketch, "E2395", {"start": v(-13.6, -6.1) * mm, "end": v(-13.61, -6) * mm});
            skLineSegment(sketch, "E2396", {"start": v(-13.61, -6) * mm, "end": v(-13.6, -5.88) * mm});
            skLineSegment(sketch, "E2397", {"start": v(-13.6, -5.88) * mm, "end": v(-13.56, -5.77) * mm});
            skLineSegment(sketch, "E2398", {"start": v(-13.56, -5.77) * mm, "end": v(-13.5, -5.68) * mm});
            skLineSegment(sketch, "E2399", {"start": v(-13.5, -5.68) * mm, "end": v(-13.41, -5.6) * mm});
            skLineSegment(sketch, "E2400", {"start": v(-13.41, -5.6) * mm, "end": v(-13.31, -5.55) * mm});
            skLineSegment(sketch, "E2401", {"start": v(-13.31, -5.55) * mm, "end": v(-13.2, -5.52) * mm});
            skLineSegment(sketch, "E2402", {"start": v(-13.2, -5.52) * mm, "end": v(-13.1, -5.51) * mm});
            skLineSegment(sketch, "E2403", {"start": v(-13.1, -5.51) * mm, "end": v(-12.98, -5.53) * mm});
            skLineSegment(sketch, "E2404", {"start": v(-12.98, -5.53) * mm, "end": v(-12.88, -5.58) * mm});
            skLineSegment(sketch, "E2405", {"start": v(-12.88, -5.58) * mm, "end": v(-12.79, -5.65) * mm});
            skLineSegment(sketch, "E2406", {"start": v(-12.79, -5.65) * mm, "end": v(-12.72, -5.74) * mm});
            skLineSegment(sketch, "E2407", {"start": v(-12.72, -5.74) * mm, "end": v(-12.67, -5.84) * mm});
            skLineSegment(sketch, "E2408", {"start": v(-12.67, -5.84) * mm, "end": v(-12.65, -5.96) * mm});
            skLineSegment(sketch, "E2409", {"start": v(-12.65, -5.96) * mm, "end": v(-12.65, -6.03) * mm});
            skLineSegment(sketch, "E2410", {"start": v(-15.42, -6.4) * mm, "end": v(-15.52, -6.45) * mm});
            skLineSegment(sketch, "E2411", {"start": v(-15.52, -6.45) * mm, "end": v(-15.63, -6.47) * mm});
            skLineSegment(sketch, "E2412", {"start": v(-15.63, -6.47) * mm, "end": v(-15.75, -6.47) * mm});
            skLineSegment(sketch, "E2413", {"start": v(-15.75, -6.47) * mm, "end": v(-15.85, -6.44) * mm});
            skLineSegment(sketch, "E2414", {"start": v(-15.85, -6.44) * mm, "end": v(-15.95, -6.38) * mm});
            skLineSegment(sketch, "E2415", {"start": v(-15.95, -6.38) * mm, "end": v(-16.04, -6.3) * mm});
            skLineSegment(sketch, "E2416", {"start": v(-16.04, -6.3) * mm, "end": v(-16.1, -6.21) * mm});
            skLineSegment(sketch, "E2417", {"start": v(-16.1, -6.21) * mm, "end": v(-16.14, -6.1) * mm});
            skLineSegment(sketch, "E2418", {"start": v(-16.14, -6.1) * mm, "end": v(-16.15, -6) * mm});
            skLineSegment(sketch, "E2419", {"start": v(-16.15, -6) * mm, "end": v(-16.14, -5.88) * mm});
            skLineSegment(sketch, "E2420", {"start": v(-16.14, -5.88) * mm, "end": v(-16.1, -5.77) * mm});
            skLineSegment(sketch, "E2421", {"start": v(-16.1, -5.77) * mm, "end": v(-16.04, -5.68) * mm});
            skLineSegment(sketch, "E2422", {"start": v(-16.04, -5.68) * mm, "end": v(-15.95, -5.6) * mm});
            skLineSegment(sketch, "E2423", {"start": v(-15.95, -5.6) * mm, "end": v(-15.85, -5.55) * mm});
            skLineSegment(sketch, "E2424", {"start": v(-15.85, -5.55) * mm, "end": v(-15.75, -5.52) * mm});
            skLineSegment(sketch, "E2425", {"start": v(-15.75, -5.52) * mm, "end": v(-15.63, -5.51) * mm});
            skLineSegment(sketch, "E2426", {"start": v(-15.63, -5.51) * mm, "end": v(-15.52, -5.53) * mm});
            skLineSegment(sketch, "E2427", {"start": v(-15.52, -5.53) * mm, "end": v(-15.42, -5.58) * mm});
            skLineSegment(sketch, "E2428", {"start": v(-15.42, -5.58) * mm, "end": v(-15.33, -5.65) * mm});
            skLineSegment(sketch, "E2429", {"start": v(-15.33, -5.65) * mm, "end": v(-15.26, -5.74) * mm});
            skLineSegment(sketch, "E2430", {"start": v(-15.26, -5.74) * mm, "end": v(-15.21, -5.84) * mm});
            skLineSegment(sketch, "E2431", {"start": v(-15.21, -5.84) * mm, "end": v(-15.19, -5.96) * mm});
            skLineSegment(sketch, "E2432", {"start": v(-15.19, -5.96) * mm, "end": v(-15.19, -6.03) * mm});
            skLineSegment(sketch, "E2433", {"start": v(18.09, -0.41) * mm, "end": v(18.05, -0.3) * mm});
            skLineSegment(sketch, "E2434", {"start": v(18.05, -0.3) * mm, "end": v(18.04, -0.2) * mm});
            skLineSegment(sketch, "E2435", {"start": v(18.04, -0.2) * mm, "end": v(18.05, -0.08) * mm});
            skLineSegment(sketch, "E2436", {"start": v(18.05, -0.08) * mm, "end": v(18.09, 0.03) * mm});
            skLineSegment(sketch, "E2437", {"start": v(18.09, 0.03) * mm, "end": v(18.15, 0.12) * mm});
            skLineSegment(sketch, "E2438", {"start": v(18.15, 0.12) * mm, "end": v(18.24, 0.2) * mm});
            skLineSegment(sketch, "E2439", {"start": v(18.24, 0.2) * mm, "end": v(18.34, 0.25) * mm});
            skLineSegment(sketch, "E2440", {"start": v(18.34, 0.25) * mm, "end": v(18.45, 0.28) * mm});
            skLineSegment(sketch, "E2441", {"start": v(18.45, 0.28) * mm, "end": v(18.56, 0.29) * mm});
            skLineSegment(sketch, "E2442", {"start": v(18.56, 0.29) * mm, "end": v(18.67, 0.27) * mm});
            skLineSegment(sketch, "E2443", {"start": v(18.67, 0.27) * mm, "end": v(18.77, 0.22) * mm});
            skLineSegment(sketch, "E2444", {"start": v(18.77, 0.22) * mm, "end": v(18.86, 0.15) * mm});
            skLineSegment(sketch, "E2445", {"start": v(18.86, 0.15) * mm, "end": v(18.93, 0.06) * mm});
            skLineSegment(sketch, "E2446", {"start": v(18.93, 0.06) * mm, "end": v(18.98, -0.04) * mm});
            skLineSegment(sketch, "E2447", {"start": v(18.98, -0.04) * mm, "end": v(19, -0.15) * mm});
            skLineSegment(sketch, "E2448", {"start": v(19, -0.15) * mm, "end": v(19, -0.23) * mm});
            skLineSegment(sketch, "E2449", {"start": v(5.17, -2.96) * mm, "end": v(5.06, -2.98) * mm});
            skLineSegment(sketch, "E2450", {"start": v(5.06, -2.98) * mm, "end": v(4.95, -2.98) * mm});
            skLineSegment(sketch, "E2451", {"start": v(4.95, -2.98) * mm, "end": v(4.84, -2.95) * mm});
            skLineSegment(sketch, "E2452", {"start": v(4.84, -2.95) * mm, "end": v(4.74, -2.9) * mm});
            skLineSegment(sketch, "E2453", {"start": v(4.74, -2.9) * mm, "end": v(4.65, -2.81) * mm});
            skLineSegment(sketch, "E2454", {"start": v(4.65, -2.81) * mm, "end": v(4.59, -2.72) * mm});
            skLineSegment(sketch, "E2455", {"start": v(4.59, -2.72) * mm, "end": v(4.55, -2.61) * mm});
            skLineSegment(sketch, "E2456", {"start": v(4.55, -2.61) * mm, "end": v(4.54, -2.5) * mm});
            skLineSegment(sketch, "E2457", {"start": v(4.54, -2.5) * mm, "end": v(4.55, -2.39) * mm});
            skLineSegment(sketch, "E2458", {"start": v(4.55, -2.39) * mm, "end": v(4.59, -2.28) * mm});
            skLineSegment(sketch, "E2459", {"start": v(4.59, -2.28) * mm, "end": v(4.65, -2.19) * mm});
            skLineSegment(sketch, "E2460", {"start": v(4.65, -2.19) * mm, "end": v(4.74, -2.11) * mm});
            skLineSegment(sketch, "E2461", {"start": v(4.74, -2.11) * mm, "end": v(4.84, -2.05) * mm});
            skLineSegment(sketch, "E2462", {"start": v(4.84, -2.05) * mm, "end": v(4.95, -2.02) * mm});
            skLineSegment(sketch, "E2463", {"start": v(4.95, -2.02) * mm, "end": v(5.06, -2.02) * mm});
            skLineSegment(sketch, "E2464", {"start": v(5.06, -2.02) * mm, "end": v(5.17, -2.04) * mm});
            skLineSegment(sketch, "E2465", {"start": v(5.17, -2.04) * mm, "end": v(5.27, -2.09) * mm});
            skLineSegment(sketch, "E2466", {"start": v(5.27, -2.09) * mm, "end": v(5.36, -2.16) * mm});
            skLineSegment(sketch, "E2467", {"start": v(5.36, -2.16) * mm, "end": v(5.43, -2.25) * mm});
            skLineSegment(sketch, "E2468", {"start": v(5.43, -2.25) * mm, "end": v(5.48, -2.35) * mm});
            skLineSegment(sketch, "E2469", {"start": v(5.48, -2.35) * mm, "end": v(5.5, -2.46) * mm});
            skLineSegment(sketch, "E2470", {"start": v(5.5, -2.46) * mm, "end": v(5.5, -2.54) * mm});
            skLineSegment(sketch, "E2471", {"start": v(5.02, -4.27) * mm, "end": v(4.94, -4.2) * mm});
            skLineSegment(sketch, "E2472", {"start": v(4.94, -4.2) * mm, "end": v(4.87, -4.1) * mm});
            skLineSegment(sketch, "E2473", {"start": v(4.87, -4.1) * mm, "end": v(4.83, -4) * mm});
            skLineSegment(sketch, "E2474", {"start": v(4.83, -4) * mm, "end": v(4.82, -3.88) * mm});
            skLineSegment(sketch, "E2475", {"start": v(-4.33, 0.9) * mm, "end": v(-4.35, 0.8) * mm});
            skLineSegment(sketch, "E2476", {"start": v(-4.35, 0.8) * mm, "end": v(-4.4, 0.7) * mm});
            skLineSegment(sketch, "E2477", {"start": v(-4.4, 0.7) * mm, "end": v(-4.47, 0.6) * mm});
            skLineSegment(sketch, "E2478", {"start": v(-4.47, 0.6) * mm, "end": v(-4.56, 0.54) * mm});
            skLineSegment(sketch, "E2479", {"start": v(-4.56, 0.54) * mm, "end": v(-4.66, 0.49) * mm});
            skLineSegment(sketch, "E2480", {"start": v(-4.33, 0.99) * mm, "end": v(-4.33, 0.9) * mm});
            skLineSegment(sketch, "E2481", {"start": v(6, 3.03) * mm, "end": v(5.89, 3.03) * mm});
            skLineSegment(sketch, "E2482", {"start": v(5.89, 3.03) * mm, "end": v(5.78, 3.06) * mm});
            skLineSegment(sketch, "E2483", {"start": v(5.78, 3.06) * mm, "end": v(5.68, 3.12) * mm});
            skLineSegment(sketch, "E2484", {"start": v(5.68, 3.12) * mm, "end": v(5.6, 3.2) * mm});
            skLineSegment(sketch, "E2485", {"start": v(5.6, 3.2) * mm, "end": v(5.53, 3.29) * mm});
            skLineSegment(sketch, "E2486", {"start": v(9.04, 3.06) * mm, "end": v(8.94, 3) * mm});
            skLineSegment(sketch, "E2487", {"start": v(8.94, 3) * mm, "end": v(8.82, 2.99) * mm});
            skLineSegment(sketch, "E2488", {"start": v(8.82, 2.99) * mm, "end": v(8.71, 3) * mm});
            skLineSegment(sketch, "E2489", {"start": v(8.71, 3) * mm, "end": v(8.6, 3.03) * mm});
            skLineSegment(sketch, "E2490", {"start": v(8.6, 3.03) * mm, "end": v(8.5, 3.08) * mm});
            skLineSegment(sketch, "E2491", {"start": v(5.86, 0.7) * mm, "end": v(5.77, 0.77) * mm});
            skLineSegment(sketch, "E2492", {"start": v(5.77, 0.77) * mm, "end": v(5.7, 0.87) * mm});
            skLineSegment(sketch, "E2493", {"start": v(5.7, 0.87) * mm, "end": v(5.67, 0.97) * mm});
            skLineSegment(sketch, "E2494", {"start": v(5.67, 0.97) * mm, "end": v(5.66, 1.09) * mm});
            skLineSegment(sketch, "E2495", {"start": v(5.66, 1.09) * mm, "end": v(5.67, 1.2) * mm});
            skLineSegment(sketch, "E2496", {"start": v(5.67, 1.2) * mm, "end": v(5.7, 1.3) * mm});
            skLineSegment(sketch, "E2497", {"start": v(5.7, 1.3) * mm, "end": v(5.77, 1.4) * mm});
            skLineSegment(sketch, "E2498", {"start": v(5.77, 1.4) * mm, "end": v(5.86, 1.48) * mm});
            skLineSegment(sketch, "E2499", {"start": v(5.86, 1.48) * mm, "end": v(5.96, 1.53) * mm});
            skLineSegment(sketch, "E2500", {"start": v(5.96, 1.53) * mm, "end": v(6.07, 1.56) * mm});
            skLineSegment(sketch, "E2501", {"start": v(6.07, 1.56) * mm, "end": v(6.18, 1.57) * mm});
            skLineSegment(sketch, "E2502", {"start": v(6.18, 1.57) * mm, "end": v(6.29, 1.55) * mm});
            skLineSegment(sketch, "E2503", {"start": v(6.29, 1.55) * mm, "end": v(6.4, 1.5) * mm});
            skLineSegment(sketch, "E2504", {"start": v(6.4, 1.5) * mm, "end": v(6.48, 1.43) * mm});
            skLineSegment(sketch, "E2505", {"start": v(6.48, 1.43) * mm, "end": v(6.55, 1.34) * mm});
            skLineSegment(sketch, "E2506", {"start": v(6.55, 1.34) * mm, "end": v(6.6, 1.24) * mm});
            skLineSegment(sketch, "E2507", {"start": v(6.6, 1.24) * mm, "end": v(6.62, 1.13) * mm});
            skLineSegment(sketch, "E2508", {"start": v(6.62, 1.13) * mm, "end": v(6.62, 1.05) * mm});
            skLineSegment(sketch, "E2509", {"start": v(15.6, -5.64) * mm, "end": v(15.6, -6.6) * mm});
            skLineSegment(sketch, "E2510", {"start": v(15.6, -6.6) * mm, "end": v(14.64, -6.6) * mm});
            skLineSegment(sketch, "E2511", {"start": v(8.46, -5.7) * mm, "end": v(8.46, -6.66) * mm});
            skLineSegment(sketch, "E2512", {"start": v(30.11, -22.74) * mm, "end": v(31.88, -22.74) * mm});
            skLineSegment(sketch, "E2513", {"start": v(29.98, -24.64) * mm, "end": v(29.98, -22.74) * mm});
            skLineSegment(sketch, "E2514", {"start": v(29.98, -22.74) * mm, "end": v(30.11, -22.74) * mm});
            skLineSegment(sketch, "E2515", {"start": v(27.58, -23.2) * mm, "end": v(27.67, -23.07) * mm});
            skLineSegment(sketch, "E2516", {"start": v(27.67, -23.07) * mm, "end": v(27.77, -22.97) * mm});
            skLineSegment(sketch, "E2517", {"start": v(27.77, -22.97) * mm, "end": v(27.9, -22.88) * mm});
            skLineSegment(sketch, "E2518", {"start": v(27.9, -22.88) * mm, "end": v(28.03, -22.81) * mm});
            skLineSegment(sketch, "E2519", {"start": v(25.04, -23.2) * mm, "end": v(25.13, -23.07) * mm});
            skLineSegment(sketch, "E2520", {"start": v(25.13, -23.07) * mm, "end": v(25.23, -22.97) * mm});
            skLineSegment(sketch, "E2521", {"start": v(25.23, -22.97) * mm, "end": v(25.35, -22.88) * mm});
            skLineSegment(sketch, "E2522", {"start": v(25.35, -22.88) * mm, "end": v(25.49, -22.81) * mm});
            skLineSegment(sketch, "E2523", {"start": v(24.26, -23.76) * mm, "end": v(24.23, -23.91) * mm});
            skLineSegment(sketch, "E2524", {"start": v(24.23, -23.91) * mm, "end": v(24.19, -24.05) * mm});
            skLineSegment(sketch, "E2525", {"start": v(24.19, -24.05) * mm, "end": v(24.12, -24.19) * mm});
            skLineSegment(sketch, "E2526", {"start": v(24.12, -24.19) * mm, "end": v(24.03, -24.3) * mm});
            skLineSegment(sketch, "E2527", {"start": v(24.03, -24.3) * mm, "end": v(23.93, -24.41) * mm});
            skLineSegment(sketch, "E2528", {"start": v(23.93, -24.41) * mm, "end": v(23.8, -24.5) * mm});
            skLineSegment(sketch, "E2529", {"start": v(23.8, -24.5) * mm, "end": v(23.68, -24.57) * mm});
            skLineSegment(sketch, "E2530", {"start": v(23.68, -24.57) * mm, "end": v(23.53, -24.62) * mm});
            skLineSegment(sketch, "E2531", {"start": v(23.53, -24.62) * mm, "end": v(23.39, -24.64) * mm});
            skLineSegment(sketch, "E2532", {"start": v(23.39, -24.64) * mm, "end": v(23.24, -24.64) * mm});
            skLineSegment(sketch, "E2533", {"start": v(23.24, -24.64) * mm, "end": v(23.09, -24.62) * mm});
            skLineSegment(sketch, "E2534", {"start": v(23.09, -24.62) * mm, "end": v(22.95, -24.57) * mm});
            skLineSegment(sketch, "E2535", {"start": v(22.95, -24.57) * mm, "end": v(22.81, -24.5) * mm});
            skLineSegment(sketch, "E2536", {"start": v(22.81, -24.5) * mm, "end": v(22.7, -24.41) * mm});
            skLineSegment(sketch, "E2537", {"start": v(22.7, -24.41) * mm, "end": v(22.59, -24.3) * mm});
            skLineSegment(sketch, "E2538", {"start": v(22.59, -24.3) * mm, "end": v(22.5, -24.19) * mm});
            skLineSegment(sketch, "E2539", {"start": v(22.5, -24.19) * mm, "end": v(22.43, -24.05) * mm});
            skLineSegment(sketch, "E2540", {"start": v(22.43, -24.05) * mm, "end": v(22.39, -23.91) * mm});
            skLineSegment(sketch, "E2541", {"start": v(22.39, -23.91) * mm, "end": v(22.36, -23.76) * mm});
            skLineSegment(sketch, "E2542", {"start": v(22.36, -23.76) * mm, "end": v(22.36, -23.61) * mm});
            skLineSegment(sketch, "E2543", {"start": v(22.36, -23.61) * mm, "end": v(22.39, -23.47) * mm});
            skLineSegment(sketch, "E2544", {"start": v(22.39, -23.47) * mm, "end": v(22.43, -23.32) * mm});
            skLineSegment(sketch, "E2545", {"start": v(22.43, -23.32) * mm, "end": v(22.5, -23.2) * mm});
            skLineSegment(sketch, "E2546", {"start": v(22.5, -23.2) * mm, "end": v(22.59, -23.07) * mm});
            skLineSegment(sketch, "E2547", {"start": v(22.59, -23.07) * mm, "end": v(22.7, -22.97) * mm});
            skLineSegment(sketch, "E2548", {"start": v(22.7, -22.97) * mm, "end": v(22.81, -22.88) * mm});
            skLineSegment(sketch, "E2549", {"start": v(22.81, -22.88) * mm, "end": v(22.95, -22.81) * mm});
            skLineSegment(sketch, "E2550", {"start": v(22.95, -22.81) * mm, "end": v(23.09, -22.76) * mm});
            skLineSegment(sketch, "E2551", {"start": v(23.09, -22.76) * mm, "end": v(23.24, -22.74) * mm});
            skLineSegment(sketch, "E2552", {"start": v(23.24, -22.74) * mm, "end": v(23.39, -22.74) * mm});
            skLineSegment(sketch, "E2553", {"start": v(23.39, -22.74) * mm, "end": v(23.53, -22.76) * mm});
            skLineSegment(sketch, "E2554", {"start": v(23.53, -22.76) * mm, "end": v(23.68, -22.81) * mm});
            skLineSegment(sketch, "E2555", {"start": v(23.68, -22.81) * mm, "end": v(23.8, -22.88) * mm});
            skLineSegment(sketch, "E2556", {"start": v(23.8, -22.88) * mm, "end": v(23.93, -22.97) * mm});
            skLineSegment(sketch, "E2557", {"start": v(23.93, -22.97) * mm, "end": v(24.03, -23.07) * mm});
            skLineSegment(sketch, "E2558", {"start": v(24.03, -23.07) * mm, "end": v(24.12, -23.2) * mm});
            skLineSegment(sketch, "E2559", {"start": v(24.12, -23.2) * mm, "end": v(24.19, -23.32) * mm});
            skLineSegment(sketch, "E2560", {"start": v(24.19, -23.32) * mm, "end": v(24.23, -23.47) * mm});
            skLineSegment(sketch, "E2561", {"start": v(24.23, -23.47) * mm, "end": v(24.26, -23.61) * mm});
            skLineSegment(sketch, "E2562", {"start": v(24.26, -23.61) * mm, "end": v(24.26, -23.76) * mm});
            skLineSegment(sketch, "E2563", {"start": v(19.96, -23.2) * mm, "end": v(20.05, -23.07) * mm});
            skLineSegment(sketch, "E2564", {"start": v(20.05, -23.07) * mm, "end": v(20.15, -22.97) * mm});
            skLineSegment(sketch, "E2565", {"start": v(20.15, -22.97) * mm, "end": v(20.27, -22.88) * mm});
            skLineSegment(sketch, "E2566", {"start": v(20.27, -22.88) * mm, "end": v(20.4, -22.81) * mm});
            skLineSegment(sketch, "E2567", {"start": v(17.42, -23.2) * mm, "end": v(17.5, -23.07) * mm});
            skLineSegment(sketch, "E2568", {"start": v(17.5, -23.07) * mm, "end": v(17.61, -22.97) * mm});
            skLineSegment(sketch, "E2569", {"start": v(17.61, -22.97) * mm, "end": v(17.73, -22.88) * mm});
            skLineSegment(sketch, "E2570", {"start": v(17.73, -22.88) * mm, "end": v(17.87, -22.81) * mm});
            skLineSegment(sketch, "E2571", {"start": v(14.88, -23.2) * mm, "end": v(14.97, -23.07) * mm});
            skLineSegment(sketch, "E2572", {"start": v(14.97, -23.07) * mm, "end": v(15.07, -22.97) * mm});
            skLineSegment(sketch, "E2573", {"start": v(15.07, -22.97) * mm, "end": v(15.2, -22.88) * mm});
            skLineSegment(sketch, "E2574", {"start": v(15.2, -22.88) * mm, "end": v(15.33, -22.81) * mm});
            skLineSegment(sketch, "E2575", {"start": v(12.27, -23.32) * mm, "end": v(12.34, -23.2) * mm});
            skLineSegment(sketch, "E2576", {"start": v(12.34, -23.2) * mm, "end": v(12.43, -23.07) * mm});
            skLineSegment(sketch, "E2577", {"start": v(12.43, -23.07) * mm, "end": v(12.53, -22.97) * mm});
            skLineSegment(sketch, "E2578", {"start": v(9.8, -23.2) * mm, "end": v(9.89, -23.07) * mm});
            skLineSegment(sketch, "E2579", {"start": v(9.89, -23.07) * mm, "end": v(10, -22.97) * mm});
            skLineSegment(sketch, "E2580", {"start": v(10, -22.97) * mm, "end": v(10.11, -22.88) * mm});
            skLineSegment(sketch, "E2581", {"start": v(10.11, -22.88) * mm, "end": v(10.25, -22.81) * mm});
            skLineSegment(sketch, "E2582", {"start": v(7.26, -23.2) * mm, "end": v(7.35, -23.07) * mm});
            skLineSegment(sketch, "E2583", {"start": v(7.35, -23.07) * mm, "end": v(7.45, -22.97) * mm});
            skLineSegment(sketch, "E2584", {"start": v(7.45, -22.97) * mm, "end": v(7.57, -22.88) * mm});
            skLineSegment(sketch, "E2585", {"start": v(7.57, -22.88) * mm, "end": v(7.7, -22.81) * mm});
            skLineSegment(sketch, "E2586", {"start": v(4.72, -23.2) * mm, "end": v(4.8, -23.07) * mm});
            skLineSegment(sketch, "E2587", {"start": v(4.8, -23.07) * mm, "end": v(4.91, -22.97) * mm});
            skLineSegment(sketch, "E2588", {"start": v(4.91, -22.97) * mm, "end": v(5.03, -22.88) * mm});
            skLineSegment(sketch, "E2589", {"start": v(5.03, -22.88) * mm, "end": v(5.17, -22.81) * mm});
            skLineSegment(sketch, "E2590", {"start": v(5.17, -22.81) * mm, "end": v(5.3, -22.76) * mm});
            skLineSegment(sketch, "E2591", {"start": v(5.3, -22.76) * mm, "end": v(5.46, -22.74) * mm});
            skLineSegment(sketch, "E2592", {"start": v(5.46, -22.74) * mm, "end": v(5.6, -22.74) * mm});
            skLineSegment(sketch, "E2593", {"start": v(5.6, -22.74) * mm, "end": v(5.75, -22.76) * mm});
            skLineSegment(sketch, "E2594", {"start": v(5.75, -22.76) * mm, "end": v(5.9, -22.81) * mm});
            skLineSegment(sketch, "E2595", {"start": v(5.9, -22.81) * mm, "end": v(6.03, -22.88) * mm});
            skLineSegment(sketch, "E2596", {"start": v(6.03, -22.88) * mm, "end": v(6.15, -22.97) * mm});
            skLineSegment(sketch, "E2597", {"start": v(6.15, -22.97) * mm, "end": v(6.25, -23.07) * mm});
            skLineSegment(sketch, "E2598", {"start": v(6.25, -23.07) * mm, "end": v(6.34, -23.2) * mm});
            skLineSegment(sketch, "E2599", {"start": v(6.34, -23.2) * mm, "end": v(6.4, -23.32) * mm});
            skLineSegment(sketch, "E2600", {"start": v(6.4, -23.32) * mm, "end": v(6.45, -23.47) * mm});
            skLineSegment(sketch, "E2601", {"start": v(6.45, -23.47) * mm, "end": v(6.48, -23.61) * mm});
            skLineSegment(sketch, "E2602", {"start": v(6.48, -23.61) * mm, "end": v(6.48, -23.76) * mm});
            skLineSegment(sketch, "E2603", {"start": v(2.18, -23.2) * mm, "end": v(2.27, -23.07) * mm});
            skLineSegment(sketch, "E2604", {"start": v(2.27, -23.07) * mm, "end": v(2.37, -22.97) * mm});
            skLineSegment(sketch, "E2605", {"start": v(2.37, -22.97) * mm, "end": v(2.5, -22.88) * mm});
            skLineSegment(sketch, "E2606", {"start": v(2.5, -22.88) * mm, "end": v(2.63, -22.81) * mm});
            skLineSegment(sketch, "E2607", {"start": v(2.63, -22.81) * mm, "end": v(2.77, -22.76) * mm});
            skLineSegment(sketch, "E2608", {"start": v(2.77, -22.76) * mm, "end": v(2.92, -22.74) * mm});
            skLineSegment(sketch, "E2609", {"start": v(2.92, -22.74) * mm, "end": v(3.07, -22.74) * mm});
            skLineSegment(sketch, "E2610", {"start": v(3.07, -22.74) * mm, "end": v(3.21, -22.76) * mm});
            skLineSegment(sketch, "E2611", {"start": v(3.21, -22.76) * mm, "end": v(3.36, -22.81) * mm});
            skLineSegment(sketch, "E2612", {"start": v(3.36, -22.81) * mm, "end": v(3.49, -22.88) * mm});
            skLineSegment(sketch, "E2613", {"start": v(3.49, -22.88) * mm, "end": v(3.6, -22.97) * mm});
            skLineSegment(sketch, "E2614", {"start": v(3.6, -22.97) * mm, "end": v(3.71, -23.07) * mm});
            skLineSegment(sketch, "E2615", {"start": v(3.71, -23.07) * mm, "end": v(3.8, -23.2) * mm});
            skLineSegment(sketch, "E2616", {"start": v(3.8, -23.2) * mm, "end": v(3.87, -23.32) * mm});
            skLineSegment(sketch, "E2617", {"start": v(3.87, -23.32) * mm, "end": v(3.91, -23.47) * mm});
            skLineSegment(sketch, "E2618", {"start": v(3.91, -23.47) * mm, "end": v(3.94, -23.61) * mm});
            skLineSegment(sketch, "E2619", {"start": v(3.94, -23.61) * mm, "end": v(3.94, -23.76) * mm});
            skLineSegment(sketch, "E2620", {"start": v(-0.36, -23.2) * mm, "end": v(-0.27, -23.07) * mm});
            skLineSegment(sketch, "E2621", {"start": v(-0.27, -23.07) * mm, "end": v(-0.17, -22.97) * mm});
            skLineSegment(sketch, "E2622", {"start": v(-0.17, -22.97) * mm, "end": v(-0.05, -22.88) * mm});
            skLineSegment(sketch, "E2623", {"start": v(-0.05, -22.88) * mm, "end": v(0.09, -22.81) * mm});
            skLineSegment(sketch, "E2624", {"start": v(-2.9, -23.2) * mm, "end": v(-2.81, -23.07) * mm});
            skLineSegment(sketch, "E2625", {"start": v(-2.81, -23.07) * mm, "end": v(-2.7, -22.97) * mm});
            skLineSegment(sketch, "E2626", {"start": v(-2.7, -22.97) * mm, "end": v(-2.59, -22.88) * mm});
            skLineSegment(sketch, "E2627", {"start": v(-2.59, -22.88) * mm, "end": v(-2.45, -22.81) * mm});
            skLineSegment(sketch, "E2628", {"start": v(-10.52, -23.2) * mm, "end": v(-10.43, -23.07) * mm});
            skLineSegment(sketch, "E2629", {"start": v(-10.43, -23.07) * mm, "end": v(-10.33, -22.97) * mm});
            skLineSegment(sketch, "E2630", {"start": v(-10.33, -22.97) * mm, "end": v(-10.2, -22.88) * mm});
            skLineSegment(sketch, "E2631", {"start": v(-10.2, -22.88) * mm, "end": v(-10.07, -22.81) * mm});
            skLineSegment(sketch, "E2632", {"start": v(-10.07, -22.81) * mm, "end": v(-9.93, -22.76) * mm});
            skLineSegment(sketch, "E2633", {"start": v(-9.93, -22.76) * mm, "end": v(-9.78, -22.74) * mm});
            skLineSegment(sketch, "E2634", {"start": v(-9.78, -22.74) * mm, "end": v(-9.63, -22.74) * mm});
            skLineSegment(sketch, "E2635", {"start": v(-9.63, -22.74) * mm, "end": v(-9.49, -22.76) * mm});
            skLineSegment(sketch, "E2636", {"start": v(-9.49, -22.76) * mm, "end": v(-9.34, -22.81) * mm});
            skLineSegment(sketch, "E2637", {"start": v(-9.34, -22.81) * mm, "end": v(-9.21, -22.88) * mm});
            skLineSegment(sketch, "E2638", {"start": v(-9.21, -22.88) * mm, "end": v(-9.1, -22.97) * mm});
            skLineSegment(sketch, "E2639", {"start": v(-9.1, -22.97) * mm, "end": v(-8.99, -23.07) * mm});
            skLineSegment(sketch, "E2640", {"start": v(-8.99, -23.07) * mm, "end": v(-8.9, -23.2) * mm});
            skLineSegment(sketch, "E2641", {"start": v(-8.9, -23.2) * mm, "end": v(-8.83, -23.32) * mm});
            skLineSegment(sketch, "E2642", {"start": v(-8.83, -23.32) * mm, "end": v(-8.79, -23.47) * mm});
            skLineSegment(sketch, "E2643", {"start": v(-8.79, -23.47) * mm, "end": v(-8.76, -23.61) * mm});
            skLineSegment(sketch, "E2644", {"start": v(-8.76, -23.61) * mm, "end": v(-8.76, -23.76) * mm});
            skLineSegment(sketch, "E2645", {"start": v(-13.06, -23.2) * mm, "end": v(-12.97, -23.07) * mm});
            skLineSegment(sketch, "E2646", {"start": v(-12.97, -23.07) * mm, "end": v(-12.87, -22.97) * mm});
            skLineSegment(sketch, "E2647", {"start": v(-12.87, -22.97) * mm, "end": v(-12.75, -22.88) * mm});
            skLineSegment(sketch, "E2648", {"start": v(-12.75, -22.88) * mm, "end": v(-12.61, -22.81) * mm});
            skLineSegment(sketch, "E2649", {"start": v(-12.61, -22.81) * mm, "end": v(-12.47, -22.76) * mm});
            skLineSegment(sketch, "E2650", {"start": v(-12.47, -22.76) * mm, "end": v(-12.32, -22.74) * mm});
            skLineSegment(sketch, "E2651", {"start": v(-12.32, -22.74) * mm, "end": v(-12.17, -22.74) * mm});
            skLineSegment(sketch, "E2652", {"start": v(-12.17, -22.74) * mm, "end": v(-12.03, -22.76) * mm});
            skLineSegment(sketch, "E2653", {"start": v(-12.03, -22.76) * mm, "end": v(-11.88, -22.81) * mm});
            skLineSegment(sketch, "E2654", {"start": v(-11.88, -22.81) * mm, "end": v(-11.75, -22.88) * mm});
            skLineSegment(sketch, "E2655", {"start": v(-11.75, -22.88) * mm, "end": v(-11.63, -22.97) * mm});
            skLineSegment(sketch, "E2656", {"start": v(-11.63, -22.97) * mm, "end": v(-11.53, -23.07) * mm});
            skLineSegment(sketch, "E2657", {"start": v(-11.53, -23.07) * mm, "end": v(-11.44, -23.2) * mm});
            skLineSegment(sketch, "E2658", {"start": v(-11.44, -23.2) * mm, "end": v(-11.37, -23.32) * mm});
            skLineSegment(sketch, "E2659", {"start": v(-11.37, -23.32) * mm, "end": v(-11.33, -23.47) * mm});
            skLineSegment(sketch, "E2660", {"start": v(-11.33, -23.47) * mm, "end": v(-11.3, -23.61) * mm});
            skLineSegment(sketch, "E2661", {"start": v(-11.3, -23.61) * mm, "end": v(-11.3, -23.76) * mm});
            skLineSegment(sketch, "E2662", {"start": v(-15.4, -0.07) * mm, "end": v(-15.49, -0.11) * mm});
            skLineSegment(sketch, "E2663", {"start": v(-15.49, -0.11) * mm, "end": v(-14.97, -0.12) * mm});
            skLineSegment(sketch, "E2664", {"start": v(-14.97, -0.12) * mm, "end": v(-14.9, -0.15) * mm});
            skLineSegment(sketch, "E2665", {"start": v(-14.9, -0.15) * mm, "end": v(-14.57, -0.49) * mm});
            skLineSegment(sketch, "E2666", {"start": v(-14.57, -0.49) * mm, "end": v(-14.49, -0.46) * mm});
            skLineSegment(sketch, "E2667", {"start": v(-14.49, -0.46) * mm, "end": v(-14.38, -0.44) * mm});
            skLineSegment(sketch, "E2668", {"start": v(-14.38, -0.44) * mm, "end": v(-14.26, -0.46) * mm});
            skLineSegment(sketch, "E2669", {"start": v(-14.26, -0.46) * mm, "end": v(-14.16, -0.5) * mm});
            skLineSegment(sketch, "E2670", {"start": v(-14.16, -0.5) * mm, "end": v(-14.06, -0.56) * mm});
            skLineSegment(sketch, "E2671", {"start": v(-14.06, -0.56) * mm, "end": v(-13.99, -0.64) * mm});
            skLineSegment(sketch, "E2672", {"start": v(-13.99, -0.64) * mm, "end": v(-13.93, -0.74) * mm});
            skLineSegment(sketch, "E2673", {"start": v(-13.93, -0.74) * mm, "end": v(-13.9, -0.85) * mm});
            skLineSegment(sketch, "E2674", {"start": v(-13.9, -0.85) * mm, "end": v(-13.9, -0.97) * mm});
            skLineSegment(sketch, "E2675", {"start": v(-13.9, -0.97) * mm, "end": v(-13.92, -1.08) * mm});
            skLineSegment(sketch, "E2676", {"start": v(-13.92, -1.08) * mm, "end": v(-13.96, -1.18) * mm});
            skLineSegment(sketch, "E2677", {"start": v(-13.96, -1.18) * mm, "end": v(-14.04, -1.27) * mm});
            skLineSegment(sketch, "E2678", {"start": v(-14.04, -1.27) * mm, "end": v(-14.12, -1.34) * mm});
            skLineSegment(sketch, "E2679", {"start": v(-14.12, -1.34) * mm, "end": v(-14.23, -1.39) * mm});
            skLineSegment(sketch, "E2680", {"start": v(-14.23, -1.39) * mm, "end": v(-14.34, -1.4) * mm});
            skLineSegment(sketch, "E2681", {"start": v(-14.34, -1.4) * mm, "end": v(-14.45, -1.4) * mm});
            skLineSegment(sketch, "E2682", {"start": v(-14.45, -1.4) * mm, "end": v(-14.56, -1.37) * mm});
            skLineSegment(sketch, "E2683", {"start": v(-14.56, -1.37) * mm, "end": v(-14.66, -1.32) * mm});
            skLineSegment(sketch, "E2684", {"start": v(-14.66, -1.32) * mm, "end": v(-14.74, -1.24) * mm});
            skLineSegment(sketch, "E2685", {"start": v(-14.74, -1.24) * mm, "end": v(-14.8, -1.15) * mm});
            skLineSegment(sketch, "E2686", {"start": v(-14.8, -1.15) * mm, "end": v(-14.85, -1.04) * mm});
            skLineSegment(sketch, "E2687", {"start": v(-14.85, -1.04) * mm, "end": v(-14.86, -0.93) * mm});
            skLineSegment(sketch, "E2688", {"start": v(-14.86, -0.93) * mm, "end": v(-14.85, -0.81) * mm});
            skLineSegment(sketch, "E2689", {"start": v(-14.85, -0.81) * mm, "end": v(-14.82, -0.73) * mm});
            skLineSegment(sketch, "E2690", {"start": v(-14.82, -0.73) * mm, "end": v(-15.09, -0.47) * mm});
            skLineSegment(sketch, "E2691", {"start": v(-15.09, -0.47) * mm, "end": v(-15.5, -0.47) * mm});
            skLineSegment(sketch, "E2692", {"start": v(-15.5, -0.47) * mm, "end": v(-15.4, -0.52) * mm});
            skLineSegment(sketch, "E2693", {"start": v(-15.4, -0.52) * mm, "end": v(-15.3, -0.58) * mm});
            skLineSegment(sketch, "E2694", {"start": v(-15.3, -0.58) * mm, "end": v(-15.23, -0.68) * mm});
            skLineSegment(sketch, "E2695", {"start": v(-15.23, -0.68) * mm, "end": v(-15.19, -0.78) * mm});
            skLineSegment(sketch, "E2696", {"start": v(-15.19, -0.78) * mm, "end": v(-15.17, -0.89) * mm});
            skLineSegment(sketch, "E2697", {"start": v(-15.17, -0.89) * mm, "end": v(-15.17, -1) * mm});
            skLineSegment(sketch, "E2698", {"start": v(-15.17, -1) * mm, "end": v(-15.2, -1.11) * mm});
            skLineSegment(sketch, "E2699", {"start": v(-15.2, -1.11) * mm, "end": v(-15.26, -1.21) * mm});
            skLineSegment(sketch, "E2700", {"start": v(-15.26, -1.21) * mm, "end": v(-15.33, -1.3) * mm});
            skLineSegment(sketch, "E2701", {"start": v(-15.33, -1.3) * mm, "end": v(-15.43, -1.36) * mm});
            skLineSegment(sketch, "E2702", {"start": v(-15.43, -1.36) * mm, "end": v(-15.53, -1.4) * mm});
            skLineSegment(sketch, "E2703", {"start": v(-15.53, -1.4) * mm, "end": v(-15.65, -1.4) * mm});
            skLineSegment(sketch, "E2704", {"start": v(-15.65, -1.4) * mm, "end": v(-15.76, -1.4) * mm});
            skLineSegment(sketch, "E2705", {"start": v(-15.76, -1.4) * mm, "end": v(-15.86, -1.36) * mm});
            skLineSegment(sketch, "E2706", {"start": v(-15.86, -1.36) * mm, "end": v(-15.96, -1.3) * mm});
            skLineSegment(sketch, "E2707", {"start": v(-15.96, -1.3) * mm, "end": v(-16.04, -1.21) * mm});
            skLineSegment(sketch, "E2708", {"start": v(-16.04, -1.21) * mm, "end": v(-16.1, -1.11) * mm});
            skLineSegment(sketch, "E2709", {"start": v(-16.1, -1.11) * mm, "end": v(-16.11, -1.05) * mm});
            skLineSegment(sketch, "E2710", {"start": v(-16.11, -1.05) * mm, "end": v(-20.94, -1.04) * mm});
            skLineSegment(sketch, "E2711", {"start": v(-20.94, -1.04) * mm, "end": v(-21, -1.01) * mm});
            skLineSegment(sketch, "E2712", {"start": v(-21, -1.01) * mm, "end": v(-21.5, -0.52) * mm});
            skLineSegment(sketch, "E2713", {"start": v(-21.5, -0.52) * mm, "end": v(-25.27, 3.26) * mm});
            skLineSegment(sketch, "E2714", {"start": v(-25.27, 3.26) * mm, "end": v(-25.3, 3.32) * mm});
            skLineSegment(sketch, "E2715", {"start": v(-25.3, 3.32) * mm, "end": v(-25.3, 4.03) * mm});
            skLineSegment(sketch, "E2716", {"start": v(-25.3, 4.03) * mm, "end": v(-25.3, 10.98) * mm});
            skLineSegment(sketch, "E2717", {"start": v(-25.3, 10.98) * mm, "end": v(-25.26, 11.04) * mm});
            skLineSegment(sketch, "E2718", {"start": v(-25.26, 11.04) * mm, "end": v(-24.77, 11.54) * mm});
            skLineSegment(sketch, "E2719", {"start": v(-24.77, 11.54) * mm, "end": v(-18.83, 17.47) * mm});
            skLineSegment(sketch, "E2720", {"start": v(-18.83, 17.47) * mm, "end": v(-18.77, 17.5) * mm});
            skLineSegment(sketch, "E2721", {"start": v(-18.77, 17.5) * mm, "end": v(-18.06, 17.5) * mm});
            skLineSegment(sketch, "E2722", {"start": v(-18.06, 17.5) * mm, "end": v(35.67, 17.5) * mm});
            skLineSegment(sketch, "E2723", {"start": v(35.67, 17.5) * mm, "end": v(35.73, 17.68) * mm});
            skLineSegment(sketch, "E2724", {"start": v(35.68, 17.1) * mm, "end": v(35.68, 17.14) * mm});
            skLineSegment(sketch, "E2725", {"start": v(35.68, 17.14) * mm, "end": v(-18.66, 17.14) * mm});
            skLineSegment(sketch, "E2726", {"start": v(-18.66, 17.14) * mm, "end": v(-24.94, 10.86) * mm});
            skLineSegment(sketch, "E2727", {"start": v(-24.94, 10.86) * mm, "end": v(-24.94, 3.42) * mm});
            skLineSegment(sketch, "E2728", {"start": v(-24.94, 3.42) * mm, "end": v(-20.83, -0.7) * mm});
            skLineSegment(sketch, "E2729", {"start": v(-20.83, -0.7) * mm, "end": v(-16.3, -0.7) * mm});
            skLineSegment(sketch, "E2730", {"start": v(-16.3, -0.7) * mm, "end": v(-16.07, -0.7) * mm});
            skLineSegment(sketch, "E2731", {"start": v(-16.07, -0.7) * mm, "end": v(-15.99, -0.58) * mm});
            skLineSegment(sketch, "E2732", {"start": v(-15.8, -0.47) * mm, "end": v(-20.32, -0.46) * mm});
            skLineSegment(sketch, "E2733", {"start": v(-20.32, -0.46) * mm, "end": v(-20.38, -0.43) * mm});
            skLineSegment(sketch, "E2734", {"start": v(-20.38, -0.43) * mm, "end": v(-20.88, 0.06) * mm});
            skLineSegment(sketch, "E2735", {"start": v(-20.88, 0.06) * mm, "end": v(-24.49, 3.67) * mm});
            skLineSegment(sketch, "E2736", {"start": v(-24.49, 3.67) * mm, "end": v(-24.5, 3.74) * mm});
            skLineSegment(sketch, "E2737", {"start": v(-24.5, 3.74) * mm, "end": v(-24.51, 4.44) * mm});
            skLineSegment(sketch, "E2738", {"start": v(-24.51, 4.44) * mm, "end": v(-24.5, 10.55) * mm});
            skLineSegment(sketch, "E2739", {"start": v(-24.5, 10.55) * mm, "end": v(-24.48, 10.6) * mm});
            skLineSegment(sketch, "E2740", {"start": v(-24.48, 10.6) * mm, "end": v(-23.98, 11.1) * mm});
            skLineSegment(sketch, "E2741", {"start": v(-23.98, 11.1) * mm, "end": v(-20.15, 14.93) * mm});
            skLineSegment(sketch, "E2742", {"start": v(-20.15, 14.93) * mm, "end": v(-20.08, 14.96) * mm});
            skLineSegment(sketch, "E2743", {"start": v(-20.08, 14.96) * mm, "end": v(-19.38, 14.96) * mm});
            skLineSegment(sketch, "E2744", {"start": v(-19.38, 14.96) * mm, "end": v(35.67, 14.96) * mm});
            skLineSegment(sketch, "E2745", {"start": v(35.67, 14.96) * mm, "end": v(35.73, 15.14) * mm});
            skLineSegment(sketch, "E2746", {"start": v(35.68, 14.56) * mm, "end": v(35.68, 14.6) * mm});
            skLineSegment(sketch, "E2747", {"start": v(35.68, 14.6) * mm, "end": v(-19.98, 14.6) * mm});
            skLineSegment(sketch, "E2748", {"start": v(-19.98, 14.6) * mm, "end": v(-24.16, 10.43) * mm});
            skLineSegment(sketch, "E2749", {"start": v(-24.16, 10.43) * mm, "end": v(-24.16, 3.84) * mm});
            skLineSegment(sketch, "E2750", {"start": v(-24.16, 3.84) * mm, "end": v(-20.2, -0.11) * mm});
            skLineSegment(sketch, "E2751", {"start": v(-20.2, -0.11) * mm, "end": v(-15.8, -0.11) * mm});
            skLineSegment(sketch, "E2752", {"start": v(-15.8, -0.11) * mm, "end": v(-15.9, -0.07) * mm});
            skLineSegment(sketch, "E2753", {"start": v(-15.9, -0.07) * mm, "end": v(-15.99, 0) * mm});
            skLineSegment(sketch, "E2754", {"start": v(-15.99, 0) * mm, "end": v(-16.06, 0.1) * mm});
            skLineSegment(sketch, "E2755", {"start": v(-16.06, 0.1) * mm, "end": v(-16.1, 0.2) * mm});
            skLineSegment(sketch, "E2756", {"start": v(-16.1, 0.2) * mm, "end": v(-16.13, 0.3) * mm});
            skLineSegment(sketch, "E2757", {"start": v(-16.13, 0.3) * mm, "end": v(-16.13, 0.37) * mm});
            skLineSegment(sketch, "E2758", {"start": v(-16.13, 0.37) * mm, "end": v(-19.87, 0.37) * mm});
            skLineSegment(sketch, "E2759", {"start": v(-19.87, 0.37) * mm, "end": v(-19.93, 0.4) * mm});
            skLineSegment(sketch, "E2760", {"start": v(-19.93, 0.4) * mm, "end": v(-20.43, 0.9) * mm});
            skLineSegment(sketch, "E2761", {"start": v(-20.43, 0.9) * mm, "end": v(-23.12, 3.6) * mm});
            skLineSegment(sketch, "E2762", {"start": v(-23.12, 3.6) * mm, "end": v(-23.15, 3.67) * mm});
            skLineSegment(sketch, "E2763", {"start": v(-23.15, 3.67) * mm, "end": v(-23.15, 4.37) * mm});
            skLineSegment(sketch, "E2764", {"start": v(-23.15, 4.37) * mm, "end": v(-23.15, 9.64) * mm});
            skLineSegment(sketch, "E2765", {"start": v(-23.15, 9.64) * mm, "end": v(-23.12, 9.7) * mm});
            skLineSegment(sketch, "E2766", {"start": v(-23.12, 9.7) * mm, "end": v(-22.62, 10.2) * mm});
            skLineSegment(sketch, "E2767", {"start": v(-22.62, 10.2) * mm, "end": v(-20.43, 12.4) * mm});
            skLineSegment(sketch, "E2768", {"start": v(-20.43, 12.4) * mm, "end": v(-20.37, 12.42) * mm});
            skLineSegment(sketch, "E2769", {"start": v(-20.37, 12.42) * mm, "end": v(-19.66, 12.42) * mm});
            skLineSegment(sketch, "E2770", {"start": v(-19.66, 12.42) * mm, "end": v(35.67, 12.42) * mm});
            skLineSegment(sketch, "E2771", {"start": v(35.67, 12.42) * mm, "end": v(35.73, 12.6) * mm});
            skLineSegment(sketch, "E2772", {"start": v(35.68, 12.02) * mm, "end": v(35.68, 12.06) * mm});
            skLineSegment(sketch, "E2773", {"start": v(35.68, 12.06) * mm, "end": v(-20.26, 12.06) * mm});
            skLineSegment(sketch, "E2774", {"start": v(-20.26, 12.06) * mm, "end": v(-22.8, 9.53) * mm});
            skLineSegment(sketch, "E2775", {"start": v(-22.8, 9.53) * mm, "end": v(-22.8, 3.76) * mm});
            skLineSegment(sketch, "E2776", {"start": v(-22.8, 3.76) * mm, "end": v(-19.75, 0.72) * mm});
            skLineSegment(sketch, "E2777", {"start": v(-19.75, 0.72) * mm, "end": v(-15.95, 0.72) * mm});
            skLineSegment(sketch, "E2778", {"start": v(-15.95, 0.72) * mm, "end": v(-15.83, 0.79) * mm});
            skLineSegment(sketch, "E2779", {"start": v(-15.83, 0.79) * mm, "end": v(-15.72, 0.82) * mm});
            skLineSegment(sketch, "E2780", {"start": v(-15.72, 0.82) * mm, "end": v(-15.6, 0.83) * mm});
            skLineSegment(sketch, "E2781", {"start": v(-15.6, 0.83) * mm, "end": v(-15.5, 0.8) * mm});
            skLineSegment(sketch, "E2782", {"start": v(-15.5, 0.8) * mm, "end": v(-15.4, 0.75) * mm});
            skLineSegment(sketch, "E2783", {"start": v(-15.4, 0.75) * mm, "end": v(-15.3, 0.69) * mm});
            skLineSegment(sketch, "E2784", {"start": v(-15.3, 0.69) * mm, "end": v(-15.23, 0.6) * mm});
            skLineSegment(sketch, "E2785", {"start": v(-15.23, 0.6) * mm, "end": v(-15.19, 0.5) * mm});
            skLineSegment(sketch, "E2786", {"start": v(-15.19, 0.5) * mm, "end": v(-15.17, 0.38) * mm});
            skLineSegment(sketch, "E2787", {"start": v(-15.17, 0.38) * mm, "end": v(-15.17, 0.3) * mm});
            skLineSegment(sketch, "E2788", {"start": v(-13.9, 0.3) * mm, "end": v(-13.92, 0.2) * mm});
            skLineSegment(sketch, "E2789", {"start": v(-13.92, 0.2) * mm, "end": v(-13.96, 0.1) * mm});
            skLineSegment(sketch, "E2790", {"start": v(-13.96, 0.1) * mm, "end": v(-14.04, 0) * mm});
            skLineSegment(sketch, "E2791", {"start": v(-14.04, 0) * mm, "end": v(-14.12, -0.07) * mm});
            skLineSegment(sketch, "E2792", {"start": v(-14.12, -0.07) * mm, "end": v(-14.23, -0.12) * mm});
            skLineSegment(sketch, "E2793", {"start": v(-14.23, -0.12) * mm, "end": v(-14.34, -0.14) * mm});
            skLineSegment(sketch, "E2794", {"start": v(-14.34, -0.14) * mm, "end": v(-14.45, -0.13) * mm});
            skLineSegment(sketch, "E2795", {"start": v(-14.45, -0.13) * mm, "end": v(-14.56, -0.1) * mm});
            skLineSegment(sketch, "E2796", {"start": v(-14.56, -0.1) * mm, "end": v(-14.66, -0.05) * mm});
            skLineSegment(sketch, "E2797", {"start": v(-14.66, -0.05) * mm, "end": v(-14.74, 0.03) * mm});
            skLineSegment(sketch, "E2798", {"start": v(-14.74, 0.03) * mm, "end": v(-14.8, 0.12) * mm});
            skLineSegment(sketch, "E2799", {"start": v(-14.8, 0.12) * mm, "end": v(-14.85, 0.23) * mm});
            skLineSegment(sketch, "E2800", {"start": v(-14.85, 0.23) * mm, "end": v(-14.86, 0.34) * mm});
            skLineSegment(sketch, "E2801", {"start": v(-14.86, 0.34) * mm, "end": v(-14.85, 0.46) * mm});
            skLineSegment(sketch, "E2802", {"start": v(-14.85, 0.46) * mm, "end": v(-14.82, 0.54) * mm});
            skLineSegment(sketch, "E2803", {"start": v(-14.82, 0.54) * mm, "end": v(-15.75, 1.46) * mm});
            skLineSegment(sketch, "E2804", {"start": v(-15.75, 1.46) * mm, "end": v(-19.02, 1.46) * mm});
            skLineSegment(sketch, "E2805", {"start": v(-19.02, 1.46) * mm, "end": v(-19.08, 1.49) * mm});
            skLineSegment(sketch, "E2806", {"start": v(-19.08, 1.49) * mm, "end": v(-19.12, 1.51) * mm});
            skLineSegment(sketch, "E2807", {"start": v(-19.12, 1.51) * mm, "end": v(-21.26, 3.66) * mm});
            skLineSegment(sketch, "E2808", {"start": v(-21.26, 3.66) * mm, "end": v(-21.29, 3.73) * mm});
            skLineSegment(sketch, "E2809", {"start": v(-21.29, 3.73) * mm, "end": v(-21.29, 4.43) * mm});
            skLineSegment(sketch, "E2810", {"start": v(-21.29, 4.43) * mm, "end": v(-21.28, 8.1) * mm});
            skLineSegment(sketch, "E2811", {"start": v(-21.28, 8.1) * mm, "end": v(-21.25, 8.17) * mm});
            skLineSegment(sketch, "E2812", {"start": v(-21.25, 8.17) * mm, "end": v(-20.76, 8.67) * mm});
            skLineSegment(sketch, "E2813", {"start": v(-20.76, 8.67) * mm, "end": v(-19.57, 9.85) * mm});
            skLineSegment(sketch, "E2814", {"start": v(-19.57, 9.85) * mm, "end": v(-19.5, 9.88) * mm});
            skLineSegment(sketch, "E2815", {"start": v(-19.5, 9.88) * mm, "end": v(-18.8, 9.88) * mm});
            skLineSegment(sketch, "E2816", {"start": v(-18.8, 9.88) * mm, "end": v(35.67, 9.88) * mm});
            skLineSegment(sketch, "E2817", {"start": v(35.67, 9.88) * mm, "end": v(35.73, 10.06) * mm});
            skLineSegment(sketch, "E2818", {"start": v(35.68, 9.48) * mm, "end": v(35.68, 9.52) * mm});
            skLineSegment(sketch, "E2819", {"start": v(35.68, 9.52) * mm, "end": v(-19.4, 9.52) * mm});
            skLineSegment(sketch, "E2820", {"start": v(-19.4, 9.52) * mm, "end": v(-20.93, 8) * mm});
            skLineSegment(sketch, "E2821", {"start": v(-20.93, 8) * mm, "end": v(-20.93, 3.83) * mm});
            skLineSegment(sketch, "E2822", {"start": v(-20.93, 3.83) * mm, "end": v(-19.35, 2.25) * mm});
            skLineSegment(sketch, "E2823", {"start": v(-19.35, 2.25) * mm, "end": v(-18.92, 1.81) * mm});
            skLineSegment(sketch, "E2824", {"start": v(-18.92, 1.81) * mm, "end": v(-15.63, 1.8) * mm});
            skLineSegment(sketch, "E2825", {"start": v(-15.63, 1.8) * mm, "end": v(-15.57, 1.78) * mm});
            skLineSegment(sketch, "E2826", {"start": v(-15.57, 1.78) * mm, "end": v(-15.06, 1.28) * mm});
            skLineSegment(sketch, "E2827", {"start": v(-15.06, 1.28) * mm, "end": v(-14.56, 0.78) * mm});
            skLineSegment(sketch, "E2828", {"start": v(-14.56, 0.78) * mm, "end": v(-14.49, 0.81) * mm});
            skLineSegment(sketch, "E2829", {"start": v(-14.49, 0.81) * mm, "end": v(-14.38, 0.83) * mm});
            skLineSegment(sketch, "E2830", {"start": v(-14.38, 0.83) * mm, "end": v(-14.26, 0.81) * mm});
            skLineSegment(sketch, "E2831", {"start": v(-14.26, 0.81) * mm, "end": v(-14.16, 0.77) * mm});
            skLineSegment(sketch, "E2832", {"start": v(-14.16, 0.77) * mm, "end": v(-14.06, 0.71) * mm});
            skLineSegment(sketch, "E2833", {"start": v(-14.06, 0.71) * mm, "end": v(-13.99, 0.63) * mm});
            skLineSegment(sketch, "E2834", {"start": v(-13.99, 0.63) * mm, "end": v(-13.93, 0.53) * mm});
            skLineSegment(sketch, "E2835", {"start": v(-13.93, 0.53) * mm, "end": v(-13.9, 0.42) * mm});
            skLineSegment(sketch, "E2836", {"start": v(-13.9, 0.42) * mm, "end": v(-13.9, 0.3) * mm});
            skLineSegment(sketch, "E2837", {"start": v(-13.9, -2.24) * mm, "end": v(-13.92, -2.35) * mm});
            skLineSegment(sketch, "E2838", {"start": v(-13.92, -2.35) * mm, "end": v(-13.96, -2.45) * mm});
            skLineSegment(sketch, "E2839", {"start": v(-13.96, -2.45) * mm, "end": v(-14.04, -2.54) * mm});
            skLineSegment(sketch, "E2840", {"start": v(-14.04, -2.54) * mm, "end": v(-14.12, -2.6) * mm});
            skLineSegment(sketch, "E2841", {"start": v(-14.12, -2.6) * mm, "end": v(-14.23, -2.66) * mm});
            skLineSegment(sketch, "E2842", {"start": v(-14.23, -2.66) * mm, "end": v(-14.34, -2.68) * mm});
            skLineSegment(sketch, "E2843", {"start": v(-14.34, -2.68) * mm, "end": v(-14.45, -2.67) * mm});
            skLineSegment(sketch, "E2844", {"start": v(-14.45, -2.67) * mm, "end": v(-14.57, -2.64) * mm});
            skLineSegment(sketch, "E2845", {"start": v(-14.57, -2.64) * mm, "end": v(-17.29, -5.36) * mm});
            skLineSegment(sketch, "E2846", {"start": v(-17.29, -5.36) * mm, "end": v(-17.35, -5.39) * mm});
            skLineSegment(sketch, "E2847", {"start": v(-17.35, -5.39) * mm, "end": v(-17.4, -5.39) * mm});
            skLineSegment(sketch, "E2848", {"start": v(-17.4, -5.39) * mm, "end": v(-18.74, -5.39) * mm});
            skLineSegment(sketch, "E2849", {"start": v(-18.74, -5.39) * mm, "end": v(-18.8, -5.36) * mm});
            skLineSegment(sketch, "E2850", {"start": v(-18.8, -5.36) * mm, "end": v(-19.3, -4.86) * mm});
            skLineSegment(sketch, "E2851", {"start": v(-19.3, -4.86) * mm, "end": v(-26.53, 2.37) * mm});
            skLineSegment(sketch, "E2852", {"start": v(-26.53, 2.37) * mm, "end": v(-26.56, 2.44) * mm});
            skLineSegment(sketch, "E2853", {"start": v(-26.56, 2.44) * mm, "end": v(-26.56, 3.14) * mm});
            skLineSegment(sketch, "E2854", {"start": v(-26.56, 3.14) * mm, "end": v(-26.55, 10.8) * mm});
            skLineSegment(sketch, "E2855", {"start": v(-26.55, 10.8) * mm, "end": v(-26.52, 10.87) * mm});
            skLineSegment(sketch, "E2856", {"start": v(-26.52, 10.87) * mm, "end": v(-26.03, 11.37) * mm});
            skLineSegment(sketch, "E2857", {"start": v(-26.03, 11.37) * mm, "end": v(-17.38, 20.01) * mm});
            skLineSegment(sketch, "E2858", {"start": v(-17.38, 20.01) * mm, "end": v(-17.31, 20.04) * mm});
            skLineSegment(sketch, "E2859", {"start": v(-17.31, 20.04) * mm, "end": v(-16.6, 20.04) * mm});
            skLineSegment(sketch, "E2860", {"start": v(-16.6, 20.04) * mm, "end": v(35.67, 20.04) * mm});
            skLineSegment(sketch, "E2861", {"start": v(35.67, 20.04) * mm, "end": v(35.73, 20.22) * mm});
            skLineSegment(sketch, "E2862", {"start": v(35.68, 19.64) * mm, "end": v(35.68, 19.68) * mm});
            skLineSegment(sketch, "E2863", {"start": v(35.68, 19.68) * mm, "end": v(-17.2, 19.68) * mm});
            skLineSegment(sketch, "E2864", {"start": v(-17.2, 19.68) * mm, "end": v(-26.2, 10.69) * mm});
            skLineSegment(sketch, "E2865", {"start": v(-26.2, 10.69) * mm, "end": v(-26.2, 9.55) * mm});
            skLineSegment(sketch, "E2866", {"start": v(-26.2, 9.55) * mm, "end": v(-26.2, 2.54) * mm});
            skLineSegment(sketch, "E2867", {"start": v(-26.2, 2.54) * mm, "end": v(-20.7, -2.96) * mm});
            skLineSegment(sketch, "E2868", {"start": v(-20.7, -2.96) * mm, "end": v(-18.62, -5.04) * mm});
            skLineSegment(sketch, "E2869", {"start": v(-18.62, -5.04) * mm, "end": v(-17.47, -5.03) * mm});
            skLineSegment(sketch, "E2870", {"start": v(-17.47, -5.03) * mm, "end": v(-14.82, -2.4) * mm});
            skLineSegment(sketch, "E2871", {"start": v(-14.82, -2.4) * mm, "end": v(-14.85, -2.27) * mm});
            skLineSegment(sketch, "E2872", {"start": v(-13.95, -1.98) * mm, "end": v(-13.9, -2.08) * mm});
            skLineSegment(sketch, "E2873", {"start": v(-13.9, -2.08) * mm, "end": v(-13.9, -2.2) * mm});
            skLineSegment(sketch, "E2874", {"start": v(-13.9, -2.2) * mm, "end": v(-13.9, -2.24) * mm});
            skLineSegment(sketch, "E2875", {"start": v(35.71, -9.04) * mm, "end": v(37.48, -9.04) * mm});
            skLineSegment(sketch, "E2876", {"start": v(35.58, -10.94) * mm, "end": v(35.58, -9.04) * mm});
            skLineSegment(sketch, "E2877", {"start": v(35.58, -9.04) * mm, "end": v(35.71, -9.04) * mm});
            skLineSegment(sketch, "E2878", {"start": v(35.72, -12.04) * mm, "end": v(35.8, -11.92) * mm});
            skLineSegment(sketch, "E2879", {"start": v(35.8, -11.92) * mm, "end": v(35.91, -11.81) * mm});
            skLineSegment(sketch, "E2880", {"start": v(35.91, -11.81) * mm, "end": v(36.03, -11.72) * mm});
            skLineSegment(sketch, "E2881", {"start": v(36.03, -11.72) * mm, "end": v(36.17, -11.65) * mm});
            skLineSegment(sketch, "E2882", {"start": v(13.4, 4.77) * mm, "end": v(15.17, 4.77) * mm});
            skLineSegment(sketch, "E2883", {"start": v(15.95, 4.32) * mm, "end": v(16.04, 4.44) * mm});
            skLineSegment(sketch, "E2884", {"start": v(16.04, 4.44) * mm, "end": v(16.14, 4.54) * mm});
            skLineSegment(sketch, "E2885", {"start": v(16.14, 4.54) * mm, "end": v(16.27, 4.63) * mm});
            skLineSegment(sketch, "E2886", {"start": v(16.27, 4.63) * mm, "end": v(16.4, 4.7) * mm});
            skLineSegment(sketch, "E2887", {"start": v(16.4, 4.7) * mm, "end": v(16.54, 4.74) * mm});
            skLineSegment(sketch, "E2888", {"start": v(16.54, 4.74) * mm, "end": v(16.69, 4.77) * mm});
            skLineSegment(sketch, "E2889", {"start": v(16.69, 4.77) * mm, "end": v(16.84, 4.77) * mm});
            skLineSegment(sketch, "E2890", {"start": v(16.84, 4.77) * mm, "end": v(16.98, 4.74) * mm});
            skLineSegment(sketch, "E2891", {"start": v(16.98, 4.74) * mm, "end": v(17.13, 4.7) * mm});
            skLineSegment(sketch, "E2892", {"start": v(17.13, 4.7) * mm, "end": v(17.26, 4.63) * mm});
            skLineSegment(sketch, "E2893", {"start": v(17.26, 4.63) * mm, "end": v(17.38, 4.54) * mm});
            skLineSegment(sketch, "E2894", {"start": v(17.38, 4.54) * mm, "end": v(17.49, 4.44) * mm});
            skLineSegment(sketch, "E2895", {"start": v(17.49, 4.44) * mm, "end": v(17.57, 4.32) * mm});
            skLineSegment(sketch, "E2896", {"start": v(12.97, 24.64) * mm, "end": v(14.74, 24.64) * mm});
            skLineSegment(sketch, "E2897", {"start": v(14.74, 24.64) * mm, "end": v(14.74, 22.74) * mm});
            skLineSegment(sketch, "E2898", {"start": v(14.74, 22.74) * mm, "end": v(12.84, 22.74) * mm});
            skLineSegment(sketch, "E2899", {"start": v(12.84, 24.64) * mm, "end": v(12.97, 24.64) * mm});
            skLineSegment(sketch, "E2900", {"start": v(17.28, 23.61) * mm, "end": v(17.25, 23.46) * mm});
            skLineSegment(sketch, "E2901", {"start": v(17.25, 23.46) * mm, "end": v(17.2, 23.32) * mm});
            skLineSegment(sketch, "E2902", {"start": v(17.2, 23.32) * mm, "end": v(17.14, 23.2) * mm});
            skLineSegment(sketch, "E2903", {"start": v(17.14, 23.2) * mm, "end": v(17.05, 23.07) * mm});
            skLineSegment(sketch, "E2904", {"start": v(17.05, 23.07) * mm, "end": v(16.95, 22.96) * mm});
            skLineSegment(sketch, "E2905", {"start": v(16.95, 22.96) * mm, "end": v(16.83, 22.88) * mm});
            skLineSegment(sketch, "E2906", {"start": v(16.83, 22.88) * mm, "end": v(16.7, 22.8) * mm});
            skLineSegment(sketch, "E2907", {"start": v(16.7, 22.8) * mm, "end": v(16.55, 22.76) * mm});
            skLineSegment(sketch, "E2908", {"start": v(16.55, 22.76) * mm, "end": v(16.4, 22.74) * mm});
            skLineSegment(sketch, "E2909", {"start": v(16.4, 22.74) * mm, "end": v(16.26, 22.74) * mm});
            skLineSegment(sketch, "E2910", {"start": v(16.26, 22.74) * mm, "end": v(16.1, 22.76) * mm});
            skLineSegment(sketch, "E2911", {"start": v(16.1, 22.76) * mm, "end": v(15.97, 22.8) * mm});
            skLineSegment(sketch, "E2912", {"start": v(15.97, 22.8) * mm, "end": v(15.83, 22.88) * mm});
            skLineSegment(sketch, "E2913", {"start": v(17.25, 23.9) * mm, "end": v(17.28, 23.76) * mm});
            skLineSegment(sketch, "E2914", {"start": v(17.28, 23.76) * mm, "end": v(17.28, 23.61) * mm});
            skSolve(sketch);
        }
        {
            var Q0;
            Q0=makeQuery(id+"F0.imprint","IMPRINT",FACE,{"disambiguationData":[TD([[makeQuery(id+"F0.imprint","IMPRINT",EDGE,{"derivedFrom":sQuery(id+"F0.wireOp",EDGE,"E612")}),1.0]])]});
            var sketch = newSketch(context, id + "F1", { "sketchPlane" : qUnion([Q0])});
            skLineSegment(sketch, "E2915.0", {"start": v(38.1, 25.4) * mm, "end": v(-38.1, 25.4) * mm});
            skLineSegment(sketch, "E2915.1", {"start": v(38.1, -25.4) * mm, "end": v(38.1, 25.4) * mm});
            skLineSegment(sketch, "E2915.2", {"start": v(-38.1, -25.4) * mm, "end": v(38.1, -25.4) * mm});
            skLineSegment(sketch, "E2915.3", {"start": v(-38.1, 25.4) * mm, "end": v(-38.1, -25.4) * mm});
            skSolve(sketch);
        }
        {
            var Q0;
            Q0=makeQuery(id+"F1.imprint","IMPRINT",FACE,{"disambiguationData":[TD([[makeQuery(id+"F1.imprint","IMPRINT",EDGE,{"derivedFrom":sQuery(id+"F1.wireOp",EDGE,"E2915.0")}),1.0]])]});
            var sketch = newSketch(context, id + "F2", { "sketchPlane" : qUnion([Q0])});
            skLineSegment(sketch, "E2916.bottom", {"start": v(21.36, 5.36) * mm, "end": v(-23.09, 5.36) * mm});
            skLineSegment(sketch, "E2916.top", {"start": v(21.36, -7.34) * mm, "end": v(-23.09, -7.34) * mm});
            skLineSegment(sketch, "E2916.left", {"start": v(21.36, 5.36) * mm, "end": v(21.36, -7.34) * mm});
            skLineSegment(sketch, "E2916.right", {"start": v(-23.09, 5.36) * mm, "end": v(-23.09, -7.34) * mm});
            skLineSegment(sketch, "E2917", {"start": v(-23.09, -7.34) * mm, "end": v(21.36, 5.36) * mm, "construction": true});
            skLineSegment(sketch, "E2918", {"start": v(-23.09, 5.36) * mm, "end": v(21.36, -7.34) * mm, "construction": true});
            skPoint(sketch, "E2919", {"position": v(-0.86, -1) * mm});
            skSolve(sketch);
        }
        {
            var Q0;
            Q0=qSketchRegion(id+"F2",true);
            extrude(context, id + "F3", {"entities" : qUnion([Q0]), "depth" : 12.7 * mm, "offsetDistance" : 25.4 * mm});
        }
        {
            var Q0;
            Q0=makeQuery(id+"F3.opExtrude","CAP_FACE",FACE,{"disambiguationData":[OSD([sQuery(id+"F2.wireOp",EDGE,"E2916.bottom"),sQuery(id+"F2.wireOp",EDGE,"E2916.top"),sQuery(id+"F2.wireOp",EDGE,"E2916.left"),sQuery(id+"F2.wireOp",EDGE,"E2916.right")])],"isStart":false});
            var sketch = newSketch(context, id + "F4", { "sketchPlane" : qUnion([Q0])});
            skPoint(sketch, "E2920.0", {"position": v(-15.65, -2.2) * mm});
            skPoint(sketch, "E2920.1", {"position": v(-14.38, -2.2) * mm});
            skPoint(sketch, "E2920.2", {"position": v(-14.38, -0.93) * mm});
            skPoint(sketch, "E2920.3", {"position": v(-15.65, -0.93) * mm});
            skPoint(sketch, "E2920.4", {"position": v(-15.65, 0.34) * mm});
            skPoint(sketch, "E2920.5", {"position": v(-14.38, 0.34) * mm});
            skPoint(sketch, "E2921.0", {"position": v(-18.2, -6) * mm});
            skPoint(sketch, "E2921.1", {"position": v(-15.67, -6) * mm});
            skPoint(sketch, "E2921.2", {"position": v(-13.13, -6) * mm});
            skPoint(sketch, "E2922.0", {"position": v(-4.81, 0.95) * mm});
            skPoint(sketch, "E2923.0", {"position": v(5.3, -3.88) * mm});
            skPoint(sketch, "E2923.1", {"position": v(5.02, -2.5) * mm});
            skPoint(sketch, "E2923.2", {"position": v(6.14, 1.09) * mm});
            skPoint(sketch, "E2924.1", {"position": v(5.96, 3.5) * mm});
            skPoint(sketch, "E2924.2", {"position": v(8.79, 3.47) * mm});
            skPoint(sketch, "E2925.0", {"position": v(7.97, -6.18) * mm});
            skPoint(sketch, "E2925.1", {"position": v(15.12, -6.13) * mm});
            skPoint(sketch, "E2926.0", {"position": v(18.52, -0.2) * mm});
            skPoint(sketch, "E2927.0", {"position": v(16.76, 3.82) * mm});
            skPoint(sketch, "E2928.0", {"position": v(14.22, 3.82) * mm});
            skCircle(sketch, "E2929", {"center": v(-18.2, -6) * mm, "radius": 0.38 * mm});
            skCircle(sketch, "E2930", {"center": v(-15.67, -6) * mm, "radius": 0.38 * mm});
            skCircle(sketch, "E2931", {"center": v(-13.13, -6) * mm, "radius": 0.38 * mm});
            skCircle(sketch, "E2932", {"center": v(-14.38, -2.2) * mm, "radius": 0.38 * mm});
            skCircle(sketch, "E2933", {"center": v(-15.65, -2.2) * mm, "radius": 0.38 * mm});
            skCircle(sketch, "E2934", {"center": v(-15.65, -0.93) * mm, "radius": 0.38 * mm});
            skCircle(sketch, "E2935", {"center": v(-14.38, -0.93) * mm, "radius": 0.38 * mm});
            skCircle(sketch, "E2936", {"center": v(-14.38, 0.34) * mm, "radius": 0.38 * mm});
            skCircle(sketch, "E2937", {"center": v(-15.65, 0.34) * mm, "radius": 0.38 * mm});
            skCircle(sketch, "E2938", {"center": v(-4.81, 0.95) * mm, "radius": 0.38 * mm});
            skCircle(sketch, "E2939", {"center": v(5.3, -3.88) * mm, "radius": 0.38 * mm});
            skCircle(sketch, "E2940", {"center": v(5.02, -2.5) * mm, "radius": 0.38 * mm});
            skCircle(sketch, "E2941", {"center": v(6.14, 1.09) * mm, "radius": 0.38 * mm});
            skCircle(sketch, "E2942", {"center": v(5.96, 3.5) * mm, "radius": 0.38 * mm});
            skCircle(sketch, "E2943", {"center": v(8.79, 3.47) * mm, "radius": 0.38 * mm});
            skCircle(sketch, "E2944", {"center": v(18.52, -0.2) * mm, "radius": 0.38 * mm});
            skCircle(sketch, "E2945", {"center": v(16.76, 3.82) * mm, "radius": 0.38 * mm});
            skCircle(sketch, "E2946", {"center": v(14.22, 3.82) * mm, "radius": 0.38 * mm});
            skCircle(sketch, "E2947", {"center": v(7.97, -6.18) * mm, "radius": 0.38 * mm});
            skCircle(sketch, "E2948", {"center": v(15.12, -6.13) * mm, "radius": 0.38 * mm});
            skSolve(sketch);
        }
        {
            var Q0;
            Q0 = qSketchRegion(id + "F4", true);
            extrude(context, id + "F5", {"entities" : qUnion([Q0]), "operationType" : NewBodyOperationType.REMOVE, "endBound" : BoundingType.THROUGH_ALL, "oppositeDirection" : true, "depth" : 25.4 * mm, "offsetDistance" : 25.4 * mm});
        }
        {
            var Q0;
            Q0=makeQuery(id+"F3.opExtrude","CAP_FACE",FACE,{"disambiguationData":[OSD([sQuery(id+"F2.wireOp",EDGE,"E2916.bottom"),sQuery(id+"F2.wireOp",EDGE,"E2916.top"),sQuery(id+"F2.wireOp",EDGE,"E2916.left"),sQuery(id+"F2.wireOp",EDGE,"E2916.right")])],"isStart":false});
            var sketch = newSketch(context, id + "F6", { "sketchPlane" : qUnion([Q0])});
            skLineSegment(sketch, "E2949", {"start": v(4.22, -7.34) * mm, "end": v(10.57, -12.42) * mm});
            skLineSegment(sketch, "E2950", {"start": v(10.57, -12.42) * mm, "end": v(5.49, -12.42) * mm});
            skLineSegment(sketch, "E2951", {"start": v(5.49, -12.42) * mm, "end": v(-0.86, -7.34) * mm});
            skLineSegment(sketch, "E2952", {"start": v(-0.86, -7.34) * mm, "end": v(-7.21, -12.42) * mm});
            skLineSegment(sketch, "E2953", {"start": v(-7.21, -12.42) * mm, "end": v(-12.3, -12.42) * mm});
            skLineSegment(sketch, "E2954", {"start": v(-12.3, -12.42) * mm, "end": v(-5.94, -7.34) * mm});
            skLineSegment(sketch, "E2955", {"start": v(4.22, -7.34) * mm, "end": v(-0.86, -7.34) * mm});
            skLineSegment(sketch, "E2956", {"start": v(-0.86, -7.34) * mm, "end": v(-5.94, -7.34) * mm});
            skPoint(sketch, "E2957.0", {"position": v(-0.86, -1) * mm});
            skLineSegment(sketch, "E2958", {"start": v(-23.09, -7.34) * mm, "end": v(-5.94, -7.34) * mm});
            skLineSegment(sketch, "E2959", {"start": v(4.22, -7.34) * mm, "end": v(21.36, -7.34) * mm});
            skSolve(sketch);
        }
        {
            var Q0;
            Q0 = qSketchRegion(id + "F6", true);
            var Q1;
            Q1=makeQuery(id+"F3.opExtrude","CAP_FACE",FACE,{"disambiguationData":[OSD([sQuery(id+"F2.wireOp",EDGE,"E2916.bottom"),sQuery(id+"F2.wireOp",EDGE,"E2916.top"),sQuery(id+"F2.wireOp",EDGE,"E2916.left"),sQuery(id+"F2.wireOp",EDGE,"E2916.right")])],"isStart":true});
            var Q2;
            Q2=makeQuery(id+"F3.opExtrude","SWEPT_BODY",BODY,{"disambiguationData":[OSD([sQuery(id+"F2.wireOp",EDGE,"E2916.bottom"),sQuery(id+"F2.wireOp",EDGE,"E2916.top"),sQuery(id+"F2.wireOp",EDGE,"E2916.left"),sQuery(id+"F2.wireOp",EDGE,"E2916.right")])]});
            extrude(context, id + "F7", {"entities" : qUnion([Q0]), "operationType" : NewBodyOperationType.ADD, "endBound" : BoundingType.UP_TO_SURFACE, "oppositeDirection" : true, "depth" : 25.4 * mm, "endBoundEntityFace" : qUnion([Q1]), "endBoundEntityBody" : qUnion([Q2]), "offsetDistance" : 25.4 * mm});
        }
    });
